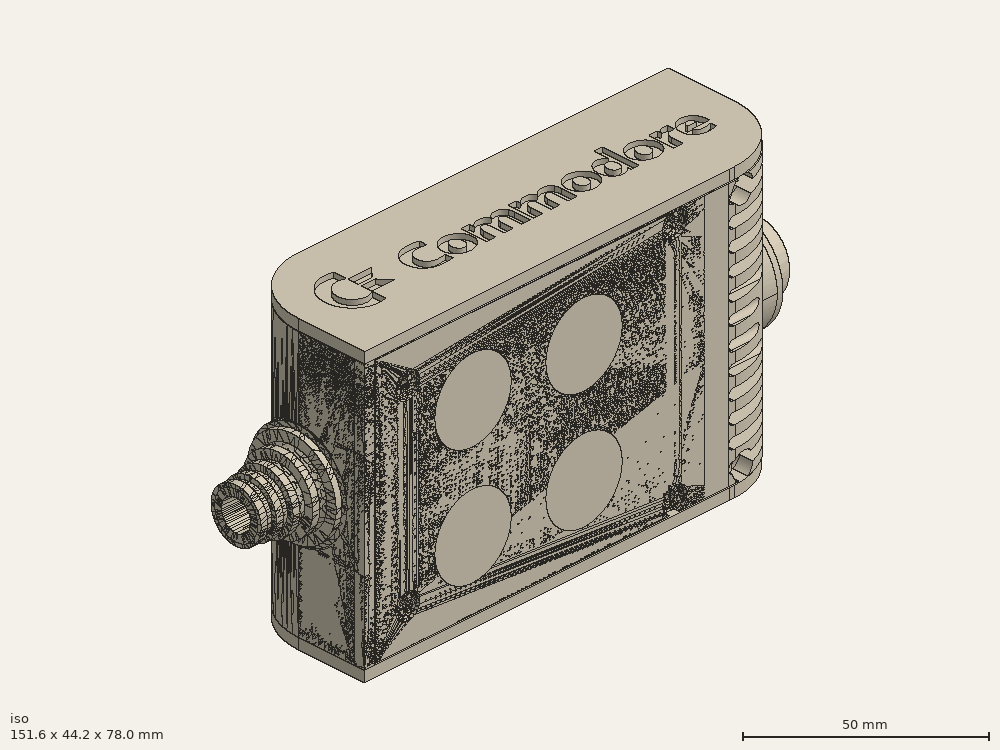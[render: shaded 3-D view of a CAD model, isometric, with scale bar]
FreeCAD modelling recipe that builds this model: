
FCSTD DOCUMENT  (FreeCAD 0.19R0.19.2)
Label: enclosure_210FCStd
License: All rights reserved
LicenseURL: http://en.wikipedia.org/wiki/All_rights_reserved
objects: Part::Revolution×152, Part::MultiFuse×146, Part::Feature×146, Sketcher::SketchObject×84, Part::Cut×72, Part::Cylinder×70, Part::Extrusion×69, Part::Fillet×58, Part::Box×36, App::MeasureDistance×4, Part::FeaturePython×2, Image::ImagePlane×1, PartDesign::Body×1, Part::Mirroring×1
note: 837 computed .brp shape members not serialized (recipe doc carries the construction recipe); baked Part::Feature solids carry a one-line shape summary decoded from their .brp

FEATURE [Sketcher::SketchObject] Sketch  label="topSketch"
  FullyConstrained = true
  sketch-geometry (20):
    g0: LineSegment StartX=5.21097e-06 StartY=3 StartZ=0 EndX=5.21097e-06 EndY=19 EndZ=0
    g1: ArcOfCircle CenterX=19 CenterY=19 CenterZ=0 NormalX=0 NormalY=0 NormalZ=1 AngleXU=0 Radius=19 StartAngle=1.5708 EndAngle=3.14159
    g2: ArcOfCircle CenterX=19 CenterY=19 CenterZ=0 NormalX=0 NormalY=0 NormalZ=1 AngleXU=0 Radius=16 StartAngle=1.5708 EndAngle=3.14159
    g3: LineSegment StartX=114 StartY=35 StartZ=0 EndX=19 EndY=35 EndZ=0
    g4: LineSegment StartX=5.21097e-06 StartY=3 StartZ=0 EndX=5.21097e-06 EndY=0 EndZ=0
    g5: LineSegment StartX=3 StartY=0 StartZ=0 EndX=5.21097e-06 EndY=0 EndZ=0
    g6: LineSegment StartX=3 StartY=19 StartZ=0 EndX=3 EndY=0 EndZ=0
    g7: LineSegment StartX=19 StartY=38 StartZ=0 EndX=124 EndY=38 EndZ=0
    g8: Circle CenterX=119 CenterY=35 CenterZ=0 NormalX=0 NormalY=0 NormalZ=1 AngleXU=0 Radius=1
    g9: Circle CenterX=121 CenterY=35 CenterZ=0 NormalX=0 NormalY=0 NormalZ=1 AngleXU=0 Radius=1
    g10: Circle CenterX=121 CenterY=33 CenterZ=0 NormalX=0 NormalY=0 NormalZ=1 AngleXU=0 Radius=1
    g11: BSplineCurve PolesCount=3 KnotsCount=2 Degree=2 IsPeriodic=0
    g12: GeomPoint X=119 Y=35 Z=0
    g13: GeomPoint X=121 Y=33 Z=0
    g14: LineSegment StartX=119 StartY=35 StartZ=0 EndX=114 EndY=35 EndZ=0
    g15: ArcOfCircle CenterX=105 CenterY=19 CenterZ=0 NormalX=0 NormalY=0 NormalZ=1 AngleXU=0 Radius=19 StartAngle=5.7297 EndAngle=6.28319
    g16: ArcOfCircle CenterX=105 CenterY=19 CenterZ=0 NormalX=0 NormalY=0 NormalZ=1 AngleXU=0 Radius=16 StartAngle=5.60905 EndAngle=6.28319
    g17: LineSegment StartX=121 StartY=33 StartZ=0 EndX=121 EndY=19 EndZ=0
    g18: LineSegment StartX=124 StartY=38 StartZ=0 EndX=124 EndY=19 EndZ=0
    g19: LineSegment StartX=117.5 StartY=9.01251 StartZ=0 EndX=121.163 EndY=9.0125 EndZ=0
  constraints (46):
    c: Vertical(g0)
    c: Block(g0)
    c: Coincident(g1,g0)
    c: Block(g1)
    c: Coincident(g2,g1)
    c: Block(g2)
    c: Coincident(g3,g2)
    c: Horizontal(g3)
    c: Tangent(g3,g2)
    c: Coincident(g4,g0)
    c: Distance(g4) = 3
    c: Vertical(g4)
    c: Coincident(g5,g4)
    c: Horizontal(g5)
    c: Coincident(g6,g2)
    c: Coincident(g6,g5)
    c: Vertical(g6)
    c: Horizontal(g7)
    c: Distance(g7) = 105
    c: Coincident(g7,g1)
    c: Block(g3)
    c: Weight(g8) = 1
    c: Equal(g8,g9)
    c: Equal(g8,g10)
    c: InternalAlignment(g8,g11)
    c: InternalAlignment(g9,g11)
    c: InternalAlignment(g10,g11)
    c: InternalAlignment(g12,g11)
    c: InternalAlignment(g13,g11)
    c: Block(g11)
    c: Coincident(g14,g11)
    c: Coincident(g14,g3)
    c: Horizontal(g14)
    c: Block(g15)
    c: Coincident(g16,g15)
    c: Block(g16)
    c: Coincident(g17,g11)
    c: Coincident(g17,g16)
    c: Vertical(g17)
    c: Distance(g17) = 14
    c: Coincident(g18,g7)
    c: Coincident(g18,g15)
    c: Vertical(g18)
    c: Distance(g18) = 19
    c: Coincident(g19,g16)
    c: Coincident(g19,g15)
FEATURE [Sketcher::SketchObject] Sketch001  label="bottomSketch"
  FullyConstrained = true
  sketch-geometry (32):
    g0: LineSegment StartX=3.3 StartY=-6.03275e-07 StartZ=0 EndX=98 EndY=-6.03275e-07 EndZ=0
    g1: ArcOfCircle CenterX=98 CenterY=19 CenterZ=0 NormalX=0 NormalY=0 NormalZ=1 AngleXU=0 Radius=19 StartAngle=4.71239 EndAngle=5.71103
    g2: LineSegment StartX=6.3 StartY=8 StartZ=0 EndX=3.3 EndY=8 EndZ=0
    g3: LineSegment StartX=3.3 StartY=8 StartZ=0 EndX=3.3 EndY=-6.03275e-07 EndZ=0
    g4: ArcOfCircle CenterX=8.3 CenterY=5 CenterZ=0 NormalX=0 NormalY=0 NormalZ=1 AngleXU=0 Radius=2 StartAngle=3.14159 EndAngle=4.71239
    g5: LineSegment StartX=6.3 StartY=8 StartZ=0 EndX=6.3 EndY=5 EndZ=0
    g6: ArcOfCircle CenterX=98 CenterY=19 CenterZ=0 NormalX=0 NormalY=0 NormalZ=1 AngleXU=0 Radius=12.7 StartAngle=4.71239 EndAngle=6.28319
    g7: LineSegment StartX=94.7 StartY=3 StartZ=0 EndX=8.3 EndY=3 EndZ=0
    g8-g12: Circle x5 (B-spline internal-alignment scaffolding for g13; pole/knot coordinates omitted)
    g13: BSplineCurve PolesCount=5 KnotsCount=3 Degree=3 IsPeriodic=0
    g14: GeomPoint X=98 Y=6.3 Z=0
    g15: GeomPoint X=96.3938 Y=4.71946 Z=0
    g16: GeomPoint X=94.7 Y=3 Z=0
    g17-g23: Circle x7 (B-spline internal-alignment scaffolding for g24; pole/knot coordinates omitted)
    g24: BSplineCurve PolesCount=7 KnotsCount=5 Degree=3 IsPeriodic=0
    g25-g29: GeomPoint x5 (B-spline internal-alignment scaffolding for g24; pole/knot coordinates omitted)
    g30: ArcOfCircle CenterX=98 CenterY=19 CenterZ=0 NormalX=0 NormalY=0 NormalZ=1 AngleXU=0 Radius=15.7 StartAngle=5.81226 EndAngle=6.28319
    g31: LineSegment StartX=110.7 StartY=19 StartZ=0 EndX=113.7 EndY=19 EndZ=0
  constraints (41):
    c: Horizontal(g0)
    c: Coincident(g1,g0)
    c: Block(g1)
    c: Horizontal(g2)
    c: Distance(g2) = 3
    c: Coincident(g3,g2)
    c: Vertical(g3)
    c: Coincident(g3,g0)
    c: Block(g4)
    c: Block(g2)
    c: Coincident(g5,g2)
    c: Coincident(g5,g4)
    c: Vertical(g5)
    c: Coincident(g6,g1)
    c: Block(g6)
    c: Coincident(g7,g4)
    c: Horizontal(g7)
    c: Block(g0)
    c: Block(g7)
    c: Block(g3)
    c: Coincident(g13,g6)
    c: Weight(g8) = 1
    c: Equal(g8, g9-g12) x4
    c: Coincident(g13,g7)
    c: InternalAlignment(g8-g12 -> g13) x5
    c: InternalAlignment(g14,g13)
    c: InternalAlignment(g15,g13)
    c: InternalAlignment(g16,g13)
    c: Block(g13)
    c: Weight(g17) = 1
    c: Equal(g17, g18-g23) x6
    c: Coincident(g24,g1)
    c: InternalAlignment(g17-g23 -> g24) x7
    c: InternalAlignment(g25-g29 -> g24) x5
    c: Block(g24)
    c: Coincident(g30,g24)
    c: Coincident(g31,g6)
    c: Coincident(g31,g30)
    c: Horizontal(g31)
    c: Block(g31)
    c: Block(g30)
FEATURE [Part::Extrusion] Extrude  label="top"
  Base = -> Sketch
  Dir = (0,0,1)
  DirMode = 2
  FaceMakerClass = Part::FaceMakerBullseye
  LengthFwd = 72
  LengthRev = 0
  Solid = true
  Symmetric = false
FEATURE [Part::Extrusion] Extrude001  label="bottom"
  Base = -> Sketch001
  Dir = (0,0,1)
  DirMode = 2
  FaceMakerClass = Part::FaceMakerBullseye
  LengthFwd = 71.4
  LengthRev = 0
  Placement = pos=(0,0,0.3) rot=(0,0,1;0rad)
  Solid = true
  Symmetric = false
FEATURE [Sketcher::SketchObject] Sketch002  label="topSketch001"
  FullyConstrained = true
  sketch-geometry (8):
    g0: ArcOfCircle CenterX=19 CenterY=19.0975 CenterZ=0 NormalX=0 NormalY=0 NormalZ=1 AngleXU=0 Radius=18.9025 StartAngle=1.5708 EndAngle=3.14674
    g1: LineSegment StartX=0.0977805 StartY=19.0003 StartZ=0 EndX=0.0977805 EndY=0.000251602 EndZ=0
    g2: LineSegment StartX=19 StartY=38 StartZ=0 EndX=124 EndY=38 EndZ=0
    g3: LineSegment StartX=0.0977805 StartY=0.000251602 StartZ=0 EndX=105.098 EndY=0.000251602 EndZ=0
    g4: LineSegment StartX=124 StartY=38 StartZ=0 EndX=125.616 EndY=38 EndZ=0
    g5: LineSegment StartX=105.098 StartY=0.000251602 StartZ=0 EndX=106.713 EndY=0.000251602 EndZ=0
    g6: ArcOfCircle CenterX=106.616 CenterY=19 CenterZ=0 NormalX=0 NormalY=0 NormalZ=1 AngleXU=0 Radius=19 StartAngle=4.71754 EndAngle=6.28319
    g7: LineSegment StartX=125.616 StartY=38 StartZ=0 EndX=125.616 EndY=19 EndZ=0
  constraints (21):
    c: Block(g0)
    c: Coincident(g1,g0)
    c: Vertical(g1)
    c: Horizontal(g2)
    c: Distance(g2) = 105
    c: Coincident(g2,g0)
    c: Distance(g1) = 19
    c: Coincident(g3,g1)
    c: Horizontal(g3)
    c: Distance(g3) = 105
    c: Coincident(g4,g2)
    c: Horizontal(g4)
    c: Distance(g4) = 1.61553
    c: Horizontal(g5)
    c: Equal(g4,g5) = 1.61553
    c: Coincident(g5,g3)
    c: Block(g6)
    c: Coincident(g6,g5)
    c: Coincident(g7,g4)
    c: Coincident(g7,g6)
    c: Vertical(g7)
FEATURE [Part::Extrusion] Extrude002  label="sideA"
  Base = -> Sketch002
  Dir = (0,0,1)
  DirMode = 2
  FaceMakerClass = Part::FaceMakerBullseye
  LengthFwd = 3
  LengthRev = 0
  Placement = pos=(0,0,-3) rot=(0,0,1;0rad)
  Solid = true
  Symmetric = false
FEATURE [Sketcher::SketchObject] Sketch003  label="topSketch002"
  FullyConstrained = true
  sketch-geometry (6):
    g0: LineSegment StartX=19 StartY=38 StartZ=0 EndX=117 EndY=38 EndZ=0
    g1: ArcOfCircle CenterX=19 CenterY=19 CenterZ=0 NormalX=0 NormalY=0 NormalZ=1 AngleXU=0 Radius=19 StartAngle=1.5708 EndAngle=3.14159
    g2: LineSegment StartX=117 StartY=38 StartZ=0 EndX=117 EndY=19 EndZ=0
    g3: LineSegment StartX=98 StartY=1.0161e-12 StartZ=0 EndX=5.22862e-06 EndY=1.0161e-12 EndZ=0
    g4: LineSegment StartX=5.22862e-06 StartY=19 StartZ=0 EndX=5.22862e-06 EndY=1.0161e-12 EndZ=0
    g5: ArcOfCircle CenterX=98 CenterY=19 CenterZ=0 NormalX=0 NormalY=0 NormalZ=1 AngleXU=0 Radius=19 StartAngle=4.71239 EndAngle=6.28319
  constraints (16):
    c: Horizontal(g0)
    c: Distance(g0) = 98
    c: Coincident(g1,g0)
    c: Block(g1)
    c: Coincident(g2,g0)
    c: Vertical(g2)
    c: Distance(g2) = 19
    c: Horizontal(g3)
    c: Coincident(g4,g1)
    c: Vertical(g4)
    c: Coincident(g3,g4)
    c: Block(g3)
    c: Coincident(g5,g2)
    c: Coincident(g5,g3)
    c: Block(g0)
    c: Block(g5)
FEATURE [Sketcher::SketchObject] Sketch004
  FullyConstrained = true
  MapMode = 3
  Placement = pos=(0,0,0) rot=(1,0,0;1.5708rad)
  Support = -> [Extrude]
  sketch-geometry (8):
    g0: Circle CenterX=80.351 CenterY=-67.6202 CenterZ=0 NormalX=0 NormalY=0 NormalZ=1 AngleXU=0 Radius=2
    g1: Circle CenterX=80.351 CenterY=-67.6202 CenterZ=0 NormalX=0 NormalY=0 NormalZ=1 AngleXU=0 Radius=3
    g2: Circle CenterX=80.351 CenterY=-4.92017 CenterZ=0 NormalX=0 NormalY=0 NormalZ=1 AngleXU=0 Radius=2
    g3: Circle CenterX=80.351 CenterY=-4.92017 CenterZ=0 NormalX=0 NormalY=0 NormalZ=1 AngleXU=0 Radius=3
    g4: Circle CenterX=23.851 CenterY=-4.92017 CenterZ=0 NormalX=0 NormalY=0 NormalZ=1 AngleXU=0 Radius=2
    g5: Circle CenterX=23.851 CenterY=-4.92017 CenterZ=0 NormalX=0 NormalY=0 NormalZ=1 AngleXU=0 Radius=3
    g6: Circle CenterX=23.851 CenterY=-67.6202 CenterZ=0 NormalX=0 NormalY=0 NormalZ=1 AngleXU=0 Radius=2
    g7: Circle CenterX=23.851 CenterY=-67.6202 CenterZ=0 NormalX=0 NormalY=0 NormalZ=1 AngleXU=0 Radius=3
  constraints (8):
    c: Block(g3)
    c: Block(g2)
    c: Block(g1)
    c: Block(g0)
    c: Block(g6)
    c: Block(g7)
    c: Block(g4)
    c: Block(g5)
FEATURE [Part::Extrusion] Extrude004
  Base = -> Sketch004
  Dir = (0,-1,2e-16)
  DirMode = 2
  FaceMakerClass = Part::FaceMakerBullseye
  LengthFwd = 6
  LengthRev = 0
  Placement = pos=(0,9,0) rot=(0,0,1;0rad)
  Solid = true
  Symmetric = false
FEATURE [Sketcher::SketchObject] Sketch005
  FullyConstrained = true
  MapMode = 3
  Placement = pos=(0,0,0) rot=(1,0,0;1.5708rad)
  Support = -> [Extrude]
  sketch-geometry (8):
    g0: Circle CenterX=80.351 CenterY=-67.6202 CenterZ=0 NormalX=0 NormalY=0 NormalZ=1 AngleXU=0 Radius=3
    g1: Circle CenterX=80.351 CenterY=-4.92017 CenterZ=0 NormalX=0 NormalY=0 NormalZ=1 AngleXU=0 Radius=3
    g2: Circle CenterX=23.851 CenterY=-4.92017 CenterZ=0 NormalX=0 NormalY=0 NormalZ=1 AngleXU=0 Radius=3
    g3: Circle CenterX=23.851 CenterY=-67.6202 CenterZ=0 NormalX=0 NormalY=0 NormalZ=1 AngleXU=0 Radius=3
    g4: Circle CenterX=23.851 CenterY=-67.6202 CenterZ=0 NormalX=0 NormalY=0 NormalZ=1 AngleXU=0 Radius=5
    g5: Circle CenterX=80.351 CenterY=-67.6202 CenterZ=0 NormalX=0 NormalY=0 NormalZ=1 AngleXU=0 Radius=5
    g6: Circle CenterX=23.851 CenterY=-4.92017 CenterZ=0 NormalX=0 NormalY=0 NormalZ=1 AngleXU=0 Radius=5
    g7: Circle CenterX=80.351 CenterY=-4.92017 CenterZ=0 NormalX=0 NormalY=0 NormalZ=1 AngleXU=0 Radius=5
  constraints (8):
    c: Block(g1)
    c: Block(g0)
    c: Block(g3)
    c: Block(g2)
    c: Block(g5)
    c: Block(g4)
    c: Block(g6)
    c: Block(g7)
FEATURE [Part::Extrusion] Extrude005
  Base = -> Sketch005
  Dir = (0,-1,2e-16)
  DirMode = 2
  FaceMakerClass = Part::FaceMakerBullseye
  LengthFwd = 2
  LengthRev = 0
  Solid = true
  Symmetric = false
FEATURE [Sketcher::SketchObject] Sketch006
  FullyConstrained = true
  MapMode = 3
  Placement = pos=(0,0,0) rot=(1,0,0;1.5708rad)
  sketch-geometry (8):
    g0: Circle CenterX=80.351 CenterY=-67.6202 CenterZ=0 NormalX=0 NormalY=0 NormalZ=1 AngleXU=0 Radius=3
    g1: Circle CenterX=80.351 CenterY=-4.92017 CenterZ=0 NormalX=0 NormalY=0 NormalZ=1 AngleXU=0 Radius=3
    g2: Circle CenterX=23.851 CenterY=-4.92017 CenterZ=0 NormalX=0 NormalY=0 NormalZ=1 AngleXU=0 Radius=3
    g3: Circle CenterX=23.851 CenterY=-67.6202 CenterZ=0 NormalX=0 NormalY=0 NormalZ=1 AngleXU=0 Radius=3
    g4: Circle CenterX=23.851 CenterY=-67.6202 CenterZ=0 NormalX=0 NormalY=0 NormalZ=1 AngleXU=0 Radius=5
    g5: Circle CenterX=80.351 CenterY=-67.6202 CenterZ=0 NormalX=0 NormalY=0 NormalZ=1 AngleXU=0 Radius=5
    g6: Circle CenterX=23.851 CenterY=-4.92017 CenterZ=0 NormalX=0 NormalY=0 NormalZ=1 AngleXU=0 Radius=5
    g7: Circle CenterX=80.351 CenterY=-4.92017 CenterZ=0 NormalX=0 NormalY=0 NormalZ=1 AngleXU=0 Radius=5
  constraints (8):
    c: Block(g1)
    c: Block(g0)
    c: Block(g3)
    c: Block(g2)
    c: Block(g5)
    c: Block(g4)
    c: Block(g6)
    c: Block(g7)
FEATURE [Part::Extrusion] Extrude007
  Base = -> Sketch006
  Dir = (0,-1,2e-16)
  DirMode = 2
  FaceMakerClass = Part::FaceMakerBullseye
  LengthFwd = 2
  LengthRev = 0
  Solid = true
  Symmetric = false
FEATURE [Part::Fillet] Fillet
  Base = -> Extrude007
  Edges = 4 edges r=1.99: [Edge6,Edge12,Edge18,Edge24]
FEATURE [Part::Cut] Cut
  Base = -> Extrude005
  Placement = pos=(0,5,0) rot=(0,0,1;0rad)
  Tool = -> Fillet
FEATURE [Part::MultiFuse] Fusion  label="pCBScrews"
  Placement = pos=(-2.5,0,72.3) rot=(0,0,1;0rad)
  Shapes = -> [Extrude004,Cut]
FEATURE [App::MeasureDistance] Distance  label="Distance: 0.69 mm"
  Distance = 0.685967
  P1 = (24.0138,2.9647,0.3)
  P2 = (23.8901,3,-0.373787)
FEATURE [App::MeasureDistance] Distance001  label="Distance: 0.53 mm"
  Distance = 0.533607
  P1 = (80.2939,3,72.2334)
  P2 = (80.281,2.99661,71.7)
FEATURE [Part::Fillet] Fillet001
  Base = -> Extrude001
  Edges = 1 edges r=2.4: [Edge17]
FEATURE [Part::Fillet] Fillet002  label="bottom001"
  Base = -> Fillet001
  Edges = 1 edges r=2.4: [Edge36]
FEATURE [Part::Fillet] Fillet003  label="top001"
  Base = -> Extrude
  Edges = 1 edges r=2: [Edge1]
FEATURE [Sketcher::SketchObject] Sketch007
  FullyConstrained = true
  sketch-geometry (16):
    g0: LineSegment StartX=4 StartY=0 StartZ=0 EndX=4 EndY=2.4 EndZ=0
    g1: LineSegment StartX=4 StartY=2.4 StartZ=0 EndX=7 EndY=2.4 EndZ=0
    g2: LineSegment StartX=4 StartY=0 StartZ=0 EndX=5.7 EndY=0 EndZ=0
    g3: LineSegment StartX=5.7 StartY=0 StartZ=0 EndX=5.7 EndY=-5.6 EndZ=0
    g4-g8: Circle x5 (B-spline internal-alignment scaffolding for g9; pole/knot coordinates omitted)
    g9: BSplineCurve PolesCount=5 KnotsCount=3 Degree=3 IsPeriodic=0
    g10: GeomPoint X=7 Y=2.4 Z=0
    g11: GeomPoint X=10.4582 Y=-1.55472 Z=0
    g12: GeomPoint X=14 Y=-5.6 Z=0
    g13: LineSegment StartX=14 StartY=-5.6 StartZ=0 EndX=14 EndY=-14.1 EndZ=0
    g14: LineSegment StartX=14 StartY=-14.1 StartZ=0 EndX=6.5 EndY=-14.1 EndZ=0
    g15: LineSegment StartX=5.7 StartY=-5.6 StartZ=0 EndX=6.5 EndY=-14.1 EndZ=0
  constraints (28):
    c: Distance(g0) = 2.4
    c: Vertical(g0)
    c: Block(g0)
    c: Coincident(g1,g0)
    c: Horizontal(g1)
    c: Distance(g1) = 3
    c: Coincident(g2,g0)
    c: Horizontal(g2)
    c: Distance(g2) = 1.7
    c: Coincident(g3,g2)
    c: Vertical(g3)
    c: Distance(g3) = 5.6
    c: Coincident(g9,g1)
    c: Weight(g4) = 1
    c: Equal(g4, g5-g8) x4
    c: InternalAlignment(g4-g8 -> g9) x5
    c: InternalAlignment(g10,g9)
    c: InternalAlignment(g11,g9)
    c: InternalAlignment(g12,g9)
    c: Block(g9)
    c: Coincident(g13,g9)
    c: Vertical(g13)
    c: Distance(g13) = 8.5
    c: Coincident(g14,g13)
    c: Horizontal(g14)
    c: Distance(g14) = 7.5
    c: Coincident(g15,g3)
    c: Coincident(g15,g14)
FEATURE [Part::Feature] Face
  shape: bbox 10 x 16.5 x 2e-07 mm, 1 faces, 0 solids (baked)
FEATURE [Part::Revolution] Revolve  label="plugHousing"
  Angle = 360
  Axis = (0,1,0)
  Base = (0,0,0)
  FaceMakerClass = Part::FaceMakerBullseye
  Placement = pos=(0,0,36.15) rot=(0,0,1;0rad)
  Solid = false
  Source = -> Face
  Symmetric = false
FEATURE [Part::Feature] Face001
  shape: bbox 10 x 16.5 x 2e-07 mm, 1 faces, 0 solids (baked)
FEATURE [Part::Revolution] Revolve001  label="plugHousing001"
  Angle = 360
  Axis = (0,1,0)
  Base = (0,0,0)
  FaceMakerClass = Part::FaceMakerBullseye
  Placement = pos=(0,0,36.15) rot=(0,0,1;0rad)
  Solid = false
  Source = -> Face001
  Symmetric = false
FEATURE [Part::MultiFuse] Fusion001  label="plugHousing002"
  Placement = pos=(0,0,0) rot=(0,0,1;1.5708rad)
  Shapes = -> [Revolve001,Revolve]
FEATURE [Part::Feature] Face002
  shape: bbox 10 x 16.5 x 2e-07 mm, 1 faces, 0 solids (baked)
FEATURE [Part::Revolution] Revolve003  label="plugHousing005"
  Angle = 360
  Axis = (0,1,0)
  Base = (0,0,0)
  FaceMakerClass = Part::FaceMakerBullseye
  Placement = pos=(0,0,36.15) rot=(0,0,1;0rad)
  Solid = false
  Source = -> Face002
  Symmetric = false
FEATURE [Part::Feature] Face003
  shape: bbox 10 x 16.5 x 2e-07 mm, 1 faces, 0 solids (baked)
FEATURE [Part::Revolution] Revolve002  label="plugHousing003"
  Angle = 360
  Axis = (0,1,0)
  Base = (0,0,0)
  FaceMakerClass = Part::FaceMakerBullseye
  Placement = pos=(0,0,36.15) rot=(0,0,1;0rad)
  Solid = false
  Source = -> Face003
  Symmetric = false
FEATURE [Part::MultiFuse] Fusion002  label="plugHousing004"
  Placement = pos=(0,0,0) rot=(0,0,1;1.5708rad)
  Shapes = -> [Revolve002,Revolve003]
FEATURE [Part::MultiFuse] Fusion003  label="plugHousing006"
  Placement = pos=(0,19,0) rot=(0,0,1;3.14159rad)
  Shapes = -> [Fusion002,Fusion001]
FEATURE [Part::Feature] Face004
  shape: bbox 10 x 16.5 x 2e-07 mm, 1 faces, 0 solids (baked)
FEATURE [Part::Revolution] Revolve006  label="plugHousing010"
  Angle = 360
  Axis = (0,1,0)
  Base = (0,0,0)
  FaceMakerClass = Part::FaceMakerBullseye
  Placement = pos=(0,0,36.15) rot=(0,0,1;0rad)
  Solid = false
  Source = -> Face004
  Symmetric = false
FEATURE [Part::Feature] Face005
  shape: bbox 10 x 16.5 x 2e-07 mm, 1 faces, 0 solids (baked)
FEATURE [Part::Revolution] Revolve007  label="plugHousing011"
  Angle = 360
  Axis = (0,1,0)
  Base = (0,0,0)
  FaceMakerClass = Part::FaceMakerBullseye
  Placement = pos=(0,0,36.15) rot=(0,0,1;0rad)
  Solid = false
  Source = -> Face005
  Symmetric = false
FEATURE [Part::Feature] Face006
  shape: bbox 10 x 16.5 x 2e-07 mm, 1 faces, 0 solids (baked)
FEATURE [Part::Revolution] Revolve004  label="plugHousing007"
  Angle = 360
  Axis = (0,1,0)
  Base = (0,0,0)
  FaceMakerClass = Part::FaceMakerBullseye
  Placement = pos=(0,0,36.15) rot=(0,0,1;0rad)
  Solid = false
  Source = -> Face006
  Symmetric = false
FEATURE [Part::MultiFuse] Fusion004  label="plugHousing009"
  Placement = pos=(0,0,0) rot=(0,0,1;1.5708rad)
  Shapes = -> [Revolve004,Revolve007]
FEATURE [Part::Feature] Face007
  shape: bbox 10 x 16.5 x 2e-07 mm, 1 faces, 0 solids (baked)
FEATURE [Part::Revolution] Revolve005  label="plugHousing008"
  Angle = 360
  Axis = (0,1,0)
  Base = (0,0,0)
  FaceMakerClass = Part::FaceMakerBullseye
  Placement = pos=(0,0,36.15) rot=(0,0,1;0rad)
  Solid = false
  Source = -> Face007
  Symmetric = false
FEATURE [Part::MultiFuse] Fusion005  label="plugHousing012"
  Placement = pos=(0,0,0) rot=(0,0,1;1.5708rad)
  Shapes = -> [Revolve006,Revolve005]
FEATURE [Part::MultiFuse] Fusion006  label="plugHousing013"
  Placement = pos=(0,19,0) rot=(0,0,1;3.14159rad)
  Shapes = -> [Fusion005,Fusion004]
FEATURE [Part::MultiFuse] Fusion007  label="plugHousing014"
  Placement = pos=(122.621,0,-0.15) rot=(0,0,1;0rad)
  Shapes = -> [Fusion003,Fusion006]
FEATURE [Part::Cylinder] Cylinder002
  Angle = 360
  AttacherType = Attacher::AttachEngine3D
  Height = 20
  Placement = pos=(0,0,36.15) rot=(0,0,1;0rad)
  Radius = 4
FEATURE [Part::Cylinder] Cylinder003
  Angle = 360
  AttacherType = Attacher::AttachEngine3D
  Height = 10
  Placement = pos=(0,0,36.15) rot=(0,0,1;0rad)
  Radius = 4
FEATURE [Part::MultiFuse] Fusion009  label="removeToCreateHoleForPlugHousing"
  Placement = pos=(70,19,36.15) rot=(0,1,0;1.5708rad)
  Shapes = -> [Cylinder002,Cylinder003]
FEATURE [Part::Cylinder] Cylinder004
  Angle = 360
  AttacherType = Attacher::AttachEngine3D
  Height = 20
  Placement = pos=(0,0,36.15) rot=(0,0,1;0rad)
  Radius = 4
FEATURE [Part::Cylinder] Cylinder005
  Angle = 360
  AttacherType = Attacher::AttachEngine3D
  Height = 10
  Placement = pos=(0,0,36.15) rot=(0,0,1;0rad)
  Radius = 4
FEATURE [Part::MultiFuse] Fusion010  label="removeToCreateHoleForPlugHousing001"
  Placement = pos=(70,19,36.15) rot=(0,1,0;1.5708rad)
  Shapes = -> [Cylinder004,Cylinder005]
FEATURE [Part::Cut] Cut001
  Base = -> Fillet003
  Tool = -> Fusion010
FEATURE [Part::Cut] Cut002  label="Bottom"
  Base = -> Fillet002
  Tool = -> Fusion009
FEATURE [Part::Feature] Face008
  shape: bbox 10 x 16.5 x 2e-07 mm, 1 faces, 0 solids (baked)
FEATURE [Part::Revolution] Revolve011  label="plugHousing021"
  Angle = 360
  Axis = (0,1,0)
  Base = (0,0,0)
  FaceMakerClass = Part::FaceMakerBullseye
  Placement = pos=(0,0,36.15) rot=(0,0,1;0rad)
  Solid = false
  Source = -> Face008
  Symmetric = false
FEATURE [Part::Feature] Face009
  shape: bbox 10 x 16.5 x 2e-07 mm, 1 faces, 0 solids (baked)
FEATURE [Part::Revolution] Revolve012  label="plugHousing022"
  Angle = 360
  Axis = (0,1,0)
  Base = (0,0,0)
  FaceMakerClass = Part::FaceMakerBullseye
  Placement = pos=(0,0,36.15) rot=(0,0,1;0rad)
  Solid = false
  Source = -> Face009
  Symmetric = false
FEATURE [Part::Feature] Face010 .. Face013  x4 (patterned run collapsed; names and placements below)
  shape: bbox 10 x 16.5 x 2e-07 mm, 1 faces, 0 solids (baked)
FEATURE [Part::Revolution] Revolve015  label="plugHousing027"
  Angle = 360
  Axis = (0,1,0)
  Base = (0,0,0)
  FaceMakerClass = Part::FaceMakerBullseye
  Placement = pos=(0,0,36.15) rot=(0,0,1;0rad)
  Solid = false
  Source = -> Face013
  Symmetric = false
FEATURE [Part::Feature] Face014
  shape: bbox 10 x 16.5 x 2e-07 mm, 1 faces, 0 solids (baked)
FEATURE [Part::Feature] Face015
  shape: bbox 10 x 16.5 x 2e-07 mm, 1 faces, 0 solids (baked)
FEATURE [Part::Feature] Face016
  shape: bbox 10 x 16.5 x 2e-07 mm, 1 faces, 0 solids (baked)
FEATURE [Part::Revolution] Revolve019  label="plugHousing033"
  Angle = 360
  Axis = (0,1,0)
  Base = (0,0,0)
  FaceMakerClass = Part::FaceMakerBullseye
  Placement = pos=(0,0,36.15) rot=(0,0,1;0rad)
  Solid = false
  Source = -> Face016
  Symmetric = false
FEATURE [Part::Feature] Face017
  shape: bbox 10 x 16.5 x 2e-07 mm, 1 faces, 0 solids (baked)
FEATURE [Part::Revolution] Revolve020  label="plugHousing034"
  Angle = 360
  Axis = (0,1,0)
  Base = (0,0,0)
  FaceMakerClass = Part::FaceMakerBullseye
  Placement = pos=(0,0,36.15) rot=(0,0,1;0rad)
  Solid = false
  Source = -> Face017
  Symmetric = false
FEATURE [Part::Feature] Face018
  shape: bbox 10 x 16.5 x 2e-07 mm, 1 faces, 0 solids (baked)
FEATURE [Part::Revolution] Revolve016  label="plugHousing030"
  Angle = 360
  Axis = (0,1,0)
  Base = (0,0,0)
  FaceMakerClass = Part::FaceMakerBullseye
  Placement = pos=(0,0,36.15) rot=(0,0,1;0rad)
  Solid = false
  Source = -> Face018
  Symmetric = false
FEATURE [Part::MultiFuse] Fusion020  label="plugHousing038"
  Placement = pos=(0,0,0) rot=(0,0,1;1.5708rad)
  Shapes = -> [Revolve016,Revolve020]
FEATURE [Part::Feature] Face019
  shape: bbox 10 x 16.5 x 2e-07 mm, 1 faces, 0 solids (baked)
FEATURE [Part::Feature] Face020
  shape: bbox 10 x 16.5 x 2e-07 mm, 1 faces, 0 solids (baked)
FEATURE [Part::Revolution] Revolve017  label="plugHousing031"
  Angle = 360
  Axis = (0,1,0)
  Base = (0,0,0)
  FaceMakerClass = Part::FaceMakerBullseye
  Placement = pos=(0,0,36.15) rot=(0,0,1;0rad)
  Solid = false
  Source = -> Face020
  Symmetric = false
FEATURE [Part::MultiFuse] Fusion021  label="plugHousing039"
  Placement = pos=(0,0,0) rot=(0,0,1;1.5708rad)
  Shapes = -> [Revolve019,Revolve017]
FEATURE [Part::MultiFuse] Fusion023  label="plugHousing041"
  Placement = pos=(0,19,0) rot=(0,0,1;3.14159rad)
  Shapes = -> [Fusion021,Fusion020]
FEATURE [Part::Revolution] Revolve022  label="plugHousing043"
  Angle = 360
  Axis = (0,1,0)
  Base = (0,0,0)
  FaceMakerClass = Part::FaceMakerBullseye
  Placement = pos=(0,0,36.15) rot=(0,0,1;0rad)
  Solid = false
  Source = -> Face019
  Symmetric = false
FEATURE [Part::Feature] Face021
  shape: bbox 10 x 16.5 x 2e-07 mm, 1 faces, 0 solids (baked)
FEATURE [Part::Revolution] Revolve023  label="plugHousing044"
  Angle = 360
  Axis = (0,1,0)
  Base = (0,0,0)
  FaceMakerClass = Part::FaceMakerBullseye
  Placement = pos=(0,0,36.15) rot=(0,0,1;0rad)
  Solid = false
  Source = -> Face021
  Symmetric = false
FEATURE [Part::Feature] Face022
  shape: bbox 10 x 16.5 x 2e-07 mm, 1 faces, 0 solids (baked)
FEATURE [Part::Revolution] Revolve018  label="plugHousing032"
  Angle = 360
  Axis = (0,1,0)
  Base = (0,0,0)
  FaceMakerClass = Part::FaceMakerBullseye
  Placement = pos=(0,0,36.15) rot=(0,0,1;0rad)
  Solid = false
  Source = -> Face022
  Symmetric = false
FEATURE [Part::MultiFuse] Fusion022  label="plugHousing040"
  Placement = pos=(0,0,0) rot=(0,0,1;1.5708rad)
  Shapes = -> [Revolve018,Revolve023]
FEATURE [Part::Feature] Face023
  shape: bbox 10 x 16.5 x 2e-07 mm, 1 faces, 0 solids (baked)
FEATURE [Part::Revolution] Revolve021  label="plugHousing035"
  Angle = 360
  Axis = (0,1,0)
  Base = (0,0,0)
  FaceMakerClass = Part::FaceMakerBullseye
  Placement = pos=(0,0,36.15) rot=(0,0,1;0rad)
  Solid = false
  Source = -> Face023
  Symmetric = false
FEATURE [Part::MultiFuse] Fusion018  label="plugHousing036"
  Placement = pos=(0,0,0) rot=(0,0,1;1.5708rad)
  Shapes = -> [Revolve022,Revolve021]
FEATURE [Part::MultiFuse] Fusion019  label="plugHousing037"
  Placement = pos=(0,19,0) rot=(0,0,1;3.14159rad)
  Shapes = -> [Fusion018,Fusion022]
FEATURE [Part::MultiFuse] Fusion024  label="plugHousing042"
  Placement = pos=(122.621,0,-0.15) rot=(0,0,1;0rad)
  Shapes = -> [Fusion023,Fusion019]
FEATURE [Part::Cylinder] Cylinder006
  Angle = 360
  AttacherType = Attacher::AttachEngine3D
  Height = 20
  Placement = pos=(0,0,36.15) rot=(0,0,1;0rad)
  Radius = 14.3
FEATURE [Part::Cylinder] Cylinder007
  Angle = 360
  AttacherType = Attacher::AttachEngine3D
  Height = 10
  Placement = pos=(0,0,36.15) rot=(0,0,1;0rad)
  Radius = 4
FEATURE [Part::MultiFuse] Fusion026  label="removeToCreteHoleForPlugHousing"
  Placement = pos=(70,19,36) rot=(0,1,0;1.5708rad)
  Shapes = -> [Cylinder006,Cylinder007]
FEATURE [Part::Box] Box001  label="Cube001"
  AttacherType = Attacher::AttachEngine3D
  Height = 28
  Length = 3
  Placement = pos=(110.7,19,22) rot=(0,0,1;0rad)
  Width = 15.7
FEATURE [Part::Cut] Cut003  label="top002"
  Base = -> Cut001
  Tool = -> Fusion007
FEATURE [Part::Revolution] Revolve008  label="plugHousing015"
  Angle = 360
  Axis = (0,1,0)
  Base = (0,0,0)
  FaceMakerClass = Part::FaceMakerBullseye
  Placement = pos=(0,0,36.15) rot=(0,0,1;0rad)
  Solid = false
  Source = -> Face010
  Symmetric = false
FEATURE [Part::MultiFuse] Fusion013  label="plugHousing020"
  Placement = pos=(0,0,0) rot=(0,0,1;1.5708rad)
  Shapes = -> [Revolve008,Revolve012]
FEATURE [Part::Cut] Cut004  label="top003"
  Base = -> Cut003
  Placement = pos=(1,0,0) rot=(0,0,1;0rad)
  Tool = -> Fusion026
FEATURE [Part::Cylinder] Cylinder008
  Angle = 360
  AttacherType = Attacher::AttachEngine3D
  Height = 20
  Placement = pos=(0,0,36.15) rot=(0,0,1;0rad)
  Radius = 10.3
FEATURE [Part::Cylinder] Cylinder009
  Angle = 360
  AttacherType = Attacher::AttachEngine3D
  Height = 10
  Placement = pos=(0,0,36.15) rot=(0,0,1;0rad)
  Radius = 4
FEATURE [Part::MultiFuse] Fusion027  label="removeToCreteHoleForPlugHousing001"
  Placement = pos=(70,19,36) rot=(0,1,0;1.5708rad)
  Shapes = -> [Cylinder008,Cylinder009]
FEATURE [Part::Cut] Cut005  label="plugHousingTab"
  Base = -> Box001
  Tool = -> Fusion027
FEATURE [Part::MultiFuse] Fusion028  label="plugHousing045"
  Shapes = -> [Fusion024,Cut005]
FEATURE [Part::Box] Box002  label="Cube002"
  AttacherType = Attacher::AttachEngine3D
  Height = 28.8
  Length = 3
  Placement = pos=(107.3,28,21.6) rot=(0,0,1;0rad)
  Width = 7
FEATURE [Part::Box] Box003  label="Cube003"
  AttacherType = Attacher::AttachEngine3D
  Height = 3
  Length = 6.4
  Placement = pos=(107.3,28,18.6) rot=(0,0,1;0rad)
  Width = 7
FEATURE [Part::Box] Box004  label="Cube004"
  AttacherType = Attacher::AttachEngine3D
  Height = 3
  Length = 6.4
  Placement = pos=(107.3,28,50.4) rot=(0,0,1;0rad)
  Width = 7
FEATURE [Part::MultiFuse] Fusion029  label="plugHousingBracketHolder"
  Shapes = -> [Box004,Box002,Box003]
FEATURE [Part::Cylinder] Cylinder010
  Angle = 360
  AttacherType = Attacher::AttachEngine3D
  Height = 20
  Placement = pos=(0,0,36.15) rot=(0,0,1;0rad)
  Radius = 14.3
FEATURE [Part::Cylinder] Cylinder011
  Angle = 360
  AttacherType = Attacher::AttachEngine3D
  Height = 10
  Placement = pos=(0,0,36.15) rot=(0,0,1;0rad)
  Radius = 4
FEATURE [Part::MultiFuse] Fusion030  label="removeToCreteHoleForPlugHousing002"
  Placement = pos=(70,19,36) rot=(0,1,0;1.5708rad)
  Shapes = -> [Cylinder010,Cylinder011]
FEATURE [Part::Cut] Cut006  label="plugHousingBracketHolder001"
  Base = -> Fusion029
  Tool = -> Fusion030
FEATURE [Part::Cylinder] Cylinder012
  Angle = 360
  AttacherType = Attacher::AttachEngine3D
  Height = 20
  Placement = pos=(0,0,36.15) rot=(0,0,1;0rad)
  Radius = 7
FEATURE [Part::Cylinder] Cylinder013
  Angle = 360
  AttacherType = Attacher::AttachEngine3D
  Height = 10
  Placement = pos=(0,0,36.15) rot=(0,0,1;0rad)
  Radius = 4
FEATURE [Part::MultiFuse] Fusion032  label="removeToCreteHoleForPlugHousing003"
  Placement = pos=(70,19,36) rot=(0,1,0;1.5708rad)
  Shapes = -> [Cylinder012,Cylinder013]
FEATURE [Part::Cut] Cut007  label="bottom002"
  Base = -> Cut002
  Tool = -> Fusion032
FEATURE [Sketcher::SketchObject] Sketch008
  FullyConstrained = true
  sketch-geometry (54):
    g0: LineSegment StartX=-4.2 StartY=0 StartZ=0 EndX=-6.2 EndY=0 EndZ=0
    g1: LineSegment StartX=-14 StartY=-18 StartZ=0 EndX=-14 EndY=-26.5 EndZ=0
    g2: LineSegment StartX=-4.2 StartY=0 StartZ=0 EndX=-4.2 EndY=-13.4877 EndZ=0
    g3: Circle CenterX=-4.2 CenterY=-13.4877 CenterZ=0 NormalX=0 NormalY=0 NormalZ=1 AngleXU=0 Radius=1
    g4: Circle CenterX=-4.2 CenterY=-26.5 CenterZ=0 NormalX=0 NormalY=0 NormalZ=1 AngleXU=0 Radius=1
    g5: Circle CenterX=-8.2 CenterY=-26.5 CenterZ=0 NormalX=0 NormalY=0 NormalZ=1 AngleXU=0 Radius=1
    g6: BSplineCurve PolesCount=3 KnotsCount=2 Degree=2 IsPeriodic=0
    g7: GeomPoint X=-4.2 Y=-13.4877 Z=0
    g8: GeomPoint X=-8.2 Y=-26.5 Z=0
    g9: LineSegment StartX=-14 StartY=-26.5 StartZ=0 EndX=-8.2 EndY=-26.5 EndZ=0
    g10: LineSegment StartX=-10.15 StartY=-12 StartZ=0 EndX=-10.15 EndY=-14 EndZ=0
    g11: LineSegment StartX=-12.8401 StartY=-16 StartZ=0 EndX=-10.1571 EndY=-16 EndZ=0
    g12: LineSegment StartX=-10.15 StartY=-14 StartZ=0 EndX=-8.70761 EndY=-14 EndZ=0
    g13: LineSegment StartX=-12.8401 StartY=-16 StartZ=0 EndX=-12.8401 EndY=-17.6958 EndZ=0
    g14: LineSegment StartX=-10.15 StartY=-12 StartZ=0 EndX=-7.79258 EndY=-12 EndZ=0
    g15: Circle CenterX=-6.2215 CenterY=-2 CenterZ=0 NormalX=0 NormalY=0 NormalZ=1 AngleXU=0 Radius=1
    g16: Circle CenterX=-6.22762 CenterY=-2.58724 CenterZ=0 NormalX=0 NormalY=0 NormalZ=1 AngleXU=0 Radius=1
    g17: Circle CenterX=-6.32538 CenterY=-4 CenterZ=0 NormalX=0 NormalY=0 NormalZ=1 AngleXU=0 Radius=1
    g18: BSplineCurve PolesCount=3 KnotsCount=2 Degree=2 IsPeriodic=0
    g19: GeomPoint X=-6.2215 Y=-2 Z=0
    g20: GeomPoint X=-6.32538 Y=-4 Z=0
    g21: Circle CenterX=-6.48644 CenterY=-5.99526 CenterZ=0 NormalX=0 NormalY=0 NormalZ=1 AngleXU=0 Radius=1
    g22: Circle CenterX=-6.58486 CenterY=-6.99526 CenterZ=0 NormalX=0 NormalY=0 NormalZ=1 AngleXU=0 Radius=1
    g23: Circle CenterX=-6.77343 CenterY=-8 CenterZ=0 NormalX=0 NormalY=0 NormalZ=1 AngleXU=0 Radius=1
    g24: BSplineCurve PolesCount=3 KnotsCount=2 Degree=2 IsPeriodic=0
    g25: GeomPoint X=-6.48644 Y=-5.99526 Z=0
    g26: GeomPoint X=-6.77343 Y=-8 Z=0
    g27: Circle CenterX=-7.19003 CenterY=-10 CenterZ=0 NormalX=0 NormalY=0 NormalZ=1 AngleXU=0 Radius=1
    g28: Circle CenterX=-7.44407 CenterY=-11.0915 CenterZ=0 NormalX=0 NormalY=0 NormalZ=1 AngleXU=0 Radius=1
    g29: Circle CenterX=-7.79258 CenterY=-12 CenterZ=0 NormalX=0 NormalY=0 NormalZ=1 AngleXU=0 Radius=1
    g30: BSplineCurve PolesCount=3 KnotsCount=2 Degree=2 IsPeriodic=0
    g31: GeomPoint X=-7.19003 Y=-10 Z=0
    g32: GeomPoint X=-7.79258 Y=-12 Z=0
    g33: Circle CenterX=-8.70761 CenterY=-14 CenterZ=0 NormalX=0 NormalY=0 NormalZ=1 AngleXU=0 Radius=1
    g34: Circle CenterX=-9.33087 CenterY=-15.1837 CenterZ=0 NormalX=0 NormalY=0 NormalZ=1 AngleXU=0 Radius=1
    g35: Circle CenterX=-10.1571 CenterY=-16 CenterZ=0 NormalX=0 NormalY=0 NormalZ=1 AngleXU=0 Radius=1
    g36: BSplineCurve PolesCount=3 KnotsCount=2 Degree=2 IsPeriodic=0
    g37: GeomPoint X=-8.70761 Y=-14 Z=0
    g38: GeomPoint X=-10.1571 Y=-16 Z=0
    g39: Circle CenterX=-12.8401 CenterY=-17.6958 CenterZ=0 NormalX=0 NormalY=0 NormalZ=1 AngleXU=0 Radius=1
    g40: Circle CenterX=-13.3521 CenterY=-17.9027 CenterZ=0 NormalX=0 NormalY=0 NormalZ=1 AngleXU=0 Radius=1
    g41: Circle CenterX=-14 CenterY=-18 CenterZ=0 NormalX=0 NormalY=0 NormalZ=1 AngleXU=0 Radius=1
    g42: BSplineCurve PolesCount=3 KnotsCount=2 Degree=2 IsPeriodic=0
    g43: GeomPoint X=-12.8401 Y=-17.6958 Z=0
    g44: GeomPoint X=-14 Y=-18 Z=0
    g45: LineSegment StartX=-6.2 StartY=0 StartZ=0 EndX=-7.2 EndY=0 EndZ=0
    g46: LineSegment StartX=-7.2 StartY=0 StartZ=0 EndX=-7.2 EndY=-2 EndZ=0
    g47: LineSegment StartX=-7.2 StartY=-2 StartZ=0 EndX=-6.2215 EndY=-2 EndZ=0
    g48: LineSegment StartX=-6.32538 StartY=-4 StartZ=0 EndX=-7.65538 EndY=-4 EndZ=0
    g49: LineSegment StartX=-7.65538 StartY=-4 StartZ=0 EndX=-7.65538 EndY=-5.99526 EndZ=0
    g50: LineSegment StartX=-7.65538 StartY=-5.99526 StartZ=0 EndX=-6.48644 EndY=-5.99526 EndZ=0
    g51: LineSegment StartX=-6.77343 StartY=-8 StartZ=0 EndX=-8.43343 EndY=-8 EndZ=0
    g52: LineSegment StartX=-8.43343 StartY=-8 StartZ=0 EndX=-8.43343 EndY=-10 EndZ=0
    g53: LineSegment StartX=-8.43343 StartY=-10 StartZ=0 EndX=-7.19003 EndY=-10 EndZ=0
  constraints (112):
    c: Horizontal(g0)
    c: Distance(g0) = 2
    c: Block(g0)
    c: Vertical(g1)
    c: Coincident(g2,g0)
    c: Vertical(g2)
    c: Block(g2)
    c: Coincident(g6,g2)
    c: Weight(g3) = 1
    c: Equal(g3,g4)
    c: Equal(g3,g5)
    c: InternalAlignment(g3,g6)
    c: InternalAlignment(g4,g6)
    c: InternalAlignment(g5,g6)
    c: InternalAlignment(g7,g6)
    c: InternalAlignment(g8,g6)
    c: Block(g6)
    c: Coincident(g9,g1)
    c: Coincident(g9,g6)
    c: Horizontal(g9)
    c: Vertical(g10)
    c: Block(g10)
    c: Horizontal(g11)
    c: Block(g11)
    c: Coincident(g12,g10)
    c: Horizontal(g12)
    c: Block(g12)
    c: Coincident(g13,g11)
    c: Vertical(g13)
    c: Block(g13)
    c: Coincident(g14,g10)
    c: Horizontal(g14)
    c: Block(g14)
    c: Block(g9)
    c: Block(g1)
    c: Weight(g15) = 1
    c: Equal(g15,g16)
    c: Equal(g15,g17)
    c: InternalAlignment(g15,g18)
    c: InternalAlignment(g16,g18)
    c: InternalAlignment(g17,g18)
    c: InternalAlignment(g19,g18)
    c: InternalAlignment(g20,g18)
    c: Weight(g21) = 1
    c: Equal(g21,g22)
    c: Equal(g21,g23)
    c: InternalAlignment(g21,g24)
    c: InternalAlignment(g22,g24)
    c: InternalAlignment(g23,g24)
    c: InternalAlignment(g25,g24)
    c: InternalAlignment(g26,g24)
    c: Weight(g27) = 1
    c: Equal(g27,g28)
    c: Equal(g27,g29)
    c: Coincident(g30,g14)
    c: InternalAlignment(g27,g30)
    c: InternalAlignment(g28,g30)
    c: InternalAlignment(g29,g30)
    c: InternalAlignment(g31,g30)
    c: InternalAlignment(g32,g30)
    c: Coincident(g36,g12)
    c: Weight(g33) = 1
    c: Equal(g33,g34)
    c: Equal(g33,g35)
    c: Coincident(g36,g11)
    c: InternalAlignment(g33,g36)
    c: InternalAlignment(g34,g36)
    c: InternalAlignment(g35,g36)
    c: InternalAlignment(g37,g36)
    c: InternalAlignment(g38,g36)
    c: Coincident(g42,g13)
    c: Weight(g39) = 1
    c: Equal(g39,g40)
    c: Equal(g39,g41)
    c: Coincident(g42,g1)
    c: InternalAlignment(g39,g42)
    c: InternalAlignment(g40,g42)
    c: InternalAlignment(g41,g42)
    c: InternalAlignment(g43,g42)
    c: InternalAlignment(g44,g42)
    c: Block(g18)
    c: Block(g24)
    c: Block(g30)
    c: Block(g36)
    c: Block(g42)
    c: Horizontal(g45)
    c: Coincident(g45,g0)
    c: Vertical(g46)
    c: Coincident(g46,g45)
    c: Coincident(g47,g46)
    c: Coincident(g47,g18)
    c: Horizontal(g47)
    c: Block(g46)
    c: Coincident(g48,g18)
    c: Horizontal(g48)
    c: Distance(g48) = 1.33
    c: Vertical(g49)
    c: Coincident(g49,g48)
    c: Coincident(g50,g49)
    c: Coincident(g50,g24)
    c: Horizontal(g50)
    c: Tangent(g50,g22)
    c: Horizontal(g51)
    c: Coincident(g51,g24)
    c: Block(g51)
    c: Vertical(g52)
    c: Block(g52)
    c: Coincident(g52,g51)
    c: Coincident(g53,g52)
    c: Coincident(g53,g30)
    c: Horizontal(g53)
    c: Distance(g1) = 8.5
FEATURE [Part::Feature] Face024
  shape: bbox 9.8 x 26.5 x 2e-07 mm, 1 faces, 0 solids (baked)
FEATURE [Part::Revolution] Revolve024
  Angle = 360
  Axis = (0,1,0)
  Base = (0,0,0)
  FaceMakerClass = Part::FaceMakerBullseye
  Placement = pos=(0,0,0) rot=(0,0,1;1.5708rad)
  Solid = false
  Source = -> Face024
  Symmetric = false
FEATURE [Part::Feature] Face025
  shape: bbox 9.8 x 26.5 x 2e-07 mm, 1 faces, 0 solids (baked)
FEATURE [Part::Revolution] Revolve025
  Angle = 360
  Axis = (0,1,0)
  Base = (0,0,0)
  FaceMakerClass = Part::FaceMakerBullseye
  Placement = pos=(0,0,0) rot=(0,0,1;1.5708rad)
  Solid = false
  Source = -> Face025
  Symmetric = false
FEATURE [Part::MultiFuse] Fusion033
  Placement = pos=(-18,19,36) rot=(0,0,1;0rad)
  Shapes = -> [Revolve025,Revolve024]
FEATURE [Part::Cylinder] Cylinder014
  Angle = 360
  AttacherType = Attacher::AttachEngine3D
  Height = 20
  Placement = pos=(0,0,36.15) rot=(0,0,1;0rad)
  Radius = 14.3
FEATURE [Part::Cylinder] Cylinder015
  Angle = 360
  AttacherType = Attacher::AttachEngine3D
  Height = 10
  Placement = pos=(0,0,36.15) rot=(0,0,1;0rad)
  Radius = 4
FEATURE [Part::MultiFuse] Fusion034  label="removeToCreteHoleForPlugHousing004"
  Placement = pos=(-42,19,36) rot=(0,1,0;1.5708rad)
  Shapes = -> [Cylinder014,Cylinder015]
FEATURE [Part::Cut] Cut008  label="top004"
  Base = -> Cut004
  Placement = pos=(-1,0,0) rot=(0,0,1;0rad)
  Tool = -> Fusion034
FEATURE [Part::Box] Box005  label="Cube005"
  AttacherType = Attacher::AttachEngine3D
  Height = 28
  Length = 3
  Placement = pos=(110.7,19,22) rot=(0,0,1;0rad)
  Width = 15.7
FEATURE [Part::Cylinder] Cylinder016
  Angle = 360
  AttacherType = Attacher::AttachEngine3D
  Height = 10
  Placement = pos=(0,0,36.15) rot=(0,0,1;0rad)
  Radius = 4
FEATURE [Part::Cylinder] Cylinder017
  Angle = 360
  AttacherType = Attacher::AttachEngine3D
  Height = 20
  Placement = pos=(0,0,36.15) rot=(0,0,1;0rad)
  Radius = 10.3
FEATURE [Part::MultiFuse] Fusion035  label="removeToCreteHoleForPlugHousing005"
  Placement = pos=(70,19,36) rot=(0,1,0;1.5708rad)
  Shapes = -> [Cylinder017,Cylinder016]
FEATURE [Part::Cut] Cut009  label="plugHousingTab001"
  Base = -> Box005
  Placement = pos=(-107.4,-14,0) rot=(0,0,1;0rad)
  Tool = -> Fusion035
FEATURE [Part::Box] Box006  label="Cube006"
  AttacherType = Attacher::AttachEngine3D
  Height = 28
  Length = 3
  Placement = pos=(110.7,19,22) rot=(0,0,1;0rad)
  Width = 15.7
FEATURE [Part::Cylinder] Cylinder018
  Angle = 360
  AttacherType = Attacher::AttachEngine3D
  Height = 10
  Placement = pos=(0,0,36.15) rot=(0,0,1;0rad)
  Radius = 4
FEATURE [Part::Cylinder] Cylinder019
  Angle = 360
  AttacherType = Attacher::AttachEngine3D
  Height = 20
  Placement = pos=(0,0,36.15) rot=(0,0,1;0rad)
  Radius = 10.3
FEATURE [Part::MultiFuse] Fusion036  label="removeToCreteHoleForPlugHousing006"
  Placement = pos=(70,19,36) rot=(0,1,0;1.5708rad)
  Shapes = -> [Cylinder019,Cylinder018]
FEATURE [Part::Cut] Cut010  label="plugHousingTab002"
  Base = -> Box006
  Placement = pos=(-107.4,-14,0) rot=(0,0,1;0rad)
  Tool = -> Fusion036
FEATURE [Part::MultiFuse] Fusion037
  Placement = pos=(9.6,23,0) rot=(0,0,1;3.14159rad)
  Shapes = -> [Cut009,Cut010]
FEATURE [Part::Box] Box  label="Cube"
  AttacherType = Attacher::AttachEngine3D
  Height = 10
  Length = 3
  Placement = pos=(3.3,4,12) rot=(0,0,1;0rad)
  Width = 10
FEATURE [Part::Fillet] Fillet004
  Base = -> Fusion028
  Edges = 1 edges r=2: [Edge25]
FEATURE [Part::Fillet] Fillet005  label="plugHousing046"
  Base = -> Fillet004
  Edges = 1 edges r=2: [Edge8]
FEATURE [Part::Fillet] Fillet006
  Base = -> Box
  Edges = 1 edges r=2: [Edge11]
FEATURE [Part::Box] Box007  label="Cube007"
  AttacherType = Attacher::AttachEngine3D
  Height = 10
  Length = 3
  Placement = pos=(3.3,4,50) rot=(0,0,1;0rad)
  Width = 10
FEATURE [Part::Fillet] Fillet007
  Base = -> Box007
  Edges = 1 edges r=2: [Edge12]
FEATURE [Part::Box] Box008  label="Cube008"
  AttacherType = Attacher::AttachEngine3D
  Height = 28
  Length = 4
  Placement = pos=(5,0,22) rot=(0,0,1;0rad)
  Width = 10
FEATURE [Part::Fillet] Fillet008
  Base = -> Box008
  Edges = 1 edges r=1: [Edge7]
FEATURE [Part::Fillet] Fillet009
  Base = -> Fillet008
  Edges = 1 edges r=2: [Edge5]
FEATURE [Part::Fillet] Fillet010
  Base = -> Fillet009
  Edges = 1 edges r=2: [Edge2]
FEATURE [Sketcher::SketchObject] Sketch009  label="topSketch003"
  FullyConstrained = true
  sketch-geometry (4):
    g0: LineSegment StartX=16.8446 StartY=31.512 StartZ=0 EndX=16.3251 EndY=34.4666 EndZ=0
    g1: ArcOfCircle CenterX=19 CenterY=19.2524 CenterZ=0 NormalX=0 NormalY=0 NormalZ=1 AngleXU=0 Radius=15.4476 StartAngle=1.74483 EndAngle=2.72717
    g2: ArcOfCircle CenterX=19 CenterY=19.2524 CenterZ=0 NormalX=0 NormalY=0 NormalZ=1 AngleXU=0 Radius=12.4476 StartAngle=1.74483 EndAngle=2.73189
    g3: LineSegment StartX=4.86004 StartY=25.4725 StartZ=0 EndX=7.58253 EndY=24.2107 EndZ=0
  constraints (7):
    c: Block(g0)
    c: Coincident(g1,g0)
    c: Coincident(g2,g0)
    c: Coincident(g3,g1)
    c: Coincident(g3,g2)
    c: Block(g1)
    c: Block(g2)
FEATURE [Part::Extrusion] Extrude008
  Base = -> Sketch009
  Dir = (0,0,1)
  DirMode = 2
  FaceMakerClass = Part::FaceMakerBullseye
  LengthFwd = 10
  LengthRev = 0
  Placement = pos=(0,0,31) rot=(0,0,1;0rad)
  Solid = true
  Symmetric = false
FEATURE [Part::Cylinder] Cylinder020
  Angle = 360
  AttacherType = Attacher::AttachEngine3D
  Height = 20
  Placement = pos=(0,0,36.15) rot=(0,0,1;0rad)
  Radius = 8.2
FEATURE [Part::Cylinder] Cylinder021
  Angle = 360
  AttacherType = Attacher::AttachEngine3D
  Height = 10
  Placement = pos=(0,0,36.15) rot=(0,0,1;0rad)
  Radius = 4
FEATURE [Part::MultiFuse] Fusion038  label="removeToCreteHoleForPlugHousing007"
  Placement = pos=(-42,19,36) rot=(0,1,0;1.5708rad)
  Shapes = -> [Cylinder020,Cylinder021]
FEATURE [Part::Cut] Cut011
  Base = -> Extrude008
  Tool = -> Fusion038
FEATURE [Part::Fillet] Fillet011
  Base = -> Cut011
  Edges = 1 edges r=2: [Edge1]
FEATURE [Part::Fillet] Fillet012
  Base = -> Fillet011
  Edges = 1 edges r=2.5: [Edge1]
FEATURE [Part::Fillet] Fillet013
  Base = -> Fillet012
  Edges = 1 edges r=2.5: [Edge2]
FEATURE [Part::Box] Box010  label="Cube010"
  AttacherType = Attacher::AttachEngine3D
  Height = 16
  Length = 8
  Placement = pos=(12.7,31.52,28) rot=(0,0,1;0rad)
  Width = 4
FEATURE [Sketcher::SketchObject] Sketch010  label="topSketch004"
  FullyConstrained = true
  sketch-geometry (4):
    g0: LineSegment StartX=16.8446 StartY=31.512 StartZ=0 EndX=16.3251 EndY=34.4666 EndZ=0
    g1: ArcOfCircle CenterX=19 CenterY=19.2524 CenterZ=0 NormalX=0 NormalY=0 NormalZ=1 AngleXU=0 Radius=15.4476 StartAngle=1.74483 EndAngle=2.72717
    g2: ArcOfCircle CenterX=19 CenterY=19.2524 CenterZ=0 NormalX=0 NormalY=0 NormalZ=1 AngleXU=0 Radius=12.4476 StartAngle=1.74483 EndAngle=2.73189
    g3: LineSegment StartX=4.86004 StartY=25.4725 StartZ=0 EndX=7.58253 EndY=24.2107 EndZ=0
  constraints (7):
    c: Block(g0)
    c: Coincident(g1,g0)
    c: Coincident(g2,g0)
    c: Coincident(g3,g1)
    c: Coincident(g3,g2)
    c: Block(g1)
    c: Block(g2)
FEATURE [Part::Cylinder] Cylinder022
  Angle = 360
  AttacherType = Attacher::AttachEngine3D
  Height = 10
  Placement = pos=(0,0,36.15) rot=(0,0,1;0rad)
  Radius = 4
FEATURE [Sketcher::SketchObject] Sketch011  label="topSketch005"
  FullyConstrained = true
  sketch-geometry (4):
    g0: LineSegment StartX=16.8446 StartY=31.512 StartZ=0 EndX=16.3251 EndY=34.4666 EndZ=0
    g1: ArcOfCircle CenterX=19 CenterY=19.2524 CenterZ=0 NormalX=0 NormalY=0 NormalZ=1 AngleXU=0 Radius=15.4476 StartAngle=1.74483 EndAngle=2.72717
    g2: ArcOfCircle CenterX=19 CenterY=19.2524 CenterZ=0 NormalX=0 NormalY=0 NormalZ=1 AngleXU=0 Radius=12.4476 StartAngle=1.74483 EndAngle=2.73189
    g3: LineSegment StartX=4.86004 StartY=25.4725 StartZ=0 EndX=7.58253 EndY=24.2107 EndZ=0
  constraints (7):
    c: Block(g0)
    c: Coincident(g1,g0)
    c: Coincident(g2,g0)
    c: Coincident(g3,g1)
    c: Coincident(g3,g2)
    c: Block(g1)
    c: Block(g2)
FEATURE [Part::Extrusion] Extrude010
  Base = -> Sketch011
  Dir = (0,0,1)
  DirMode = 2
  FaceMakerClass = Part::FaceMakerBullseye
  LengthFwd = 10.6
  LengthRev = 0
  Placement = pos=(0,0,31) rot=(0,0,1;0rad)
  Solid = true
  Symmetric = false
FEATURE [Part::Cylinder] Cylinder023
  Angle = 360
  AttacherType = Attacher::AttachEngine3D
  Height = 20
  Placement = pos=(0,0,36.15) rot=(0,0,1;0rad)
  Radius = 8.2
FEATURE [Part::MultiFuse] Fusion039  label="removeToCreteHoleForPlugHousing008"
  Placement = pos=(-42,19,36) rot=(0,1,0;1.5708rad)
  Shapes = -> [Cylinder023,Cylinder022]
FEATURE [Part::Cut] Cut012
  Base = -> Extrude010
  Placement = pos=(0,0,-0.3) rot=(0,0,1;0rad)
  Tool = -> Fusion039
FEATURE [Part::Cut] Cut013
  Base = -> Box010
  Tool = -> Cut012
FEATURE [Part::Fillet] Fillet014
  Base = -> Cut013
  Edges = 1 edges r=0.7: [Edge13]
FEATURE [Part::Fillet] Fillet015
  Base = -> Fillet014
  Edges = 1 edges r=0.7: [Edge13]
FEATURE [Part::Fillet] Fillet016
  Base = -> Fillet015
  Edges = 1 edges r=0.7: [Edge16]
FEATURE [Part::Fillet] Fillet017
  Base = -> Fillet016
  Edges = 1 edges r=0.7: [Edge11]
FEATURE [Part::Fillet] Fillet018
  Base = -> Fillet017
  Edges = 1 edges r=0.7: [Edge10]
FEATURE [Part::Fillet] Fillet019
  Base = -> Fillet018
  Edges = 1 edges r=1.2: [Edge5]
FEATURE [Part::Fillet] Fillet020
  Base = -> Fillet019
  Edges = 1 edges r=1.2: [Edge12]
FEATURE [Part::Fillet] Fillet021
  Base = -> Fillet020
  Edges = 1 edges r=2: [Edge1]
  Placement = pos=(0.3,0,0) rot=(0,0,1;0rad)
FEATURE [Part::MultiFuse] Fusion040  label="top005"
  Shapes = -> [Cut008,Fillet021]
FEATURE [Part::MultiFuse] Fusion041  label="wireHolder"
  Shapes = -> [Fusion033,Fillet013]
FEATURE [Part::MultiFuse] Fusion042
  Shapes = -> [Fillet007,Fusion041]
FEATURE [Part::MultiFuse] Fusion043  label="wireHolder001"
  Shapes = -> [Fusion042,Fillet010]
FEATURE [Part::MultiFuse] Fusion044  label="wireHolder002"
  Shapes = -> [Fillet006,Fusion037,Fusion043]
FEATURE [Part::Feature] Face026
  shape: bbox 11 x 6 x 2e-07 mm, 1 faces, 0 solids (baked)
FEATURE [Part::Revolution] Revolve026
  Angle = 360
  Axis = (0,1,0)
  Base = (0,0,0)
  FaceMakerClass = Part::FaceMakerBullseye
  Placement = pos=(30.3,-1,19.7) rot=(0,0,1;0rad)
  Solid = false
  Source = -> Face026
  Symmetric = false
FEATURE [Sketcher::SketchObject] Sketch013  label="topSketch006"
  FullyConstrained = true
  sketch-geometry (13):
    g0: LineSegment StartX=117 StartY=19 StartZ=0 EndX=117 EndY=38 EndZ=0
    g1: ArcOfCircle CenterX=98 CenterY=19 CenterZ=0 NormalX=0 NormalY=0 NormalZ=1 AngleXU=0 Radius=19 StartAngle=5.7297 EndAngle=6.28319
    g2: LineSegment StartX=0 StartY=3 StartZ=0 EndX=0 EndY=19 EndZ=0
    g3: LineSegment StartX=19 StartY=38 StartZ=0 EndX=117 EndY=38 EndZ=0
    g4: ArcOfCircle CenterX=19 CenterY=19 CenterZ=0 NormalX=0 NormalY=0 NormalZ=1 AngleXU=0 Radius=19 StartAngle=1.5708 EndAngle=3.14159
    g5: ArcOfCircle CenterX=19 CenterY=19 CenterZ=0 NormalX=0 NormalY=0 NormalZ=1 AngleXU=0 Radius=16 StartAngle=1.5708 EndAngle=3.14159
    g6: ArcOfCircle CenterX=98 CenterY=19 CenterZ=0 NormalX=0 NormalY=0 NormalZ=1 AngleXU=0 Radius=16 StartAngle=5.60905 EndAngle=6.28319
    g7: LineSegment StartX=114 StartY=19 StartZ=0 EndX=114 EndY=35 EndZ=0
    g8: LineSegment StartX=110.5 StartY=9.01251 StartZ=0 EndX=114.163 EndY=9.01251 EndZ=0
    g9: LineSegment StartX=114 StartY=35 StartZ=0 EndX=19 EndY=35 EndZ=0
    g10: LineSegment StartX=0 StartY=3 StartZ=0 EndX=0 EndY=0 EndZ=0
    g11: LineSegment StartX=3 StartY=0 StartZ=0 EndX=0 EndY=0 EndZ=0
    g12: LineSegment StartX=3 StartY=19 StartZ=0 EndX=3 EndY=0 EndZ=0
  constraints (33):
    c: Vertical(g0)
    c: Distance(g0) = 19
    c: Block(g0)
    c: Coincident(g1,g0)
    c: Block(g1)
    c: Vertical(g2)
    c: Block(g2)
    c: Coincident(g3,g0)
    c: Horizontal(g3)
    c: Distance(g3) = 98
    c: Coincident(g4,g3)
    c: Coincident(g4,g2)
    c: Block(g4)
    c: Coincident(g5,g4)
    c: Coincident(g6,g1)
    c: Block(g6)
    c: Block(g5)
    c: Coincident(g7,g6)
    c: Vertical(g7)
    c: Coincident(g8,g6)
    c: Coincident(g8,g1)
    c: Coincident(g9,g7)
    c: Coincident(g9,g5)
    c: Horizontal(g9)
    c: Tangent(g9,g5)
    c: Coincident(g10,g2)
    c: Distance(g10) = 3
    c: Vertical(g10)
    c: Coincident(g11,g10)
    c: Horizontal(g11)
    c: Coincident(g12,g5)
    c: Coincident(g12,g11)
    c: Vertical(g12)
FEATURE [Part::Extrusion] Extrude011  label="top006"
  Base = -> Sketch013
  Dir = (0,0,1)
  DirMode = 2
  FaceMakerClass = Part::FaceMakerBullseye
  LengthFwd = 72
  LengthRev = 0
  Solid = true
  Symmetric = false
FEATURE [Sketcher::SketchObject] Sketch014
  FullyConstrained = true
  MapMode = 3
  Placement = pos=(0,0,0) rot=(1,0,0;1.5708rad)
  Support = -> [Extrude011]
  sketch-geometry (8):
    g0: Circle CenterX=80.351 CenterY=-67.6202 CenterZ=0 NormalX=0 NormalY=0 NormalZ=1 AngleXU=0 Radius=2
    g1: Circle CenterX=80.351 CenterY=-67.6202 CenterZ=0 NormalX=0 NormalY=0 NormalZ=1 AngleXU=0 Radius=3
    g2: Circle CenterX=80.351 CenterY=-4.92017 CenterZ=0 NormalX=0 NormalY=0 NormalZ=1 AngleXU=0 Radius=2
    g3: Circle CenterX=80.351 CenterY=-4.92017 CenterZ=0 NormalX=0 NormalY=0 NormalZ=1 AngleXU=0 Radius=3
    g4: Circle CenterX=23.851 CenterY=-4.92017 CenterZ=0 NormalX=0 NormalY=0 NormalZ=1 AngleXU=0 Radius=2
    g5: Circle CenterX=23.851 CenterY=-4.92017 CenterZ=0 NormalX=0 NormalY=0 NormalZ=1 AngleXU=0 Radius=3
    g6: Circle CenterX=23.851 CenterY=-67.6202 CenterZ=0 NormalX=0 NormalY=0 NormalZ=1 AngleXU=0 Radius=2
    g7: Circle CenterX=23.851 CenterY=-67.6202 CenterZ=0 NormalX=0 NormalY=0 NormalZ=1 AngleXU=0 Radius=3
  constraints (8):
    c: Block(g3)
    c: Block(g2)
    c: Block(g1)
    c: Block(g0)
    c: Block(g6)
    c: Block(g7)
    c: Block(g4)
    c: Block(g5)
FEATURE [Part::Feature] Face027
  shape: bbox 11 x 6 x 2e-07 mm, 1 faces, 0 solids (baked)
FEATURE [Part::Revolution] Revolve027
  Angle = 360
  Axis = (0,1,0)
  Base = (0,0,0)
  FaceMakerClass = Part::FaceMakerBullseye
  Placement = pos=(30.3,-1,51.7) rot=(0,0,1;0rad)
  Solid = false
  Source = -> Face027
  Symmetric = false
FEATURE [Part::Feature] Face028
  shape: bbox 11 x 6 x 2e-07 mm, 1 faces, 0 solids (baked)
FEATURE [Part::Revolution] Revolve028
  Angle = 360
  Axis = (0,1,0)
  Base = (0,0,0)
  FaceMakerClass = Part::FaceMakerBullseye
  Placement = pos=(62.3,-1,19.7) rot=(0,0,1;0rad)
  Solid = false
  Source = -> Face028
  Symmetric = false
FEATURE [Part::Feature] Face029
  shape: bbox 11 x 6 x 2e-07 mm, 1 faces, 0 solids (baked)
FEATURE [Part::Revolution] Revolve029
  Angle = 360
  Axis = (0,1,0)
  Base = (0,0,0)
  FaceMakerClass = Part::FaceMakerBullseye
  Placement = pos=(62.3,-1,51.7) rot=(0,0,1;0rad)
  Solid = false
  Source = -> Face029
  Symmetric = false
FEATURE [Part::Feature] Wire
  shape: bbox 11 x 5.2 x 2e-07 mm, 0 faces, 0 solids (baked)
FEATURE [Part::Revolution] Revolve030
  Angle = 360
  Axis = (0,1,0)
  Base = (0,0,0)
  FaceMakerClass = Part::FaceMakerBullseye
  Placement = pos=(30.3,38,19.7) rot=(0,0,1;0rad)
  Solid = true
  Source = -> Wire
  Symmetric = false
FEATURE [Part::Feature] Wire001
  shape: bbox 11 x 5.2 x 2e-07 mm, 0 faces, 0 solids (baked)
FEATURE [Part::Revolution] Revolve031
  Angle = 360
  Axis = (0,1,0)
  Base = (0,0,0)
  FaceMakerClass = Part::FaceMakerBullseye
  Placement = pos=(30.3,38,51.7) rot=(0,0,1;0rad)
  Solid = true
  Source = -> Wire001
  Symmetric = false
FEATURE [Part::Feature] Wire002
  shape: bbox 11 x 5.2 x 2e-07 mm, 0 faces, 0 solids (baked)
FEATURE [Part::Revolution] Revolve032
  Angle = 360
  Axis = (0,1,0)
  Base = (0,0,0)
  FaceMakerClass = Part::FaceMakerBullseye
  Placement = pos=(62.3,38,51.7) rot=(0,0,1;0rad)
  Solid = true
  Source = -> Wire002
  Symmetric = false
FEATURE [Part::Feature] Wire003
  shape: bbox 11 x 5.2 x 2e-07 mm, 0 faces, 0 solids (baked)
FEATURE [Part::Revolution] Revolve033
  Angle = 360
  Axis = (0,1,0)
  Base = (0,0,0)
  FaceMakerClass = Part::FaceMakerBullseye
  Placement = pos=(62.3,38,19.7) rot=(0,0,1;0rad)
  Solid = true
  Source = -> Wire003
  Symmetric = false
FEATURE [Part::MultiFuse] Fusion045  label="altRandScrewHousing"
  Shapes = -> [Revolve029,Revolve027,Revolve028,Revolve026]
FEATURE [Part::MultiFuse] Fusion046  label="fanScrewHousing"
  Shapes = -> [Revolve033,Revolve032,Revolve031,Revolve030]
FEATURE [Sketcher::SketchObject] Sketch015
  FullyConstrained = true
  sketch-geometry (17):
    g0: Circle CenterX=-3.5 CenterY=23.5 CenterZ=0 NormalX=0 NormalY=0 NormalZ=1 AngleXU=0 Radius=1
    g1: Circle CenterX=-1 CenterY=15.25 CenterZ=0 NormalX=0 NormalY=0 NormalZ=1 AngleXU=0 Radius=1
    g2: Circle CenterX=-3.5 CenterY=7 CenterZ=0 NormalX=0 NormalY=0 NormalZ=1 AngleXU=0 Radius=1
    g3: BSplineCurve PolesCount=3 KnotsCount=2 Degree=2 IsPeriodic=0
    g4: GeomPoint X=-3.5 Y=23.5 Z=0
    g5: GeomPoint X=-3.5 Y=7 Z=0
    g6: Circle CenterX=-4.8 CenterY=30.5 CenterZ=0 NormalX=0 NormalY=0 NormalZ=1 AngleXU=0 Radius=1
    g7: Circle CenterX=-3.5 CenterY=30.5 CenterZ=0 NormalX=0 NormalY=0 NormalZ=1 AngleXU=0 Radius=1
    g8: Circle CenterX=-3.5 CenterY=29.2 CenterZ=0 NormalX=0 NormalY=0 NormalZ=1 AngleXU=0 Radius=1
    g9: BSplineCurve PolesCount=3 KnotsCount=2 Degree=2 IsPeriodic=0
    g10: GeomPoint X=-4.8 Y=30.5 Z=0
    g11: GeomPoint X=-3.5 Y=29.2 Z=0
    g12: LineSegment StartX=-3.5 StartY=29.2 StartZ=0 EndX=-3.5 EndY=23.5 EndZ=0
    g13: LineSegment StartX=-4.8 StartY=30.5 StartZ=0 EndX=0 EndY=30.5 EndZ=0
    g14: LineSegment StartX=-3.5 StartY=0.3 StartZ=0 EndX=0 EndY=0.3 EndZ=0
    g15: LineSegment StartX=-3.5 StartY=0.3 StartZ=0 EndX=-3.5 EndY=7 EndZ=0
    g16: LineSegment StartX=0 StartY=0.3 StartZ=0 EndX=0 EndY=30.5 EndZ=0
  constraints (33):
    c: Weight(g0) = 1
    c: Equal(g0,g1)
    c: Equal(g0,g2)
    c: InternalAlignment(g0,g3)
    c: InternalAlignment(g1,g3)
    c: InternalAlignment(g2,g3)
    c: InternalAlignment(g4,g3)
    c: InternalAlignment(g5,g3)
    c: Block(g3)
    c: Weight(g6) = 1
    c: Equal(g6,g7)
    c: Equal(g6,g8)
    c: InternalAlignment(g6,g9)
    c: InternalAlignment(g7,g9)
    c: InternalAlignment(g8,g9)
    c: InternalAlignment(g10,g9)
    c: InternalAlignment(g11,g9)
    c: Block(g9)
    c: Coincident(g12,g9)
    c: Coincident(g12,g3)
    c: Vertical(g12)
    c: Coincident(g13,g9)
    c: Horizontal(g13)
    c: Distance(g13) = 4.8
    c: Horizontal(g14)
    c: Block(g14)
    c: Coincident(g15,g14)
    c: Coincident(g15,g3)
    c: Vertical(g15)
    c: Coincident(g16,g14)
    c: Coincident(g16,g13)
    c: Vertical(g16)
    c: Tangent(g16,g1)
FEATURE [Sketcher::SketchObject] Sketch016
  FullyConstrained = true
  sketch-geometry (16):
    g0: Circle CenterX=-3.5 CenterY=23.5 CenterZ=0 NormalX=0 NormalY=0 NormalZ=1 AngleXU=0 Radius=1
    g1: Circle CenterX=-1 CenterY=15.25 CenterZ=0 NormalX=0 NormalY=0 NormalZ=1 AngleXU=0 Radius=1
    g2: Circle CenterX=-3.5 CenterY=7 CenterZ=0 NormalX=0 NormalY=0 NormalZ=1 AngleXU=0 Radius=1
    g3: BSplineCurve PolesCount=3 KnotsCount=2 Degree=2 IsPeriodic=0
    g4: GeomPoint X=-3.5 Y=23.5 Z=0
    g5: GeomPoint X=-3.5 Y=7 Z=0
    g6: LineSegment StartX=-3.5 StartY=28.2 StartZ=0 EndX=-3.5 EndY=23.5 EndZ=0
    g7: LineSegment StartX=0 StartY=29.5 StartZ=0 EndX=0 EndY=30 EndZ=0
    g8: LineSegment StartX=-3.5 StartY=28.2 StartZ=0 EndX=-3.5 EndY=30 EndZ=0
    g9: LineSegment StartX=0 StartY=30 StartZ=0 EndX=0 EndY=30.5 EndZ=0
    g10: LineSegment StartX=0 StartY=30.5 StartZ=0 EndX=-3.5 EndY=30.5 EndZ=0
    g11: LineSegment StartX=-3.5 StartY=30.5 StartZ=0 EndX=-3.5 EndY=30 EndZ=0
    g12: LineSegment StartX=0 StartY=29.5 StartZ=0 EndX=0 EndY=5 EndZ=0
    g13: LineSegment StartX=-3.5 StartY=0.3 StartZ=0 EndX=-3.5 EndY=7 EndZ=0
    g14: LineSegment StartX=-3.5 StartY=0.3 StartZ=0 EndX=0 EndY=0.3 EndZ=0
    g15: LineSegment StartX=0 StartY=5 StartZ=0 EndX=0 EndY=0.3 EndZ=0
  constraints (39):
    c: Weight(g0) = 1
    c: Equal(g0,g1)
    c: Equal(g0,g2)
    c: InternalAlignment(g0,g3)
    c: InternalAlignment(g1,g3)
    c: InternalAlignment(g2,g3)
    c: InternalAlignment(g4,g3)
    c: InternalAlignment(g5,g3)
    c: Block(g3)
    c: Coincident(g6,g3)
    c: Vertical(g6)
    c: Vertical(g7)
    c: Distance(g7) = 0.5
    c: Coincident(g8,g6)
    c: Vertical(g8)
    c: Block(g6)
    c: Block(g7)
    c: Vertical(g9)
    c: Equal(g7,g9) = 0.5
    c: Block(g9)
    c: Coincident(g9,g7)
    c: Horizontal(g10)
    c: Coincident(g10,g9)
    c: Coincident(g11,g10)
    c: Coincident(g11,g8)
    c: Vertical(g11)
    c: Block(g11)
    c: Coincident(g12,g7)
    c: Vertical(g12)
    c: Coincident(g13,g3)
    c: Vertical(g13)
    c: Distance(g13) = 6.7
    c: Coincident(g14,g13)
    c: Horizontal(g14)
    c: Block(g14)
    c: Coincident(g15,g12)
    c: Coincident(g15,g14)
    c: Vertical(g15)
    c: Block(g15)
FEATURE [Sketcher::SketchObject] Sketch017
  FullyConstrained = true
  sketch-geometry (11):
    g0: LineSegment StartX=-3.5 StartY=1e-16 StartZ=0 EndX=-1.6 EndY=1e-16 EndZ=0
    g1: LineSegment StartX=-1.6 StartY=1e-16 StartZ=0 EndX=-1.6 EndY=1.5 EndZ=0
    g2: LineSegment StartX=-3.5 StartY=1.5 StartZ=0 EndX=-1.6 EndY=1.5 EndZ=0
    g3: LineSegment StartX=-3.5 StartY=1e-16 StartZ=0 EndX=-4.8 EndY=1e-16 EndZ=0
    g4: Circle CenterX=-3.5 CenterY=1.3 CenterZ=0 NormalX=0 NormalY=0 NormalZ=1 AngleXU=0 Radius=1
    g5: Circle CenterX=-3.5 CenterY=1e-16 CenterZ=0 NormalX=0 NormalY=0 NormalZ=1 AngleXU=0 Radius=1
    g6: Circle CenterX=-4.8 CenterY=1e-16 CenterZ=0 NormalX=0 NormalY=0 NormalZ=1 AngleXU=0 Radius=1
    g7: BSplineCurve PolesCount=3 KnotsCount=2 Degree=2 IsPeriodic=0
    g8: GeomPoint X=-3.5 Y=1.3 Z=0
    g9: GeomPoint X=-4.8 Y=1e-16 Z=0
    g10: LineSegment StartX=-3.5 StartY=1.3 StartZ=0 EndX=-3.5 EndY=1.5 EndZ=0
  constraints (24):
    c: Horizontal(g0)
    c: Distance(g0) = 1.9
    c: Block(g0)
    c: Coincident(g1,g0)
    c: Vertical(g1)
    c: Coincident(g2,g1)
    c: Horizontal(g2)
    c: Coincident(g3,g0)
    c: Horizontal(g3)
    c: Distance(g3) = 1.3
    c: Weight(g4) = 1
    c: Equal(g4,g5)
    c: Coincident(g5,g0)
    c: Equal(g4,g6)
    c: Coincident(g7,g3)
    c: InternalAlignment(g4,g7)
    c: InternalAlignment(g5,g7)
    c: InternalAlignment(g6,g7)
    c: InternalAlignment(g8,g7)
    c: InternalAlignment(g9,g7)
    c: Coincident(g10,g7)
    c: Coincident(g10,g2)
    c: Vertical(g10)
    c: Block(g10)
FEATURE [Part::Feature] Face035
  shape: bbox 3.2 x 1.5 x 2e-07 mm, 1 faces, 0 solids (baked)
FEATURE [Part::Revolution] Revolve039  label="backCaseScrewRetainer"
  Angle = 360
  Axis = (0,1,0)
  Base = (0,0,0)
  FaceMakerClass = Part::FaceMakerBullseye
  Placement = pos=(12.5,3,62) rot=(0,0,1;0rad)
  Solid = false
  Source = -> Face035
  Symmetric = false
FEATURE [Part::Feature] Face036
  shape: bbox 3.2 x 1.5 x 2e-07 mm, 1 faces, 0 solids (baked)
FEATURE [Part::Feature] Face039
  shape: bbox 4.8 x 30.2 x 2e-07 mm, 1 faces, 0 solids (baked)
FEATURE [Part::Revolution] Revolve043  label="frontCaseScrewPost002"
  Angle = 360
  Axis = (0,1,0)
  Base = (0,0,0)
  FaceMakerClass = Part::FaceMakerBullseye
  Placement = pos=(89.5,4.5,3.5) rot=(0,0,1;0rad)
  Solid = false
  Source = -> Face039
  Symmetric = false
FEATURE [Part::Feature] Face042
  shape: bbox 4.8 x 30.2 x 2e-07 mm, 1 faces, 0 solids (baked)
FEATURE [Part::Revolution] Revolve046  label="frontCaseScrewPost003"
  Angle = 360
  Axis = (0,1,0)
  Base = (0,0,0)
  FaceMakerClass = Part::FaceMakerBullseye
  Placement = pos=(89.5,4.5,68.5) rot=(0,0,1;0rad)
  Solid = false
  Source = -> Face042
  Symmetric = false
FEATURE [Part::Feature] Face043
  shape: bbox 3.2 x 1.5 x 2e-07 mm, 1 faces, 0 solids (baked)
FEATURE [Part::Revolution] Revolve047  label="frontCaseScrewRetainer002"
  Angle = 360
  Axis = (0,1,0)
  Base = (0,0,0)
  FaceMakerClass = Part::FaceMakerBullseye
  Placement = pos=(89.5,3,68.5) rot=(0,0,1;0rad)
  Solid = false
  Source = -> Face043
  Symmetric = false
FEATURE [Part::Feature] Face044
  shape: bbox 3.2 x 1.5 x 2e-07 mm, 1 faces, 0 solids (baked)
FEATURE [Part::Revolution] Revolve048  label="frontCaseScrewRetainer003"
  Angle = 360
  Axis = (0,1,0)
  Base = (0,0,0)
  FaceMakerClass = Part::FaceMakerBullseye
  Placement = pos=(89.5,3,3.5) rot=(0,0,1;0rad)
  Solid = false
  Source = -> Face044
  Symmetric = false
FEATURE [App::MeasureDistance] Distance002  label="Distance: 1.67 mm"
  Distance = 1.66921
  P1 = (99.2361,4.7524,71.7)
  P2 = (99.2347,6.42161,71.7)
FEATURE [Sketcher::SketchObject] Sketch018
  FullyConstrained = true
  sketch-geometry (7):
    g0: LineSegment StartX=0 StartY=0 StartZ=0 EndX=0 EndY=6 EndZ=0
    g1: Circle CenterX=0 CenterY=0 CenterZ=0 NormalX=0 NormalY=0 NormalZ=1 AngleXU=0 Radius=1
    g2: Circle CenterX=8 CenterY=6 CenterZ=0 NormalX=0 NormalY=0 NormalZ=1 AngleXU=0 Radius=1
    g3: BSplineCurve PolesCount=3 KnotsCount=2 Degree=2 IsPeriodic=0
    g4: GeomPoint X=0 Y=0 Z=0
    g5: GeomPoint X=8 Y=6 Z=0
    g6: LineSegment StartX=0 StartY=6 StartZ=0 EndX=8 EndY=6 EndZ=0
  constraints (14):
    c: Coincident(g0,g-1)
    c: Distance(g0) = 6
    c: Vertical(g0)
    c: Coincident(g3,g0)
    c: Weight(g1) = 1
    c: Equal(g1,g2)
    c: InternalAlignment(g1,g3)
    c: InternalAlignment(g2,g3)
    c: InternalAlignment(g4,g3)
    c: InternalAlignment(g5,g3)
    c: Block(g3)
    c: Coincident(g6,g0)
    c: Coincident(g6,g3)
    c: Horizontal(g6)
FEATURE [Part::Extrusion] Extrude012  label="caseScrewPillarBracket"
  Base = -> Sketch018
  Dir = (0,0,1)
  DirMode = 2
  FaceMakerClass = Part::FaceMakerBullseye
  LengthFwd = 2.4
  LengthRev = 0
  Placement = pos=(15.76,29,8.8) rot=(0,1,0;0rad)
  Solid = true
  Symmetric = false
FEATURE [Sketcher::SketchObject] Sketch019
  FullyConstrained = true
  sketch-geometry (7):
    g0: LineSegment StartX=0 StartY=0 StartZ=0 EndX=0 EndY=6 EndZ=0
    g1: Circle CenterX=0 CenterY=0 CenterZ=0 NormalX=0 NormalY=0 NormalZ=1 AngleXU=0 Radius=1
    g2: Circle CenterX=8 CenterY=6 CenterZ=0 NormalX=0 NormalY=0 NormalZ=1 AngleXU=0 Radius=1
    g3: BSplineCurve PolesCount=3 KnotsCount=2 Degree=2 IsPeriodic=0
    g4: GeomPoint X=0 Y=0 Z=0
    g5: GeomPoint X=8 Y=6 Z=0
    g6: LineSegment StartX=0 StartY=6 StartZ=0 EndX=8 EndY=6 EndZ=0
  constraints (14):
    c: Coincident(g0,g-1)
    c: Distance(g0) = 6
    c: Vertical(g0)
    c: Coincident(g3,g0)
    c: Weight(g1) = 1
    c: Equal(g1,g2)
    c: InternalAlignment(g1,g3)
    c: InternalAlignment(g2,g3)
    c: InternalAlignment(g4,g3)
    c: InternalAlignment(g5,g3)
    c: Block(g3)
    c: Coincident(g6,g0)
    c: Coincident(g6,g3)
    c: Horizontal(g6)
FEATURE [Part::Extrusion] Extrude013  label="caseScrewPillarBracket001"
  Base = -> Sketch019
  Dir = (0,0,1)
  DirMode = 2
  FaceMakerClass = Part::FaceMakerBullseye
  LengthFwd = 2.4
  LengthRev = 0
  Placement = pos=(15.76,29,60.8) rot=(0,0,1;0rad)
  Solid = true
  Symmetric = false
FEATURE [Sketcher::SketchObject] Sketch020
  FullyConstrained = true
  sketch-geometry (7):
    g0: LineSegment StartX=0 StartY=0 StartZ=0 EndX=0 EndY=6 EndZ=0
    g1: Circle CenterX=0 CenterY=0 CenterZ=0 NormalX=0 NormalY=0 NormalZ=1 AngleXU=0 Radius=1
    g2: Circle CenterX=8 CenterY=6 CenterZ=0 NormalX=0 NormalY=0 NormalZ=1 AngleXU=0 Radius=1
    g3: BSplineCurve PolesCount=3 KnotsCount=2 Degree=2 IsPeriodic=0
    g4: GeomPoint X=0 Y=0 Z=0
    g5: GeomPoint X=8 Y=6 Z=0
    g6: LineSegment StartX=0 StartY=6 StartZ=0 EndX=8 EndY=6 EndZ=0
  constraints (14):
    c: Coincident(g0,g-1)
    c: Distance(g0) = 6
    c: Vertical(g0)
    c: Coincident(g3,g0)
    c: Weight(g1) = 1
    c: Equal(g1,g2)
    c: InternalAlignment(g1,g3)
    c: InternalAlignment(g2,g3)
    c: InternalAlignment(g4,g3)
    c: InternalAlignment(g5,g3)
    c: Block(g3)
    c: Coincident(g6,g0)
    c: Coincident(g6,g3)
    c: Horizontal(g6)
FEATURE [Part::Extrusion] Extrude014  label="caseScrewPillarBracket002"
  Base = -> Sketch020
  Dir = (0,0,1)
  DirMode = 2
  FaceMakerClass = Part::FaceMakerBullseye
  LengthFwd = 2.4
  LengthRev = 0
  Placement = pos=(13.7,29,13.26) rot=(0,-1,0;1.5708rad)
  Solid = true
  Symmetric = false
FEATURE [Sketcher::SketchObject] Sketch021
  FullyConstrained = true
  sketch-geometry (7):
    g0: LineSegment StartX=0 StartY=0 StartZ=0 EndX=0 EndY=6 EndZ=0
    g1: Circle CenterX=0 CenterY=0 CenterZ=0 NormalX=0 NormalY=0 NormalZ=1 AngleXU=0 Radius=1
    g2: Circle CenterX=8 CenterY=6 CenterZ=0 NormalX=0 NormalY=0 NormalZ=1 AngleXU=0 Radius=1
    g3: BSplineCurve PolesCount=3 KnotsCount=2 Degree=2 IsPeriodic=0
    g4: GeomPoint X=0 Y=0 Z=0
    g5: GeomPoint X=8 Y=6 Z=0
    g6: LineSegment StartX=0 StartY=6 StartZ=0 EndX=8 EndY=6 EndZ=0
  constraints (14):
    c: Coincident(g0,g-1)
    c: Distance(g0) = 6
    c: Vertical(g0)
    c: Coincident(g3,g0)
    c: Weight(g1) = 1
    c: Equal(g1,g2)
    c: InternalAlignment(g1,g3)
    c: InternalAlignment(g2,g3)
    c: InternalAlignment(g4,g3)
    c: InternalAlignment(g5,g3)
    c: Block(g3)
    c: Coincident(g6,g0)
    c: Coincident(g6,g3)
    c: Horizontal(g6)
FEATURE [Part::Extrusion] Extrude015  label="caseScrewPillarBracket003"
  Base = -> Sketch021
  Dir = (0,0,1)
  DirMode = 2
  FaceMakerClass = Part::FaceMakerBullseye
  LengthFwd = 2.4
  LengthRev = 0
  Placement = pos=(11.3,29,58.74) rot=(0,1,0;1.5708rad)
  Solid = true
  Symmetric = false
FEATURE [Sketcher::SketchObject] Sketch022
  FullyConstrained = true
  sketch-geometry (7):
    g0: LineSegment StartX=0 StartY=0 StartZ=0 EndX=0 EndY=6 EndZ=0
    g1: Circle CenterX=0 CenterY=0 CenterZ=0 NormalX=0 NormalY=0 NormalZ=1 AngleXU=0 Radius=1
    g2: Circle CenterX=8 CenterY=6 CenterZ=0 NormalX=0 NormalY=0 NormalZ=1 AngleXU=0 Radius=1
    g3: BSplineCurve PolesCount=3 KnotsCount=2 Degree=2 IsPeriodic=0
    g4: GeomPoint X=0 Y=0 Z=0
    g5: GeomPoint X=8 Y=6 Z=0
    g6: LineSegment StartX=0 StartY=6 StartZ=0 EndX=8 EndY=6 EndZ=0
  constraints (14):
    c: Coincident(g0,g-1)
    c: Distance(g0) = 6
    c: Vertical(g0)
    c: Coincident(g3,g0)
    c: Weight(g1) = 1
    c: Equal(g1,g2)
    c: InternalAlignment(g1,g3)
    c: InternalAlignment(g2,g3)
    c: InternalAlignment(g4,g3)
    c: InternalAlignment(g5,g3)
    c: Block(g3)
    c: Coincident(g6,g0)
    c: Coincident(g6,g3)
    c: Horizontal(g6)
FEATURE [Part::Extrusion] Extrude016  label="caseScrewPillarBracket004"
  Base = -> Sketch022
  Dir = (0,0,1)
  DirMode = 2
  FaceMakerClass = Part::FaceMakerBullseye
  LengthFwd = 2.4
  LengthRev = 0
  Placement = pos=(88.3,29,65.23) rot=(0,1,0;1.5708rad)
  Solid = true
  Symmetric = false
FEATURE [Sketcher::SketchObject] Sketch023
  FullyConstrained = true
  sketch-geometry (7):
    g0: LineSegment StartX=0 StartY=0 StartZ=0 EndX=0 EndY=6 EndZ=0
    g1: Circle CenterX=0 CenterY=0 CenterZ=0 NormalX=0 NormalY=0 NormalZ=1 AngleXU=0 Radius=1
    g2: Circle CenterX=8 CenterY=6 CenterZ=0 NormalX=0 NormalY=0 NormalZ=1 AngleXU=0 Radius=1
    g3: BSplineCurve PolesCount=3 KnotsCount=2 Degree=2 IsPeriodic=0
    g4: GeomPoint X=0 Y=0 Z=0
    g5: GeomPoint X=8 Y=6 Z=0
    g6: LineSegment StartX=0 StartY=6 StartZ=0 EndX=8 EndY=6 EndZ=0
  constraints (14):
    c: Coincident(g0,g-1)
    c: Distance(g0) = 6
    c: Vertical(g0)
    c: Coincident(g3,g0)
    c: Weight(g1) = 1
    c: Equal(g1,g2)
    c: InternalAlignment(g1,g3)
    c: InternalAlignment(g2,g3)
    c: InternalAlignment(g4,g3)
    c: InternalAlignment(g5,g3)
    c: Block(g3)
    c: Coincident(g6,g0)
    c: Coincident(g6,g3)
    c: Horizontal(g6)
FEATURE [Part::Extrusion] Extrude017  label="caseScrewPillarBracket005"
  Base = -> Sketch023
  Dir = (0,0,1)
  DirMode = 2
  FaceMakerClass = Part::FaceMakerBullseye
  LengthFwd = 2.4
  LengthRev = 0
  Placement = pos=(90.7,29,6.77) rot=(0,-1,0;1.5708rad)
  Solid = true
  Symmetric = false
FEATURE [Sketcher::SketchObject] Sketch024
  FullyConstrained = true
  sketch-geometry (7):
    g0: LineSegment StartX=0 StartY=0 StartZ=0 EndX=0 EndY=6 EndZ=0
    g1: Circle CenterX=0 CenterY=0 CenterZ=0 NormalX=0 NormalY=0 NormalZ=1 AngleXU=0 Radius=1
    g2: Circle CenterX=8 CenterY=6 CenterZ=0 NormalX=0 NormalY=0 NormalZ=1 AngleXU=0 Radius=1
    g3: BSplineCurve PolesCount=3 KnotsCount=2 Degree=2 IsPeriodic=0
    g4: GeomPoint X=0 Y=0 Z=0
    g5: GeomPoint X=8 Y=6 Z=0
    g6: LineSegment StartX=0 StartY=6 StartZ=0 EndX=8 EndY=6 EndZ=0
  constraints (14):
    c: Coincident(g0,g-1)
    c: Distance(g0) = 6
    c: Vertical(g0)
    c: Coincident(g3,g0)
    c: Weight(g1) = 1
    c: Equal(g1,g2)
    c: InternalAlignment(g1,g3)
    c: InternalAlignment(g2,g3)
    c: InternalAlignment(g4,g3)
    c: InternalAlignment(g5,g3)
    c: Block(g3)
    c: Coincident(g6,g0)
    c: Coincident(g6,g3)
    c: Horizontal(g6)
FEATURE [Part::Extrusion] Extrude018  label="caseScrewPillarBracket006"
  Base = -> Sketch024
  Dir = (0,0,1)
  DirMode = 2
  FaceMakerClass = Part::FaceMakerBullseye
  LengthFwd = 2.4
  LengthRev = 0
  Placement = pos=(103.7,29,6.77) rot=(0,-1,0;1.5708rad)
  Solid = true
  Symmetric = false
FEATURE [Sketcher::SketchObject] Sketch025
  FullyConstrained = true
  sketch-geometry (7):
    g0: LineSegment StartX=0 StartY=0 StartZ=0 EndX=0 EndY=6 EndZ=0
    g1: Circle CenterX=0 CenterY=0 CenterZ=0 NormalX=0 NormalY=0 NormalZ=1 AngleXU=0 Radius=1
    g2: Circle CenterX=8 CenterY=6 CenterZ=0 NormalX=0 NormalY=0 NormalZ=1 AngleXU=0 Radius=1
    g3: BSplineCurve PolesCount=3 KnotsCount=2 Degree=2 IsPeriodic=0
    g4: GeomPoint X=0 Y=0 Z=0
    g5: GeomPoint X=8 Y=6 Z=0
    g6: LineSegment StartX=0 StartY=6 StartZ=0 EndX=8 EndY=6 EndZ=0
  constraints (14):
    c: Coincident(g0,g-1)
    c: Distance(g0) = 6
    c: Vertical(g0)
    c: Coincident(g3,g0)
    c: Weight(g1) = 1
    c: Equal(g1,g2)
    c: InternalAlignment(g1,g3)
    c: InternalAlignment(g2,g3)
    c: InternalAlignment(g4,g3)
    c: InternalAlignment(g5,g3)
    c: Block(g3)
    c: Coincident(g6,g0)
    c: Coincident(g6,g3)
    c: Horizontal(g6)
FEATURE [Part::Extrusion] Extrude019  label="caseScrewPillarBracket007"
  Base = -> Sketch025
  Dir = (0,0,1)
  DirMode = 2
  FaceMakerClass = Part::FaceMakerBullseye
  LengthFwd = 2.4
  LengthRev = 0
  Placement = pos=(101.3,29,65.23) rot=(0,1,0;1.5708rad)
  Solid = true
  Symmetric = false
FEATURE [Part::Box] Box011  label="frontCaseScrewPillarBracket"
  AttacherType = Attacher::AttachEngine3D
  Height = 2.4
  Length = 16
  Placement = pos=(87,28,2.3) rot=(0,0,1;0rad)
  Width = 7
FEATURE [Part::Box] Box012  label="frontCaseScrewPillarBracket001"
  AttacherType = Attacher::AttachEngine3D
  Height = 2.4
  Length = 16
  Placement = pos=(87,28,67.3) rot=(0,0,1;0rad)
  Width = 7
FEATURE [Sketcher::SketchObject] Sketch026
  FullyConstrained = true
  sketch-geometry (17):
    g0: Circle CenterX=-3.5 CenterY=23.5 CenterZ=0 NormalX=0 NormalY=0 NormalZ=1 AngleXU=0 Radius=1
    g1: Circle CenterX=-1 CenterY=15.25 CenterZ=0 NormalX=0 NormalY=0 NormalZ=1 AngleXU=0 Radius=1
    g2: Circle CenterX=-3.5 CenterY=7 CenterZ=0 NormalX=0 NormalY=0 NormalZ=1 AngleXU=0 Radius=1
    g3: BSplineCurve PolesCount=3 KnotsCount=2 Degree=2 IsPeriodic=0
    g4: GeomPoint X=-3.5 Y=23.5 Z=0
    g5: GeomPoint X=-3.5 Y=7 Z=0
    g6: Circle CenterX=-4.8 CenterY=30.5 CenterZ=0 NormalX=0 NormalY=0 NormalZ=1 AngleXU=0 Radius=1
    g7: Circle CenterX=-3.5 CenterY=30.5 CenterZ=0 NormalX=0 NormalY=0 NormalZ=1 AngleXU=0 Radius=1
    g8: Circle CenterX=-3.5 CenterY=29.2 CenterZ=0 NormalX=0 NormalY=0 NormalZ=1 AngleXU=0 Radius=1
    g9: BSplineCurve PolesCount=3 KnotsCount=2 Degree=2 IsPeriodic=0
    g10: GeomPoint X=-4.8 Y=30.5 Z=0
    g11: GeomPoint X=-3.5 Y=29.2 Z=0
    g12: LineSegment StartX=-3.5 StartY=29.2 StartZ=0 EndX=-3.5 EndY=23.5 EndZ=0
    g13: LineSegment StartX=-4.8 StartY=30.5 StartZ=0 EndX=0 EndY=30.5 EndZ=0
    g14: LineSegment StartX=-3.5 StartY=5 StartZ=0 EndX=-3.5 EndY=7 EndZ=0
    g15: LineSegment StartX=0 StartY=5 StartZ=0 EndX=0 EndY=30.5 EndZ=0
    g16: LineSegment StartX=-3.5 StartY=5 StartZ=0 EndX=0 EndY=5 EndZ=0
  constraints (33):
    c: Weight(g0) = 1
    c: Equal(g0,g1)
    c: Equal(g0,g2)
    c: InternalAlignment(g0,g3)
    c: InternalAlignment(g1,g3)
    c: InternalAlignment(g2,g3)
    c: InternalAlignment(g4,g3)
    c: InternalAlignment(g5,g3)
    c: Block(g3)
    c: Weight(g6) = 1
    c: Equal(g6,g7)
    c: Equal(g6,g8)
    c: InternalAlignment(g6,g9)
    c: InternalAlignment(g7,g9)
    c: InternalAlignment(g8,g9)
    c: InternalAlignment(g10,g9)
    c: InternalAlignment(g11,g9)
    c: Block(g9)
    c: Coincident(g12,g9)
    c: Coincident(g12,g3)
    c: Vertical(g12)
    c: Coincident(g13,g9)
    c: Horizontal(g13)
    c: Distance(g13) = 4.8
    c: Coincident(g14,g3)
    c: Vertical(g14)
    c: Coincident(g15,g13)
    c: Vertical(g15)
    c: Tangent(g15,g1)
    c: Distance(g14) = 2
    c: Coincident(g16,g14)
    c: Horizontal(g16)
    c: Coincident(g15,g16)
FEATURE [Part::Feature] Face050
  shape: bbox 4.8 x 25.5 x 2e-07 mm, 1 faces, 0 solids (baked)
FEATURE [Part::Revolution] Revolve054  label="moreFrontCaseScrewPost001"
  Angle = 360
  Axis = (0,1,0)
  Base = (0,0,0)
  FaceMakerClass = Part::FaceMakerBullseye
  Placement = pos=(102.5,4.5,3.5) rot=(0,0,1;0rad)
  Solid = false
  Source = -> Face050
  Symmetric = false
FEATURE [Part::Feature] Face051
  shape: bbox 4.8 x 25.5 x 2e-07 mm, 1 faces, 0 solids (baked)
FEATURE [Part::Revolution] Revolve055  label="moreFrontCaseScrewPost002"
  Angle = 360
  Axis = (0,1,0)
  Base = (0,0,0)
  FaceMakerClass = Part::FaceMakerBullseye
  Placement = pos=(102.5,4.5,68.5) rot=(0,0,1;0rad)
  Solid = false
  Source = -> Face051
  Symmetric = false
FEATURE [Sketcher::SketchObject] Sketch027
  FullyConstrained = true
  sketch-geometry (10):
    g0: LineSegment StartX=-1.6 StartY=4.7 StartZ=0 EndX=-1.6 EndY=1.7 EndZ=0
    g1: LineSegment StartX=-3.5 StartY=4.7 StartZ=0 EndX=-1.6 EndY=4.7 EndZ=0
    g2: LineSegment StartX=-1.6 StartY=1.7 StartZ=0 EndX=-1.6 EndY=1.5 EndZ=0
    g3: LineSegment StartX=-1.6 StartY=1.5 StartZ=0 EndX=-5.2 EndY=1.5 EndZ=0
    g4: Circle CenterX=-3.5 CenterY=4.7 CenterZ=0 NormalX=0 NormalY=0 NormalZ=1 AngleXU=0 Radius=1
    g5: Circle CenterX=-3.59627 CenterY=2.99743 CenterZ=0 NormalX=0 NormalY=0 NormalZ=1 AngleXU=0 Radius=1
    g6: Circle CenterX=-5.2 CenterY=1.5 CenterZ=0 NormalX=0 NormalY=0 NormalZ=1 AngleXU=0 Radius=1
    g7: BSplineCurve PolesCount=3 KnotsCount=2 Degree=2 IsPeriodic=0
    g8: GeomPoint X=-3.5 Y=4.7 Z=0
    g9: GeomPoint X=-5.2 Y=1.5 Z=0
  constraints (23):
    c: Vertical(g0)
    c: Distance(g0) = 3
    c: Coincident(g1,g0)
    c: Horizontal(g1)
    c: Block(g0)
    c: Block(g1)
    c: Coincident(g2,g0)
    c: Vertical(g2)
    c: Distance(g2) = 0.2
    c: Coincident(g3,g2)
    c: Horizontal(g3)
    c: Block(g3)
    c: Coincident(g7,g1)
    c: Weight(g4) = 1
    c: Equal(g4,g5)
    c: Equal(g4,g6)
    c: Coincident(g7,g3)
    c: InternalAlignment(g4,g7)
    c: InternalAlignment(g5,g7)
    c: InternalAlignment(g6,g7)
    c: InternalAlignment(g8,g7)
    c: InternalAlignment(g9,g7)
    c: Block(g7)
FEATURE [Sketcher::SketchObject] Sketch028
  FullyConstrained = true
  sketch-geometry (18):
    g0: LineSegment StartX=0 StartY=3e-16 StartZ=0 EndX=0 EndY=1.7 EndZ=0
    g1: LineSegment StartX=-3.5 StartY=0 StartZ=0 EndX=-3.5 EndY=0.9 EndZ=0
    g2: Circle CenterX=-2.7 CenterY=1.7 CenterZ=0 NormalX=0 NormalY=0 NormalZ=1 AngleXU=0 Radius=1
    g3: Circle CenterX=-3.5 CenterY=1.7 CenterZ=0 NormalX=0 NormalY=0 NormalZ=1 AngleXU=0 Radius=1
    g4: Circle CenterX=-3.5 CenterY=0.9 CenterZ=0 NormalX=0 NormalY=0 NormalZ=1 AngleXU=0 Radius=1
    g5: BSplineCurve PolesCount=3 KnotsCount=2 Degree=2 IsPeriodic=0
    g6: GeomPoint X=-2.7 Y=1.7 Z=0
    g7: GeomPoint X=-3.5 Y=0.9 Z=0
    g8: LineSegment StartX=-3.5 StartY=0 StartZ=0 EndX=-3.5 EndY=-7 EndZ=0
    g9: LineSegment StartX=0 StartY=3e-16 StartZ=0 EndX=0 EndY=-7 EndZ=0
    g10: LineSegment StartX=-3.5 StartY=-7 StartZ=0 EndX=0 EndY=-7 EndZ=0
    g11: LineSegment StartX=-2.7 StartY=1.7 StartZ=0 EndX=-1.6 EndY=1.7 EndZ=0
    g12: LineSegment StartX=0 StartY=1.7 StartZ=0 EndX=0 EndY=4.5 EndZ=0
    g13: LineSegment StartX=0 StartY=4.5 StartZ=0 EndX=0 EndY=10.8 EndZ=0
    g14: LineSegment StartX=0 StartY=10.8 StartZ=0 EndX=-2 EndY=10.8 EndZ=0
    g15: LineSegment StartX=-1.6 StartY=4.7 StartZ=0 EndX=-1.6 EndY=1.7 EndZ=0
    g16: LineSegment StartX=-1.6 StartY=4.7 StartZ=0 EndX=-2 EndY=4.7 EndZ=0
    g17: LineSegment StartX=-2 StartY=4.7 StartZ=0 EndX=-2 EndY=10.8 EndZ=0
  constraints (44):
    c: Vertical(g0)
    c: Vertical(g1)
    c: Distance(g1) = 0.9
    c: Block(g0)
    c: Distance(g0) = 1.7
    c: Weight(g2) = 1
    c: Equal(g2,g3)
    c: Equal(g2,g4)
    c: Coincident(g5,g1)
    c: InternalAlignment(g2,g5)
    c: InternalAlignment(g3,g5)
    c: InternalAlignment(g4,g5)
    c: InternalAlignment(g6,g5)
    c: InternalAlignment(g7,g5)
    c: Block(g5)
    c: Coincident(g8,g1)
    c: Vertical(g8)
    c: Distance(g8) = 7
    c: Vertical(g9)
    c: Equal(g8,g9) = 7
    c: Coincident(g9,g0)
    c: Coincident(g10,g8)
    c: Coincident(g10,g9)
    c: Horizontal(g10)
    c: Coincident(g11,g5)
    c: Horizontal(g11)
    c: Coincident(g12,g0)
    c: Vertical(g12)
    c: Distance(g12) = 2.8
    c: Coincident(g13,g12)
    c: Vertical(g13)
    c: Distance(g13) = 6.3
    c: Coincident(g14,g13)
    c: Horizontal(g14)
    c: Distance(g14) = 2
    c: Vertical(g15)
    c: Distance(g15) = 3
    c: Block(g11)
    c: Coincident(g15,g11)
    c: Coincident(g16,g15)
    c: Horizontal(g16)
    c: Coincident(g17,g16)
    c: Coincident(g17,g14)
    c: Vertical(g17)
FEATURE [Part::Revolution] Revolve040  label="backCaseScrewRetainer001"
  Angle = 360
  Axis = (0,1,0)
  Base = (0,0,0)
  FaceMakerClass = Part::FaceMakerBullseye
  Placement = pos=(12.5,3,10) rot=(0,0,1;0rad)
  Solid = false
  Source = -> Face036
  Symmetric = false
FEATURE [Part::Feature] Face055
  shape: bbox 3.5 x 30.2 x 2e-07 mm, 1 faces, 0 solids (baked)
FEATURE [Part::Revolution] Revolve059  label="backCaseScrewPost"
  Angle = 360
  Axis = (0,1,0)
  Base = (0,0,0)
  FaceMakerClass = Part::FaceMakerBullseye
  Placement = pos=(12.5,4.5,10) rot=(0,0,1;0rad)
  Solid = false
  Source = -> Face055
  Symmetric = false
FEATURE [Part::Feature] Face056
  shape: bbox 3.5 x 30.2 x 2e-07 mm, 1 faces, 0 solids (baked)
FEATURE [Part::Revolution] Revolve060  label="backCaseScrewPost001"
  Angle = 360
  Axis = (0,1,0)
  Base = (0,0,0)
  FaceMakerClass = Part::FaceMakerBullseye
  Placement = pos=(12.5,4.5,62) rot=(0,0,1;0rad)
  Solid = false
  Source = -> Face056
  Symmetric = false
FEATURE [Part::Feature] Face057
  shape: bbox 3.5 x 17.8 x 2e-07 mm, 1 faces, 0 solids (baked)
FEATURE [Part::Revolution] Revolve061  label="removeToCreateScrewAndThreadedInsertHole"
  Angle = 360
  Axis = (0,1,0)
  Base = (0,0,0)
  FaceMakerClass = Part::FaceMakerBullseye
  Placement = pos=(12.5,0,10) rot=(0,0,1;0rad)
  Solid = false
  Source = -> Face057
  Symmetric = false
FEATURE [Part::Feature] Face058
  shape: bbox 3.5 x 17.8 x 2e-07 mm, 1 faces, 0 solids (baked)
FEATURE [Part::Revolution] Revolve062  label="removeToCreateScrewAndThreadedInsertHole001"
  Angle = 360
  Axis = (0,1,0)
  Base = (0,0,0)
  FaceMakerClass = Part::FaceMakerBullseye
  Placement = pos=(12.5,0,62) rot=(0,0,1;0rad)
  Solid = false
  Source = -> Face058
  Symmetric = false
FEATURE [Part::Feature] Face059
  shape: bbox 3.5 x 17.8 x 2e-07 mm, 1 faces, 0 solids (baked)
FEATURE [Part::Revolution] Revolve063  label="removeToCreateScrewAndThreadedInsertHole002"
  Angle = 360
  Axis = (0,1,0)
  Base = (0,0,0)
  FaceMakerClass = Part::FaceMakerBullseye
  Placement = pos=(89.5,0,68.5) rot=(0,0,1;0rad)
  Solid = false
  Source = -> Face059
  Symmetric = false
FEATURE [Part::Feature] Face060
  shape: bbox 3.5 x 17.8 x 2e-07 mm, 1 faces, 0 solids (baked)
FEATURE [Part::Revolution] Revolve064  label="removeToCreateScrewAndThreadedInsertHole003"
  Angle = 360
  Axis = (0,1,0)
  Base = (0,0,0)
  FaceMakerClass = Part::FaceMakerBullseye
  Placement = pos=(89.5,0,3.5) rot=(0,0,1;0rad)
  Solid = false
  Source = -> Face060
  Symmetric = false
FEATURE [Part::Feature] Face061
  shape: bbox 3.5 x 17.8 x 2e-07 mm, 1 faces, 0 solids (baked)
FEATURE [Part::Revolution] Revolve065  label="removeToCreateScrewAndThreadedInsertHole004"
  Angle = 360
  Axis = (0,1,0)
  Base = (0,0,0)
  FaceMakerClass = Part::FaceMakerBullseye
  Placement = pos=(102.5,4.7,3.5) rot=(0,0,1;0rad)
  Solid = false
  Source = -> Face061
  Symmetric = false
FEATURE [Part::Feature] Face062
  shape: bbox 3.5 x 17.8 x 2e-07 mm, 1 faces, 0 solids (baked)
FEATURE [Part::Revolution] Revolve066  label="removeToCreateScrewAndThreadedInsertHole005"
  Angle = 360
  Axis = (0,1,0)
  Base = (0,0,0)
  FaceMakerClass = Part::FaceMakerBullseye
  Placement = pos=(102.5,4.7,68.5) rot=(0,0,1;0rad)
  Solid = false
  Source = -> Face062
  Symmetric = false
FEATURE [Part::MultiFuse] Fusion047  label="makeHoles"
  Shapes = -> [Revolve066,Revolve065,Revolve064,Revolve063,Revolve062,Revolve061]
FEATURE [Part::Feature] Face063
  shape: bbox 3.6 x 3.2 x 2e-07 mm, 1 faces, 0 solids (baked)
FEATURE [Part::Revolution] Revolve067  label="moreFrontCaseScrewRetainer002"
  Angle = 360
  Axis = (0,1,0)
  Base = (0,0,0)
  FaceMakerClass = Part::FaceMakerBullseye
  Placement = pos=(102.5,4.5,68.5) rot=(0,0,1;0rad)
  Solid = false
  Source = -> Face063
  Symmetric = false
FEATURE [Part::Feature] Face064
  shape: bbox 3.6 x 3.2 x 2e-07 mm, 1 faces, 0 solids (baked)
FEATURE [Part::Revolution] Revolve068  label="moreFrontCaseScrewRetainer003"
  Angle = 360
  Axis = (0,1,0)
  Base = (0,0,0)
  FaceMakerClass = Part::FaceMakerBullseye
  Placement = pos=(102.5,4.5,3.5) rot=(0,0,1;0rad)
  Solid = false
  Source = -> Face064
  Symmetric = false
FEATURE [Part::Feature] Face065
  shape: bbox 3.5 x 17.8 x 2e-07 mm, 1 faces, 0 solids (baked)
FEATURE [Part::Revolution] Revolve069  label="removeToCreateScrewAndThreadedInsertHole006"
  Angle = 360
  Axis = (0,1,0)
  Base = (0,0,0)
  FaceMakerClass = Part::FaceMakerBullseye
  Placement = pos=(12.5,0,10) rot=(0,0,1;0rad)
  Solid = false
  Source = -> Face065
  Symmetric = false
FEATURE [Part::Feature] Face066
  shape: bbox 3.5 x 17.8 x 2e-07 mm, 1 faces, 0 solids (baked)
FEATURE [Part::Revolution] Revolve070  label="removeToCreateScrewAndThreadedInsertHole007"
  Angle = 360
  Axis = (0,1,0)
  Base = (0,0,0)
  FaceMakerClass = Part::FaceMakerBullseye
  Placement = pos=(12.5,0,62) rot=(0,0,1;0rad)
  Solid = false
  Source = -> Face066
  Symmetric = false
FEATURE [Part::Feature] Face067
  shape: bbox 3.5 x 17.8 x 2e-07 mm, 1 faces, 0 solids (baked)
FEATURE [Part::Revolution] Revolve071  label="removeToCreateScrewAndThreadedInsertHole008"
  Angle = 360
  Axis = (0,1,0)
  Base = (0,0,0)
  FaceMakerClass = Part::FaceMakerBullseye
  Placement = pos=(89.5,0,68.5) rot=(0,0,1;0rad)
  Solid = false
  Source = -> Face067
  Symmetric = false
FEATURE [Part::Feature] Face068
  shape: bbox 3.5 x 17.8 x 2e-07 mm, 1 faces, 0 solids (baked)
FEATURE [Part::Revolution] Revolve072  label="removeToCreateScrewAndThreadedInsertHole009"
  Angle = 360
  Axis = (0,1,0)
  Base = (0,0,0)
  FaceMakerClass = Part::FaceMakerBullseye
  Placement = pos=(89.5,0,3.5) rot=(0,0,1;0rad)
  Solid = false
  Source = -> Face068
  Symmetric = false
FEATURE [Part::Feature] Face069
  shape: bbox 3.5 x 17.8 x 2e-07 mm, 1 faces, 0 solids (baked)
FEATURE [Part::Feature] Face070
  shape: bbox 3.5 x 17.8 x 2e-07 mm, 1 faces, 0 solids (baked)
FEATURE [Part::Revolution] Revolve073  label="removeToCreateScrewAndThreadedInsertHole010"
  Angle = 360
  Axis = (0,1,0)
  Base = (0,0,0)
  FaceMakerClass = Part::FaceMakerBullseye
  Placement = pos=(102.5,4.7,3.5) rot=(0,0,1;0rad)
  Solid = false
  Source = -> Face069
  Symmetric = false
FEATURE [Part::Revolution] Revolve074  label="removeToCreateScrewAndThreadedInsertHole011"
  Angle = 360
  Axis = (0,1,0)
  Base = (0,0,0)
  FaceMakerClass = Part::FaceMakerBullseye
  Placement = pos=(102.5,4.7,68.5) rot=(0,0,1;0rad)
  Solid = false
  Source = -> Face070
  Symmetric = false
FEATURE [Part::MultiFuse] Fusion048  label="makeHoles001"
  Shapes = -> [Revolve074,Revolve073,Revolve072,Revolve071,Revolve070,Revolve069]
FEATURE [Part::MultiFuse] Fusion049  label="caseScrewRetainers"
  Shapes = -> [Revolve067,Revolve068,Revolve048,Revolve047,Revolve039,Revolve040]
FEATURE [Part::Cut] Cut015  label="caseScrewRetainers001"
  Base = -> Fusion049
  Tool = -> Fusion048
FEATURE [Part::MultiFuse] Fusion050  label="casePillars"
  Shapes = -> [Revolve055,Revolve054,Revolve043,Revolve046,Revolve059,Revolve060]
FEATURE [Part::Feature] Face071 .. Face076  x6 (patterned run collapsed; names and placements below)
  shape: bbox 3.5 x 17.8 x 2e-07 mm, 1 faces, 0 solids (baked)
FEATURE [Part::Revolution] Revolve075  label="removeToCreateScrewAndThreadedInsertHole012"
  Angle = 360
  Axis = (0,1,0)
  Base = (0,0,0)
  FaceMakerClass = Part::FaceMakerBullseye
  Placement = pos=(12.5,0,10) rot=(0,0,1;0rad)
  Solid = false
  Source = -> Face071
  Symmetric = false
FEATURE [Part::Revolution] Revolve076  label="removeToCreateScrewAndThreadedInsertHole013"
  Angle = 360
  Axis = (0,1,0)
  Base = (0,0,0)
  FaceMakerClass = Part::FaceMakerBullseye
  Placement = pos=(12.5,0,62) rot=(0,0,1;0rad)
  Solid = false
  Source = -> Face072
  Symmetric = false
FEATURE [Part::Revolution] Revolve077  label="removeToCreateScrewAndThreadedInsertHole014"
  Angle = 360
  Axis = (0,1,0)
  Base = (0,0,0)
  FaceMakerClass = Part::FaceMakerBullseye
  Placement = pos=(89.5,0,68.5) rot=(0,0,1;0rad)
  Solid = false
  Source = -> Face073
  Symmetric = false
FEATURE [Part::Revolution] Revolve078  label="removeToCreateScrewAndThreadedInsertHole015"
  Angle = 360
  Axis = (0,1,0)
  Base = (0,0,0)
  FaceMakerClass = Part::FaceMakerBullseye
  Placement = pos=(89.5,0,3.5) rot=(0,0,1;0rad)
  Solid = false
  Source = -> Face074
  Symmetric = false
FEATURE [Part::Revolution] Revolve079  label="removeToCreateScrewAndThreadedInsertHole016"
  Angle = 360
  Axis = (0,1,0)
  Base = (0,0,0)
  FaceMakerClass = Part::FaceMakerBullseye
  Placement = pos=(102.5,4.7,3.5) rot=(0,0,1;0rad)
  Solid = false
  Source = -> Face075
  Symmetric = false
FEATURE [Part::Revolution] Revolve080  label="removeToCreateScrewAndThreadedInsertHole017"
  Angle = 360
  Axis = (0,1,0)
  Base = (0,0,0)
  FaceMakerClass = Part::FaceMakerBullseye
  Placement = pos=(102.5,4.7,68.5) rot=(0,0,1;0rad)
  Solid = false
  Source = -> Face076
  Symmetric = false
FEATURE [Part::MultiFuse] Fusion051  label="makeHoles002"
  Shapes = -> [Revolve080,Revolve079,Revolve078,Revolve077,Revolve076,Revolve075]
FEATURE [Part::Cut] Cut016  label="caesPillars"
  Base = -> Fusion050
  Tool = -> Fusion051
FEATURE [Part::Revolution] Revolve009  label="plugHousing016"
  Angle = 360
  Axis = (0,1,0)
  Base = (0,0,0)
  FaceMakerClass = Part::FaceMakerBullseye
  Placement = pos=(0,0,36.15) rot=(0,0,1;0rad)
  Solid = false
  Source = -> Face012
  Symmetric = false
FEATURE [Part::MultiFuse] Fusion014  label="plugHousing023"
  Placement = pos=(0,0,0) rot=(0,0,1;1.5708rad)
  Shapes = -> [Revolve011,Revolve009]
FEATURE [Part::Revolution] Revolve010  label="plugHousing017"
  Angle = 360
  Axis = (0,1,0)
  Base = (0,0,0)
  FaceMakerClass = Part::FaceMakerBullseye
  Placement = pos=(0,0,36.15) rot=(0,0,1;0rad)
  Solid = false
  Source = -> Face014
  Symmetric = false
FEATURE [Part::MultiFuse] Fusion015  label="plugHousing024"
  Placement = pos=(0,0,0) rot=(0,0,1;1.5708rad)
  Shapes = -> [Revolve010,Revolve015]
FEATURE [Part::Revolution] Revolve014  label="plugHousing026"
  Angle = 360
  Axis = (0,1,0)
  Base = (0,0,0)
  FaceMakerClass = Part::FaceMakerBullseye
  Placement = pos=(0,0,36.15) rot=(0,0,1;0rad)
  Solid = false
  Source = -> Face011
  Symmetric = false
FEATURE [Part::Revolution] Revolve013  label="plugHousing025"
  Angle = 360
  Axis = (0,1,0)
  Base = (0,0,0)
  FaceMakerClass = Part::FaceMakerBullseye
  Placement = pos=(0,0,36.15) rot=(0,0,1;0rad)
  Solid = false
  Source = -> Face015
  Symmetric = false
FEATURE [Part::MultiFuse] Fusion016  label="plugHousing028"
  Placement = pos=(0,19,0) rot=(0,0,1;3.14159rad)
  Shapes = -> [Fusion014,Fusion013]
FEATURE [Part::MultiFuse] Fusion011  label="plugHousing018"
  Placement = pos=(0,0,0) rot=(0,0,1;1.5708rad)
  Shapes = -> [Revolve014,Revolve013]
FEATURE [Part::MultiFuse] Fusion012  label="plugHousing019"
  Placement = pos=(0,19,0) rot=(0,0,1;3.14159rad)
  Shapes = -> [Fusion011,Fusion015]
FEATURE [Part::MultiFuse] Fusion017  label="plugHousing029"
  Placement = pos=(122.621,0,-0.15) rot=(0,0,1;0rad)
  Shapes = -> [Fusion016,Fusion012]
FEATURE [Part::MultiFuse] Fusion052  label="casePillarRetainers"
  Shapes = -> [Extrude012,Extrude013,Extrude014,Extrude015,Extrude016,Extrude017,Extrude018,Extrude019,Box011,Box012]
FEATURE [Part::Feature] Face077
  shape: bbox 3.5 x 17.8 x 2e-07 mm, 1 faces, 0 solids (baked)
FEATURE [Part::Revolution] Revolve081  label="removeToCreateScrewAndThreadedInsertHole018"
  Angle = 360
  Axis = (0,1,0)
  Base = (0,0,0)
  FaceMakerClass = Part::FaceMakerBullseye
  Placement = pos=(62.3,30.3,19.7) rot=(0,0,1;0rad)
  Solid = false
  Source = -> Face077
  Symmetric = false
FEATURE [Part::Feature] Face078
  shape: bbox 3.5 x 17.8 x 2e-07 mm, 1 faces, 0 solids (baked)
FEATURE [Part::Revolution] Revolve082  label="removeToCreateScrewAndThreadedInsertHole019"
  Angle = 360
  Axis = (0,1,0)
  Base = (0,0,0)
  FaceMakerClass = Part::FaceMakerBullseye
  Placement = pos=(62.3,30.3,51.7) rot=(0,0,1;0rad)
  Solid = false
  Source = -> Face078
  Symmetric = false
FEATURE [Part::Feature] Face079
  shape: bbox 3.5 x 17.8 x 2e-07 mm, 1 faces, 0 solids (baked)
FEATURE [Part::Revolution] Revolve083  label="removeToCreateScrewAndThreadedInsertHole020"
  Angle = 360
  Axis = (0,1,0)
  Base = (0,0,0)
  FaceMakerClass = Part::FaceMakerBullseye
  Placement = pos=(30.3,30.3,19.7) rot=(0,0,1;0rad)
  Solid = false
  Source = -> Face079
  Symmetric = false
FEATURE [Part::Feature] Face080
  shape: bbox 3.5 x 17.8 x 2e-07 mm, 1 faces, 0 solids (baked)
FEATURE [Part::Revolution] Revolve084  label="removeToCreateScrewAndThreadedInsertHole021"
  Angle = 360
  Axis = (0,1,0)
  Base = (0,0,0)
  FaceMakerClass = Part::FaceMakerBullseye
  Placement = pos=(30.3,30.3,51.7) rot=(0,0,1;0rad)
  Solid = false
  Source = -> Face080
  Symmetric = false
FEATURE [Part::MultiFuse] Fusion053  label="createThreadedInsertHolesForFan"
  Shapes = -> [Revolve081,Revolve082,Revolve083,Revolve084]
FEATURE [Part::Cut] Cut017  label="fanScrewHousing001"
  Base = -> Fusion046
  Tool = -> Fusion053
FEATURE [Part::Feature] Face081
  shape: bbox 3.5 x 17.8 x 2e-07 mm, 1 faces, 0 solids (baked)
FEATURE [Part::Revolution] Revolve085  label="removeToCreateScrewAndThreadedInsertHole022"
  Angle = 360
  Axis = (0,1,0)
  Base = (0,0,0)
  FaceMakerClass = Part::FaceMakerBullseye
  Placement = pos=(62.3,30.3,19.7) rot=(0,0,1;0rad)
  Solid = false
  Source = -> Face081
  Symmetric = false
FEATURE [Part::Feature] Face082
  shape: bbox 3.5 x 17.8 x 2e-07 mm, 1 faces, 0 solids (baked)
FEATURE [Part::Revolution] Revolve086  label="removeToCreateScrewAndThreadedInsertHole023"
  Angle = 360
  Axis = (0,1,0)
  Base = (0,0,0)
  FaceMakerClass = Part::FaceMakerBullseye
  Placement = pos=(62.3,30.3,51.7) rot=(0,0,1;0rad)
  Solid = false
  Source = -> Face082
  Symmetric = false
FEATURE [Part::Feature] Face083
  shape: bbox 3.5 x 17.8 x 2e-07 mm, 1 faces, 0 solids (baked)
FEATURE [Part::Revolution] Revolve087  label="removeToCreateScrewAndThreadedInsertHole024"
  Angle = 360
  Axis = (0,1,0)
  Base = (0,0,0)
  FaceMakerClass = Part::FaceMakerBullseye
  Placement = pos=(30.3,30.3,19.7) rot=(0,0,1;0rad)
  Solid = false
  Source = -> Face083
  Symmetric = false
FEATURE [Part::Feature] Face084
  shape: bbox 3.5 x 17.8 x 2e-07 mm, 1 faces, 0 solids (baked)
FEATURE [Part::Revolution] Revolve088  label="removeToCreateScrewAndThreadedInsertHole025"
  Angle = 360
  Axis = (0,1,0)
  Base = (0,0,0)
  FaceMakerClass = Part::FaceMakerBullseye
  Placement = pos=(30.3,30.3,51.7) rot=(0,0,1;0rad)
  Solid = false
  Source = -> Face084
  Symmetric = false
FEATURE [Part::MultiFuse] Fusion054  label="createThreadedInsertHolesForFan001"
  Shapes = -> [Revolve085,Revolve086,Revolve087,Revolve088]
FEATURE [Part::Cut] Cut018  label="top007"
  Base = -> Fusion040
  Tool = -> Fusion054
FEATURE [Sketcher::SketchObject] Sketch029
  FullyConstrained = false
  Placement = pos=(0,0,0) rot=(1,0,0;1.5708rad)
  sketch-geometry (24):
    g0: ArcOfCircle CenterX=-4 CenterY=-10.5 CenterZ=0 NormalX=0 NormalY=0 NormalZ=1 AngleXU=0 Radius=1.5 StartAngle=6e-16 EndAngle=3.14159
    g1: ArcOfCircle CenterX=-34.2 CenterY=-10.5 CenterZ=0 NormalX=0 NormalY=0 NormalZ=1 AngleXU=0 Radius=1.5 StartAngle=0 EndAngle=3.14159
    g2: ArcOfCircle CenterX=-34.2 CenterY=-27.7 CenterZ=0 NormalX=0 NormalY=0 NormalZ=1 AngleXU=0 Radius=1.5 StartAngle=3.14159 EndAngle=6.28319
    g3: ArcOfCircle CenterX=-4 CenterY=-27.7 CenterZ=0 NormalX=0 NormalY=0 NormalZ=1 AngleXU=0 Radius=1.5 StartAngle=3.1416 EndAngle=6.28319
    g4: ArcOfCircle CenterX=-10 CenterY=-4.3 CenterZ=0 NormalX=0 NormalY=0 NormalZ=1 AngleXU=0 Radius=1.5 StartAngle=2e-16 EndAngle=3.14159
    g5: ArcOfCircle CenterX=-16.1 CenterY=-1.8 CenterZ=0 NormalX=0 NormalY=0 NormalZ=1 AngleXU=0 Radius=1.5 StartAngle=5e-16 EndAngle=3.14159
    g6: ArcOfCircle CenterX=-22.1 CenterY=-1.8 CenterZ=0 NormalX=0 NormalY=0 NormalZ=1 AngleXU=0 Radius=1.5 StartAngle=5e-16 EndAngle=3.14159
    g7: ArcOfCircle CenterX=-28.2 CenterY=-4.3 CenterZ=0 NormalX=0 NormalY=0 NormalZ=1 AngleXU=0 Radius=1.5 StartAngle=2e-16 EndAngle=3.14159
    g8: ArcOfCircle CenterX=-10 CenterY=-33.9 CenterZ=0 NormalX=0 NormalY=0 NormalZ=1 AngleXU=0 Radius=1.5 StartAngle=3.14159 EndAngle=6.28319
    g9: ArcOfCircle CenterX=-16.1 CenterY=-36.4 CenterZ=0 NormalX=0 NormalY=0 NormalZ=1 AngleXU=0 Radius=1.5 StartAngle=3.14159 EndAngle=6.28319
    g10: ArcOfCircle CenterX=-22.1 CenterY=-36.4 CenterZ=0 NormalX=0 NormalY=0 NormalZ=1 AngleXU=0 Radius=1.5 StartAngle=3.14159 EndAngle=6.28319
    g11: ArcOfCircle CenterX=-28.2 CenterY=-33.9 CenterZ=0 NormalX=0 NormalY=0 NormalZ=1 AngleXU=0 Radius=1.5 StartAngle=3.14159 EndAngle=6.28319
    g12: LineSegment StartX=-35.7 StartY=-10.5 StartZ=0 EndX=-35.7 EndY=-27.7 EndZ=0
    g13: LineSegment StartX=-32.7 StartY=-10.5 StartZ=0 EndX=-32.7 EndY=-27.7 EndZ=0
    g14: LineSegment StartX=-29.7 StartY=-33.9 StartZ=0 EndX=-29.7 EndY=-4.3 EndZ=0
    g15: LineSegment StartX=-26.7 StartY=-33.9 StartZ=0 EndX=-26.7 EndY=-4.3 EndZ=0
    g16: LineSegment StartX=-2.5 StartY=-10.5 StartZ=0 EndX=-2.5 EndY=-27.7 EndZ=0
    g17: LineSegment StartX=-8.5 StartY=-4.3 StartZ=0 EndX=-8.5 EndY=-33.9 EndZ=0
    g18: LineSegment StartX=-5.5 StartY=-10.5 StartZ=0 EndX=-5.5 EndY=-27.7 EndZ=0
    g19: LineSegment StartX=-11.5 StartY=-4.3 StartZ=0 EndX=-11.5 EndY=-33.9 EndZ=0
    g20: LineSegment StartX=-14.6 StartY=-1.8 StartZ=0 EndX=-14.6 EndY=-36.4 EndZ=0
    g21: LineSegment StartX=-17.6 StartY=-1.8 StartZ=0 EndX=-17.6 EndY=-36.4 EndZ=0
    g22: LineSegment StartX=-20.6 StartY=-36.4 StartZ=0 EndX=-20.6 EndY=-1.8 EndZ=0
    g23: LineSegment StartX=-23.6 StartY=-1.8 StartZ=0 EndX=-23.6 EndY=-36.4 EndZ=0
  constraints (48):
    c: Block(g0)
    c: Block(g1)
    c: Block(g2)
    c: Block(g3)
    c: Block(g4)
    c: Block(g5)
    c: Block(g6)
    c: Block(g7)
    c: Block(g8)
    c: Block(g9)
    c: Block(g10)
    c: Block(g11)
    c: Coincident(g12,g1)
    c: Coincident(g12,g2)
    c: Vertical(g12)
    c: Coincident(g13,g1)
    c: Coincident(g13,g2)
    c: Vertical(g13)
    c: Coincident(g14,g11)
    c: Coincident(g14,g7)
    c: Vertical(g14)
    c: Coincident(g15,g11)
    c: Coincident(g15,g7)
    c: Vertical(g15)
    c: Coincident(g16,g0)
    c: Coincident(g16,g3)
    c: Vertical(g16)
    c: Coincident(g17,g4)
    c: Coincident(g17,g8)
    c: Vertical(g17)
    c: Coincident(g18,g0)
    c: Coincident(g18,g3)
    c: Vertical(g18)
    c: Coincident(g19,g4)
    c: Coincident(g19,g8)
    c: Vertical(g19)
    c: Coincident(g20,g5)
    c: Coincident(g20,g9)
    c: Vertical(g20)
    c: Coincident(g21,g5)
    c: Coincident(g21,g9)
    c: Vertical(g21)
    c: Coincident(g22,g10)
    c: Coincident(g22,g6)
    c: Vertical(g22)
    c: Coincident(g23,g6)
    c: Coincident(g23,g10)
    c: Vertical(g23)
FEATURE [Part::Extrusion] Extrude020  label="removeToCreateFanGrillHoles"
  Base = -> Sketch029
  Dir = (0,-1,6e-16)
  DirMode = 2
  FaceMakerClass = Part::FaceMakerBullseye
  LengthFwd = 10
  LengthRev = 0
  Placement = pos=(65.4,44,54.82) rot=(0,0,1;0rad)
  Solid = true
  Symmetric = false
FEATURE [Part::MultiFuse] Fusion055  label="top008"
  Shapes = -> [Cut017,Cut018]
FEATURE [Part::Cut] Cut019  label="top009"
  Base = -> Fusion055
  Tool = -> Extrude020
FEATURE [App::MeasureDistance] Distance003  label="Distance: 71.95 mm"
  Distance = 71.9513
  P1 = (117,38,72)
  P2 = (117,38,0.0487319)
FEATURE [Sketcher::SketchObject] Sketch030
  FullyConstrained = true
  Placement = pos=(117,19,0) rot=(0.57735,0.57735,0.57735;2.0944rad)
  sketch-geometry (48):
    g0: LineSegment StartX=-49.19 StartY=69.25 StartZ=0 EndX=-49.19 EndY=66.25 EndZ=0
    g1: LineSegment StartX=-49.19 StartY=63.5 StartZ=0 EndX=-49.19 EndY=60.5 EndZ=0
    g2: LineSegment StartX=-49.19 StartY=57.75 StartZ=0 EndX=-49.19 EndY=54.75 EndZ=0
    g3: LineSegment StartX=-49.19 StartY=52 StartZ=0 EndX=-49.19 EndY=49 EndZ=0
    g4: LineSegment StartX=-49.19 StartY=46.25 StartZ=0 EndX=-49.19 EndY=43.25 EndZ=0
    g5: LineSegment StartX=-49.19 StartY=40.5 StartZ=0 EndX=-49.19 EndY=37.5 EndZ=0
    g6: LineSegment StartX=-49.19 StartY=34.5 StartZ=0 EndX=-49.19 EndY=31.5 EndZ=0
    g7: LineSegment StartX=-49.19 StartY=28.75 StartZ=0 EndX=-49.19 EndY=25.75 EndZ=0
    g8: LineSegment StartX=-49.19 StartY=23 StartZ=0 EndX=-49.19 EndY=20 EndZ=0
    g9: LineSegment StartX=-49.19 StartY=17.25 StartZ=0 EndX=-49.19 EndY=14.25 EndZ=0
    g10: LineSegment StartX=-49.19 StartY=11.5 StartZ=0 EndX=-49.19 EndY=8.5 EndZ=0
    g11: LineSegment StartX=-49.19 StartY=5.75 StartZ=0 EndX=-49.19 EndY=2.75 EndZ=0
    g12: ArcOfCircle CenterX=-1.5 CenterY=67.75 CenterZ=0 NormalX=0 NormalY=0 NormalZ=1 AngleXU=0 Radius=1.5 StartAngle=4.71239 EndAngle=7.85398
    g13: ArcOfCircle CenterX=-1.5 CenterY=62 CenterZ=0 NormalX=0 NormalY=0 NormalZ=1 AngleXU=0 Radius=1.5 StartAngle=4.71239 EndAngle=7.85398
    g14: ArcOfCircle CenterX=-1.5 CenterY=56.25 CenterZ=0 NormalX=0 NormalY=0 NormalZ=1 AngleXU=0 Radius=1.5 StartAngle=4.71239 EndAngle=7.85398
    g15: ArcOfCircle CenterX=-11.49 CenterY=50.5 CenterZ=0 NormalX=0 NormalY=0 NormalZ=1 AngleXU=0 Radius=1.5 StartAngle=4.71239 EndAngle=7.85398
    g16: ArcOfCircle CenterX=-16.28 CenterY=44.75 CenterZ=0 NormalX=0 NormalY=0 NormalZ=1 AngleXU=0 Radius=1.5 StartAngle=4.71239 EndAngle=7.85398
    g17: ArcOfCircle CenterX=-18.2337 CenterY=39 CenterZ=0 NormalX=0 NormalY=0 NormalZ=1 AngleXU=0 Radius=1.5 StartAngle=4.71485 EndAngle=7.85398
    g18: ArcOfCircle CenterX=-16.2837 CenterY=27.25 CenterZ=0 NormalX=0 NormalY=0 NormalZ=1 AngleXU=0 Radius=1.5 StartAngle=4.71485 EndAngle=7.85398
    g19: ArcOfCircle CenterX=-18.2337 CenterY=33 CenterZ=0 NormalX=0 NormalY=0 NormalZ=1 AngleXU=0 Radius=1.5 StartAngle=4.71485 EndAngle=7.85398
    g20: ArcOfCircle CenterX=-11.49 CenterY=21.5 CenterZ=0 NormalX=0 NormalY=0 NormalZ=1 AngleXU=0 Radius=1.5 StartAngle=4.71239 EndAngle=7.85398
    g21: ArcOfCircle CenterX=-1.5 CenterY=4.25 CenterZ=0 NormalX=0 NormalY=0 NormalZ=1 AngleXU=0 Radius=1.5 StartAngle=4.71239 EndAngle=7.85398
    g22: ArcOfCircle CenterX=-1.5 CenterY=10 CenterZ=0 NormalX=0 NormalY=0 NormalZ=1 AngleXU=0 Radius=1.5 StartAngle=4.71239 EndAngle=7.85398
    g23: ArcOfCircle CenterX=-1.5 CenterY=15.75 CenterZ=0 NormalX=0 NormalY=0 NormalZ=1 AngleXU=0 Radius=1.5 StartAngle=4.71239 EndAngle=7.85398
    g24: LineSegment StartX=-49.19 StartY=69.25 StartZ=0 EndX=-1.5 EndY=69.25 EndZ=0
    g25: LineSegment StartX=-49.19 StartY=66.25 StartZ=0 EndX=-1.5 EndY=66.25 EndZ=0
    g26: LineSegment StartX=-49.19 StartY=63.5 StartZ=0 EndX=-1.5 EndY=63.5 EndZ=0
    g27: LineSegment StartX=-49.19 StartY=60.5 StartZ=0 EndX=-1.5 EndY=60.5 EndZ=0
    g28: LineSegment StartX=-49.19 StartY=57.75 StartZ=0 EndX=-1.5 EndY=57.75 EndZ=0
    g29: LineSegment StartX=-49.19 StartY=54.75 StartZ=0 EndX=-1.5 EndY=54.75 EndZ=0
    g30: LineSegment StartX=-49.19 StartY=52 StartZ=0 EndX=-11.49 EndY=52 EndZ=0
    g31: LineSegment StartX=-49.19 StartY=49 StartZ=0 EndX=-11.49 EndY=49 EndZ=0
    g32: LineSegment StartX=-49.19 StartY=46.25 StartZ=0 EndX=-16.28 EndY=46.25 EndZ=0
    g33: LineSegment StartX=-49.19 StartY=43.25 StartZ=0 EndX=-16.28 EndY=43.25 EndZ=0
    g34: LineSegment StartX=-49.19 StartY=40.5 StartZ=0 EndX=-18.2337 EndY=40.5 EndZ=0
    g35: LineSegment StartX=-49.19 StartY=37.5 StartZ=0 EndX=-18.23 EndY=37.5 EndZ=0
    g36: LineSegment StartX=-49.19 StartY=34.5 StartZ=0 EndX=-18.2337 EndY=34.5 EndZ=0
    g37: LineSegment StartX=-49.19 StartY=31.5 StartZ=0 EndX=-18.23 EndY=31.5 EndZ=0
    g38: LineSegment StartX=-49.19 StartY=28.75 StartZ=0 EndX=-16.2837 EndY=28.75 EndZ=0
    g39: LineSegment StartX=-49.19 StartY=25.75 StartZ=0 EndX=-16.28 EndY=25.75 EndZ=0
    g40: LineSegment StartX=-49.19 StartY=23 StartZ=0 EndX=-11.49 EndY=23 EndZ=0
    g41: LineSegment StartX=-49.19 StartY=20 StartZ=0 EndX=-11.49 EndY=20 EndZ=0
    g42: LineSegment StartX=-49.19 StartY=17.25 StartZ=0 EndX=-1.5 EndY=17.25 EndZ=0
    g43: LineSegment StartX=-49.19 StartY=14.25 StartZ=0 EndX=-1.5 EndY=14.25 EndZ=0
    g44: LineSegment StartX=-49.19 StartY=11.5 StartZ=0 EndX=-1.5 EndY=11.5 EndZ=0
    g45: LineSegment StartX=-49.19 StartY=8.5 StartZ=0 EndX=-1.5 EndY=8.5 EndZ=0
    g46: LineSegment StartX=-49.19 StartY=5.75 StartZ=0 EndX=-1.5 EndY=5.75 EndZ=0
    g47: LineSegment StartX=-49.19 StartY=2.75 StartZ=0 EndX=-1.5 EndY=2.75 EndZ=0
  constraints (120):
    c: Vertical(g0)
    c: Distance(g0) = 3
    c: Block(g0)
    c: Vertical(g1)
    c: Distance(g1) = 3
    c: Vertical(g2)
    c: Equal(g0,g2) = 3
    c: Block(g2)
    c: Vertical(g3)
    c: Equal(g1,g3) = 3
    c: Vertical(g4)
    c: Equal(g0,g4) = 3
    c: Block(g4)
    c: Vertical(g5)
    c: Equal(g1,g5) = 3
    c: Vertical(g6)
    c: Equal(g0,g6) = 3
    c: Block(g6)
    c: Vertical(g7)
    c: Equal(g1,g7) = 3
    c: Vertical(g8)
    c: Equal(g0,g8) = 3
    c: Block(g8)
    c: Vertical(g9)
    c: Equal(g1,g9) = 3
    c: Vertical(g10)
    c: Equal(g0,g10) = 3
    c: Block(g10)
    c: Vertical(g11)
    c: Equal(g1,g11) = 3
    c: Block(g12)
    c: Block(g13)
    c: Block(g14)
    c: Block(g15)
    c: Block(g16)
    c: Block(g17)
    c: Block(g18)
    c: Block(g19)
    c: Block(g20)
    c: Block(g21)
    c: Block(g22)
    c: Block(g23)
    c: Block(g11)
    c: Block(g9)
    c: Block(g7)
    c: Block(g5)
    c: Block(g3)
    c: Block(g1)
    c: Coincident(g24,g0)
    c: Coincident(g24,g12)
    c: Horizontal(g24)
    c: Coincident(g25,g0)
    c: Coincident(g25,g12)
    c: Horizontal(g25)
    c: Coincident(g26,g1)
    c: Coincident(g26,g13)
    c: Horizontal(g26)
    c: Coincident(g27,g1)
    c: Coincident(g27,g13)
    c: Horizontal(g27)
    c: Coincident(g28,g2)
    c: Coincident(g28,g14)
    c: Horizontal(g28)
    c: Coincident(g29,g2)
    c: Coincident(g29,g14)
    c: Horizontal(g29)
    c: Coincident(g30,g3)
    c: Coincident(g30,g15)
    c: Horizontal(g30)
    c: Coincident(g31,g3)
    c: Coincident(g31,g15)
    c: Horizontal(g31)
    c: Coincident(g32,g4)
    c: Coincident(g32,g16)
    c: Horizontal(g32)
    c: Coincident(g33,g4)
    c: Coincident(g33,g16)
    c: Horizontal(g33)
    c: Coincident(g34,g5)
    c: Coincident(g34,g17)
    c: Horizontal(g34)
    c: Coincident(g35,g5)
    c: Coincident(g35,g17)
    c: Horizontal(g35)
    c: Coincident(g36,g6)
    c: Coincident(g36,g19)
    c: Horizontal(g36)
    c: Coincident(g37,g6)
    c: Coincident(g37,g19)
    c: Horizontal(g37)
    c: Coincident(g38,g7)
    c: Coincident(g38,g18)
    c: Horizontal(g38)
    c: Coincident(g39,g7)
    c: Coincident(g39,g18)
    c: Horizontal(g39)
    c: Coincident(g40,g8)
    c: Coincident(g40,g20)
    c: Horizontal(g40)
    c: Coincident(g41,g8)
    c: Coincident(g41,g20)
    c: Horizontal(g41)
    c: Coincident(g42,g9)
    c: Coincident(g42,g23)
    c: Horizontal(g42)
    c: Coincident(g43,g9)
    c: Coincident(g43,g23)
    c: Horizontal(g43)
    c: Coincident(g44,g10)
    c: Coincident(g44,g22)
    c: Horizontal(g44)
    c: Coincident(g45,g10)
    c: Coincident(g45,g22)
    c: Horizontal(g45)
    c: Coincident(g46,g11)
    c: Coincident(g46,g21)
    c: Horizontal(g46)
    c: Coincident(g47,g11)
    c: Coincident(g47,g21)
    c: Horizontal(g47)
FEATURE [Sketcher::SketchObject] Sketch031
  FullyConstrained = true
  Placement = pos=(117,19,0) rot=(0.57735,0.57735,0.57735;2.0944rad)
  sketch-geometry (24):
    g0: ArcOfCircle CenterX=-49.19 CenterY=67.75 CenterZ=0 NormalX=0 NormalY=0 NormalZ=1 AngleXU=0 Radius=1.5 StartAngle=1.5708 EndAngle=4.71239
    g1: ArcOfCircle CenterX=-49.19 CenterY=62 CenterZ=0 NormalX=0 NormalY=0 NormalZ=1 AngleXU=0 Radius=1.5 StartAngle=1.5708 EndAngle=4.71239
    g2: ArcOfCircle CenterX=-49.19 CenterY=56.25 CenterZ=0 NormalX=0 NormalY=0 NormalZ=1 AngleXU=0 Radius=1.5 StartAngle=1.5708 EndAngle=4.71239
    g3: ArcOfCircle CenterX=-49.19 CenterY=50.5 CenterZ=0 NormalX=0 NormalY=0 NormalZ=1 AngleXU=0 Radius=1.5 StartAngle=1.5708 EndAngle=4.71239
    g4: ArcOfCircle CenterX=-49.19 CenterY=44.75 CenterZ=0 NormalX=0 NormalY=0 NormalZ=1 AngleXU=0 Radius=1.5 StartAngle=1.5708 EndAngle=4.71239
    g5: ArcOfCircle CenterX=-49.19 CenterY=39 CenterZ=0 NormalX=0 NormalY=0 NormalZ=1 AngleXU=0 Radius=1.5 StartAngle=1.5708 EndAngle=4.71239
    g6: ArcOfCircle CenterX=-49.19 CenterY=33 CenterZ=0 NormalX=0 NormalY=0 NormalZ=1 AngleXU=0 Radius=1.5 StartAngle=1.5708 EndAngle=4.71239
    g7: ArcOfCircle CenterX=-49.19 CenterY=27.25 CenterZ=0 NormalX=0 NormalY=0 NormalZ=1 AngleXU=0 Radius=1.5 StartAngle=1.5708 EndAngle=4.71239
    g8: ArcOfCircle CenterX=-49.19 CenterY=21.5 CenterZ=0 NormalX=0 NormalY=0 NormalZ=1 AngleXU=0 Radius=1.5 StartAngle=1.5708 EndAngle=4.71239
    g9: ArcOfCircle CenterX=-49.19 CenterY=15.75 CenterZ=0 NormalX=0 NormalY=0 NormalZ=1 AngleXU=0 Radius=1.5 StartAngle=1.5708 EndAngle=4.71239
    g10: ArcOfCircle CenterX=-49.19 CenterY=10 CenterZ=0 NormalX=0 NormalY=0 NormalZ=1 AngleXU=0 Radius=1.5 StartAngle=1.5708 EndAngle=4.71239
    g11: ArcOfCircle CenterX=-49.19 CenterY=4.25 CenterZ=0 NormalX=0 NormalY=0 NormalZ=1 AngleXU=0 Radius=1.5 StartAngle=1.5708 EndAngle=4.71239
    g12: LineSegment StartX=-49.19 StartY=69.25 StartZ=0 EndX=-49.19 EndY=66.25 EndZ=0
    g13: LineSegment StartX=-49.19 StartY=63.5 StartZ=0 EndX=-49.19 EndY=60.5 EndZ=0
    g14: LineSegment StartX=-49.19 StartY=57.75 StartZ=0 EndX=-49.19 EndY=54.75 EndZ=0
    g15: LineSegment StartX=-49.19 StartY=52 StartZ=0 EndX=-49.19 EndY=49 EndZ=0
    g16: LineSegment StartX=-49.19 StartY=46.25 StartZ=0 EndX=-49.19 EndY=43.25 EndZ=0
    g17: LineSegment StartX=-49.19 StartY=40.5 StartZ=0 EndX=-49.19 EndY=37.5 EndZ=0
    g18: LineSegment StartX=-49.19 StartY=34.5 StartZ=0 EndX=-49.19 EndY=31.5 EndZ=0
    g19: LineSegment StartX=-49.19 StartY=28.75 StartZ=0 EndX=-49.19 EndY=25.75 EndZ=0
    g20: LineSegment StartX=-49.19 StartY=23 StartZ=0 EndX=-49.19 EndY=20 EndZ=0
    g21: LineSegment StartX=-49.19 StartY=17.25 StartZ=0 EndX=-49.19 EndY=14.25 EndZ=0
    g22: LineSegment StartX=-49.19 StartY=11.5 StartZ=0 EndX=-49.19 EndY=8.5 EndZ=0
    g23: LineSegment StartX=-49.19 StartY=5.75 StartZ=0 EndX=-49.19 EndY=2.75 EndZ=0
  constraints (48):
    c: Block(g0)
    c: Block(g1)
    c: Block(g2)
    c: Block(g3)
    c: Block(g4)
    c: Block(g5)
    c: Block(g6)
    c: Block(g7)
    c: Block(g8)
    c: Block(g9)
    c: Block(g10)
    c: Block(g11)
    c: Coincident(g12,g0)
    c: Coincident(g12,g0)
    c: Vertical(g12)
    c: Vertical(g13)
    c: Coincident(g13,g1)
    c: Vertical(g14)
    c: Coincident(g14,g2)
    c: Vertical(g15)
    c: Coincident(g15,g3)
    c: Vertical(g16)
    c: Coincident(g16,g4)
    c: Vertical(g17)
    c: Coincident(g17,g5)
    c: Vertical(g18)
    c: Coincident(g18,g6)
    c: Vertical(g19)
    c: Coincident(g19,g7)
    c: Vertical(g20)
    c: Coincident(g20,g8)
    c: Vertical(g21)
    c: Coincident(g21,g9)
    c: Vertical(g22)
    c: Coincident(g22,g10)
    c: Vertical(g23)
    c: Coincident(g23,g11)
    c: Block(g23)
    c: Block(g22)
    c: Block(g21)
    c: Block(g20)
    c: Block(g13)
    c: Block(g14)
    c: Block(g15)
    c: Block(g16)
    c: Block(g17)
    c: Block(g18)
    c: Block(g19)
FEATURE [Part::Extrusion] Extrude022
  Base = -> Sketch030
  Dir = (1,-2e-16,2e-16)
  DirMode = 2
  FaceMakerClass = Part::FaceMakerBullseye
  LengthFwd = 19
  LengthRev = 0
  Placement = pos=(-19,0,0) rot=(0,0,1;0rad)
  Solid = true
  Symmetric = false
FEATURE [Part::Fillet] Fillet022
  Base = -> Extrude022
  Edges = 24 edges r=1.49: [Edge6,Edge11,Edge18,Edge23,Edge30,Edge35,Edge42,Edge47,Edge54,Edge59,Edge66,Edge71,Edge78,Edge83,Edge90,Edge95,Edge102,Edge107,Edge114,Edge119,Edge126,Edge131,Edge138,Edge143]
FEATURE [Part::Cut] Cut020  label="top010"
  Base = -> Cut019
  Tool = -> Fillet022
FEATURE [Sketcher::SketchObject] Sketch032
  FullyConstrained = true
  Placement = pos=(117,19,0) rot=(0.57735,0.57735,0.57735;2.0944rad)
  sketch-geometry (48):
    g0: LineSegment StartX=-49.19 StartY=69.25 StartZ=0 EndX=-49.19 EndY=66.25 EndZ=0
    g1: LineSegment StartX=-49.19 StartY=63.5 StartZ=0 EndX=-49.19 EndY=60.5 EndZ=0
    g2: LineSegment StartX=-49.19 StartY=57.75 StartZ=0 EndX=-49.19 EndY=54.75 EndZ=0
    g3: LineSegment StartX=-49.19 StartY=52 StartZ=0 EndX=-49.19 EndY=49 EndZ=0
    g4: LineSegment StartX=-49.19 StartY=46.25 StartZ=0 EndX=-49.19 EndY=43.25 EndZ=0
    g5: LineSegment StartX=-49.19 StartY=40.5 StartZ=0 EndX=-49.19 EndY=37.5 EndZ=0
    g6: LineSegment StartX=-49.19 StartY=34.5 StartZ=0 EndX=-49.19 EndY=31.5 EndZ=0
    g7: LineSegment StartX=-49.19 StartY=28.75 StartZ=0 EndX=-49.19 EndY=25.75 EndZ=0
    g8: LineSegment StartX=-49.19 StartY=23 StartZ=0 EndX=-49.19 EndY=20 EndZ=0
    g9: LineSegment StartX=-49.19 StartY=17.25 StartZ=0 EndX=-49.19 EndY=14.25 EndZ=0
    g10: LineSegment StartX=-49.19 StartY=11.5 StartZ=0 EndX=-49.19 EndY=8.5 EndZ=0
    g11: LineSegment StartX=-49.19 StartY=5.75 StartZ=0 EndX=-49.19 EndY=2.75 EndZ=0
    g12: ArcOfCircle CenterX=-1.5 CenterY=67.75 CenterZ=0 NormalX=0 NormalY=0 NormalZ=1 AngleXU=0 Radius=1.5 StartAngle=4.71239 EndAngle=7.85398
    g13: ArcOfCircle CenterX=-1.5 CenterY=62 CenterZ=0 NormalX=0 NormalY=0 NormalZ=1 AngleXU=0 Radius=1.5 StartAngle=4.71239 EndAngle=7.85398
    g14: ArcOfCircle CenterX=-1.5 CenterY=56.25 CenterZ=0 NormalX=0 NormalY=0 NormalZ=1 AngleXU=0 Radius=1.5 StartAngle=4.71239 EndAngle=7.85398
    g15: ArcOfCircle CenterX=-11.49 CenterY=50.5 CenterZ=0 NormalX=0 NormalY=0 NormalZ=1 AngleXU=0 Radius=1.5 StartAngle=4.71239 EndAngle=7.85398
    g16: ArcOfCircle CenterX=-16.28 CenterY=44.75 CenterZ=0 NormalX=0 NormalY=0 NormalZ=1 AngleXU=0 Radius=1.5 StartAngle=4.71239 EndAngle=7.85398
    g17: ArcOfCircle CenterX=-18.2337 CenterY=39 CenterZ=0 NormalX=0 NormalY=0 NormalZ=1 AngleXU=0 Radius=1.5 StartAngle=4.71485 EndAngle=7.85398
    g18: ArcOfCircle CenterX=-16.2837 CenterY=27.25 CenterZ=0 NormalX=0 NormalY=0 NormalZ=1 AngleXU=0 Radius=1.5 StartAngle=4.71485 EndAngle=7.85398
    g19: ArcOfCircle CenterX=-18.2337 CenterY=33 CenterZ=0 NormalX=0 NormalY=0 NormalZ=1 AngleXU=0 Radius=1.5 StartAngle=4.71485 EndAngle=7.85398
    g20: ArcOfCircle CenterX=-11.49 CenterY=21.5 CenterZ=0 NormalX=0 NormalY=0 NormalZ=1 AngleXU=0 Radius=1.5 StartAngle=4.71239 EndAngle=7.85398
    g21: ArcOfCircle CenterX=-1.5 CenterY=4.25 CenterZ=0 NormalX=0 NormalY=0 NormalZ=1 AngleXU=0 Radius=1.5 StartAngle=4.71239 EndAngle=7.85398
    g22: ArcOfCircle CenterX=-1.5 CenterY=10 CenterZ=0 NormalX=0 NormalY=0 NormalZ=1 AngleXU=0 Radius=1.5 StartAngle=4.71239 EndAngle=7.85398
    g23: ArcOfCircle CenterX=-1.5 CenterY=15.75 CenterZ=0 NormalX=0 NormalY=0 NormalZ=1 AngleXU=0 Radius=1.5 StartAngle=4.71239 EndAngle=7.85398
    g24: LineSegment StartX=-49.19 StartY=69.25 StartZ=0 EndX=-1.5 EndY=69.25 EndZ=0
    g25: LineSegment StartX=-49.19 StartY=66.25 StartZ=0 EndX=-1.5 EndY=66.25 EndZ=0
    g26: LineSegment StartX=-49.19 StartY=63.5 StartZ=0 EndX=-1.5 EndY=63.5 EndZ=0
    g27: LineSegment StartX=-49.19 StartY=60.5 StartZ=0 EndX=-1.5 EndY=60.5 EndZ=0
    g28: LineSegment StartX=-49.19 StartY=57.75 StartZ=0 EndX=-1.5 EndY=57.75 EndZ=0
    g29: LineSegment StartX=-49.19 StartY=54.75 StartZ=0 EndX=-1.5 EndY=54.75 EndZ=0
    g30: LineSegment StartX=-49.19 StartY=52 StartZ=0 EndX=-11.49 EndY=52 EndZ=0
    g31: LineSegment StartX=-49.19 StartY=49 StartZ=0 EndX=-11.49 EndY=49 EndZ=0
    g32: LineSegment StartX=-49.19 StartY=46.25 StartZ=0 EndX=-16.28 EndY=46.25 EndZ=0
    g33: LineSegment StartX=-49.19 StartY=43.25 StartZ=0 EndX=-16.28 EndY=43.25 EndZ=0
    g34: LineSegment StartX=-49.19 StartY=40.5 StartZ=0 EndX=-18.2337 EndY=40.5 EndZ=0
    g35: LineSegment StartX=-49.19 StartY=37.5 StartZ=0 EndX=-18.23 EndY=37.5 EndZ=0
    g36: LineSegment StartX=-49.19 StartY=34.5 StartZ=0 EndX=-18.2337 EndY=34.5 EndZ=0
    g37: LineSegment StartX=-49.19 StartY=31.5 StartZ=0 EndX=-18.23 EndY=31.5 EndZ=0
    g38: LineSegment StartX=-49.19 StartY=28.75 StartZ=0 EndX=-16.2837 EndY=28.75 EndZ=0
    g39: LineSegment StartX=-49.19 StartY=25.75 StartZ=0 EndX=-16.28 EndY=25.75 EndZ=0
    g40: LineSegment StartX=-49.19 StartY=23 StartZ=0 EndX=-11.49 EndY=23 EndZ=0
    g41: LineSegment StartX=-49.19 StartY=20 StartZ=0 EndX=-11.49 EndY=20 EndZ=0
    g42: LineSegment StartX=-49.19 StartY=17.25 StartZ=0 EndX=-1.5 EndY=17.25 EndZ=0
    g43: LineSegment StartX=-49.19 StartY=14.25 StartZ=0 EndX=-1.5 EndY=14.25 EndZ=0
    g44: LineSegment StartX=-49.19 StartY=11.5 StartZ=0 EndX=-1.5 EndY=11.5 EndZ=0
    g45: LineSegment StartX=-49.19 StartY=8.5 StartZ=0 EndX=-1.5 EndY=8.5 EndZ=0
    g46: LineSegment StartX=-49.19 StartY=5.75 StartZ=0 EndX=-1.5 EndY=5.75 EndZ=0
    g47: LineSegment StartX=-49.19 StartY=2.75 StartZ=0 EndX=-1.5 EndY=2.75 EndZ=0
  constraints (120):
    c: Vertical(g0)
    c: Distance(g0) = 3
    c: Block(g0)
    c: Vertical(g1)
    c: Distance(g1) = 3
    c: Vertical(g2)
    c: Equal(g0,g2) = 3
    c: Block(g2)
    c: Vertical(g3)
    c: Equal(g1,g3) = 3
    c: Vertical(g4)
    c: Equal(g0,g4) = 3
    c: Block(g4)
    c: Vertical(g5)
    c: Equal(g1,g5) = 3
    c: Vertical(g6)
    c: Equal(g0,g6) = 3
    c: Block(g6)
    c: Vertical(g7)
    c: Equal(g1,g7) = 3
    c: Vertical(g8)
    c: Equal(g0,g8) = 3
    c: Block(g8)
    c: Vertical(g9)
    c: Equal(g1,g9) = 3
    c: Vertical(g10)
    c: Equal(g0,g10) = 3
    c: Block(g10)
    c: Vertical(g11)
    c: Equal(g1,g11) = 3
    c: Block(g12)
    c: Block(g13)
    c: Block(g14)
    c: Block(g15)
    c: Block(g16)
    c: Block(g17)
    c: Block(g18)
    c: Block(g19)
    c: Block(g20)
    c: Block(g21)
    c: Block(g22)
    c: Block(g23)
    c: Block(g11)
    c: Block(g9)
    c: Block(g7)
    c: Block(g5)
    c: Block(g3)
    c: Block(g1)
    c: Coincident(g24,g0)
    c: Coincident(g24,g12)
    c: Horizontal(g24)
    c: Coincident(g25,g0)
    c: Coincident(g25,g12)
    c: Horizontal(g25)
    c: Coincident(g26,g1)
    c: Coincident(g26,g13)
    c: Horizontal(g26)
    c: Coincident(g27,g1)
    c: Coincident(g27,g13)
    c: Horizontal(g27)
    c: Coincident(g28,g2)
    c: Coincident(g28,g14)
    c: Horizontal(g28)
    c: Coincident(g29,g2)
    c: Coincident(g29,g14)
    c: Horizontal(g29)
    c: Coincident(g30,g3)
    c: Coincident(g30,g15)
    c: Horizontal(g30)
    c: Coincident(g31,g3)
    c: Coincident(g31,g15)
    c: Horizontal(g31)
    c: Coincident(g32,g4)
    c: Coincident(g32,g16)
    c: Horizontal(g32)
    c: Coincident(g33,g4)
    c: Coincident(g33,g16)
    c: Horizontal(g33)
    c: Coincident(g34,g5)
    c: Coincident(g34,g17)
    c: Horizontal(g34)
    c: Coincident(g35,g5)
    c: Coincident(g35,g17)
    c: Horizontal(g35)
    c: Coincident(g36,g6)
    c: Coincident(g36,g19)
    c: Horizontal(g36)
    c: Coincident(g37,g6)
    c: Coincident(g37,g19)
    c: Horizontal(g37)
    c: Coincident(g38,g7)
    c: Coincident(g38,g18)
    c: Horizontal(g38)
    c: Coincident(g39,g7)
    c: Coincident(g39,g18)
    c: Horizontal(g39)
    c: Coincident(g40,g8)
    c: Coincident(g40,g20)
    c: Horizontal(g40)
    c: Coincident(g41,g8)
    c: Coincident(g41,g20)
    c: Horizontal(g41)
    c: Coincident(g42,g9)
    c: Coincident(g42,g23)
    c: Horizontal(g42)
    c: Coincident(g43,g9)
    c: Coincident(g43,g23)
    c: Horizontal(g43)
    c: Coincident(g44,g10)
    c: Coincident(g44,g22)
    c: Horizontal(g44)
    c: Coincident(g45,g10)
    c: Coincident(g45,g22)
    c: Horizontal(g45)
    c: Coincident(g46,g11)
    c: Coincident(g46,g21)
    c: Horizontal(g46)
    c: Coincident(g47,g11)
    c: Coincident(g47,g21)
    c: Horizontal(g47)
FEATURE [Part::Extrusion] Extrude023
  Base = -> Sketch032
  Dir = (1,-2e-16,2e-16)
  DirMode = 2
  FaceMakerClass = Part::FaceMakerBullseye
  LengthFwd = 19
  LengthRev = 0
  Placement = pos=(-19,0,0) rot=(0,0,1;0rad)
  Solid = true
  Symmetric = false
FEATURE [Part::Fillet] Fillet023
  Base = -> Extrude023
  Edges = <same value as first occurrence — deduplicated (x6 in doc)>
  Placement = pos=(0,0.05,0) rot=(0,0,1;0rad)
FEATURE [Part::Cut] Cut014  label="bottom003"
  Base = -> Cut007
  Tool = -> Fusion047
FEATURE [Part::Cut] Cut021  label="bottom004"
  Base = -> Cut014
  Tool = -> Fillet023
FEATURE [Sketcher::SketchObject] Sketch033
  FullyConstrained = true
  Placement = pos=(117,19,0) rot=(0.57735,0.57735,0.57735;2.0944rad)
  sketch-geometry (8):
    g0: LineSegment StartX=-49.19 StartY=69.25 StartZ=0 EndX=-49.19 EndY=66.25 EndZ=0
    g1: LineSegment StartX=-49.19 StartY=5.75 StartZ=0 EndX=-49.19 EndY=2.75 EndZ=0
    g2: ArcOfCircle CenterX=-1.5 CenterY=67.75 CenterZ=0 NormalX=0 NormalY=0 NormalZ=1 AngleXU=0 Radius=1.5 StartAngle=4.71239 EndAngle=7.85398
    g3: ArcOfCircle CenterX=-1.5 CenterY=4.25 CenterZ=0 NormalX=0 NormalY=0 NormalZ=1 AngleXU=0 Radius=1.5 StartAngle=4.71239 EndAngle=7.85398
    g4: LineSegment StartX=-49.19 StartY=69.25 StartZ=0 EndX=-1.5 EndY=69.25 EndZ=0
    g5: LineSegment StartX=-49.19 StartY=66.25 StartZ=0 EndX=-1.5 EndY=66.25 EndZ=0
    g6: LineSegment StartX=-49.19 StartY=5.75 StartZ=0 EndX=-1.5 EndY=5.75 EndZ=0
    g7: LineSegment StartX=-49.19 StartY=2.75 StartZ=0 EndX=-1.5 EndY=2.75 EndZ=0
  constraints (19):
    c: Vertical(g0)
    c: Distance(g0) = 3
    c: Block(g0)
    c: Vertical(g1)
    c: Block(g2)
    c: Block(g3)
    c: Block(g1)
    c: Coincident(g4,g0)
    c: Coincident(g4,g2)
    c: Horizontal(g4)
    c: Coincident(g5,g0)
    c: Coincident(g5,g2)
    c: Horizontal(g5)
    c: Coincident(g6,g1)
    c: Coincident(g6,g3)
    c: Horizontal(g6)
    c: Coincident(g7,g1)
    c: Coincident(g7,g3)
    c: Horizontal(g7)
FEATURE [Sketcher::SketchObject] Sketch034
  FullyConstrained = true
  Placement = pos=(117,19,0) rot=(0.57735,0.57735,0.57735;2.0944rad)
  sketch-geometry (8):
    g0: LineSegment StartX=-49.19 StartY=63.5 StartZ=0 EndX=-49.19 EndY=60.5 EndZ=0
    g1: LineSegment StartX=-49.19 StartY=11.5 StartZ=0 EndX=-49.19 EndY=8.5 EndZ=0
    g2: ArcOfCircle CenterX=-1.5 CenterY=62 CenterZ=0 NormalX=0 NormalY=0 NormalZ=1 AngleXU=0 Radius=1.5 StartAngle=4.71239 EndAngle=7.85398
    g3: ArcOfCircle CenterX=-1.5 CenterY=10 CenterZ=0 NormalX=0 NormalY=0 NormalZ=1 AngleXU=0 Radius=1.5 StartAngle=4.71239 EndAngle=7.85398
    g4: LineSegment StartX=-49.19 StartY=63.5 StartZ=0 EndX=-1.5 EndY=63.5 EndZ=0
    g5: LineSegment StartX=-49.19 StartY=60.5 StartZ=0 EndX=-1.5 EndY=60.5 EndZ=0
    g6: LineSegment StartX=-49.19 StartY=11.5 StartZ=0 EndX=-1.5 EndY=11.5 EndZ=0
    g7: LineSegment StartX=-49.19 StartY=8.5 StartZ=0 EndX=-1.5 EndY=8.5 EndZ=0
  constraints (19):
    c: Vertical(g0)
    c: Distance(g0) = 3
    c: Vertical(g1)
    c: Block(g1)
    c: Block(g2)
    c: Block(g3)
    c: Block(g0)
    c: Coincident(g4,g0)
    c: Coincident(g4,g2)
    c: Horizontal(g4)
    c: Coincident(g5,g0)
    c: Coincident(g5,g2)
    c: Horizontal(g5)
    c: Coincident(g6,g1)
    c: Coincident(g6,g3)
    c: Horizontal(g6)
    c: Coincident(g7,g1)
    c: Coincident(g7,g3)
    c: Horizontal(g7)
FEATURE [Part::Extrusion] Extrude024
  Base = -> Sketch033
  Dir = (1,0,0)
  DirMode = 2
  FaceMakerClass = Part::FaceMakerBullseye
  LengthFwd = 10
  LengthRev = 0
  Solid = true
  Symmetric = false
FEATURE [Part::Extrusion] Extrude025
  Base = -> Sketch034
  Dir = (1,0,0)
  DirMode = 2
  FaceMakerClass = Part::FaceMakerBullseye
  LengthFwd = 10
  LengthRev = 0
  Solid = true
  Symmetric = false
FEATURE [Part::Fillet] Fillet024  label="removeFromtMoreFrontCaseScrewRetainers"
  Base = -> Extrude024
  Edges = 4 edges r=1.49: [Edge6,Edge11,Edge18,Edge23]
  Placement = pos=(-11,0,0) rot=(0,0,1;0rad)
FEATURE [Part::Fillet] Fillet025  label="removeFromtMoreFrontCaseScrewRetainers001"
  Base = -> Extrude025
  Edges = 4 edges r=1.49: [Edge6,Edge11,Edge18,Edge23]
  Placement = pos=(-19,0,0) rot=(0,0,1;0rad)
FEATURE [Part::Cut] Cut022
  Base = -> Cut015
  Tool = -> Fillet025
FEATURE [Part::Cut] Cut023  label="screwRetainers"
  Base = -> Cut022
  Tool = -> Fillet024
FEATURE [Part::MultiFuse] Fusion056  label="bottom005"
  Shapes = -> [Fusion044,Cut021]
FEATURE [Part::MultiFuse] Fusion057  label="casePillars001"
  Shapes = -> [Cut016,Fusion052]
FEATURE [Part::MultiFuse] Fusion058  label="bottom006"
  Shapes = -> [Fusion056,Cut023]
FEATURE [Part::MultiFuse] Fusion059  label="bottom007"
  Shapes = -> [Fusion058,Fillet005]
FEATURE [Part::MultiFuse] Fusion060  label="bottom008"
  Shapes = -> [Fusion059,Fusion]
FEATURE [Part::MultiFuse] Fusion061  label="top011"
  Shapes = -> [Cut006,Cut020]
FEATURE [Part::MultiFuse] Fusion062  label="top012"
  Shapes = -> [Fusion057,Fusion061]
FEATURE [Sketcher::SketchObject] Sketch035  label="topSketch007"
  FullyConstrained = true
  sketch-geometry (6):
    g0: LineSegment StartX=19 StartY=38 StartZ=0 EndX=117 EndY=38 EndZ=0
    g1: ArcOfCircle CenterX=19 CenterY=19 CenterZ=0 NormalX=0 NormalY=0 NormalZ=1 AngleXU=0 Radius=19 StartAngle=1.5708 EndAngle=3.14159
    g2: LineSegment StartX=117 StartY=38 StartZ=0 EndX=117 EndY=19 EndZ=0
    g3: LineSegment StartX=98 StartY=1.0161e-12 StartZ=0 EndX=5.22862e-06 EndY=1.0161e-12 EndZ=0
    g4: LineSegment StartX=5.22862e-06 StartY=19 StartZ=0 EndX=5.22862e-06 EndY=1.0161e-12 EndZ=0
    g5: ArcOfCircle CenterX=98 CenterY=19 CenterZ=0 NormalX=0 NormalY=0 NormalZ=1 AngleXU=0 Radius=19 StartAngle=4.71239 EndAngle=6.28319
  constraints (16):
    c: Horizontal(g0)
    c: Distance(g0) = 98
    c: Coincident(g1,g0)
    c: Block(g1)
    c: Coincident(g2,g0)
    c: Vertical(g2)
    c: Distance(g2) = 19
    c: Horizontal(g3)
    c: Coincident(g4,g1)
    c: Vertical(g4)
    c: Coincident(g3,g4)
    c: Block(g3)
    c: Coincident(g5,g2)
    c: Coincident(g5,g3)
    c: Block(g0)
    c: Block(g5)
FEATURE [Part::Extrusion] Extrude026  label="sideA001"
  Base = -> Sketch035
  Dir = (0,0,1)
  DirMode = 2
  FaceMakerClass = Part::FaceMakerBullseye
  LengthFwd = 3
  LengthRev = 0
  Placement = pos=(0,0,-2.7) rot=(0,0,1;0rad)
  Solid = true
  Symmetric = false
FEATURE [Sketcher::SketchObject] Sketch036  label="topSketch008"
  FullyConstrained = true
  sketch-geometry (6):
    g0: LineSegment StartX=19 StartY=38 StartZ=0 EndX=117 EndY=38 EndZ=0
    g1: ArcOfCircle CenterX=19 CenterY=19 CenterZ=0 NormalX=0 NormalY=0 NormalZ=1 AngleXU=0 Radius=19 StartAngle=1.5708 EndAngle=3.14159
    g2: LineSegment StartX=117 StartY=38 StartZ=0 EndX=117 EndY=19 EndZ=0
    g3: LineSegment StartX=98 StartY=1.0161e-12 StartZ=0 EndX=5.22862e-06 EndY=1.0161e-12 EndZ=0
    g4: LineSegment StartX=5.22862e-06 StartY=19 StartZ=0 EndX=5.22862e-06 EndY=1.0161e-12 EndZ=0
    g5: ArcOfCircle CenterX=98 CenterY=19 CenterZ=0 NormalX=0 NormalY=0 NormalZ=1 AngleXU=0 Radius=19 StartAngle=4.71239 EndAngle=6.28319
  constraints (16):
    c: Horizontal(g0)
    c: Distance(g0) = 98
    c: Coincident(g1,g0)
    c: Block(g1)
    c: Coincident(g2,g0)
    c: Vertical(g2)
    c: Distance(g2) = 19
    c: Horizontal(g3)
    c: Coincident(g4,g1)
    c: Vertical(g4)
    c: Coincident(g3,g4)
    c: Block(g3)
    c: Coincident(g5,g2)
    c: Coincident(g5,g3)
    c: Block(g0)
    c: Block(g5)
FEATURE [Part::Extrusion] Extrude027  label="sideB001"
  Base = -> Sketch036
  Dir = (0,0,1)
  DirMode = 2
  FaceMakerClass = Part::FaceMakerBullseye
  LengthFwd = 3
  LengthRev = 0
  Placement = pos=(0,0,71.7) rot=(0,0,1;0rad)
  Solid = true
  Symmetric = false
FEATURE [Part::MultiFuse] Fusion064  label="removeFromBottom"
  Shapes = -> [Extrude026,Extrude027]
FEATURE [Part::Cut] Cut024  label="bottom009"
  Base = -> Fusion060
  Tool = -> Fusion064
FEATURE [Sketcher::SketchObject] Sketch037  label="topSketch009"
  FullyConstrained = true
  sketch-geometry (8):
    g0: ArcOfCircle CenterX=19 CenterY=19.1201 CenterZ=0 NormalX=0 NormalY=0 NormalZ=1 AngleXU=0 Radius=18.8799 StartAngle=1.5708 EndAngle=3.14793
    g1: LineSegment StartX=0.120501 StartY=19.0004 StartZ=0 EndX=0.120501 EndY=0.000382114 EndZ=0
    g2: LineSegment StartX=19 StartY=38 StartZ=0 EndX=124 EndY=38 EndZ=0
    g3: LineSegment StartX=0.120501 StartY=0.000382114 StartZ=0 EndX=105.121 EndY=0.000382114 EndZ=0
    g4: LineSegment StartX=124 StartY=38 StartZ=0 EndX=125.616 EndY=38 EndZ=0
    g5: LineSegment StartX=105.121 StartY=0.000382114 StartZ=0 EndX=106.736 EndY=0.000382114 EndZ=0
    g6: ArcOfCircle CenterX=106.616 CenterY=19 CenterZ=0 NormalX=0 NormalY=0 NormalZ=1 AngleXU=0 Radius=19 StartAngle=4.71873 EndAngle=6.28319
    g7: LineSegment StartX=125.616 StartY=38 StartZ=0 EndX=125.616 EndY=19 EndZ=0
  constraints (21):
    c: Block(g0)
    c: Coincident(g1,g0)
    c: Vertical(g1)
    c: Horizontal(g2)
    c: Distance(g2) = 105
    c: Coincident(g2,g0)
    c: Distance(g1) = 19
    c: Coincident(g3,g1)
    c: Horizontal(g3)
    c: Distance(g3) = 105
    c: Coincident(g4,g2)
    c: Horizontal(g4)
    c: Distance(g4) = 1.61553
    c: Horizontal(g5)
    c: Equal(g4,g5) = 1.61553
    c: Coincident(g5,g3)
    c: Block(g6)
    c: Coincident(g6,g5)
    c: Coincident(g7,g4)
    c: Coincident(g7,g6)
    c: Vertical(g7)
FEATURE [Part::Extrusion] Extrude028  label="sideB"
  Base = -> Sketch037
  Dir = (0,0,1)
  DirMode = 2
  FaceMakerClass = Part::FaceMakerBullseye
  LengthFwd = 3
  LengthRev = 0
  Placement = pos=(0,0,72) rot=(0,0,1;0rad)
  Solid = true
  Symmetric = false
FEATURE [Sketcher::SketchObject] Sketch038  label="topSketch010"
  FullyConstrained = true
  sketch-geometry (22):
    g0: LineSegment StartX=5.21097e-06 StartY=3 StartZ=0 EndX=5.21097e-06 EndY=19 EndZ=0
    g1: ArcOfCircle CenterX=19 CenterY=19 CenterZ=0 NormalX=0 NormalY=0 NormalZ=1 AngleXU=0 Radius=19 StartAngle=1.5708 EndAngle=3.14159
    g2: ArcOfCircle CenterX=19 CenterY=19 CenterZ=0 NormalX=0 NormalY=0 NormalZ=1 AngleXU=0 Radius=16 StartAngle=1.5708 EndAngle=3.14159
    g3: LineSegment StartX=114 StartY=35 StartZ=0 EndX=19 EndY=35 EndZ=0
    g4: LineSegment StartX=5.21097e-06 StartY=3 StartZ=0 EndX=5.21097e-06 EndY=0 EndZ=0
    g5: LineSegment StartX=3 StartY=0 StartZ=0 EndX=5.21097e-06 EndY=0 EndZ=0
    g6: LineSegment StartX=3 StartY=19 StartZ=0 EndX=3 EndY=0 EndZ=0
    g7: LineSegment StartX=19 StartY=38 StartZ=0 EndX=124 EndY=38 EndZ=0
    g8: Circle CenterX=119 CenterY=35 CenterZ=0 NormalX=0 NormalY=0 NormalZ=1 AngleXU=0 Radius=1
    g9: Circle CenterX=121 CenterY=35 CenterZ=0 NormalX=0 NormalY=0 NormalZ=1 AngleXU=0 Radius=1
    g10: Circle CenterX=121 CenterY=33 CenterZ=0 NormalX=0 NormalY=0 NormalZ=1 AngleXU=0 Radius=1
    g11: BSplineCurve PolesCount=3 KnotsCount=2 Degree=2 IsPeriodic=0
    g12: GeomPoint X=119 Y=35 Z=0
    g13: GeomPoint X=121 Y=33 Z=0
    g14: LineSegment StartX=119 StartY=35 StartZ=0 EndX=114 EndY=35 EndZ=0
    g15: ArcOfCircle CenterX=105 CenterY=19 CenterZ=0 NormalX=0 NormalY=0 NormalZ=1 AngleXU=0 Radius=16 StartAngle=5.60905 EndAngle=6.28319
    g16: LineSegment StartX=121 StartY=33 StartZ=0 EndX=121 EndY=19 EndZ=0
    g17: LineSegment StartX=117.5 StartY=9.01251 StartZ=0 EndX=121.163 EndY=9.0125 EndZ=0
    g18: ArcOfCircle CenterX=105 CenterY=19 CenterZ=0 NormalX=0 NormalY=0 NormalZ=1 AngleXU=0 Radius=20.6155 StartAngle=5.7297 EndAngle=6.28319
    g19: LineSegment StartX=121.163 StartY=9.0125 StartZ=0 EndX=122.538 EndY=8.16329 EndZ=0
    g20: LineSegment StartX=124 StartY=38 StartZ=0 EndX=125.616 EndY=38 EndZ=0
    g21: LineSegment StartX=125.616 StartY=19 StartZ=0 EndX=125.616 EndY=38 EndZ=0
  constraints (49):
    c: Vertical(g0)
    c: Block(g0)
    c: Coincident(g1,g0)
    c: Block(g1)
    c: Coincident(g2,g1)
    c: Block(g2)
    c: Coincident(g3,g2)
    c: Horizontal(g3)
    c: Tangent(g3,g2)
    c: Coincident(g4,g0)
    c: Distance(g4) = 3
    c: Vertical(g4)
    c: Coincident(g5,g4)
    c: Horizontal(g5)
    c: Coincident(g6,g2)
    c: Coincident(g6,g5)
    c: Vertical(g6)
    c: Horizontal(g7)
    c: Distance(g7) = 105
    c: Coincident(g7,g1)
    c: Block(g3)
    c: Weight(g8) = 1
    c: Equal(g8,g9)
    c: Equal(g8,g10)
    c: InternalAlignment(g8,g11)
    c: InternalAlignment(g9,g11)
    c: InternalAlignment(g10,g11)
    c: InternalAlignment(g12,g11)
    c: InternalAlignment(g13,g11)
    c: Block(g11)
    c: Coincident(g14,g11)
    c: Coincident(g14,g3)
    c: Horizontal(g14)
    c: Block(g15)
    c: Coincident(g16,g11)
    c: Coincident(g16,g15)
    c: Vertical(g16)
    c: Distance(g16) = 14
    c: Coincident(g17,g15)
    c: Block(g18)
    c: Coincident(g19,g18)
    c: Coincident(g20,g7)
    c: Horizontal(g20)
    c: Vertical(g21)
    c: Coincident(g20,g21)
    c: Block(g20)
    c: Block(g21)
    c: Block(g19)
    c: Block(g17)
FEATURE [Part::Extrusion] Extrude029
  Base = -> Sketch038
  Dir = (0,0,1)
  DirMode = 2
  FaceMakerClass = Part::FaceMakerBullseye
  LengthFwd = 72
  LengthRev = 0
  Solid = true
  Symmetric = false
FEATURE [Part::Feature] Face085
  shape: bbox 4.8 x 25.5 x 2e-07 mm, 1 faces, 0 solids (baked)
FEATURE [Part::Revolution] Revolve089  label="moreFrontCaseScrewPost003"
  Angle = 360
  Axis = (0,1,0)
  Base = (0,0,0)
  FaceMakerClass = Part::FaceMakerBullseye
  Placement = pos=(109.5,4.5,3.5) rot=(0,0,1;0rad)
  Solid = false
  Source = -> Face085
  Symmetric = false
FEATURE [Part::Feature] Face086
  shape: bbox 4.8 x 25.5 x 2e-07 mm, 1 faces, 0 solids (baked)
FEATURE [Part::Revolution] Revolve090  label="moreFrontCaseScrewPost004"
  Angle = 360
  Axis = (0,1,0)
  Base = (0,0,0)
  FaceMakerClass = Part::FaceMakerBullseye
  Placement = pos=(109.5,4.5,68.5) rot=(0,0,1;0rad)
  Solid = false
  Source = -> Face086
  Symmetric = false
FEATURE [Part::Fillet] Fillet026  label="top013"
  Base = -> Extrude029
  Edges = 1 edges r=2: [Edge35]
FEATURE [Sketcher::SketchObject] Sketch039
  FullyConstrained = true
  sketch-geometry (7):
    g0: LineSegment StartX=0 StartY=0 StartZ=0 EndX=0 EndY=6 EndZ=0
    g1: Circle CenterX=0 CenterY=0 CenterZ=0 NormalX=0 NormalY=0 NormalZ=1 AngleXU=0 Radius=1
    g2: Circle CenterX=8 CenterY=6 CenterZ=0 NormalX=0 NormalY=0 NormalZ=1 AngleXU=0 Radius=1
    g3: BSplineCurve PolesCount=3 KnotsCount=2 Degree=2 IsPeriodic=0
    g4: GeomPoint X=0 Y=0 Z=0
    g5: GeomPoint X=8 Y=6 Z=0
    g6: LineSegment StartX=0 StartY=6 StartZ=0 EndX=8 EndY=6 EndZ=0
  constraints (14):
    c: Coincident(g0,g-1)
    c: Distance(g0) = 6
    c: Vertical(g0)
    c: Coincident(g3,g0)
    c: Weight(g1) = 1
    c: Equal(g1,g2)
    c: InternalAlignment(g1,g3)
    c: InternalAlignment(g2,g3)
    c: InternalAlignment(g4,g3)
    c: InternalAlignment(g5,g3)
    c: Block(g3)
    c: Coincident(g6,g0)
    c: Coincident(g6,g3)
    c: Horizontal(g6)
FEATURE [Sketcher::SketchObject] Sketch040
  FullyConstrained = true
  sketch-geometry (7):
    g0: LineSegment StartX=0 StartY=0 StartZ=0 EndX=0 EndY=6 EndZ=0
    g1: Circle CenterX=0 CenterY=0 CenterZ=0 NormalX=0 NormalY=0 NormalZ=1 AngleXU=0 Radius=1
    g2: Circle CenterX=8 CenterY=6 CenterZ=0 NormalX=0 NormalY=0 NormalZ=1 AngleXU=0 Radius=1
    g3: BSplineCurve PolesCount=3 KnotsCount=2 Degree=2 IsPeriodic=0
    g4: GeomPoint X=0 Y=0 Z=0
    g5: GeomPoint X=8 Y=6 Z=0
    g6: LineSegment StartX=0 StartY=6 StartZ=0 EndX=8 EndY=6 EndZ=0
  constraints (14):
    c: Coincident(g0,g-1)
    c: Distance(g0) = 6
    c: Vertical(g0)
    c: Coincident(g3,g0)
    c: Weight(g1) = 1
    c: Equal(g1,g2)
    c: InternalAlignment(g1,g3)
    c: InternalAlignment(g2,g3)
    c: InternalAlignment(g4,g3)
    c: InternalAlignment(g5,g3)
    c: Block(g3)
    c: Coincident(g6,g0)
    c: Coincident(g6,g3)
    c: Horizontal(g6)
FEATURE [Sketcher::SketchObject] Sketch041
  FullyConstrained = true
  sketch-geometry (7):
    g0: LineSegment StartX=0 StartY=0 StartZ=0 EndX=0 EndY=6 EndZ=0
    g1: Circle CenterX=0 CenterY=0 CenterZ=0 NormalX=0 NormalY=0 NormalZ=1 AngleXU=0 Radius=1
    g2: Circle CenterX=8 CenterY=6 CenterZ=0 NormalX=0 NormalY=0 NormalZ=1 AngleXU=0 Radius=1
    g3: BSplineCurve PolesCount=3 KnotsCount=2 Degree=2 IsPeriodic=0
    g4: GeomPoint X=0 Y=0 Z=0
    g5: GeomPoint X=8 Y=6 Z=0
    g6: LineSegment StartX=0 StartY=6 StartZ=0 EndX=8 EndY=6 EndZ=0
  constraints (14):
    c: Coincident(g0,g-1)
    c: Distance(g0) = 6
    c: Vertical(g0)
    c: Coincident(g3,g0)
    c: Weight(g1) = 1
    c: Equal(g1,g2)
    c: InternalAlignment(g1,g3)
    c: InternalAlignment(g2,g3)
    c: InternalAlignment(g4,g3)
    c: InternalAlignment(g5,g3)
    c: Block(g3)
    c: Coincident(g6,g0)
    c: Coincident(g6,g3)
    c: Horizontal(g6)
FEATURE [Sketcher::SketchObject] Sketch042
  FullyConstrained = true
  sketch-geometry (7):
    g0: LineSegment StartX=0 StartY=0 StartZ=0 EndX=0 EndY=6 EndZ=0
    g1: Circle CenterX=0 CenterY=0 CenterZ=0 NormalX=0 NormalY=0 NormalZ=1 AngleXU=0 Radius=1
    g2: Circle CenterX=8 CenterY=6 CenterZ=0 NormalX=0 NormalY=0 NormalZ=1 AngleXU=0 Radius=1
    g3: BSplineCurve PolesCount=3 KnotsCount=2 Degree=2 IsPeriodic=0
    g4: GeomPoint X=0 Y=0 Z=0
    g5: GeomPoint X=8 Y=6 Z=0
    g6: LineSegment StartX=0 StartY=6 StartZ=0 EndX=8 EndY=6 EndZ=0
  constraints (14):
    c: Coincident(g0,g-1)
    c: Distance(g0) = 6
    c: Vertical(g0)
    c: Coincident(g3,g0)
    c: Weight(g1) = 1
    c: Equal(g1,g2)
    c: InternalAlignment(g1,g3)
    c: InternalAlignment(g2,g3)
    c: InternalAlignment(g4,g3)
    c: InternalAlignment(g5,g3)
    c: Block(g3)
    c: Coincident(g6,g0)
    c: Coincident(g6,g3)
    c: Horizontal(g6)
FEATURE [Part::Extrusion] Extrude030  label="caseScrewPillarBracket008"
  Base = -> Sketch039
  Dir = (0,0,1)
  DirMode = 2
  FaceMakerClass = Part::FaceMakerBullseye
  LengthFwd = 2.4
  LengthRev = 0
  Placement = pos=(15.76,29,8.8) rot=(0,1,0;0rad)
  Solid = true
  Symmetric = false
FEATURE [Part::Extrusion] Extrude031  label="caseScrewPillarBracket009"
  Base = -> Sketch040
  Dir = (0,0,1)
  DirMode = 2
  FaceMakerClass = Part::FaceMakerBullseye
  LengthFwd = 2.4
  LengthRev = 0
  Placement = pos=(15.76,29,60.8) rot=(0,0,1;0rad)
  Solid = true
  Symmetric = false
FEATURE [Part::Extrusion] Extrude032  label="caseScrewPillarBracket010"
  Base = -> Sketch041
  Dir = (0,0,1)
  DirMode = 2
  FaceMakerClass = Part::FaceMakerBullseye
  LengthFwd = 2.4
  LengthRev = 0
  Placement = pos=(13.7,29,13.26) rot=(0,-1,0;1.5708rad)
  Solid = true
  Symmetric = false
FEATURE [Part::Extrusion] Extrude033  label="caseScrewPillarBracket011"
  Base = -> Sketch042
  Dir = (0,0,1)
  DirMode = 2
  FaceMakerClass = Part::FaceMakerBullseye
  LengthFwd = 2.4
  LengthRev = 0
  Placement = pos=(11.3,29,58.74) rot=(0,1,0;1.5708rad)
  Solid = true
  Symmetric = false
FEATURE [Sketcher::SketchObject] Sketch043
  FullyConstrained = true
  sketch-geometry (7):
    g0: LineSegment StartX=0 StartY=0 StartZ=0 EndX=0 EndY=6 EndZ=0
    g1: Circle CenterX=0 CenterY=0 CenterZ=0 NormalX=0 NormalY=0 NormalZ=1 AngleXU=0 Radius=1
    g2: Circle CenterX=8 CenterY=6 CenterZ=0 NormalX=0 NormalY=0 NormalZ=1 AngleXU=0 Radius=1
    g3: BSplineCurve PolesCount=3 KnotsCount=2 Degree=2 IsPeriodic=0
    g4: GeomPoint X=0 Y=0 Z=0
    g5: GeomPoint X=8 Y=6 Z=0
    g6: LineSegment StartX=0 StartY=6 StartZ=0 EndX=8 EndY=6 EndZ=0
  constraints (14):
    c: Coincident(g0,g-1)
    c: Distance(g0) = 6
    c: Vertical(g0)
    c: Coincident(g3,g0)
    c: Weight(g1) = 1
    c: Equal(g1,g2)
    c: InternalAlignment(g1,g3)
    c: InternalAlignment(g2,g3)
    c: InternalAlignment(g4,g3)
    c: InternalAlignment(g5,g3)
    c: Block(g3)
    c: Coincident(g6,g0)
    c: Coincident(g6,g3)
    c: Horizontal(g6)
FEATURE [Part::Extrusion] Extrude034  label="caseScrewPillarBracket012"
  Base = -> Sketch043
  Dir = (0,0,1)
  DirMode = 2
  FaceMakerClass = Part::FaceMakerBullseye
  LengthFwd = 2.4
  LengthRev = 0
  Placement = pos=(88.3,29,65.23) rot=(0,1,0;1.5708rad)
  Solid = true
  Symmetric = false
FEATURE [Sketcher::SketchObject] Sketch044
  FullyConstrained = true
  sketch-geometry (7):
    g0: LineSegment StartX=0 StartY=0 StartZ=0 EndX=0 EndY=6 EndZ=0
    g1: Circle CenterX=0 CenterY=0 CenterZ=0 NormalX=0 NormalY=0 NormalZ=1 AngleXU=0 Radius=1
    g2: Circle CenterX=8 CenterY=6 CenterZ=0 NormalX=0 NormalY=0 NormalZ=1 AngleXU=0 Radius=1
    g3: BSplineCurve PolesCount=3 KnotsCount=2 Degree=2 IsPeriodic=0
    g4: GeomPoint X=0 Y=0 Z=0
    g5: GeomPoint X=8 Y=6 Z=0
    g6: LineSegment StartX=0 StartY=6 StartZ=0 EndX=8 EndY=6 EndZ=0
  constraints (14):
    c: Coincident(g0,g-1)
    c: Distance(g0) = 6
    c: Vertical(g0)
    c: Coincident(g3,g0)
    c: Weight(g1) = 1
    c: Equal(g1,g2)
    c: InternalAlignment(g1,g3)
    c: InternalAlignment(g2,g3)
    c: InternalAlignment(g4,g3)
    c: InternalAlignment(g5,g3)
    c: Block(g3)
    c: Coincident(g6,g0)
    c: Coincident(g6,g3)
    c: Horizontal(g6)
FEATURE [Part::Extrusion] Extrude035  label="caseScrewPillarBracket013"
  Base = -> Sketch044
  Dir = (0,0,1)
  DirMode = 2
  FaceMakerClass = Part::FaceMakerBullseye
  LengthFwd = 2.4
  LengthRev = 0
  Placement = pos=(90.7,29,6.77) rot=(0,-1,0;1.5708rad)
  Solid = true
  Symmetric = false
FEATURE [Sketcher::SketchObject] Sketch045
  FullyConstrained = true
  sketch-geometry (7):
    g0: LineSegment StartX=0 StartY=0 StartZ=0 EndX=0 EndY=6 EndZ=0
    g1: Circle CenterX=0 CenterY=0 CenterZ=0 NormalX=0 NormalY=0 NormalZ=1 AngleXU=0 Radius=1
    g2: Circle CenterX=8 CenterY=6 CenterZ=0 NormalX=0 NormalY=0 NormalZ=1 AngleXU=0 Radius=1
    g3: BSplineCurve PolesCount=3 KnotsCount=2 Degree=2 IsPeriodic=0
    g4: GeomPoint X=0 Y=0 Z=0
    g5: GeomPoint X=8 Y=6 Z=0
    g6: LineSegment StartX=0 StartY=6 StartZ=0 EndX=8 EndY=6 EndZ=0
  constraints (14):
    c: Coincident(g0,g-1)
    c: Distance(g0) = 6
    c: Vertical(g0)
    c: Coincident(g3,g0)
    c: Weight(g1) = 1
    c: Equal(g1,g2)
    c: InternalAlignment(g1,g3)
    c: InternalAlignment(g2,g3)
    c: InternalAlignment(g4,g3)
    c: InternalAlignment(g5,g3)
    c: Block(g3)
    c: Coincident(g6,g0)
    c: Coincident(g6,g3)
    c: Horizontal(g6)
FEATURE [Sketcher::SketchObject] Sketch046
  FullyConstrained = true
  sketch-geometry (7):
    g0: LineSegment StartX=0 StartY=0 StartZ=0 EndX=0 EndY=6 EndZ=0
    g1: Circle CenterX=0 CenterY=0 CenterZ=0 NormalX=0 NormalY=0 NormalZ=1 AngleXU=0 Radius=1
    g2: Circle CenterX=8 CenterY=6 CenterZ=0 NormalX=0 NormalY=0 NormalZ=1 AngleXU=0 Radius=1
    g3: BSplineCurve PolesCount=3 KnotsCount=2 Degree=2 IsPeriodic=0
    g4: GeomPoint X=0 Y=0 Z=0
    g5: GeomPoint X=8 Y=6 Z=0
    g6: LineSegment StartX=0 StartY=6 StartZ=0 EndX=8 EndY=6 EndZ=0
  constraints (14):
    c: Coincident(g0,g-1)
    c: Distance(g0) = 6
    c: Vertical(g0)
    c: Coincident(g3,g0)
    c: Weight(g1) = 1
    c: Equal(g1,g2)
    c: InternalAlignment(g1,g3)
    c: InternalAlignment(g2,g3)
    c: InternalAlignment(g4,g3)
    c: InternalAlignment(g5,g3)
    c: Block(g3)
    c: Coincident(g6,g0)
    c: Coincident(g6,g3)
    c: Horizontal(g6)
FEATURE [Part::Extrusion] Extrude036  label="caseScrewPillarBracket014"
  Base = -> Sketch045
  Dir = (0,0,1)
  DirMode = 2
  FaceMakerClass = Part::FaceMakerBullseye
  LengthFwd = 2.4
  LengthRev = 0
  Placement = pos=(110.7,29,6.77) rot=(0,-1,0;1.5708rad)
  Solid = true
  Symmetric = false
FEATURE [Part::Extrusion] Extrude037  label="caseScrewPillarBracket015"
  Base = -> Sketch046
  Dir = (0,0,1)
  DirMode = 2
  FaceMakerClass = Part::FaceMakerBullseye
  LengthFwd = 2.4
  LengthRev = 0
  Placement = pos=(108.3,29,65.23) rot=(0,1,0;1.5708rad)
  Solid = true
  Symmetric = false
FEATURE [Part::Box] Box013  label="frontCaseScrewPillarBracket002"
  AttacherType = Attacher::AttachEngine3D
  Height = 2.4
  Length = 22
  Placement = pos=(87,28,2.3) rot=(0,0,1;0rad)
  Width = 7
FEATURE [Part::Box] Box014  label="frontCaseScrewPillarBracket003"
  AttacherType = Attacher::AttachEngine3D
  Height = 2.4
  Length = 22
  Placement = pos=(87,28,67.3) rot=(0,0,1;0rad)
  Width = 7
FEATURE [Part::Feature] Face087
  shape: bbox 4.8 x 30.2 x 2e-07 mm, 1 faces, 0 solids (baked)
FEATURE [Part::Revolution] Revolve091  label="frontCaseScrewPost004"
  Angle = 360
  Axis = (0,1,0)
  Base = (0,0,0)
  FaceMakerClass = Part::FaceMakerBullseye
  Placement = pos=(89.5,4.5,3.5) rot=(0,0,1;0rad)
  Solid = false
  Source = -> Face087
  Symmetric = false
FEATURE [Part::Feature] Face088
  shape: bbox 4.8 x 30.2 x 2e-07 mm, 1 faces, 0 solids (baked)
FEATURE [Part::Revolution] Revolve092  label="frontCaseScrewPost005"
  Angle = 360
  Axis = (0,1,0)
  Base = (0,0,0)
  FaceMakerClass = Part::FaceMakerBullseye
  Placement = pos=(89.5,4.5,68.5) rot=(0,0,1;0rad)
  Solid = false
  Source = -> Face088
  Symmetric = false
FEATURE [Part::Feature] Face089
  shape: bbox 3.5 x 30.2 x 2e-07 mm, 1 faces, 0 solids (baked)
FEATURE [Part::Revolution] Revolve093  label="backCaseScrewPost002"
  Angle = 360
  Axis = (0,1,0)
  Base = (0,0,0)
  FaceMakerClass = Part::FaceMakerBullseye
  Placement = pos=(12.5,4.5,10) rot=(0,0,1;0rad)
  Solid = false
  Source = -> Face089
  Symmetric = false
FEATURE [Part::Feature] Face090
  shape: bbox 3.5 x 30.2 x 2e-07 mm, 1 faces, 0 solids (baked)
FEATURE [Part::Revolution] Revolve094  label="backCaseScrewPost003"
  Angle = 360
  Axis = (0,1,0)
  Base = (0,0,0)
  FaceMakerClass = Part::FaceMakerBullseye
  Placement = pos=(12.5,4.5,62) rot=(0,0,1;0rad)
  Solid = false
  Source = -> Face090
  Symmetric = false
FEATURE [Part::Box] Box015  label="Cube011"
  AttacherType = Attacher::AttachEngine3D
  Height = 28.8
  Length = 3
  Placement = pos=(107.3,28,21.6) rot=(0,0,1;0rad)
  Width = 7
FEATURE [Part::Box] Box016  label="Cube012"
  AttacherType = Attacher::AttachEngine3D
  Height = 3
  Length = 7.4
  Placement = pos=(107.3,28,18.6) rot=(0,0,1;0rad)
  Width = 7
FEATURE [Part::Box] Box017  label="Cube013"
  AttacherType = Attacher::AttachEngine3D
  Height = 3
  Length = 7.4
  Placement = pos=(107.3,28,50.4) rot=(0,0,1;0rad)
  Width = 7
FEATURE [Part::Cylinder] Cylinder024
  Angle = 360
  AttacherType = Attacher::AttachEngine3D
  Height = 20
  Placement = pos=(0,0,36.15) rot=(0,0,1;0rad)
  Radius = 14.3
FEATURE [Part::Cylinder] Cylinder025
  Angle = 360
  AttacherType = Attacher::AttachEngine3D
  Height = 10
  Placement = pos=(0,0,36.15) rot=(0,0,1;0rad)
  Radius = 4
FEATURE [Part::MultiFuse] Fusion066  label="removeToCreteHoleForPlugHousing009"
  Placement = pos=(70,19,36) rot=(0,1,0;1.5708rad)
  Shapes = -> [Cylinder024,Cylinder025]
FEATURE [Part::MultiFuse] Fusion065  label="plugHousingBracketHolder002"
  Shapes = -> [Box017,Box015,Box016]
FEATURE [Part::Cut] Cut025  label="plugHousingBracketHolder003"
  Base = -> Fusion065
  Placement = pos=(7,0,0) rot=(0,0,1;0rad)
  Tool = -> Fusion066
FEATURE [Sketcher::SketchObject] Sketch047
  FullyConstrained = false
  Placement = pos=(0,0,0) rot=(1,0,0;1.5708rad)
  sketch-geometry (24):
    g0: ArcOfCircle CenterX=-4 CenterY=-10.5 CenterZ=0 NormalX=0 NormalY=0 NormalZ=1 AngleXU=0 Radius=1.5 StartAngle=6e-16 EndAngle=3.14159
    g1: ArcOfCircle CenterX=-34.2 CenterY=-10.5 CenterZ=0 NormalX=0 NormalY=0 NormalZ=1 AngleXU=0 Radius=1.5 StartAngle=0 EndAngle=3.14159
    g2: ArcOfCircle CenterX=-34.2 CenterY=-27.7 CenterZ=0 NormalX=0 NormalY=0 NormalZ=1 AngleXU=0 Radius=1.5 StartAngle=3.14159 EndAngle=6.28319
    g3: ArcOfCircle CenterX=-4 CenterY=-27.7 CenterZ=0 NormalX=0 NormalY=0 NormalZ=1 AngleXU=0 Radius=1.5 StartAngle=3.1416 EndAngle=6.28319
    g4: ArcOfCircle CenterX=-10 CenterY=-4.3 CenterZ=0 NormalX=0 NormalY=0 NormalZ=1 AngleXU=0 Radius=1.5 StartAngle=2e-16 EndAngle=3.14159
    g5: ArcOfCircle CenterX=-16.1 CenterY=-1.8 CenterZ=0 NormalX=0 NormalY=0 NormalZ=1 AngleXU=0 Radius=1.5 StartAngle=5e-16 EndAngle=3.14159
    g6: ArcOfCircle CenterX=-22.1 CenterY=-1.8 CenterZ=0 NormalX=0 NormalY=0 NormalZ=1 AngleXU=0 Radius=1.5 StartAngle=5e-16 EndAngle=3.14159
    g7: ArcOfCircle CenterX=-28.2 CenterY=-4.3 CenterZ=0 NormalX=0 NormalY=0 NormalZ=1 AngleXU=0 Radius=1.5 StartAngle=2e-16 EndAngle=3.14159
    g8: ArcOfCircle CenterX=-10 CenterY=-33.9 CenterZ=0 NormalX=0 NormalY=0 NormalZ=1 AngleXU=0 Radius=1.5 StartAngle=3.14159 EndAngle=6.28319
    g9: ArcOfCircle CenterX=-16.1 CenterY=-36.4 CenterZ=0 NormalX=0 NormalY=0 NormalZ=1 AngleXU=0 Radius=1.5 StartAngle=3.14159 EndAngle=6.28319
    g10: ArcOfCircle CenterX=-22.1 CenterY=-36.4 CenterZ=0 NormalX=0 NormalY=0 NormalZ=1 AngleXU=0 Radius=1.5 StartAngle=3.14159 EndAngle=6.28319
    g11: ArcOfCircle CenterX=-28.2 CenterY=-33.9 CenterZ=0 NormalX=0 NormalY=0 NormalZ=1 AngleXU=0 Radius=1.5 StartAngle=3.14159 EndAngle=6.28319
    g12: LineSegment StartX=-35.7 StartY=-10.5 StartZ=0 EndX=-35.7 EndY=-27.7 EndZ=0
    g13: LineSegment StartX=-32.7 StartY=-10.5 StartZ=0 EndX=-32.7 EndY=-27.7 EndZ=0
    g14: LineSegment StartX=-29.7 StartY=-33.9 StartZ=0 EndX=-29.7 EndY=-4.3 EndZ=0
    g15: LineSegment StartX=-26.7 StartY=-33.9 StartZ=0 EndX=-26.7 EndY=-4.3 EndZ=0
    g16: LineSegment StartX=-2.5 StartY=-10.5 StartZ=0 EndX=-2.5 EndY=-27.7 EndZ=0
    g17: LineSegment StartX=-8.5 StartY=-4.3 StartZ=0 EndX=-8.5 EndY=-33.9 EndZ=0
    g18: LineSegment StartX=-5.5 StartY=-10.5 StartZ=0 EndX=-5.5 EndY=-27.7 EndZ=0
    g19: LineSegment StartX=-11.5 StartY=-4.3 StartZ=0 EndX=-11.5 EndY=-33.9 EndZ=0
    g20: LineSegment StartX=-14.6 StartY=-1.8 StartZ=0 EndX=-14.6 EndY=-36.4 EndZ=0
    g21: LineSegment StartX=-17.6 StartY=-1.8 StartZ=0 EndX=-17.6 EndY=-36.4 EndZ=0
    g22: LineSegment StartX=-20.6 StartY=-36.4 StartZ=0 EndX=-20.6 EndY=-1.8 EndZ=0
    g23: LineSegment StartX=-23.6 StartY=-1.8 StartZ=0 EndX=-23.6 EndY=-36.4 EndZ=0
  constraints (48):
    c: Block(g0)
    c: Block(g1)
    c: Block(g2)
    c: Block(g3)
    c: Block(g4)
    c: Block(g5)
    c: Block(g6)
    c: Block(g7)
    c: Block(g8)
    c: Block(g9)
    c: Block(g10)
    c: Block(g11)
    c: Coincident(g12,g1)
    c: Coincident(g12,g2)
    c: Vertical(g12)
    c: Coincident(g13,g1)
    c: Coincident(g13,g2)
    c: Vertical(g13)
    c: Coincident(g14,g11)
    c: Coincident(g14,g7)
    c: Vertical(g14)
    c: Coincident(g15,g11)
    c: Coincident(g15,g7)
    c: Vertical(g15)
    c: Coincident(g16,g0)
    c: Coincident(g16,g3)
    c: Vertical(g16)
    c: Coincident(g17,g4)
    c: Coincident(g17,g8)
    c: Vertical(g17)
    c: Coincident(g18,g0)
    c: Coincident(g18,g3)
    c: Vertical(g18)
    c: Coincident(g19,g4)
    c: Coincident(g19,g8)
    c: Vertical(g19)
    c: Coincident(g20,g5)
    c: Coincident(g20,g9)
    c: Vertical(g20)
    c: Coincident(g21,g5)
    c: Coincident(g21,g9)
    c: Vertical(g21)
    c: Coincident(g22,g10)
    c: Coincident(g22,g6)
    c: Vertical(g22)
    c: Coincident(g23,g6)
    c: Coincident(g23,g10)
    c: Vertical(g23)
FEATURE [Part::Extrusion] Extrude038  label="removeToCreateFanGrillHoles001"
  Base = -> Sketch047
  Dir = (0,-1,6e-16)
  DirMode = 2
  FaceMakerClass = Part::FaceMakerBullseye
  LengthFwd = 10
  LengthRev = 0
  Placement = pos=(65.4,44,54.82) rot=(0,0,1;0rad)
  Solid = true
  Symmetric = false
FEATURE [Part::Feature] Wire004
  shape: bbox 11 x 5.2 x 2e-07 mm, 0 faces, 0 solids (baked)
FEATURE [Part::Revolution] Revolve095
  Angle = 360
  Axis = (0,1,0)
  Base = (0,0,0)
  FaceMakerClass = Part::FaceMakerBullseye
  Placement = pos=(30.3,38,19.7) rot=(0,0,1;0rad)
  Solid = true
  Source = -> Wire004
  Symmetric = false
FEATURE [Part::Feature] Wire005
  shape: bbox 11 x 5.2 x 2e-07 mm, 0 faces, 0 solids (baked)
FEATURE [Part::Revolution] Revolve096
  Angle = 360
  Axis = (0,1,0)
  Base = (0,0,0)
  FaceMakerClass = Part::FaceMakerBullseye
  Placement = pos=(30.3,38,51.7) rot=(0,0,1;0rad)
  Solid = true
  Source = -> Wire005
  Symmetric = false
FEATURE [Part::Feature] Wire006
  shape: bbox 11 x 5.2 x 2e-07 mm, 0 faces, 0 solids (baked)
FEATURE [Part::Revolution] Revolve097
  Angle = 360
  Axis = (0,1,0)
  Base = (0,0,0)
  FaceMakerClass = Part::FaceMakerBullseye
  Placement = pos=(62.3,38,51.7) rot=(0,0,1;0rad)
  Solid = true
  Source = -> Wire006
  Symmetric = false
FEATURE [Part::Feature] Wire007
  shape: bbox 11 x 5.2 x 2e-07 mm, 0 faces, 0 solids (baked)
FEATURE [Part::Revolution] Revolve098
  Angle = 360
  Axis = (0,1,0)
  Base = (0,0,0)
  FaceMakerClass = Part::FaceMakerBullseye
  Placement = pos=(62.3,38,19.7) rot=(0,0,1;0rad)
  Solid = true
  Source = -> Wire007
  Symmetric = false
FEATURE [Part::MultiFuse] Fusion067  label="fanScrewHousing002"
  Shapes = -> [Revolve098,Revolve097,Revolve096,Revolve095]
FEATURE [Part::Feature] Face091 .. Face094  x4 (patterned run collapsed; names and placements below)
  shape: bbox 3.5 x 17.8 x 2e-07 mm, 1 faces, 0 solids (baked)
FEATURE [Part::Revolution] Revolve099  label="removeToCreateScrewAndThreadedInsertHole026"
  Angle = 360
  Axis = (0,1,0)
  Base = (0,0,0)
  FaceMakerClass = Part::FaceMakerBullseye
  Placement = pos=(62.3,30.3,19.7) rot=(0,0,1;0rad)
  Solid = false
  Source = -> Face091
  Symmetric = false
FEATURE [Part::Revolution] Revolve100  label="removeToCreateScrewAndThreadedInsertHole027"
  Angle = 360
  Axis = (0,1,0)
  Base = (0,0,0)
  FaceMakerClass = Part::FaceMakerBullseye
  Placement = pos=(62.3,30.3,51.7) rot=(0,0,1;0rad)
  Solid = false
  Source = -> Face092
  Symmetric = false
FEATURE [Part::Revolution] Revolve101  label="removeToCreateScrewAndThreadedInsertHole028"
  Angle = 360
  Axis = (0,1,0)
  Base = (0,0,0)
  FaceMakerClass = Part::FaceMakerBullseye
  Placement = pos=(30.3,30.3,19.7) rot=(0,0,1;0rad)
  Solid = false
  Source = -> Face093
  Symmetric = false
FEATURE [Part::Revolution] Revolve102  label="removeToCreateScrewAndThreadedInsertHole029"
  Angle = 360
  Axis = (0,1,0)
  Base = (0,0,0)
  FaceMakerClass = Part::FaceMakerBullseye
  Placement = pos=(30.3,30.3,51.7) rot=(0,0,1;0rad)
  Solid = false
  Source = -> Face094
  Symmetric = false
FEATURE [Part::MultiFuse] Fusion068  label="createThreadedInsertHolesForFan002"
  Shapes = -> [Revolve099,Revolve100,Revolve101,Revolve102]
FEATURE [Part::Cut] Cut026  label="fanScrewHousing003"
  Base = -> Fusion067
  Tool = -> Fusion068
FEATURE [Sketcher::SketchObject] Sketch048
  FullyConstrained = false
  Placement = pos=(0,0,0) rot=(1,0,0;1.5708rad)
  sketch-geometry (24):
    g0: ArcOfCircle CenterX=-4 CenterY=-10.5 CenterZ=0 NormalX=0 NormalY=0 NormalZ=1 AngleXU=0 Radius=1.5 StartAngle=6e-16 EndAngle=3.14159
    g1: ArcOfCircle CenterX=-34.2 CenterY=-10.5 CenterZ=0 NormalX=0 NormalY=0 NormalZ=1 AngleXU=0 Radius=1.5 StartAngle=0 EndAngle=3.14159
    g2: ArcOfCircle CenterX=-34.2 CenterY=-27.7 CenterZ=0 NormalX=0 NormalY=0 NormalZ=1 AngleXU=0 Radius=1.5 StartAngle=3.14159 EndAngle=6.28319
    g3: ArcOfCircle CenterX=-4 CenterY=-27.7 CenterZ=0 NormalX=0 NormalY=0 NormalZ=1 AngleXU=0 Radius=1.5 StartAngle=3.1416 EndAngle=6.28319
    g4: ArcOfCircle CenterX=-10 CenterY=-4.3 CenterZ=0 NormalX=0 NormalY=0 NormalZ=1 AngleXU=0 Radius=1.5 StartAngle=2e-16 EndAngle=3.14159
    g5: ArcOfCircle CenterX=-16.1 CenterY=-1.8 CenterZ=0 NormalX=0 NormalY=0 NormalZ=1 AngleXU=0 Radius=1.5 StartAngle=5e-16 EndAngle=3.14159
    g6: ArcOfCircle CenterX=-22.1 CenterY=-1.8 CenterZ=0 NormalX=0 NormalY=0 NormalZ=1 AngleXU=0 Radius=1.5 StartAngle=5e-16 EndAngle=3.14159
    g7: ArcOfCircle CenterX=-28.2 CenterY=-4.3 CenterZ=0 NormalX=0 NormalY=0 NormalZ=1 AngleXU=0 Radius=1.5 StartAngle=2e-16 EndAngle=3.14159
    g8: ArcOfCircle CenterX=-10 CenterY=-33.9 CenterZ=0 NormalX=0 NormalY=0 NormalZ=1 AngleXU=0 Radius=1.5 StartAngle=3.14159 EndAngle=6.28319
    g9: ArcOfCircle CenterX=-16.1 CenterY=-36.4 CenterZ=0 NormalX=0 NormalY=0 NormalZ=1 AngleXU=0 Radius=1.5 StartAngle=3.14159 EndAngle=6.28319
    g10: ArcOfCircle CenterX=-22.1 CenterY=-36.4 CenterZ=0 NormalX=0 NormalY=0 NormalZ=1 AngleXU=0 Radius=1.5 StartAngle=3.14159 EndAngle=6.28319
    g11: ArcOfCircle CenterX=-28.2 CenterY=-33.9 CenterZ=0 NormalX=0 NormalY=0 NormalZ=1 AngleXU=0 Radius=1.5 StartAngle=3.14159 EndAngle=6.28319
    g12: LineSegment StartX=-35.7 StartY=-10.5 StartZ=0 EndX=-35.7 EndY=-27.7 EndZ=0
    g13: LineSegment StartX=-32.7 StartY=-10.5 StartZ=0 EndX=-32.7 EndY=-27.7 EndZ=0
    g14: LineSegment StartX=-29.7 StartY=-33.9 StartZ=0 EndX=-29.7 EndY=-4.3 EndZ=0
    g15: LineSegment StartX=-26.7 StartY=-33.9 StartZ=0 EndX=-26.7 EndY=-4.3 EndZ=0
    g16: LineSegment StartX=-2.5 StartY=-10.5 StartZ=0 EndX=-2.5 EndY=-27.7 EndZ=0
    g17: LineSegment StartX=-8.5 StartY=-4.3 StartZ=0 EndX=-8.5 EndY=-33.9 EndZ=0
    g18: LineSegment StartX=-5.5 StartY=-10.5 StartZ=0 EndX=-5.5 EndY=-27.7 EndZ=0
    g19: LineSegment StartX=-11.5 StartY=-4.3 StartZ=0 EndX=-11.5 EndY=-33.9 EndZ=0
    g20: LineSegment StartX=-14.6 StartY=-1.8 StartZ=0 EndX=-14.6 EndY=-36.4 EndZ=0
    g21: LineSegment StartX=-17.6 StartY=-1.8 StartZ=0 EndX=-17.6 EndY=-36.4 EndZ=0
    g22: LineSegment StartX=-20.6 StartY=-36.4 StartZ=0 EndX=-20.6 EndY=-1.8 EndZ=0
    g23: LineSegment StartX=-23.6 StartY=-1.8 StartZ=0 EndX=-23.6 EndY=-36.4 EndZ=0
  constraints (48):
    c: Block(g0)
    c: Block(g1)
    c: Block(g2)
    c: Block(g3)
    c: Block(g4)
    c: Block(g5)
    c: Block(g6)
    c: Block(g7)
    c: Block(g8)
    c: Block(g9)
    c: Block(g10)
    c: Block(g11)
    c: Coincident(g12,g1)
    c: Coincident(g12,g2)
    c: Vertical(g12)
    c: Coincident(g13,g1)
    c: Coincident(g13,g2)
    c: Vertical(g13)
    c: Coincident(g14,g11)
    c: Coincident(g14,g7)
    c: Vertical(g14)
    c: Coincident(g15,g11)
    c: Coincident(g15,g7)
    c: Vertical(g15)
    c: Coincident(g16,g0)
    c: Coincident(g16,g3)
    c: Vertical(g16)
    c: Coincident(g17,g4)
    c: Coincident(g17,g8)
    c: Vertical(g17)
    c: Coincident(g18,g0)
    c: Coincident(g18,g3)
    c: Vertical(g18)
    c: Coincident(g19,g4)
    c: Coincident(g19,g8)
    c: Vertical(g19)
    c: Coincident(g20,g5)
    c: Coincident(g20,g9)
    c: Vertical(g20)
    c: Coincident(g21,g5)
    c: Coincident(g21,g9)
    c: Vertical(g21)
    c: Coincident(g22,g10)
    c: Coincident(g22,g6)
    c: Vertical(g22)
    c: Coincident(g23,g6)
    c: Coincident(g23,g10)
    c: Vertical(g23)
FEATURE [Part::Extrusion] Extrude039  label="removeToCreateFanGrillHoles002"
  Base = -> Sketch048
  Dir = (0,-1,6e-16)
  DirMode = 2
  FaceMakerClass = Part::FaceMakerBullseye
  LengthFwd = 10
  LengthRev = 0
  Placement = pos=(65.4,44,54.82) rot=(0,0,1;0rad)
  Solid = true
  Symmetric = false
FEATURE [Part::Cut] Cut027  label="fanScrewHousing004"
  Base = -> Cut026
  Tool = -> Extrude038
FEATURE [Part::Cut] Cut028  label="top014"
  Base = -> Fillet026
  Tool = -> Extrude039
FEATURE [Part::Feature] Face095 .. Face098  x4 (patterned run collapsed; names and placements below)
  shape: bbox 3.5 x 17.8 x 2e-07 mm, 1 faces, 0 solids (baked)
FEATURE [Part::Revolution] Revolve103  label="removeToCreateScrewAndThreadedInsertHole030"
  Angle = 360
  Axis = (0,1,0)
  Base = (0,0,0)
  FaceMakerClass = Part::FaceMakerBullseye
  Placement = pos=(62.3,30.3,19.7) rot=(0,0,1;0rad)
  Solid = false
  Source = -> Face095
  Symmetric = false
FEATURE [Part::Revolution] Revolve104  label="removeToCreateScrewAndThreadedInsertHole031"
  Angle = 360
  Axis = (0,1,0)
  Base = (0,0,0)
  FaceMakerClass = Part::FaceMakerBullseye
  Placement = pos=(62.3,30.3,51.7) rot=(0,0,1;0rad)
  Solid = false
  Source = -> Face096
  Symmetric = false
FEATURE [Part::Revolution] Revolve105  label="removeToCreateScrewAndThreadedInsertHole032"
  Angle = 360
  Axis = (0,1,0)
  Base = (0,0,0)
  FaceMakerClass = Part::FaceMakerBullseye
  Placement = pos=(30.3,30.3,19.7) rot=(0,0,1;0rad)
  Solid = false
  Source = -> Face097
  Symmetric = false
FEATURE [Part::Revolution] Revolve106  label="removeToCreateScrewAndThreadedInsertHole033"
  Angle = 360
  Axis = (0,1,0)
  Base = (0,0,0)
  FaceMakerClass = Part::FaceMakerBullseye
  Placement = pos=(30.3,30.3,51.7) rot=(0,0,1;0rad)
  Solid = false
  Source = -> Face098
  Symmetric = false
FEATURE [Part::MultiFuse] Fusion069  label="createThreadedInsertHolesForFan003"
  Shapes = -> [Revolve103,Revolve104,Revolve105,Revolve106]
FEATURE [Part::Cut] Cut029  label="top015"
  Base = -> Cut028
  Tool = -> Fusion054
FEATURE [Part::Cut] Cut030  label="fanScrewHousing005"
  Base = -> Cut027
  Tool = -> Fusion069
FEATURE [Part::Cylinder] Cylinder026  label="removeToCreteHoleForPlugHousing010"
  Angle = 360
  AttacherType = Attacher::AttachEngine3D
  Height = 20
  Placement = pos=(-2,19,36) rot=(0,1,0;1.5708rad)
  Radius = 14.3
FEATURE [Part::Box] Box018  label="removeToCreteHoleForPlugHousing011"
  AttacherType = Attacher::AttachEngine3D
  Height = 28.6
  Length = 10
  Placement = pos=(-2,0,21.7) rot=(0,0,1;0rad)
  Width = 19
FEATURE [Part::Box] Box019  label="wireHolderBottomCaseBit"
  AttacherType = Attacher::AttachEngine3D
  Height = 28
  Length = 3
  Placement = pos=(0,0,22) rot=(0,0,1;0rad)
  Width = 21
FEATURE [Part::Cylinder] Cylinder027  label="removeToCreteHoleForPlugHousing012"
  Angle = 360
  AttacherType = Attacher::AttachEngine3D
  Height = 20
  Placement = pos=(-2,19,36) rot=(0,1,0;1.5708rad)
  Radius = 14.3
FEATURE [Part::Cut] Cut031  label="wireHolderBottomCaseBit001"
  Base = -> Box019
  Tool = -> Cylinder027
FEATURE [Part::MultiFuse] Fusion070  label="removeToCreteHoleForPlugHousing013"
  Shapes = -> [Box018,Cylinder026]
FEATURE [Part::Cut] Cut032  label="top016"
  Base = -> Cut029
  Tool = -> Fusion070
FEATURE [Part::Cylinder] Cylinder028
  Angle = 360
  AttacherType = Attacher::AttachEngine3D
  Height = 20
  Placement = pos=(0,0,36.15) rot=(0,0,1;0rad)
  Radius = 14.3
FEATURE [Part::Cylinder] Cylinder029
  Angle = 360
  AttacherType = Attacher::AttachEngine3D
  Height = 10
  Placement = pos=(0,0,36.15) rot=(0,0,1;0rad)
  Radius = 4
FEATURE [Part::MultiFuse] Fusion071  label="removeToCreteHoleForPlugHousing014"
  Placement = pos=(70,19,36) rot=(0,1,0;1.5708rad)
  Shapes = -> [Cylinder028,Cylinder029]
FEATURE [Sketcher::SketchObject] Sketch049  label="topSketch011"
  FullyConstrained = true
  sketch-geometry (4):
    g0: ArcOfCircle CenterX=105 CenterY=19 CenterZ=0 NormalX=0 NormalY=0 NormalZ=1 AngleXU=0 Radius=20.6155 StartAngle=5.54125 EndAngle=6.28319
    g1: ArcOfCircle CenterX=105 CenterY=19 CenterZ=0 NormalX=0 NormalY=0 NormalZ=1 AngleXU=0 Radius=13 StartAngle=5.54125 EndAngle=6.28319
    g2: LineSegment StartX=118 StartY=19 StartZ=0 EndX=125.616 EndY=19 EndZ=0
    g3: LineSegment StartX=114.583 StartY=10.2157 StartZ=0 EndX=120.197 EndY=5.06982 EndZ=0
  constraints (7):
    c: Block(g0)
    c: Block(g1)
    c: Coincident(g2,g1)
    c: Coincident(g2,g0)
    c: Horizontal(g2)
    c: Coincident(g3,g1)
    c: Coincident(g3,g0)
FEATURE [Part::Box] Box020  label="removeToCreteHoleForPlugHousing015"
  AttacherType = Attacher::AttachEngine3D
  Height = 28.6
  Length = 20
  Placement = pos=(106.15,0,21.7) rot=(0,0,1;0rad)
  Width = 19
FEATURE [Part::MultiFuse] Fusion072  label="removeToCreteHoleForPlugHousing016"
  Shapes = -> [Box020,Fusion071]
FEATURE [Part::Cut] Cut033  label="removeToCreteHoleForPlugHousing017"
  Base = -> Cut032
  Tool = -> Fusion072
FEATURE [Part::Cylinder] Cylinder030
  Angle = 360
  AttacherType = Attacher::AttachEngine3D
  Height = 20
  Placement = pos=(0,0,36.15) rot=(0,0,1;0rad)
  Radius = 14.3
FEATURE [Part::Cylinder] Cylinder031
  Angle = 360
  AttacherType = Attacher::AttachEngine3D
  Height = 10
  Placement = pos=(0,0,36.15) rot=(0,0,1;0rad)
  Radius = 4
FEATURE [Part::Box] Box021  label="removeToCreteHoleForPlugHousing019"
  AttacherType = Attacher::AttachEngine3D
  Height = 28.6
  Length = 20
  Placement = pos=(106.15,0,21.7) rot=(0,0,1;0rad)
  Width = 19
FEATURE [Part::MultiFuse] Fusion074  label="removeToCreteHoleForPlugHousing020"
  Placement = pos=(70,19,36) rot=(0,1,0;1.5708rad)
  Shapes = -> [Cylinder030,Cylinder031]
FEATURE [Part::MultiFuse] Fusion073  label="removeToCreteHoleForPlugHousing018"
  Placement = pos=(0,0,28.3) rot=(0,0,1;0rad)
  Shapes = -> [Box021,Fusion074]
FEATURE [Part::Cylinder] Cylinder032
  Angle = 360
  AttacherType = Attacher::AttachEngine3D
  Height = 20
  Placement = pos=(0,0,36.15) rot=(0,0,1;0rad)
  Radius = 14.3
FEATURE [Part::Cylinder] Cylinder033
  Angle = 360
  AttacherType = Attacher::AttachEngine3D
  Height = 10
  Placement = pos=(0,0,36.15) rot=(0,0,1;0rad)
  Radius = 4
FEATURE [Part::Box] Box022  label="removeToCreteHoleForPlugHousing021"
  AttacherType = Attacher::AttachEngine3D
  Height = 28.6
  Length = 20
  Placement = pos=(106.15,0,21.7) rot=(0,0,1;0rad)
  Width = 19
FEATURE [Part::MultiFuse] Fusion076  label="removeToCreteHoleForPlugHousing023"
  Placement = pos=(70,19,36) rot=(0,1,0;1.5708rad)
  Shapes = -> [Cylinder032,Cylinder033]
FEATURE [Part::MultiFuse] Fusion075  label="removeToCreteHoleForPlugHousing022"
  Placement = pos=(0,0,-28.3) rot=(0,0,1;0rad)
  Shapes = -> [Box022,Fusion076]
FEATURE [Part::MultiFuse] Fusion077  label="removeToCreatePlugHousingBottomBit"
  Shapes = -> [Fusion075,Fusion073]
FEATURE [Part::Cylinder] Cylinder034
  Angle = 360
  AttacherType = Attacher::AttachEngine3D
  Height = 20
  Placement = pos=(0,0,36.15) rot=(0,0,1;0rad)
  Radius = 14
FEATURE [Part::Cylinder] Cylinder035
  Angle = 360
  AttacherType = Attacher::AttachEngine3D
  Height = 10
  Placement = pos=(0,0,36.15) rot=(0,0,1;0rad)
  Radius = 4
FEATURE [Part::MultiFuse] Fusion078  label="removeToCreteHoleForPlugHousing024"
  Placement = pos=(70,19,36) rot=(0,1,0;1.5708rad)
  Shapes = -> [Cylinder034,Cylinder035]
FEATURE [Part::MultiFuse] Fusion079  label="removeToCreatePlugHousingBottomBit001"
  Shapes = -> [Fusion078,Fusion077]
FEATURE [Part::Extrusion] Extrude040  label="bottomPlugHousingBit"
  Base = -> Sketch049
  Dir = (0,0,1)
  DirMode = 2
  FaceMakerClass = Part::FaceMakerBullseye
  LengthFwd = 72
  LengthRev = 0
  Solid = true
  Symmetric = false
FEATURE [Part::Cut] Cut034  label="bottomPlugHousingBit001"
  Base = -> Extrude040
  Placement = pos=(-0.09,0,0) rot=(0,0,1;0rad)
  Tool = -> Fusion079
FEATURE [Part::Box] Box023  label="Cube014"
  AttacherType = Attacher::AttachEngine3D
  Height = 16
  Length = 8
  Placement = pos=(12.7,31.52,28) rot=(0,0,1;0rad)
  Width = 4
FEATURE [Part::Cylinder] Cylinder036
  Angle = 360
  AttacherType = Attacher::AttachEngine3D
  Height = 10
  Placement = pos=(0,0,36.15) rot=(0,0,1;0rad)
  Radius = 4
FEATURE [Part::Cylinder] Cylinder037
  Angle = 360
  AttacherType = Attacher::AttachEngine3D
  Height = 20
  Placement = pos=(0,0,36.15) rot=(0,0,1;0rad)
  Radius = 8.2
FEATURE [Part::MultiFuse] Fusion080  label="removeToCreteHoleForPlugHousing025"
  Placement = pos=(-42,19,36) rot=(0,1,0;1.5708rad)
  Shapes = -> [Cylinder037,Cylinder036]
FEATURE [Sketcher::SketchObject] Sketch050  label="topSketch012"
  FullyConstrained = true
  sketch-geometry (4):
    g0: LineSegment StartX=16.8446 StartY=31.512 StartZ=0 EndX=16.3251 EndY=34.4666 EndZ=0
    g1: ArcOfCircle CenterX=19 CenterY=19.2524 CenterZ=0 NormalX=0 NormalY=0 NormalZ=1 AngleXU=0 Radius=15.4476 StartAngle=1.74483 EndAngle=2.72717
    g2: ArcOfCircle CenterX=19 CenterY=19.2524 CenterZ=0 NormalX=0 NormalY=0 NormalZ=1 AngleXU=0 Radius=12.4476 StartAngle=1.74483 EndAngle=2.73189
    g3: LineSegment StartX=4.86004 StartY=25.4725 StartZ=0 EndX=7.58253 EndY=24.2107 EndZ=0
  constraints (7):
    c: Block(g0)
    c: Coincident(g1,g0)
    c: Coincident(g2,g0)
    c: Coincident(g3,g1)
    c: Coincident(g3,g2)
    c: Block(g1)
    c: Block(g2)
FEATURE [Part::Extrusion] Extrude041
  Base = -> Sketch050
  Dir = (0,0,1)
  DirMode = 2
  FaceMakerClass = Part::FaceMakerBullseye
  LengthFwd = 10.6
  LengthRev = 0
  Placement = pos=(0,0,31) rot=(0,0,1;0rad)
  Solid = true
  Symmetric = false
FEATURE [Part::Cut] Cut035
  Base = -> Extrude041
  Placement = pos=(0,0,-0.3) rot=(0,0,1;0rad)
  Tool = -> Fusion080
FEATURE [Part::Cut] Cut036
  Base = -> Box023
  Tool = -> Cut035
FEATURE [Part::Fillet] Fillet027
  Base = -> Cut036
  Edges = 1 edges r=0.7: [Edge13]
FEATURE [Part::Fillet] Fillet028
  Base = -> Fillet027
  Edges = 1 edges r=0.7: [Edge13]
FEATURE [Part::Fillet] Fillet029
  Base = -> Fillet028
  Edges = 1 edges r=0.7: [Edge16]
FEATURE [Part::Fillet] Fillet030
  Base = -> Fillet029
  Edges = 1 edges r=0.7: [Edge11]
FEATURE [Part::Fillet] Fillet031
  Base = -> Fillet030
  Edges = 1 edges r=0.7: [Edge10]
FEATURE [Part::Fillet] Fillet032
  Base = -> Fillet031
  Edges = 1 edges r=1.2: [Edge5]
FEATURE [Part::Fillet] Fillet033
  Base = -> Fillet032
  Edges = 1 edges r=1.2: [Edge12]
FEATURE [Part::Fillet] Fillet034  label="wireHousingRetainer"
  Base = -> Fillet033
  Edges = 1 edges r=2: [Edge1]
  Placement = pos=(0.3,0,0) rot=(0,0,1;0rad)
FEATURE [Part::Feature] Face099
  shape: bbox 3.5 x 17.8 x 2e-07 mm, 1 faces, 0 solids (baked)
FEATURE [Part::Revolution] Revolve107  label="removeToCreateScrewAndThreadedInsertHole034"
  Angle = 360
  Axis = (0,1,0)
  Base = (0,0,0)
  FaceMakerClass = Part::FaceMakerBullseye
  Placement = pos=(12.5,0,10) rot=(0,0,1;0rad)
  Solid = false
  Source = -> Face099
  Symmetric = false
FEATURE [Part::Feature] Face100
  shape: bbox 3.5 x 17.8 x 2e-07 mm, 1 faces, 0 solids (baked)
FEATURE [Part::Revolution] Revolve108  label="removeToCreateScrewAndThreadedInsertHole035"
  Angle = 360
  Axis = (0,1,0)
  Base = (0,0,0)
  FaceMakerClass = Part::FaceMakerBullseye
  Placement = pos=(12.5,0,62) rot=(0,0,1;0rad)
  Solid = false
  Source = -> Face100
  Symmetric = false
FEATURE [Part::Feature] Face101
  shape: bbox 3.5 x 17.8 x 2e-07 mm, 1 faces, 0 solids (baked)
FEATURE [Part::Revolution] Revolve109  label="removeToCreateScrewAndThreadedInsertHole036"
  Angle = 360
  Axis = (0,1,0)
  Base = (0,0,0)
  FaceMakerClass = Part::FaceMakerBullseye
  Placement = pos=(89.5,0,68.5) rot=(0,0,1;0rad)
  Solid = false
  Source = -> Face101
  Symmetric = false
FEATURE [Part::Feature] Face102
  shape: bbox 3.5 x 17.8 x 2e-07 mm, 1 faces, 0 solids (baked)
FEATURE [Part::Revolution] Revolve110  label="removeToCreateScrewAndThreadedInsertHole037"
  Angle = 360
  Axis = (0,1,0)
  Base = (0,0,0)
  FaceMakerClass = Part::FaceMakerBullseye
  Placement = pos=(89.5,0,3.5) rot=(0,0,1;0rad)
  Solid = false
  Source = -> Face102
  Symmetric = false
FEATURE [Part::Feature] Face103
  shape: bbox 3.5 x 17.8 x 2e-07 mm, 1 faces, 0 solids (baked)
FEATURE [Part::Revolution] Revolve111  label="removeToCreateScrewAndThreadedInsertHole038"
  Angle = 360
  Axis = (0,1,0)
  Base = (0,0,0)
  FaceMakerClass = Part::FaceMakerBullseye
  Placement = pos=(109.5,4.7,3.5) rot=(0,0,1;0rad)
  Solid = false
  Source = -> Face103
  Symmetric = false
FEATURE [Part::Feature] Face104
  shape: bbox 3.5 x 17.8 x 2e-07 mm, 1 faces, 0 solids (baked)
FEATURE [Part::Revolution] Revolve112  label="removeToCreateScrewAndThreadedInsertHole039"
  Angle = 360
  Axis = (0,1,0)
  Base = (0,0,0)
  FaceMakerClass = Part::FaceMakerBullseye
  Placement = pos=(109.5,4.7,68.5) rot=(0,0,1;0rad)
  Solid = false
  Source = -> Face104
  Symmetric = false
FEATURE [Part::MultiFuse] Fusion081  label="removeToCreateScrewAndThreadedInsertHole040"
  Shapes = -> [Revolve107,Revolve108,Revolve109,Revolve110,Revolve111,Revolve112]
FEATURE [Part::MultiFuse] Fusion082  label="casePillars002"
  Shapes = -> [Revolve094,Revolve092,Revolve090,Revolve089,Revolve091,Revolve093]
FEATURE [Part::Cut] Cut037  label="casePillars003"
  Base = -> Fusion082
  Tool = -> Fusion081
FEATURE [Sketcher::SketchObject] Sketch051
  FullyConstrained = true
  Placement = pos=(117,19,0) rot=(0.57735,0.57735,0.57735;2.0944rad)
  sketch-geometry (48):
    g0: LineSegment StartX=-49.19 StartY=69.25 StartZ=0 EndX=-49.19 EndY=66.25 EndZ=0
    g1: LineSegment StartX=-49.19 StartY=63.5 StartZ=0 EndX=-49.19 EndY=60.5 EndZ=0
    g2: LineSegment StartX=-49.19 StartY=57.75 StartZ=0 EndX=-49.19 EndY=54.75 EndZ=0
    g3: LineSegment StartX=-49.19 StartY=52 StartZ=0 EndX=-49.19 EndY=49 EndZ=0
    g4: LineSegment StartX=-49.19 StartY=46.25 StartZ=0 EndX=-49.19 EndY=43.25 EndZ=0
    g5: LineSegment StartX=-49.19 StartY=40.5 StartZ=0 EndX=-49.19 EndY=37.5 EndZ=0
    g6: LineSegment StartX=-49.19 StartY=34.5 StartZ=0 EndX=-49.19 EndY=31.5 EndZ=0
    g7: LineSegment StartX=-49.19 StartY=28.75 StartZ=0 EndX=-49.19 EndY=25.75 EndZ=0
    g8: LineSegment StartX=-49.19 StartY=23 StartZ=0 EndX=-49.19 EndY=20 EndZ=0
    g9: LineSegment StartX=-49.19 StartY=17.25 StartZ=0 EndX=-49.19 EndY=14.25 EndZ=0
    g10: LineSegment StartX=-49.19 StartY=11.5 StartZ=0 EndX=-49.19 EndY=8.5 EndZ=0
    g11: LineSegment StartX=-49.19 StartY=5.75 StartZ=0 EndX=-49.19 EndY=2.75 EndZ=0
    g12: ArcOfCircle CenterX=-1.5 CenterY=67.75 CenterZ=0 NormalX=0 NormalY=0 NormalZ=1 AngleXU=0 Radius=1.5 StartAngle=4.71239 EndAngle=7.85398
    g13: ArcOfCircle CenterX=-1.5 CenterY=62 CenterZ=0 NormalX=0 NormalY=0 NormalZ=1 AngleXU=0 Radius=1.5 StartAngle=4.71239 EndAngle=7.85398
    g14: ArcOfCircle CenterX=-1.5 CenterY=56.25 CenterZ=0 NormalX=0 NormalY=0 NormalZ=1 AngleXU=0 Radius=1.5 StartAngle=4.71239 EndAngle=7.85398
    g15: ArcOfCircle CenterX=-11.49 CenterY=50.5 CenterZ=0 NormalX=0 NormalY=0 NormalZ=1 AngleXU=0 Radius=1.5 StartAngle=4.71239 EndAngle=7.85398
    g16: ArcOfCircle CenterX=-16.28 CenterY=44.75 CenterZ=0 NormalX=0 NormalY=0 NormalZ=1 AngleXU=0 Radius=1.5 StartAngle=4.71239 EndAngle=7.85398
    g17: ArcOfCircle CenterX=-18.2337 CenterY=39 CenterZ=0 NormalX=0 NormalY=0 NormalZ=1 AngleXU=0 Radius=1.5 StartAngle=4.71485 EndAngle=7.85398
    g18: ArcOfCircle CenterX=-16.2837 CenterY=27.25 CenterZ=0 NormalX=0 NormalY=0 NormalZ=1 AngleXU=0 Radius=1.5 StartAngle=4.71485 EndAngle=7.85398
    g19: ArcOfCircle CenterX=-18.2337 CenterY=33 CenterZ=0 NormalX=0 NormalY=0 NormalZ=1 AngleXU=0 Radius=1.5 StartAngle=4.71485 EndAngle=7.85398
    g20: ArcOfCircle CenterX=-11.49 CenterY=21.5 CenterZ=0 NormalX=0 NormalY=0 NormalZ=1 AngleXU=0 Radius=1.5 StartAngle=4.71239 EndAngle=7.85398
    g21: ArcOfCircle CenterX=-1.5 CenterY=4.25 CenterZ=0 NormalX=0 NormalY=0 NormalZ=1 AngleXU=0 Radius=1.5 StartAngle=4.71239 EndAngle=7.85398
    g22: ArcOfCircle CenterX=-1.5 CenterY=10 CenterZ=0 NormalX=0 NormalY=0 NormalZ=1 AngleXU=0 Radius=1.5 StartAngle=4.71239 EndAngle=7.85398
    g23: ArcOfCircle CenterX=-1.5 CenterY=15.75 CenterZ=0 NormalX=0 NormalY=0 NormalZ=1 AngleXU=0 Radius=1.5 StartAngle=4.71239 EndAngle=7.85398
    g24: LineSegment StartX=-49.19 StartY=69.25 StartZ=0 EndX=-1.5 EndY=69.25 EndZ=0
    g25: LineSegment StartX=-49.19 StartY=66.25 StartZ=0 EndX=-1.5 EndY=66.25 EndZ=0
    g26: LineSegment StartX=-49.19 StartY=63.5 StartZ=0 EndX=-1.5 EndY=63.5 EndZ=0
    g27: LineSegment StartX=-49.19 StartY=60.5 StartZ=0 EndX=-1.5 EndY=60.5 EndZ=0
    g28: LineSegment StartX=-49.19 StartY=57.75 StartZ=0 EndX=-1.5 EndY=57.75 EndZ=0
    g29: LineSegment StartX=-49.19 StartY=54.75 StartZ=0 EndX=-1.5 EndY=54.75 EndZ=0
    g30: LineSegment StartX=-49.19 StartY=52 StartZ=0 EndX=-11.49 EndY=52 EndZ=0
    g31: LineSegment StartX=-49.19 StartY=49 StartZ=0 EndX=-11.49 EndY=49 EndZ=0
    g32: LineSegment StartX=-49.19 StartY=46.25 StartZ=0 EndX=-16.28 EndY=46.25 EndZ=0
    g33: LineSegment StartX=-49.19 StartY=43.25 StartZ=0 EndX=-16.28 EndY=43.25 EndZ=0
    g34: LineSegment StartX=-49.19 StartY=40.5 StartZ=0 EndX=-18.2337 EndY=40.5 EndZ=0
    g35: LineSegment StartX=-49.19 StartY=37.5 StartZ=0 EndX=-18.23 EndY=37.5 EndZ=0
    g36: LineSegment StartX=-49.19 StartY=34.5 StartZ=0 EndX=-18.2337 EndY=34.5 EndZ=0
    g37: LineSegment StartX=-49.19 StartY=31.5 StartZ=0 EndX=-18.23 EndY=31.5 EndZ=0
    g38: LineSegment StartX=-49.19 StartY=28.75 StartZ=0 EndX=-16.2837 EndY=28.75 EndZ=0
    g39: LineSegment StartX=-49.19 StartY=25.75 StartZ=0 EndX=-16.28 EndY=25.75 EndZ=0
    g40: LineSegment StartX=-49.19 StartY=23 StartZ=0 EndX=-11.49 EndY=23 EndZ=0
    g41: LineSegment StartX=-49.19 StartY=20 StartZ=0 EndX=-11.49 EndY=20 EndZ=0
    g42: LineSegment StartX=-49.19 StartY=17.25 StartZ=0 EndX=-1.5 EndY=17.25 EndZ=0
    g43: LineSegment StartX=-49.19 StartY=14.25 StartZ=0 EndX=-1.5 EndY=14.25 EndZ=0
    g44: LineSegment StartX=-49.19 StartY=11.5 StartZ=0 EndX=-1.5 EndY=11.5 EndZ=0
    g45: LineSegment StartX=-49.19 StartY=8.5 StartZ=0 EndX=-1.5 EndY=8.5 EndZ=0
    g46: LineSegment StartX=-49.19 StartY=5.75 StartZ=0 EndX=-1.5 EndY=5.75 EndZ=0
    g47: LineSegment StartX=-49.19 StartY=2.75 StartZ=0 EndX=-1.5 EndY=2.75 EndZ=0
  constraints (120):
    c: Vertical(g0)
    c: Distance(g0) = 3
    c: Block(g0)
    c: Vertical(g1)
    c: Distance(g1) = 3
    c: Vertical(g2)
    c: Equal(g0,g2) = 3
    c: Block(g2)
    c: Vertical(g3)
    c: Equal(g1,g3) = 3
    c: Vertical(g4)
    c: Equal(g0,g4) = 3
    c: Block(g4)
    c: Vertical(g5)
    c: Equal(g1,g5) = 3
    c: Vertical(g6)
    c: Equal(g0,g6) = 3
    c: Block(g6)
    c: Vertical(g7)
    c: Equal(g1,g7) = 3
    c: Vertical(g8)
    c: Equal(g0,g8) = 3
    c: Block(g8)
    c: Vertical(g9)
    c: Equal(g1,g9) = 3
    c: Vertical(g10)
    c: Equal(g0,g10) = 3
    c: Block(g10)
    c: Vertical(g11)
    c: Equal(g1,g11) = 3
    c: Block(g12)
    c: Block(g13)
    c: Block(g14)
    c: Block(g15)
    c: Block(g16)
    c: Block(g17)
    c: Block(g18)
    c: Block(g19)
    c: Block(g20)
    c: Block(g21)
    c: Block(g22)
    c: Block(g23)
    c: Block(g11)
    c: Block(g9)
    c: Block(g7)
    c: Block(g5)
    c: Block(g3)
    c: Block(g1)
    c: Coincident(g24,g0)
    c: Coincident(g24,g12)
    c: Horizontal(g24)
    c: Coincident(g25,g0)
    c: Coincident(g25,g12)
    c: Horizontal(g25)
    c: Coincident(g26,g1)
    c: Coincident(g26,g13)
    c: Horizontal(g26)
    c: Coincident(g27,g1)
    c: Coincident(g27,g13)
    c: Horizontal(g27)
    c: Coincident(g28,g2)
    c: Coincident(g28,g14)
    c: Horizontal(g28)
    c: Coincident(g29,g2)
    c: Coincident(g29,g14)
    c: Horizontal(g29)
    c: Coincident(g30,g3)
    c: Coincident(g30,g15)
    c: Horizontal(g30)
    c: Coincident(g31,g3)
    c: Coincident(g31,g15)
    c: Horizontal(g31)
    c: Coincident(g32,g4)
    c: Coincident(g32,g16)
    c: Horizontal(g32)
    c: Coincident(g33,g4)
    c: Coincident(g33,g16)
    c: Horizontal(g33)
    c: Coincident(g34,g5)
    c: Coincident(g34,g17)
    c: Horizontal(g34)
    c: Coincident(g35,g5)
    c: Coincident(g35,g17)
    c: Horizontal(g35)
    c: Coincident(g36,g6)
    c: Coincident(g36,g19)
    c: Horizontal(g36)
    c: Coincident(g37,g6)
    c: Coincident(g37,g19)
    c: Horizontal(g37)
    c: Coincident(g38,g7)
    c: Coincident(g38,g18)
    c: Horizontal(g38)
    c: Coincident(g39,g7)
    c: Coincident(g39,g18)
    c: Horizontal(g39)
    c: Coincident(g40,g8)
    c: Coincident(g40,g20)
    c: Horizontal(g40)
    c: Coincident(g41,g8)
    c: Coincident(g41,g20)
    c: Horizontal(g41)
    c: Coincident(g42,g9)
    c: Coincident(g42,g23)
    c: Horizontal(g42)
    c: Coincident(g43,g9)
    c: Coincident(g43,g23)
    c: Horizontal(g43)
    c: Coincident(g44,g10)
    c: Coincident(g44,g22)
    c: Horizontal(g44)
    c: Coincident(g45,g10)
    c: Coincident(g45,g22)
    c: Horizontal(g45)
    c: Coincident(g46,g11)
    c: Coincident(g46,g21)
    c: Horizontal(g46)
    c: Coincident(g47,g11)
    c: Coincident(g47,g21)
    c: Horizontal(g47)
FEATURE [Part::Extrusion] Extrude042
  Base = -> Sketch051
  Dir = (1,-2e-16,2e-16)
  DirMode = 2
  FaceMakerClass = Part::FaceMakerBullseye
  LengthFwd = 19
  LengthRev = 0
  Placement = pos=(-19,0,0) rot=(0,0,1;0rad)
  Solid = true
  Symmetric = false
FEATURE [Part::Fillet] Fillet035  label="removeToCreateVentalationHoles"
  Base = -> Extrude042
  Edges = <same value as first occurrence — deduplicated (x6 in doc)>
  Placement = pos=(7,0,0) rot=(0,0,1;0rad)
FEATURE [Part::Cut] Cut038  label="top017"
  Base = -> Cut033
  Tool = -> Fillet035
FEATURE [Sketcher::SketchObject] Sketch052  label="bottomSketch001"
  FullyConstrained = true
  sketch-geometry (45):
    g0: LineSegment StartX=6.29999 StartY=8 StartZ=0 EndX=3.29999 EndY=8 EndZ=0
    g1: LineSegment StartX=3.29999 StartY=8 StartZ=0 EndX=3.29999 EndY=-6.03275e-07 EndZ=0
    g2: ArcOfCircle CenterX=8.29999 CenterY=5 CenterZ=0 NormalX=0 NormalY=0 NormalZ=1 AngleXU=0 Radius=2 StartAngle=3.14159 EndAngle=4.71239
    g3: LineSegment StartX=6.29999 StartY=8 StartZ=0 EndX=6.29999 EndY=5 EndZ=0
    g4: ArcOfCircle CenterX=105 CenterY=19 CenterZ=0 NormalX=0 NormalY=0 NormalZ=1 AngleXU=0 Radius=12.7 StartAngle=4.71239 EndAngle=5.94289
    g5-g11: Circle x7 (B-spline internal-alignment scaffolding for g12; pole/knot coordinates omitted)
    g12: BSplineCurve PolesCount=7 KnotsCount=5 Degree=3 IsPeriodic=0
    g13-g17: GeomPoint x5 (B-spline internal-alignment scaffolding for g12; pole/knot coordinates omitted)
    g18: ArcOfCircle CenterX=105 CenterY=19 CenterZ=0 NormalX=0 NormalY=0 NormalZ=1 AngleXU=0 Radius=15.7 StartAngle=5.81226 EndAngle=6.28319
    g19: BSplineCurve PolesCount=5 KnotsCount=3 Degree=3 IsPeriodic=0
    g20: LineSegment StartX=8.29999 StartY=3 StartZ=0 EndX=101.7 EndY=3 EndZ=0
    g21: LineSegment StartX=3.29999 StartY=-6.03275e-07 StartZ=0 EndX=105 EndY=-6.03275e-07 EndZ=0
    g22: LineSegment StartX=120.974 StartY=8.71251 StartZ=0 EndX=122.332 EndY=7.83778 EndZ=0
    g23: LineSegment StartX=105 StartY=-6.03274e-07 StartZ=0 EndX=113 EndY=-6.03274e-07 EndZ=0
    g24: ArcOfCircle CenterX=105 CenterY=19 CenterZ=0 NormalX=0 NormalY=0 NormalZ=1 AngleXU=0 Radius=20.6155 StartAngle=5.11091 EndAngle=5.71103
    g25: ArcOfCircle CenterX=117.7 CenterY=19 CenterZ=0 NormalX=0 NormalY=0 NormalZ=1 AngleXU=0 Radius=3 StartAngle=1.2e-15 EndAngle=2.10468
    g26: Circle CenterX=116.345 CenterY=16.3232 CenterZ=0 NormalX=0 NormalY=0 NormalZ=1 AngleXU=0 Radius=1
    g27: Circle CenterX=117.24 CenterY=15.7584 CenterZ=0 NormalX=0 NormalY=0 NormalZ=1 AngleXU=0 Radius=1
    g28: Circle CenterX=116.972 CenterY=14.7612 CenterZ=0 NormalX=0 NormalY=0 NormalZ=1 AngleXU=0 Radius=1
    g29: BSplineCurve PolesCount=3 KnotsCount=2 Degree=2 IsPeriodic=0
    g30: GeomPoint X=116.345 Y=16.3232 Z=0
    g31: GeomPoint X=116.972 Y=14.7612 Z=0
    g32: Circle CenterX=115.828 CenterY=17.157 CenterZ=0 NormalX=0 NormalY=0 NormalZ=1 AngleXU=0 Radius=1
    g33: Circle CenterX=115.841 CenterY=16.639 CenterZ=0 NormalX=0 NormalY=0 NormalZ=1 AngleXU=0 Radius=1
    g34: Circle CenterX=116.345 CenterY=16.3232 CenterZ=0 NormalX=0 NormalY=0 NormalZ=1 AngleXU=0 Radius=1
    g35: BSplineCurve PolesCount=3 KnotsCount=2 Degree=2 IsPeriodic=0
    g36: GeomPoint X=115.828 Y=17.157 Z=0
    g37: GeomPoint X=116.345 Y=16.3232 Z=0
    g38: LineSegment StartX=115.828 StartY=17.157 StartZ=0 EndX=115.828 EndY=20.8307 EndZ=0
    g39: Circle CenterX=115.828 CenterY=20.8307 CenterZ=0 NormalX=0 NormalY=0 NormalZ=1 AngleXU=0 Radius=1
    g40: Circle CenterX=115.831 CenterY=21.3396 CenterZ=0 NormalX=0 NormalY=0 NormalZ=1 AngleXU=0 Radius=1
    g41: Circle CenterX=116.173 CenterY=21.5825 CenterZ=0 NormalX=0 NormalY=0 NormalZ=1 AngleXU=0 Radius=1
    g42: BSplineCurve PolesCount=3 KnotsCount=2 Degree=2 IsPeriodic=0
    g43: GeomPoint X=115.828 Y=20.8307 Z=0
    g44: GeomPoint X=116.173 Y=21.5825 Z=0
  constraints (70):
    c: Horizontal(g0)
    c: Distance(g0) = 3
    c: Coincident(g1,g0)
    c: Vertical(g1)
    c: Block(g2)
    c: Block(g0)
    c: Coincident(g3,g0)
    c: Coincident(g3,g2)
    c: Vertical(g3)
    c: Block(g1)
    c: Block(g4)
    c: Coincident(g19,g4)
    c: Block(g19)
    c: Equal(g5, g6-g11) x6
    c: InternalAlignment(g5-g11 -> g12) x7
    c: InternalAlignment(g13-g17 -> g12) x5
    c: Block(g12)
    c: Coincident(g18,g12)
    c: Block(g18)
    c: Coincident(g20,g2)
    c: Coincident(g20,g19)
    c: Horizontal(g20)
    c: Distance(g20) = 93.4
    c: Coincident(g21,g1)
    c: Horizontal(g21)
    c: Distance(g21) = 101.7
    c: Horizontal(g23)
    c: Distance(g23) = 8
    c: Coincident(g24,g23)
    c: Block(g23)
    c: Coincident(g22,g24)
    c: Block(g24)
    c: Block(g22)
    c: Distance(g22) = 1.61553
    c: Coincident(g25,g18)
    c: Block(g25)
    c: Weight(g26) = 1
    c: Equal(g26,g27)
    c: Equal(g26,g28)
    c: Coincident(g29,g4)
    c: InternalAlignment(g26,g29)
    c: InternalAlignment(g27,g29)
    c: InternalAlignment(g28,g29)
    c: InternalAlignment(g30,g29)
    c: InternalAlignment(g31,g29)
    c: Block(g29)
    c: Weight(g32) = 1
    c: Equal(g32,g33)
    c: Equal(g32,g34)
    c: Coincident(g35,g29)
    c: InternalAlignment(g32,g35)
    c: InternalAlignment(g33,g35)
    c: InternalAlignment(g34,g35)
    c: InternalAlignment(g36,g35)
    c: InternalAlignment(g37,g35)
    c: Block(g35)
    c: Coincident(g38,g35)
    c: Vertical(g38)
    c: Block(g38)
    c: Coincident(g42,g38)
    c: Weight(g39) = 1
    c: Equal(g39,g40)
    c: Equal(g39,g41)
    c: Coincident(g42,g25)
    c: InternalAlignment(g39,g42)
    c: InternalAlignment(g40,g42)
    c: InternalAlignment(g41,g42)
    c: InternalAlignment(g43,g42)
    c: InternalAlignment(g44,g42)
    c: Block(g42)
FEATURE [Part::Extrusion] Extrude043  label="bottom010"
  Base = -> Sketch052
  Dir = (0,0,1)
  DirMode = 2
  FaceMakerClass = Part::FaceMakerBullseye
  LengthFwd = 71.4
  LengthRev = 0
  Placement = pos=(0,0,0.3) rot=(0,0,1;0rad)
  Solid = true
  Symmetric = false
FEATURE [Sketcher::SketchObject] Sketch053  label="topSketch013"
  FullyConstrained = true
  sketch-geometry (22):
    g0: LineSegment StartX=5.21097e-06 StartY=3 StartZ=0 EndX=5.21097e-06 EndY=19 EndZ=0
    g1: ArcOfCircle CenterX=19 CenterY=19 CenterZ=0 NormalX=0 NormalY=0 NormalZ=1 AngleXU=0 Radius=19 StartAngle=1.5708 EndAngle=3.14159
    g2: ArcOfCircle CenterX=19 CenterY=19 CenterZ=0 NormalX=0 NormalY=0 NormalZ=1 AngleXU=0 Radius=16 StartAngle=1.5708 EndAngle=3.14159
    g3: LineSegment StartX=114 StartY=35 StartZ=0 EndX=19 EndY=35 EndZ=0
    g4: LineSegment StartX=5.21097e-06 StartY=3 StartZ=0 EndX=5.21097e-06 EndY=0 EndZ=0
    g5: LineSegment StartX=3 StartY=0 StartZ=0 EndX=5.21097e-06 EndY=0 EndZ=0
    g6: LineSegment StartX=3 StartY=19 StartZ=0 EndX=3 EndY=0 EndZ=0
    g7: LineSegment StartX=19 StartY=38 StartZ=0 EndX=124 EndY=38 EndZ=0
    g8: Circle CenterX=119 CenterY=35 CenterZ=0 NormalX=0 NormalY=0 NormalZ=1 AngleXU=0 Radius=1
    g9: Circle CenterX=121 CenterY=35 CenterZ=0 NormalX=0 NormalY=0 NormalZ=1 AngleXU=0 Radius=1
    g10: Circle CenterX=121 CenterY=33 CenterZ=0 NormalX=0 NormalY=0 NormalZ=1 AngleXU=0 Radius=1
    g11: BSplineCurve PolesCount=3 KnotsCount=2 Degree=2 IsPeriodic=0
    g12: GeomPoint X=119 Y=35 Z=0
    g13: GeomPoint X=121 Y=33 Z=0
    g14: LineSegment StartX=119 StartY=35 StartZ=0 EndX=114 EndY=35 EndZ=0
    g15: ArcOfCircle CenterX=105 CenterY=19 CenterZ=0 NormalX=0 NormalY=0 NormalZ=1 AngleXU=0 Radius=16 StartAngle=5.60905 EndAngle=6.28319
    g16: LineSegment StartX=121 StartY=33 StartZ=0 EndX=121 EndY=19 EndZ=0
    g17: LineSegment StartX=117.5 StartY=9.01251 StartZ=0 EndX=121.163 EndY=9.0125 EndZ=0
    g18: ArcOfCircle CenterX=105 CenterY=19 CenterZ=0 NormalX=0 NormalY=0 NormalZ=1 AngleXU=0 Radius=20.6155 StartAngle=5.7297 EndAngle=6.28319
    g19: LineSegment StartX=121.163 StartY=9.0125 StartZ=0 EndX=122.538 EndY=8.16329 EndZ=0
    g20: LineSegment StartX=124 StartY=38 StartZ=0 EndX=125.616 EndY=38 EndZ=0
    g21: LineSegment StartX=125.616 StartY=19 StartZ=0 EndX=125.616 EndY=38 EndZ=0
  constraints (50):
    c: Vertical(g0)
    c: Block(g0)
    c: Coincident(g1,g0)
    c: Block(g1)
    c: Coincident(g2,g1)
    c: Block(g2)
    c: Coincident(g3,g2)
    c: Horizontal(g3)
    c: Tangent(g3,g2)
    c: Coincident(g4,g0)
    c: Distance(g4) = 3
    c: Vertical(g4)
    c: Coincident(g5,g4)
    c: Horizontal(g5)
    c: Coincident(g6,g2)
    c: Coincident(g6,g5)
    c: Vertical(g6)
    c: Horizontal(g7)
    c: Distance(g7) = 105
    c: Coincident(g7,g1)
    c: Block(g3)
    c: Weight(g8) = 1
    c: Equal(g8,g9)
    c: Equal(g8,g10)
    c: InternalAlignment(g8,g11)
    c: InternalAlignment(g9,g11)
    c: InternalAlignment(g10,g11)
    c: InternalAlignment(g12,g11)
    c: InternalAlignment(g13,g11)
    c: Block(g11)
    c: Coincident(g14,g11)
    c: Coincident(g14,g3)
    c: Horizontal(g14)
    c: Block(g15)
    c: Coincident(g16,g11)
    c: Coincident(g16,g15)
    c: Vertical(g16)
    c: Distance(g16) = 14
    c: Coincident(g17,g15)
    c: Block(g18)
    c: Coincident(g19,g18)
    c: Coincident(g20,g7)
    c: Horizontal(g20)
    c: Vertical(g21)
    c: Coincident(g20,g21)
    c: Block(g20)
    c: Block(g21)
    c: Block(g19)
    c: Block(g17)
    c: Distance(g20) = 1.61553
FEATURE [Part::Extrusion] Extrude044
  Base = -> Sketch053
  Dir = (0,0,1)
  DirMode = 2
  FaceMakerClass = Part::FaceMakerBullseye
  LengthFwd = 72
  LengthRev = 0
  Solid = true
  Symmetric = false
FEATURE [Part::Fillet] Fillet036  label="top018"
  Base = -> Extrude044
  Edges = 1 edges r=2: [Edge41]
FEATURE [Sketcher::SketchObject] Sketch054
  FullyConstrained = false
  Placement = pos=(0,0,0) rot=(1,0,0;1.5708rad)
  sketch-geometry (24):
    g0: ArcOfCircle CenterX=-4 CenterY=-10.5 CenterZ=0 NormalX=0 NormalY=0 NormalZ=1 AngleXU=0 Radius=1.5 StartAngle=6e-16 EndAngle=3.14159
    g1: ArcOfCircle CenterX=-34.2 CenterY=-10.5 CenterZ=0 NormalX=0 NormalY=0 NormalZ=1 AngleXU=0 Radius=1.5 StartAngle=0 EndAngle=3.14159
    g2: ArcOfCircle CenterX=-34.2 CenterY=-27.7 CenterZ=0 NormalX=0 NormalY=0 NormalZ=1 AngleXU=0 Radius=1.5 StartAngle=3.14159 EndAngle=6.28319
    g3: ArcOfCircle CenterX=-4 CenterY=-27.7 CenterZ=0 NormalX=0 NormalY=0 NormalZ=1 AngleXU=0 Radius=1.5 StartAngle=3.1416 EndAngle=6.28319
    g4: ArcOfCircle CenterX=-10 CenterY=-4.3 CenterZ=0 NormalX=0 NormalY=0 NormalZ=1 AngleXU=0 Radius=1.5 StartAngle=2e-16 EndAngle=3.14159
    g5: ArcOfCircle CenterX=-16.1 CenterY=-1.8 CenterZ=0 NormalX=0 NormalY=0 NormalZ=1 AngleXU=0 Radius=1.5 StartAngle=5e-16 EndAngle=3.14159
    g6: ArcOfCircle CenterX=-22.1 CenterY=-1.8 CenterZ=0 NormalX=0 NormalY=0 NormalZ=1 AngleXU=0 Radius=1.5 StartAngle=5e-16 EndAngle=3.14159
    g7: ArcOfCircle CenterX=-28.2 CenterY=-4.3 CenterZ=0 NormalX=0 NormalY=0 NormalZ=1 AngleXU=0 Radius=1.5 StartAngle=2e-16 EndAngle=3.14159
    g8: ArcOfCircle CenterX=-10 CenterY=-33.9 CenterZ=0 NormalX=0 NormalY=0 NormalZ=1 AngleXU=0 Radius=1.5 StartAngle=3.14159 EndAngle=6.28319
    g9: ArcOfCircle CenterX=-16.1 CenterY=-36.4 CenterZ=0 NormalX=0 NormalY=0 NormalZ=1 AngleXU=0 Radius=1.5 StartAngle=3.14159 EndAngle=6.28319
    g10: ArcOfCircle CenterX=-22.1 CenterY=-36.4 CenterZ=0 NormalX=0 NormalY=0 NormalZ=1 AngleXU=0 Radius=1.5 StartAngle=3.14159 EndAngle=6.28319
    g11: ArcOfCircle CenterX=-28.2 CenterY=-33.9 CenterZ=0 NormalX=0 NormalY=0 NormalZ=1 AngleXU=0 Radius=1.5 StartAngle=3.14159 EndAngle=6.28319
    g12: LineSegment StartX=-35.7 StartY=-10.5 StartZ=0 EndX=-35.7 EndY=-27.7 EndZ=0
    g13: LineSegment StartX=-32.7 StartY=-10.5 StartZ=0 EndX=-32.7 EndY=-27.7 EndZ=0
    g14: LineSegment StartX=-29.7 StartY=-33.9 StartZ=0 EndX=-29.7 EndY=-4.3 EndZ=0
    g15: LineSegment StartX=-26.7 StartY=-33.9 StartZ=0 EndX=-26.7 EndY=-4.3 EndZ=0
    g16: LineSegment StartX=-2.5 StartY=-10.5 StartZ=0 EndX=-2.5 EndY=-27.7 EndZ=0
    g17: LineSegment StartX=-8.5 StartY=-4.3 StartZ=0 EndX=-8.5 EndY=-33.9 EndZ=0
    g18: LineSegment StartX=-5.5 StartY=-10.5 StartZ=0 EndX=-5.5 EndY=-27.7 EndZ=0
    g19: LineSegment StartX=-11.5 StartY=-4.3 StartZ=0 EndX=-11.5 EndY=-33.9 EndZ=0
    g20: LineSegment StartX=-14.6 StartY=-1.8 StartZ=0 EndX=-14.6 EndY=-36.4 EndZ=0
    g21: LineSegment StartX=-17.6 StartY=-1.8 StartZ=0 EndX=-17.6 EndY=-36.4 EndZ=0
    g22: LineSegment StartX=-20.6 StartY=-36.4 StartZ=0 EndX=-20.6 EndY=-1.8 EndZ=0
    g23: LineSegment StartX=-23.6 StartY=-1.8 StartZ=0 EndX=-23.6 EndY=-36.4 EndZ=0
  constraints (48):
    c: Block(g0)
    c: Block(g1)
    c: Block(g2)
    c: Block(g3)
    c: Block(g4)
    c: Block(g5)
    c: Block(g6)
    c: Block(g7)
    c: Block(g8)
    c: Block(g9)
    c: Block(g10)
    c: Block(g11)
    c: Coincident(g12,g1)
    c: Coincident(g12,g2)
    c: Vertical(g12)
    c: Coincident(g13,g1)
    c: Coincident(g13,g2)
    c: Vertical(g13)
    c: Coincident(g14,g11)
    c: Coincident(g14,g7)
    c: Vertical(g14)
    c: Coincident(g15,g11)
    c: Coincident(g15,g7)
    c: Vertical(g15)
    c: Coincident(g16,g0)
    c: Coincident(g16,g3)
    c: Vertical(g16)
    c: Coincident(g17,g4)
    c: Coincident(g17,g8)
    c: Vertical(g17)
    c: Coincident(g18,g0)
    c: Coincident(g18,g3)
    c: Vertical(g18)
    c: Coincident(g19,g4)
    c: Coincident(g19,g8)
    c: Vertical(g19)
    c: Coincident(g20,g5)
    c: Coincident(g20,g9)
    c: Vertical(g20)
    c: Coincident(g21,g5)
    c: Coincident(g21,g9)
    c: Vertical(g21)
    c: Coincident(g22,g10)
    c: Coincident(g22,g6)
    c: Vertical(g22)
    c: Coincident(g23,g6)
    c: Coincident(g23,g10)
    c: Vertical(g23)
FEATURE [Part::Extrusion] Extrude045  label="removeToCreateFanGrillHoles003"
  Base = -> Sketch054
  Dir = (0,-1,6e-16)
  DirMode = 2
  FaceMakerClass = Part::FaceMakerBullseye
  LengthFwd = 10
  LengthRev = 0
  Placement = pos=(65.4,44,54.82) rot=(0,0,1;0rad)
  Solid = true
  Symmetric = false
FEATURE [Part::Feature] Face105 .. Face108  x4 (patterned run collapsed; names and placements below)
  shape: bbox 3.5 x 17.8 x 2e-07 mm, 1 faces, 0 solids (baked)
FEATURE [Part::Revolution] Revolve113  label="removeToCreateScrewAndThreadedInsertHole041"
  Angle = 360
  Axis = (0,1,0)
  Base = (0,0,0)
  FaceMakerClass = Part::FaceMakerBullseye
  Placement = pos=(62.3,30.3,19.7) rot=(0,0,1;0rad)
  Solid = false
  Source = -> Face105
  Symmetric = false
FEATURE [Part::Revolution] Revolve114  label="removeToCreateScrewAndThreadedInsertHole042"
  Angle = 360
  Axis = (0,1,0)
  Base = (0,0,0)
  FaceMakerClass = Part::FaceMakerBullseye
  Placement = pos=(62.3,30.3,51.7) rot=(0,0,1;0rad)
  Solid = false
  Source = -> Face106
  Symmetric = false
FEATURE [Part::Revolution] Revolve115  label="removeToCreateScrewAndThreadedInsertHole043"
  Angle = 360
  Axis = (0,1,0)
  Base = (0,0,0)
  FaceMakerClass = Part::FaceMakerBullseye
  Placement = pos=(30.3,30.3,19.7) rot=(0,0,1;0rad)
  Solid = false
  Source = -> Face107
  Symmetric = false
FEATURE [Part::Revolution] Revolve116  label="removeToCreateScrewAndThreadedInsertHole044"
  Angle = 360
  Axis = (0,1,0)
  Base = (0,0,0)
  FaceMakerClass = Part::FaceMakerBullseye
  Placement = pos=(30.3,30.3,51.7) rot=(0,0,1;0rad)
  Solid = false
  Source = -> Face108
  Symmetric = false
FEATURE [Part::MultiFuse] Fusion083  label="createThreadedInsertHolesForFan004"
  Shapes = -> [Revolve113,Revolve114,Revolve115,Revolve116]
FEATURE [Part::Box] Box024  label="removeToCreteHoleForPlugHousing026"
  AttacherType = Attacher::AttachEngine3D
  Height = 28.6
  Length = 10
  Placement = pos=(-2,0,21.7) rot=(0,0,1;0rad)
  Width = 19
FEATURE [Part::Cylinder] Cylinder038  label="removeToCreteHoleForPlugHousing027"
  Angle = 360
  AttacherType = Attacher::AttachEngine3D
  Height = 20
  Placement = pos=(-2,19,36) rot=(0,1,0;1.5708rad)
  Radius = 14.3
FEATURE [Part::MultiFuse] Fusion084  label="removeToCreteHoleForPlugHousing028"
  Shapes = -> [Box024,Cylinder038]
FEATURE [Part::Cylinder] Cylinder039
  Angle = 360
  AttacherType = Attacher::AttachEngine3D
  Height = 20
  Placement = pos=(0,0,36.15) rot=(0,0,1;0rad)
  Radius = 14.3
FEATURE [Part::Cylinder] Cylinder040
  Angle = 360
  AttacherType = Attacher::AttachEngine3D
  Height = 10
  Placement = pos=(0,0,36.15) rot=(0,0,1;0rad)
  Radius = 4
FEATURE [Part::Box] Box025  label="removeToCreteHoleForPlugHousing030"
  AttacherType = Attacher::AttachEngine3D
  Height = 28.6
  Length = 20
  Placement = pos=(106.15,0,21.7) rot=(0,0,1;0rad)
  Width = 19
FEATURE [Part::MultiFuse] Fusion086  label="removeToCreteHoleForPlugHousing031"
  Placement = pos=(70,19,36) rot=(0,1,0;1.5708rad)
  Shapes = -> [Cylinder039,Cylinder040]
FEATURE [Part::MultiFuse] Fusion085  label="removeToCreteHoleForPlugHousing029"
  Shapes = -> [Box025,Fusion086]
FEATURE [Sketcher::SketchObject] Sketch055
  FullyConstrained = true
  Placement = pos=(117,19,0) rot=(0.57735,0.57735,0.57735;2.0944rad)
  sketch-geometry (48):
    g0: LineSegment StartX=-49.19 StartY=69.25 StartZ=0 EndX=-49.19 EndY=66.25 EndZ=0
    g1: LineSegment StartX=-49.19 StartY=63.5 StartZ=0 EndX=-49.19 EndY=60.5 EndZ=0
    g2: LineSegment StartX=-49.19 StartY=57.75 StartZ=0 EndX=-49.19 EndY=54.75 EndZ=0
    g3: LineSegment StartX=-49.19 StartY=52 StartZ=0 EndX=-49.19 EndY=49 EndZ=0
    g4: LineSegment StartX=-49.19 StartY=46.25 StartZ=0 EndX=-49.19 EndY=43.25 EndZ=0
    g5: LineSegment StartX=-49.19 StartY=40.5 StartZ=0 EndX=-49.19 EndY=37.5 EndZ=0
    g6: LineSegment StartX=-49.19 StartY=34.5 StartZ=0 EndX=-49.19 EndY=31.5 EndZ=0
    g7: LineSegment StartX=-49.19 StartY=28.75 StartZ=0 EndX=-49.19 EndY=25.75 EndZ=0
    g8: LineSegment StartX=-49.19 StartY=23 StartZ=0 EndX=-49.19 EndY=20 EndZ=0
    g9: LineSegment StartX=-49.19 StartY=17.25 StartZ=0 EndX=-49.19 EndY=14.25 EndZ=0
    g10: LineSegment StartX=-49.19 StartY=11.5 StartZ=0 EndX=-49.19 EndY=8.5 EndZ=0
    g11: LineSegment StartX=-49.19 StartY=5.75 StartZ=0 EndX=-49.19 EndY=2.75 EndZ=0
    g12: ArcOfCircle CenterX=-1.5 CenterY=67.75 CenterZ=0 NormalX=0 NormalY=0 NormalZ=1 AngleXU=0 Radius=1.5 StartAngle=4.71239 EndAngle=7.85398
    g13: ArcOfCircle CenterX=-1.5 CenterY=62 CenterZ=0 NormalX=0 NormalY=0 NormalZ=1 AngleXU=0 Radius=1.5 StartAngle=4.71239 EndAngle=7.85398
    g14: ArcOfCircle CenterX=-1.5 CenterY=56.25 CenterZ=0 NormalX=0 NormalY=0 NormalZ=1 AngleXU=0 Radius=1.5 StartAngle=4.71239 EndAngle=7.85398
    g15: ArcOfCircle CenterX=-11.49 CenterY=50.5 CenterZ=0 NormalX=0 NormalY=0 NormalZ=1 AngleXU=0 Radius=1.5 StartAngle=4.71239 EndAngle=7.85398
    g16: ArcOfCircle CenterX=-16.28 CenterY=44.75 CenterZ=0 NormalX=0 NormalY=0 NormalZ=1 AngleXU=0 Radius=1.5 StartAngle=4.71239 EndAngle=7.85398
    g17: ArcOfCircle CenterX=-18.2337 CenterY=39 CenterZ=0 NormalX=0 NormalY=0 NormalZ=1 AngleXU=0 Radius=1.5 StartAngle=4.71485 EndAngle=7.85398
    g18: ArcOfCircle CenterX=-16.2837 CenterY=27.25 CenterZ=0 NormalX=0 NormalY=0 NormalZ=1 AngleXU=0 Radius=1.5 StartAngle=4.71485 EndAngle=7.85398
    g19: ArcOfCircle CenterX=-18.2337 CenterY=33 CenterZ=0 NormalX=0 NormalY=0 NormalZ=1 AngleXU=0 Radius=1.5 StartAngle=4.71485 EndAngle=7.85398
    g20: ArcOfCircle CenterX=-11.49 CenterY=21.5 CenterZ=0 NormalX=0 NormalY=0 NormalZ=1 AngleXU=0 Radius=1.5 StartAngle=4.71239 EndAngle=7.85398
    g21: ArcOfCircle CenterX=-1.5 CenterY=4.25 CenterZ=0 NormalX=0 NormalY=0 NormalZ=1 AngleXU=0 Radius=1.5 StartAngle=4.71239 EndAngle=7.85398
    g22: ArcOfCircle CenterX=-1.5 CenterY=10 CenterZ=0 NormalX=0 NormalY=0 NormalZ=1 AngleXU=0 Radius=1.5 StartAngle=4.71239 EndAngle=7.85398
    g23: ArcOfCircle CenterX=-1.5 CenterY=15.75 CenterZ=0 NormalX=0 NormalY=0 NormalZ=1 AngleXU=0 Radius=1.5 StartAngle=4.71239 EndAngle=7.85398
    g24: LineSegment StartX=-49.19 StartY=69.25 StartZ=0 EndX=-1.5 EndY=69.25 EndZ=0
    g25: LineSegment StartX=-49.19 StartY=66.25 StartZ=0 EndX=-1.5 EndY=66.25 EndZ=0
    g26: LineSegment StartX=-49.19 StartY=63.5 StartZ=0 EndX=-1.5 EndY=63.5 EndZ=0
    g27: LineSegment StartX=-49.19 StartY=60.5 StartZ=0 EndX=-1.5 EndY=60.5 EndZ=0
    g28: LineSegment StartX=-49.19 StartY=57.75 StartZ=0 EndX=-1.5 EndY=57.75 EndZ=0
    g29: LineSegment StartX=-49.19 StartY=54.75 StartZ=0 EndX=-1.5 EndY=54.75 EndZ=0
    g30: LineSegment StartX=-49.19 StartY=52 StartZ=0 EndX=-11.49 EndY=52 EndZ=0
    g31: LineSegment StartX=-49.19 StartY=49 StartZ=0 EndX=-11.49 EndY=49 EndZ=0
    g32: LineSegment StartX=-49.19 StartY=46.25 StartZ=0 EndX=-16.28 EndY=46.25 EndZ=0
    g33: LineSegment StartX=-49.19 StartY=43.25 StartZ=0 EndX=-16.28 EndY=43.25 EndZ=0
    g34: LineSegment StartX=-49.19 StartY=40.5 StartZ=0 EndX=-18.2337 EndY=40.5 EndZ=0
    g35: LineSegment StartX=-49.19 StartY=37.5 StartZ=0 EndX=-18.23 EndY=37.5 EndZ=0
    g36: LineSegment StartX=-49.19 StartY=34.5 StartZ=0 EndX=-18.2337 EndY=34.5 EndZ=0
    g37: LineSegment StartX=-49.19 StartY=31.5 StartZ=0 EndX=-18.23 EndY=31.5 EndZ=0
    g38: LineSegment StartX=-49.19 StartY=28.75 StartZ=0 EndX=-16.2837 EndY=28.75 EndZ=0
    g39: LineSegment StartX=-49.19 StartY=25.75 StartZ=0 EndX=-16.28 EndY=25.75 EndZ=0
    g40: LineSegment StartX=-49.19 StartY=23 StartZ=0 EndX=-11.49 EndY=23 EndZ=0
    g41: LineSegment StartX=-49.19 StartY=20 StartZ=0 EndX=-11.49 EndY=20 EndZ=0
    g42: LineSegment StartX=-49.19 StartY=17.25 StartZ=0 EndX=-1.5 EndY=17.25 EndZ=0
    g43: LineSegment StartX=-49.19 StartY=14.25 StartZ=0 EndX=-1.5 EndY=14.25 EndZ=0
    g44: LineSegment StartX=-49.19 StartY=11.5 StartZ=0 EndX=-1.5 EndY=11.5 EndZ=0
    g45: LineSegment StartX=-49.19 StartY=8.5 StartZ=0 EndX=-1.5 EndY=8.5 EndZ=0
    g46: LineSegment StartX=-49.19 StartY=5.75 StartZ=0 EndX=-1.5 EndY=5.75 EndZ=0
    g47: LineSegment StartX=-49.19 StartY=2.75 StartZ=0 EndX=-1.5 EndY=2.75 EndZ=0
  constraints (120):
    c: Vertical(g0)
    c: Distance(g0) = 3
    c: Block(g0)
    c: Vertical(g1)
    c: Distance(g1) = 3
    c: Vertical(g2)
    c: Equal(g0,g2) = 3
    c: Block(g2)
    c: Vertical(g3)
    c: Equal(g1,g3) = 3
    c: Vertical(g4)
    c: Equal(g0,g4) = 3
    c: Block(g4)
    c: Vertical(g5)
    c: Equal(g1,g5) = 3
    c: Vertical(g6)
    c: Equal(g0,g6) = 3
    c: Block(g6)
    c: Vertical(g7)
    c: Equal(g1,g7) = 3
    c: Vertical(g8)
    c: Equal(g0,g8) = 3
    c: Block(g8)
    c: Vertical(g9)
    c: Equal(g1,g9) = 3
    c: Vertical(g10)
    c: Equal(g0,g10) = 3
    c: Block(g10)
    c: Vertical(g11)
    c: Equal(g1,g11) = 3
    c: Block(g12)
    c: Block(g13)
    c: Block(g14)
    c: Block(g15)
    c: Block(g16)
    c: Block(g17)
    c: Block(g18)
    c: Block(g19)
    c: Block(g20)
    c: Block(g21)
    c: Block(g22)
    c: Block(g23)
    c: Block(g11)
    c: Block(g9)
    c: Block(g7)
    c: Block(g5)
    c: Block(g3)
    c: Block(g1)
    c: Coincident(g24,g0)
    c: Coincident(g24,g12)
    c: Horizontal(g24)
    c: Coincident(g25,g0)
    c: Coincident(g25,g12)
    c: Horizontal(g25)
    c: Coincident(g26,g1)
    c: Coincident(g26,g13)
    c: Horizontal(g26)
    c: Coincident(g27,g1)
    c: Coincident(g27,g13)
    c: Horizontal(g27)
    c: Coincident(g28,g2)
    c: Coincident(g28,g14)
    c: Horizontal(g28)
    c: Coincident(g29,g2)
    c: Coincident(g29,g14)
    c: Horizontal(g29)
    c: Coincident(g30,g3)
    c: Coincident(g30,g15)
    c: Horizontal(g30)
    c: Coincident(g31,g3)
    c: Coincident(g31,g15)
    c: Horizontal(g31)
    c: Coincident(g32,g4)
    c: Coincident(g32,g16)
    c: Horizontal(g32)
    c: Coincident(g33,g4)
    c: Coincident(g33,g16)
    c: Horizontal(g33)
    c: Coincident(g34,g5)
    c: Coincident(g34,g17)
    c: Horizontal(g34)
    c: Coincident(g35,g5)
    c: Coincident(g35,g17)
    c: Horizontal(g35)
    c: Coincident(g36,g6)
    c: Coincident(g36,g19)
    c: Horizontal(g36)
    c: Coincident(g37,g6)
    c: Coincident(g37,g19)
    c: Horizontal(g37)
    c: Coincident(g38,g7)
    c: Coincident(g38,g18)
    c: Horizontal(g38)
    c: Coincident(g39,g7)
    c: Coincident(g39,g18)
    c: Horizontal(g39)
    c: Coincident(g40,g8)
    c: Coincident(g40,g20)
    c: Horizontal(g40)
    c: Coincident(g41,g8)
    c: Coincident(g41,g20)
    c: Horizontal(g41)
    c: Coincident(g42,g9)
    c: Coincident(g42,g23)
    c: Horizontal(g42)
    c: Coincident(g43,g9)
    c: Coincident(g43,g23)
    c: Horizontal(g43)
    c: Coincident(g44,g10)
    c: Coincident(g44,g22)
    c: Horizontal(g44)
    c: Coincident(g45,g10)
    c: Coincident(g45,g22)
    c: Horizontal(g45)
    c: Coincident(g46,g11)
    c: Coincident(g46,g21)
    c: Horizontal(g46)
    c: Coincident(g47,g11)
    c: Coincident(g47,g21)
    c: Horizontal(g47)
FEATURE [Part::Extrusion] Extrude046
  Base = -> Sketch055
  Dir = (1,0,0)
  DirMode = 2
  FaceMakerClass = Part::FaceMakerBullseye
  LengthFwd = 23
  LengthRev = 0
  Placement = pos=(-19,0,0) rot=(0,0,1;0rad)
  Solid = true
  Symmetric = false
FEATURE [Part::Fillet] Fillet038  label="removeToCreateVentalationHoles001"
  Base = -> Extrude046
  Edges = <same value as first occurrence — deduplicated (x6 in doc)>
  Placement = pos=(7,0,0) rot=(0,0,1;0rad)
FEATURE [Sketcher::SketchObject] Sketch056  label="topSketch014"
  FullyConstrained = true
  sketch-geometry (22):
    g0: LineSegment StartX=5.21097e-06 StartY=3 StartZ=0 EndX=5.21097e-06 EndY=19 EndZ=0
    g1: ArcOfCircle CenterX=19 CenterY=19 CenterZ=0 NormalX=0 NormalY=0 NormalZ=1 AngleXU=0 Radius=19 StartAngle=1.5708 EndAngle=3.14159
    g2: ArcOfCircle CenterX=19 CenterY=19 CenterZ=0 NormalX=0 NormalY=0 NormalZ=1 AngleXU=0 Radius=16 StartAngle=1.5708 EndAngle=3.14159
    g3: LineSegment StartX=114 StartY=35 StartZ=0 EndX=19 EndY=35 EndZ=0
    g4: LineSegment StartX=5.21097e-06 StartY=3 StartZ=0 EndX=5.21097e-06 EndY=0 EndZ=0
    g5: LineSegment StartX=3 StartY=0 StartZ=0 EndX=5.21097e-06 EndY=0 EndZ=0
    g6: LineSegment StartX=3 StartY=19 StartZ=0 EndX=3 EndY=0 EndZ=0
    g7: LineSegment StartX=19 StartY=38 StartZ=0 EndX=124 EndY=38 EndZ=0
    g8: Circle CenterX=119 CenterY=35 CenterZ=0 NormalX=0 NormalY=0 NormalZ=1 AngleXU=0 Radius=1
    g9: Circle CenterX=121 CenterY=35 CenterZ=0 NormalX=0 NormalY=0 NormalZ=1 AngleXU=0 Radius=1
    g10: Circle CenterX=121 CenterY=33 CenterZ=0 NormalX=0 NormalY=0 NormalZ=1 AngleXU=0 Radius=1
    g11: BSplineCurve PolesCount=3 KnotsCount=2 Degree=2 IsPeriodic=0
    g12: GeomPoint X=119 Y=35 Z=0
    g13: GeomPoint X=121 Y=33 Z=0
    g14: LineSegment StartX=119 StartY=35 StartZ=0 EndX=114 EndY=35 EndZ=0
    g15: ArcOfCircle CenterX=105 CenterY=19 CenterZ=0 NormalX=0 NormalY=0 NormalZ=1 AngleXU=0 Radius=16 StartAngle=5.60905 EndAngle=6.28319
    g16: LineSegment StartX=121 StartY=33 StartZ=0 EndX=121 EndY=19 EndZ=0
    g17: LineSegment StartX=117.5 StartY=9.01251 StartZ=0 EndX=121.163 EndY=9.0125 EndZ=0
    g18: ArcOfCircle CenterX=105 CenterY=19 CenterZ=0 NormalX=0 NormalY=0 NormalZ=1 AngleXU=0 Radius=20.6155 StartAngle=5.7297 EndAngle=6.28319
    g19: LineSegment StartX=121.163 StartY=9.0125 StartZ=0 EndX=122.538 EndY=8.16329 EndZ=0
    g20: LineSegment StartX=124 StartY=38 StartZ=0 EndX=125.616 EndY=38 EndZ=0
    g21: LineSegment StartX=125.616 StartY=19 StartZ=0 EndX=125.616 EndY=38 EndZ=0
  constraints (49):
    c: Vertical(g0)
    c: Block(g0)
    c: Coincident(g1,g0)
    c: Block(g1)
    c: Coincident(g2,g1)
    c: Block(g2)
    c: Coincident(g3,g2)
    c: Horizontal(g3)
    c: Tangent(g3,g2)
    c: Coincident(g4,g0)
    c: Distance(g4) = 3
    c: Vertical(g4)
    c: Coincident(g5,g4)
    c: Horizontal(g5)
    c: Coincident(g6,g2)
    c: Coincident(g6,g5)
    c: Vertical(g6)
    c: Horizontal(g7)
    c: Distance(g7) = 105
    c: Coincident(g7,g1)
    c: Block(g3)
    c: Weight(g8) = 1
    c: Equal(g8,g9)
    c: Equal(g8,g10)
    c: InternalAlignment(g8,g11)
    c: InternalAlignment(g9,g11)
    c: InternalAlignment(g10,g11)
    c: InternalAlignment(g12,g11)
    c: InternalAlignment(g13,g11)
    c: Block(g11)
    c: Coincident(g14,g11)
    c: Coincident(g14,g3)
    c: Horizontal(g14)
    c: Block(g15)
    c: Coincident(g16,g11)
    c: Coincident(g16,g15)
    c: Vertical(g16)
    c: Distance(g16) = 14
    c: Coincident(g17,g15)
    c: Block(g18)
    c: Coincident(g19,g18)
    c: Coincident(g20,g7)
    c: Horizontal(g20)
    c: Vertical(g21)
    c: Coincident(g20,g21)
    c: Block(g20)
    c: Block(g21)
    c: Block(g19)
    c: Block(g17)
FEATURE [Part::Box] Box026  label="removeToCreteHoleForPlugHousing032"
  AttacherType = Attacher::AttachEngine3D
  Height = 28.6
  Length = 10
  Placement = pos=(-2,0,21.7) rot=(0,0,1;0rad)
  Width = 19
FEATURE [Part::Feature] Face109 .. Face112  x4 (patterned run collapsed; names and placements below)
  shape: bbox 3.5 x 17.8 x 2e-07 mm, 1 faces, 0 solids (baked)
FEATURE [Part::Revolution] Revolve117  label="removeToCreateScrewAndThreadedInsertHole045"
  Angle = 360
  Axis = (0,1,0)
  Base = (0,0,0)
  FaceMakerClass = Part::FaceMakerBullseye
  Placement = pos=(62.3,30.3,19.7) rot=(0,0,1;0rad)
  Solid = false
  Source = -> Face109
  Symmetric = false
FEATURE [Part::Revolution] Revolve118  label="removeToCreateScrewAndThreadedInsertHole046"
  Angle = 360
  Axis = (0,1,0)
  Base = (0,0,0)
  FaceMakerClass = Part::FaceMakerBullseye
  Placement = pos=(62.3,30.3,51.7) rot=(0,0,1;0rad)
  Solid = false
  Source = -> Face110
  Symmetric = false
FEATURE [Part::Revolution] Revolve119  label="removeToCreateScrewAndThreadedInsertHole047"
  Angle = 360
  Axis = (0,1,0)
  Base = (0,0,0)
  FaceMakerClass = Part::FaceMakerBullseye
  Placement = pos=(30.3,30.3,19.7) rot=(0,0,1;0rad)
  Solid = false
  Source = -> Face111
  Symmetric = false
FEATURE [Part::Revolution] Revolve120  label="removeToCreateScrewAndThreadedInsertHole048"
  Angle = 360
  Axis = (0,1,0)
  Base = (0,0,0)
  FaceMakerClass = Part::FaceMakerBullseye
  Placement = pos=(30.3,30.3,51.7) rot=(0,0,1;0rad)
  Solid = false
  Source = -> Face112
  Symmetric = false
FEATURE [Part::MultiFuse] Fusion087  label="createThreadedInsertHolesForFan005"
  Shapes = -> [Revolve117,Revolve118,Revolve119,Revolve120]
FEATURE [Part::Extrusion] Extrude047
  Base = -> Sketch056
  Dir = (0,0,1)
  DirMode = 2
  FaceMakerClass = Part::FaceMakerBullseye
  LengthFwd = 72
  LengthRev = 0
  Solid = true
  Symmetric = false
FEATURE [Part::Fillet] Fillet039  label="top019"
  Base = -> Extrude047
  Edges = 1 edges r=2: [Edge35]
FEATURE [Sketcher::SketchObject] Sketch057
  FullyConstrained = false
  Placement = pos=(0,0,0) rot=(1,0,0;1.5708rad)
  sketch-geometry (24):
    g0: ArcOfCircle CenterX=-4 CenterY=-10.5 CenterZ=0 NormalX=0 NormalY=0 NormalZ=1 AngleXU=0 Radius=1.5 StartAngle=6e-16 EndAngle=3.14159
    g1: ArcOfCircle CenterX=-34.2 CenterY=-10.5 CenterZ=0 NormalX=0 NormalY=0 NormalZ=1 AngleXU=0 Radius=1.5 StartAngle=0 EndAngle=3.14159
    g2: ArcOfCircle CenterX=-34.2 CenterY=-27.7 CenterZ=0 NormalX=0 NormalY=0 NormalZ=1 AngleXU=0 Radius=1.5 StartAngle=3.14159 EndAngle=6.28319
    g3: ArcOfCircle CenterX=-4 CenterY=-27.7 CenterZ=0 NormalX=0 NormalY=0 NormalZ=1 AngleXU=0 Radius=1.5 StartAngle=3.1416 EndAngle=6.28319
    g4: ArcOfCircle CenterX=-10 CenterY=-4.3 CenterZ=0 NormalX=0 NormalY=0 NormalZ=1 AngleXU=0 Radius=1.5 StartAngle=2e-16 EndAngle=3.14159
    g5: ArcOfCircle CenterX=-16.1 CenterY=-1.8 CenterZ=0 NormalX=0 NormalY=0 NormalZ=1 AngleXU=0 Radius=1.5 StartAngle=5e-16 EndAngle=3.14159
    g6: ArcOfCircle CenterX=-22.1 CenterY=-1.8 CenterZ=0 NormalX=0 NormalY=0 NormalZ=1 AngleXU=0 Radius=1.5 StartAngle=5e-16 EndAngle=3.14159
    g7: ArcOfCircle CenterX=-28.2 CenterY=-4.3 CenterZ=0 NormalX=0 NormalY=0 NormalZ=1 AngleXU=0 Radius=1.5 StartAngle=2e-16 EndAngle=3.14159
    g8: ArcOfCircle CenterX=-10 CenterY=-33.9 CenterZ=0 NormalX=0 NormalY=0 NormalZ=1 AngleXU=0 Radius=1.5 StartAngle=3.14159 EndAngle=6.28319
    g9: ArcOfCircle CenterX=-16.1 CenterY=-36.4 CenterZ=0 NormalX=0 NormalY=0 NormalZ=1 AngleXU=0 Radius=1.5 StartAngle=3.14159 EndAngle=6.28319
    g10: ArcOfCircle CenterX=-22.1 CenterY=-36.4 CenterZ=0 NormalX=0 NormalY=0 NormalZ=1 AngleXU=0 Radius=1.5 StartAngle=3.14159 EndAngle=6.28319
    g11: ArcOfCircle CenterX=-28.2 CenterY=-33.9 CenterZ=0 NormalX=0 NormalY=0 NormalZ=1 AngleXU=0 Radius=1.5 StartAngle=3.14159 EndAngle=6.28319
    g12: LineSegment StartX=-35.7 StartY=-10.5 StartZ=0 EndX=-35.7 EndY=-27.7 EndZ=0
    g13: LineSegment StartX=-32.7 StartY=-10.5 StartZ=0 EndX=-32.7 EndY=-27.7 EndZ=0
    g14: LineSegment StartX=-29.7 StartY=-33.9 StartZ=0 EndX=-29.7 EndY=-4.3 EndZ=0
    g15: LineSegment StartX=-26.7 StartY=-33.9 StartZ=0 EndX=-26.7 EndY=-4.3 EndZ=0
    g16: LineSegment StartX=-2.5 StartY=-10.5 StartZ=0 EndX=-2.5 EndY=-27.7 EndZ=0
    g17: LineSegment StartX=-8.5 StartY=-4.3 StartZ=0 EndX=-8.5 EndY=-33.9 EndZ=0
    g18: LineSegment StartX=-5.5 StartY=-10.5 StartZ=0 EndX=-5.5 EndY=-27.7 EndZ=0
    g19: LineSegment StartX=-11.5 StartY=-4.3 StartZ=0 EndX=-11.5 EndY=-33.9 EndZ=0
    g20: LineSegment StartX=-14.6 StartY=-1.8 StartZ=0 EndX=-14.6 EndY=-36.4 EndZ=0
    g21: LineSegment StartX=-17.6 StartY=-1.8 StartZ=0 EndX=-17.6 EndY=-36.4 EndZ=0
    g22: LineSegment StartX=-20.6 StartY=-36.4 StartZ=0 EndX=-20.6 EndY=-1.8 EndZ=0
    g23: LineSegment StartX=-23.6 StartY=-1.8 StartZ=0 EndX=-23.6 EndY=-36.4 EndZ=0
  constraints (48):
    c: Block(g0)
    c: Block(g1)
    c: Block(g2)
    c: Block(g3)
    c: Block(g4)
    c: Block(g5)
    c: Block(g6)
    c: Block(g7)
    c: Block(g8)
    c: Block(g9)
    c: Block(g10)
    c: Block(g11)
    c: Coincident(g12,g1)
    c: Coincident(g12,g2)
    c: Vertical(g12)
    c: Coincident(g13,g1)
    c: Coincident(g13,g2)
    c: Vertical(g13)
    c: Coincident(g14,g11)
    c: Coincident(g14,g7)
    c: Vertical(g14)
    c: Coincident(g15,g11)
    c: Coincident(g15,g7)
    c: Vertical(g15)
    c: Coincident(g16,g0)
    c: Coincident(g16,g3)
    c: Vertical(g16)
    c: Coincident(g17,g4)
    c: Coincident(g17,g8)
    c: Vertical(g17)
    c: Coincident(g18,g0)
    c: Coincident(g18,g3)
    c: Vertical(g18)
    c: Coincident(g19,g4)
    c: Coincident(g19,g8)
    c: Vertical(g19)
    c: Coincident(g20,g5)
    c: Coincident(g20,g9)
    c: Vertical(g20)
    c: Coincident(g21,g5)
    c: Coincident(g21,g9)
    c: Vertical(g21)
    c: Coincident(g22,g10)
    c: Coincident(g22,g6)
    c: Vertical(g22)
    c: Coincident(g23,g6)
    c: Coincident(g23,g10)
    c: Vertical(g23)
FEATURE [Part::Extrusion] Extrude048  label="removeToCreateFanGrillHoles004"
  Base = -> Sketch057
  Dir = (0,-1,6e-16)
  DirMode = 2
  FaceMakerClass = Part::FaceMakerBullseye
  LengthFwd = 10
  LengthRev = 0
  Placement = pos=(65.4,44,54.82) rot=(0,0,1;0rad)
  Solid = true
  Symmetric = false
FEATURE [Part::Cut] Cut040  label="top021"
  Base = -> Fillet039
  Tool = -> Extrude048
FEATURE [Part::Cylinder] Cylinder041  label="removeToCreteHoleForPlugHousing034"
  Angle = 360
  AttacherType = Attacher::AttachEngine3D
  Height = 20
  Placement = pos=(-2,19,36) rot=(0,1,0;1.5708rad)
  Radius = 14.3
FEATURE [Part::MultiFuse] Fusion089  label="removeToCreteHoleForPlugHousing035"
  Shapes = -> [Box026,Cylinder041]
FEATURE [Part::Cylinder] Cylinder042
  Angle = 360
  AttacherType = Attacher::AttachEngine3D
  Height = 20
  Placement = pos=(0,0,36.15) rot=(0,0,1;0rad)
  Radius = 14.3
FEATURE [Part::Cylinder] Cylinder043
  Angle = 360
  AttacherType = Attacher::AttachEngine3D
  Height = 10
  Placement = pos=(0,0,36.15) rot=(0,0,1;0rad)
  Radius = 4
FEATURE [Part::Box] Box027  label="removeToCreteHoleForPlugHousing036"
  AttacherType = Attacher::AttachEngine3D
  Height = 28.6
  Length = 20
  Placement = pos=(106.15,0,21.7) rot=(0,0,1;0rad)
  Width = 19
FEATURE [Part::Cut] Cut041  label="top022"
  Base = -> Cut040
  Tool = -> Fusion087
FEATURE [Part::Cut] Cut039  label="top020"
  Base = -> Cut041
  Tool = -> Fusion089
FEATURE [Part::MultiFuse] Fusion090  label="removeToCreteHoleForPlugHousing037"
  Placement = pos=(70,19,36) rot=(0,1,0;1.5708rad)
  Shapes = -> [Cylinder042,Cylinder043]
FEATURE [Part::MultiFuse] Fusion088  label="removeToCreteHoleForPlugHousing033"
  Shapes = -> [Box027,Fusion090]
FEATURE [Part::Cut] Cut042  label="removeToCreteHoleForPlugHousing038"
  Base = -> Cut039
  Tool = -> Fusion088
FEATURE [Part::MultiFuse] Fusion091  label="removeFromTop"
  Shapes = -> [Fillet038,Fusion085,Fusion084,Fusion083,Extrude045]
FEATURE [Part::Cut] Cut043  label="REAL TOP ====="
  Base = -> Fillet036
  Tool = -> Fusion091
FEATURE [Part::MultiFuse] Fusion092  label="caseScrewPillarBracket016"
  Shapes = -> [Extrude030,Extrude031,Extrude032,Extrude033,Extrude034,Extrude035,Extrude036,Extrude037,Box013,Box014]
FEATURE [Sketcher::SketchObject] Sketch058  label="topSketch015"
  FullyConstrained = true
  sketch-geometry (20):
    g0: LineSegment StartX=5.21097e-06 StartY=3 StartZ=0 EndX=5.21097e-06 EndY=19 EndZ=0
    g1: ArcOfCircle CenterX=19 CenterY=19 CenterZ=0 NormalX=0 NormalY=0 NormalZ=1 AngleXU=0 Radius=19 StartAngle=1.5708 EndAngle=3.14159
    g2: ArcOfCircle CenterX=19 CenterY=19 CenterZ=0 NormalX=0 NormalY=0 NormalZ=1 AngleXU=0 Radius=16 StartAngle=1.5708 EndAngle=3.14159
    g3: LineSegment StartX=114 StartY=35 StartZ=0 EndX=19 EndY=35 EndZ=0
    g4: LineSegment StartX=5.21097e-06 StartY=3 StartZ=0 EndX=5.21097e-06 EndY=0 EndZ=0
    g5: LineSegment StartX=3 StartY=0 StartZ=0 EndX=5.21097e-06 EndY=0 EndZ=0
    g6: LineSegment StartX=3 StartY=19 StartZ=0 EndX=3 EndY=0 EndZ=0
    g7: LineSegment StartX=19 StartY=38 StartZ=0 EndX=124 EndY=38 EndZ=0
    g8: Circle CenterX=119 CenterY=35 CenterZ=0 NormalX=0 NormalY=0 NormalZ=1 AngleXU=0 Radius=1
    g9: Circle CenterX=121 CenterY=35 CenterZ=0 NormalX=0 NormalY=0 NormalZ=1 AngleXU=0 Radius=1
    g10: Circle CenterX=121 CenterY=33 CenterZ=0 NormalX=0 NormalY=0 NormalZ=1 AngleXU=0 Radius=1
    g11: BSplineCurve PolesCount=3 KnotsCount=2 Degree=2 IsPeriodic=0
    g12: GeomPoint X=119 Y=35 Z=0
    g13: GeomPoint X=121 Y=33 Z=0
    g14: LineSegment StartX=119 StartY=35 StartZ=0 EndX=114 EndY=35 EndZ=0
    g15: ArcOfCircle CenterX=105 CenterY=19 CenterZ=0 NormalX=0 NormalY=0 NormalZ=1 AngleXU=0 Radius=19 StartAngle=5.7297 EndAngle=6.28319
    g16: ArcOfCircle CenterX=105 CenterY=19 CenterZ=0 NormalX=0 NormalY=0 NormalZ=1 AngleXU=0 Radius=16 StartAngle=5.60905 EndAngle=6.28319
    g17: LineSegment StartX=121 StartY=33 StartZ=0 EndX=121 EndY=19 EndZ=0
    g18: LineSegment StartX=124 StartY=38 StartZ=0 EndX=124 EndY=19 EndZ=0
    g19: LineSegment StartX=117.5 StartY=9.01251 StartZ=0 EndX=121.163 EndY=9.0125 EndZ=0
  constraints (46):
    c: Vertical(g0)
    c: Block(g0)
    c: Coincident(g1,g0)
    c: Block(g1)
    c: Coincident(g2,g1)
    c: Block(g2)
    c: Coincident(g3,g2)
    c: Horizontal(g3)
    c: Tangent(g3,g2)
    c: Coincident(g4,g0)
    c: Distance(g4) = 3
    c: Vertical(g4)
    c: Coincident(g5,g4)
    c: Horizontal(g5)
    c: Coincident(g6,g2)
    c: Coincident(g6,g5)
    c: Vertical(g6)
    c: Horizontal(g7)
    c: Distance(g7) = 105
    c: Coincident(g7,g1)
    c: Block(g3)
    c: Weight(g8) = 1
    c: Equal(g8,g9)
    c: Equal(g8,g10)
    c: InternalAlignment(g8,g11)
    c: InternalAlignment(g9,g11)
    c: InternalAlignment(g10,g11)
    c: InternalAlignment(g12,g11)
    c: InternalAlignment(g13,g11)
    c: Block(g11)
    c: Coincident(g14,g11)
    c: Coincident(g14,g3)
    c: Horizontal(g14)
    c: Block(g15)
    c: Coincident(g16,g15)
    c: Block(g16)
    c: Coincident(g17,g11)
    c: Coincident(g17,g16)
    c: Vertical(g17)
    c: Distance(g17) = 14
    c: Coincident(g18,g7)
    c: Coincident(g18,g15)
    c: Vertical(g18)
    c: Distance(g18) = 19
    c: Coincident(g19,g16)
    c: Coincident(g19,g15)
FEATURE [Part::Extrusion] Extrude049  label="top023"
  Base = -> Sketch058
  Dir = (0,0,1)
  DirMode = 2
  FaceMakerClass = Part::FaceMakerBullseye
  LengthFwd = 72
  LengthRev = 0
  Solid = true
  Symmetric = false
FEATURE [Sketcher::SketchObject] Sketch059
  FullyConstrained = true
  MapMode = 3
  Placement = pos=(0,0,0) rot=(1,0,0;1.5708rad)
  Support = -> [Extrude049]
  sketch-geometry (8):
    g0: Circle CenterX=80.351 CenterY=-67.6202 CenterZ=0 NormalX=0 NormalY=0 NormalZ=1 AngleXU=0 Radius=2
    g1: Circle CenterX=80.351 CenterY=-67.6202 CenterZ=0 NormalX=0 NormalY=0 NormalZ=1 AngleXU=0 Radius=3
    g2: Circle CenterX=80.351 CenterY=-4.92017 CenterZ=0 NormalX=0 NormalY=0 NormalZ=1 AngleXU=0 Radius=2
    g3: Circle CenterX=80.351 CenterY=-4.92017 CenterZ=0 NormalX=0 NormalY=0 NormalZ=1 AngleXU=0 Radius=3
    g4: Circle CenterX=23.851 CenterY=-4.92017 CenterZ=0 NormalX=0 NormalY=0 NormalZ=1 AngleXU=0 Radius=2
    g5: Circle CenterX=23.851 CenterY=-4.92017 CenterZ=0 NormalX=0 NormalY=0 NormalZ=1 AngleXU=0 Radius=3
    g6: Circle CenterX=23.851 CenterY=-67.6202 CenterZ=0 NormalX=0 NormalY=0 NormalZ=1 AngleXU=0 Radius=2
    g7: Circle CenterX=23.851 CenterY=-67.6202 CenterZ=0 NormalX=0 NormalY=0 NormalZ=1 AngleXU=0 Radius=3
  constraints (8):
    c: Block(g3)
    c: Block(g2)
    c: Block(g1)
    c: Block(g0)
    c: Block(g6)
    c: Block(g7)
    c: Block(g4)
    c: Block(g5)
FEATURE [Sketcher::SketchObject] Sketch060
  FullyConstrained = true
  MapMode = 3
  Placement = pos=(0,0,0) rot=(1,0,0;1.5708rad)
  Support = -> [Extrude049]
  sketch-geometry (8):
    g0: Circle CenterX=80.351 CenterY=-67.6202 CenterZ=0 NormalX=0 NormalY=0 NormalZ=1 AngleXU=0 Radius=3
    g1: Circle CenterX=80.351 CenterY=-4.92017 CenterZ=0 NormalX=0 NormalY=0 NormalZ=1 AngleXU=0 Radius=3
    g2: Circle CenterX=23.851 CenterY=-4.92017 CenterZ=0 NormalX=0 NormalY=0 NormalZ=1 AngleXU=0 Radius=3
    g3: Circle CenterX=23.851 CenterY=-67.6202 CenterZ=0 NormalX=0 NormalY=0 NormalZ=1 AngleXU=0 Radius=3
    g4: Circle CenterX=23.851 CenterY=-67.6202 CenterZ=0 NormalX=0 NormalY=0 NormalZ=1 AngleXU=0 Radius=5
    g5: Circle CenterX=80.351 CenterY=-67.6202 CenterZ=0 NormalX=0 NormalY=0 NormalZ=1 AngleXU=0 Radius=5
    g6: Circle CenterX=23.851 CenterY=-4.92017 CenterZ=0 NormalX=0 NormalY=0 NormalZ=1 AngleXU=0 Radius=5
    g7: Circle CenterX=80.351 CenterY=-4.92017 CenterZ=0 NormalX=0 NormalY=0 NormalZ=1 AngleXU=0 Radius=5
  constraints (8):
    c: Block(g1)
    c: Block(g0)
    c: Block(g3)
    c: Block(g2)
    c: Block(g5)
    c: Block(g4)
    c: Block(g6)
    c: Block(g7)
FEATURE [Sketcher::SketchObject] Sketch061
  FullyConstrained = true
  MapMode = 3
  Placement = pos=(0,0,0) rot=(1,0,0;1.5708rad)
  sketch-geometry (8):
    g0: Circle CenterX=80.351 CenterY=-67.6202 CenterZ=0 NormalX=0 NormalY=0 NormalZ=1 AngleXU=0 Radius=3
    g1: Circle CenterX=80.351 CenterY=-4.92017 CenterZ=0 NormalX=0 NormalY=0 NormalZ=1 AngleXU=0 Radius=3
    g2: Circle CenterX=23.851 CenterY=-4.92017 CenterZ=0 NormalX=0 NormalY=0 NormalZ=1 AngleXU=0 Radius=3
    g3: Circle CenterX=23.851 CenterY=-67.6202 CenterZ=0 NormalX=0 NormalY=0 NormalZ=1 AngleXU=0 Radius=3
    g4: Circle CenterX=23.851 CenterY=-67.6202 CenterZ=0 NormalX=0 NormalY=0 NormalZ=1 AngleXU=0 Radius=5
    g5: Circle CenterX=80.351 CenterY=-67.6202 CenterZ=0 NormalX=0 NormalY=0 NormalZ=1 AngleXU=0 Radius=5
    g6: Circle CenterX=23.851 CenterY=-4.92017 CenterZ=0 NormalX=0 NormalY=0 NormalZ=1 AngleXU=0 Radius=5
    g7: Circle CenterX=80.351 CenterY=-4.92017 CenterZ=0 NormalX=0 NormalY=0 NormalZ=1 AngleXU=0 Radius=5
  constraints (8):
    c: Block(g1)
    c: Block(g0)
    c: Block(g3)
    c: Block(g2)
    c: Block(g5)
    c: Block(g4)
    c: Block(g6)
    c: Block(g7)
FEATURE [Sketcher::SketchObject] Sketch062  label="topSketch016"
  FullyConstrained = true
  sketch-geometry (20):
    g0: LineSegment StartX=5.21097e-06 StartY=3 StartZ=0 EndX=5.21097e-06 EndY=19 EndZ=0
    g1: ArcOfCircle CenterX=19 CenterY=19 CenterZ=0 NormalX=0 NormalY=0 NormalZ=1 AngleXU=0 Radius=19 StartAngle=1.5708 EndAngle=3.14159
    g2: ArcOfCircle CenterX=19 CenterY=19 CenterZ=0 NormalX=0 NormalY=0 NormalZ=1 AngleXU=0 Radius=16 StartAngle=1.5708 EndAngle=3.14159
    g3: LineSegment StartX=114 StartY=35 StartZ=0 EndX=19 EndY=35 EndZ=0
    g4: LineSegment StartX=5.21097e-06 StartY=3 StartZ=0 EndX=5.21097e-06 EndY=0 EndZ=0
    g5: LineSegment StartX=3 StartY=0 StartZ=0 EndX=5.21097e-06 EndY=0 EndZ=0
    g6: LineSegment StartX=3 StartY=19 StartZ=0 EndX=3 EndY=0 EndZ=0
    g7: LineSegment StartX=19 StartY=38 StartZ=0 EndX=124 EndY=38 EndZ=0
    g8: Circle CenterX=119 CenterY=35 CenterZ=0 NormalX=0 NormalY=0 NormalZ=1 AngleXU=0 Radius=1
    g9: Circle CenterX=121 CenterY=35 CenterZ=0 NormalX=0 NormalY=0 NormalZ=1 AngleXU=0 Radius=1
    g10: Circle CenterX=121 CenterY=33 CenterZ=0 NormalX=0 NormalY=0 NormalZ=1 AngleXU=0 Radius=1
    g11: BSplineCurve PolesCount=3 KnotsCount=2 Degree=2 IsPeriodic=0
    g12: GeomPoint X=119 Y=35 Z=0
    g13: GeomPoint X=121 Y=33 Z=0
    g14: LineSegment StartX=119 StartY=35 StartZ=0 EndX=114 EndY=35 EndZ=0
    g15: ArcOfCircle CenterX=105 CenterY=19 CenterZ=0 NormalX=0 NormalY=0 NormalZ=1 AngleXU=0 Radius=19 StartAngle=5.7297 EndAngle=6.28319
    g16: ArcOfCircle CenterX=105 CenterY=19 CenterZ=0 NormalX=0 NormalY=0 NormalZ=1 AngleXU=0 Radius=16 StartAngle=5.60905 EndAngle=6.28319
    g17: LineSegment StartX=121 StartY=33 StartZ=0 EndX=121 EndY=19 EndZ=0
    g18: LineSegment StartX=124 StartY=38 StartZ=0 EndX=124 EndY=19 EndZ=0
    g19: LineSegment StartX=117.5 StartY=9.01251 StartZ=0 EndX=121.163 EndY=9.0125 EndZ=0
  constraints (46):
    c: Vertical(g0)
    c: Block(g0)
    c: Coincident(g1,g0)
    c: Block(g1)
    c: Coincident(g2,g1)
    c: Block(g2)
    c: Coincident(g3,g2)
    c: Horizontal(g3)
    c: Tangent(g3,g2)
    c: Coincident(g4,g0)
    c: Distance(g4) = 3
    c: Vertical(g4)
    c: Coincident(g5,g4)
    c: Horizontal(g5)
    c: Coincident(g6,g2)
    c: Coincident(g6,g5)
    c: Vertical(g6)
    c: Horizontal(g7)
    c: Distance(g7) = 105
    c: Coincident(g7,g1)
    c: Block(g3)
    c: Weight(g8) = 1
    c: Equal(g8,g9)
    c: Equal(g8,g10)
    c: InternalAlignment(g8,g11)
    c: InternalAlignment(g9,g11)
    c: InternalAlignment(g10,g11)
    c: InternalAlignment(g12,g11)
    c: InternalAlignment(g13,g11)
    c: Block(g11)
    c: Coincident(g14,g11)
    c: Coincident(g14,g3)
    c: Horizontal(g14)
    c: Block(g15)
    c: Coincident(g16,g15)
    c: Block(g16)
    c: Coincident(g17,g11)
    c: Coincident(g17,g16)
    c: Vertical(g17)
    c: Distance(g17) = 14
    c: Coincident(g18,g7)
    c: Coincident(g18,g15)
    c: Vertical(g18)
    c: Distance(g18) = 19
    c: Coincident(g19,g16)
    c: Coincident(g19,g15)
FEATURE [Part::Extrusion] Extrude053  label="top024"
  Base = -> Sketch062
  Dir = (0,0,1)
  DirMode = 2
  FaceMakerClass = Part::FaceMakerBullseye
  LengthFwd = 72
  LengthRev = 0
  Solid = true
  Symmetric = false
FEATURE [Sketcher::SketchObject] Sketch063
  FullyConstrained = true
  MapMode = 3
  Placement = pos=(0,0,0) rot=(1,0,0;1.5708rad)
  Support = -> [Extrude053]
  sketch-geometry (8):
    g0: Circle CenterX=80.351 CenterY=-67.6202 CenterZ=0 NormalX=0 NormalY=0 NormalZ=1 AngleXU=0 Radius=2
    g1: Circle CenterX=80.351 CenterY=-67.6202 CenterZ=0 NormalX=0 NormalY=0 NormalZ=1 AngleXU=0 Radius=3
    g2: Circle CenterX=80.351 CenterY=-4.92017 CenterZ=0 NormalX=0 NormalY=0 NormalZ=1 AngleXU=0 Radius=2
    g3: Circle CenterX=80.351 CenterY=-4.92017 CenterZ=0 NormalX=0 NormalY=0 NormalZ=1 AngleXU=0 Radius=3
    g4: Circle CenterX=23.851 CenterY=-4.92017 CenterZ=0 NormalX=0 NormalY=0 NormalZ=1 AngleXU=0 Radius=2
    g5: Circle CenterX=23.851 CenterY=-4.92017 CenterZ=0 NormalX=0 NormalY=0 NormalZ=1 AngleXU=0 Radius=3
    g6: Circle CenterX=23.851 CenterY=-67.6202 CenterZ=0 NormalX=0 NormalY=0 NormalZ=1 AngleXU=0 Radius=2
    g7: Circle CenterX=23.851 CenterY=-67.6202 CenterZ=0 NormalX=0 NormalY=0 NormalZ=1 AngleXU=0 Radius=3
  constraints (8):
    c: Block(g3)
    c: Block(g2)
    c: Block(g1)
    c: Block(g0)
    c: Block(g6)
    c: Block(g7)
    c: Block(g4)
    c: Block(g5)
FEATURE [Part::Extrusion] Extrude054
  Base = -> Sketch063
  Dir = (0,-1,2e-16)
  DirMode = 2
  FaceMakerClass = Part::FaceMakerBullseye
  LengthFwd = 6
  LengthRev = 0
  Placement = pos=(0,9,0) rot=(0,0,1;0rad)
  Solid = true
  Symmetric = false
FEATURE [Sketcher::SketchObject] Sketch064  label="topSketch017"
  FullyConstrained = true
  sketch-geometry (20):
    g0: LineSegment StartX=5.21097e-06 StartY=3 StartZ=0 EndX=5.21097e-06 EndY=19 EndZ=0
    g1: ArcOfCircle CenterX=19 CenterY=19 CenterZ=0 NormalX=0 NormalY=0 NormalZ=1 AngleXU=0 Radius=19 StartAngle=1.5708 EndAngle=3.14159
    g2: ArcOfCircle CenterX=19 CenterY=19 CenterZ=0 NormalX=0 NormalY=0 NormalZ=1 AngleXU=0 Radius=16 StartAngle=1.5708 EndAngle=3.14159
    g3: LineSegment StartX=114 StartY=35 StartZ=0 EndX=19 EndY=35 EndZ=0
    g4: LineSegment StartX=5.21097e-06 StartY=3 StartZ=0 EndX=5.21097e-06 EndY=0 EndZ=0
    g5: LineSegment StartX=3 StartY=0 StartZ=0 EndX=5.21097e-06 EndY=0 EndZ=0
    g6: LineSegment StartX=3 StartY=19 StartZ=0 EndX=3 EndY=0 EndZ=0
    g7: LineSegment StartX=19 StartY=38 StartZ=0 EndX=124 EndY=38 EndZ=0
    g8: Circle CenterX=119 CenterY=35 CenterZ=0 NormalX=0 NormalY=0 NormalZ=1 AngleXU=0 Radius=1
    g9: Circle CenterX=121 CenterY=35 CenterZ=0 NormalX=0 NormalY=0 NormalZ=1 AngleXU=0 Radius=1
    g10: Circle CenterX=121 CenterY=33 CenterZ=0 NormalX=0 NormalY=0 NormalZ=1 AngleXU=0 Radius=1
    g11: BSplineCurve PolesCount=3 KnotsCount=2 Degree=2 IsPeriodic=0
    g12: GeomPoint X=119 Y=35 Z=0
    g13: GeomPoint X=121 Y=33 Z=0
    g14: LineSegment StartX=119 StartY=35 StartZ=0 EndX=114 EndY=35 EndZ=0
    g15: ArcOfCircle CenterX=105 CenterY=19 CenterZ=0 NormalX=0 NormalY=0 NormalZ=1 AngleXU=0 Radius=19 StartAngle=5.7297 EndAngle=6.28319
    g16: ArcOfCircle CenterX=105 CenterY=19 CenterZ=0 NormalX=0 NormalY=0 NormalZ=1 AngleXU=0 Radius=16 StartAngle=5.60905 EndAngle=6.28319
    g17: LineSegment StartX=121 StartY=33 StartZ=0 EndX=121 EndY=19 EndZ=0
    g18: LineSegment StartX=124 StartY=38 StartZ=0 EndX=124 EndY=19 EndZ=0
    g19: LineSegment StartX=117.5 StartY=9.01251 StartZ=0 EndX=121.163 EndY=9.0125 EndZ=0
  constraints (46):
    c: Vertical(g0)
    c: Block(g0)
    c: Coincident(g1,g0)
    c: Block(g1)
    c: Coincident(g2,g1)
    c: Block(g2)
    c: Coincident(g3,g2)
    c: Horizontal(g3)
    c: Tangent(g3,g2)
    c: Coincident(g4,g0)
    c: Distance(g4) = 3
    c: Vertical(g4)
    c: Coincident(g5,g4)
    c: Horizontal(g5)
    c: Coincident(g6,g2)
    c: Coincident(g6,g5)
    c: Vertical(g6)
    c: Horizontal(g7)
    c: Distance(g7) = 105
    c: Coincident(g7,g1)
    c: Block(g3)
    c: Weight(g8) = 1
    c: Equal(g8,g9)
    c: Equal(g8,g10)
    c: InternalAlignment(g8,g11)
    c: InternalAlignment(g9,g11)
    c: InternalAlignment(g10,g11)
    c: InternalAlignment(g12,g11)
    c: InternalAlignment(g13,g11)
    c: Block(g11)
    c: Coincident(g14,g11)
    c: Coincident(g14,g3)
    c: Horizontal(g14)
    c: Block(g15)
    c: Coincident(g16,g15)
    c: Block(g16)
    c: Coincident(g17,g11)
    c: Coincident(g17,g16)
    c: Vertical(g17)
    c: Distance(g17) = 14
    c: Coincident(g18,g7)
    c: Coincident(g18,g15)
    c: Vertical(g18)
    c: Distance(g18) = 19
    c: Coincident(g19,g16)
    c: Coincident(g19,g15)
FEATURE [Sketcher::SketchObject] Sketch065
  FullyConstrained = true
  MapMode = 3
  Placement = pos=(0,0,0) rot=(1,0,0;1.5708rad)
  sketch-geometry (8):
    g0: Circle CenterX=80.351 CenterY=-67.6202 CenterZ=0 NormalX=0 NormalY=0 NormalZ=1 AngleXU=0 Radius=3
    g1: Circle CenterX=80.351 CenterY=-4.92017 CenterZ=0 NormalX=0 NormalY=0 NormalZ=1 AngleXU=0 Radius=3
    g2: Circle CenterX=23.851 CenterY=-4.92017 CenterZ=0 NormalX=0 NormalY=0 NormalZ=1 AngleXU=0 Radius=3
    g3: Circle CenterX=23.851 CenterY=-67.6202 CenterZ=0 NormalX=0 NormalY=0 NormalZ=1 AngleXU=0 Radius=3
    g4: Circle CenterX=23.851 CenterY=-67.6202 CenterZ=0 NormalX=0 NormalY=0 NormalZ=1 AngleXU=0 Radius=5
    g5: Circle CenterX=80.351 CenterY=-67.6202 CenterZ=0 NormalX=0 NormalY=0 NormalZ=1 AngleXU=0 Radius=5
    g6: Circle CenterX=23.851 CenterY=-4.92017 CenterZ=0 NormalX=0 NormalY=0 NormalZ=1 AngleXU=0 Radius=5
    g7: Circle CenterX=80.351 CenterY=-4.92017 CenterZ=0 NormalX=0 NormalY=0 NormalZ=1 AngleXU=0 Radius=5
  constraints (8):
    c: Block(g1)
    c: Block(g0)
    c: Block(g3)
    c: Block(g2)
    c: Block(g5)
    c: Block(g4)
    c: Block(g6)
    c: Block(g7)
FEATURE [Part::Extrusion] Extrude056
  Base = -> Sketch065
  Dir = (0,-1,2e-16)
  DirMode = 2
  FaceMakerClass = Part::FaceMakerBullseye
  LengthFwd = 2
  LengthRev = 0
  Solid = true
  Symmetric = false
FEATURE [Part::Extrusion] Extrude057  label="top025"
  Base = -> Sketch064
  Dir = (0,0,1)
  DirMode = 2
  FaceMakerClass = Part::FaceMakerBullseye
  LengthFwd = 72
  LengthRev = 0
  Solid = true
  Symmetric = false
FEATURE [Sketcher::SketchObject] Sketch066
  FullyConstrained = true
  MapMode = 3
  Placement = pos=(0,0,0) rot=(1,0,0;1.5708rad)
  Support = -> [Extrude057]
  sketch-geometry (8):
    g0: Circle CenterX=80.351 CenterY=-67.6202 CenterZ=0 NormalX=0 NormalY=0 NormalZ=1 AngleXU=0 Radius=3
    g1: Circle CenterX=80.351 CenterY=-4.92017 CenterZ=0 NormalX=0 NormalY=0 NormalZ=1 AngleXU=0 Radius=3
    g2: Circle CenterX=23.851 CenterY=-4.92017 CenterZ=0 NormalX=0 NormalY=0 NormalZ=1 AngleXU=0 Radius=3
    g3: Circle CenterX=23.851 CenterY=-67.6202 CenterZ=0 NormalX=0 NormalY=0 NormalZ=1 AngleXU=0 Radius=3
    g4: Circle CenterX=23.851 CenterY=-67.6202 CenterZ=0 NormalX=0 NormalY=0 NormalZ=1 AngleXU=0 Radius=5
    g5: Circle CenterX=80.351 CenterY=-67.6202 CenterZ=0 NormalX=0 NormalY=0 NormalZ=1 AngleXU=0 Radius=5
    g6: Circle CenterX=23.851 CenterY=-4.92017 CenterZ=0 NormalX=0 NormalY=0 NormalZ=1 AngleXU=0 Radius=5
    g7: Circle CenterX=80.351 CenterY=-4.92017 CenterZ=0 NormalX=0 NormalY=0 NormalZ=1 AngleXU=0 Radius=5
  constraints (8):
    c: Block(g1)
    c: Block(g0)
    c: Block(g3)
    c: Block(g2)
    c: Block(g5)
    c: Block(g4)
    c: Block(g6)
    c: Block(g7)
FEATURE [Part::Extrusion] Extrude055
  Base = -> Sketch066
  Dir = (0,-1,2e-16)
  DirMode = 2
  FaceMakerClass = Part::FaceMakerBullseye
  LengthFwd = 2
  LengthRev = 0
  Solid = true
  Symmetric = false
FEATURE [Part::Fillet] Fillet041
  Base = -> Extrude056
  Edges = 4 edges r=1.99: [Edge6,Edge12,Edge18,Edge24]
FEATURE [Part::Cut] Cut045
  Base = -> Extrude055
  Placement = pos=(0,6,0) rot=(0,0,1;0rad)
  Tool = -> Fillet041
FEATURE [Part::MultiFuse] Fusion095  label="pcbScrewPillars"
  Placement = pos=(-3.2,-1,72.3) rot=(0,0,1;0rad)
  Shapes = -> [Cut045,Extrude054]
FEATURE [Part::Feature] Face113
  shape: bbox 3.2 x 1.5 x 2e-07 mm, 1 faces, 0 solids (baked)
FEATURE [Part::Revolution] Revolve121  label="backCaseScrewRetainer002"
  Angle = 360
  Axis = (0,1,0)
  Base = (0,0,0)
  FaceMakerClass = Part::FaceMakerBullseye
  Placement = pos=(12.5,3,62) rot=(0,0,1;0rad)
  Solid = false
  Source = -> Face113
  Symmetric = false
FEATURE [Part::Feature] Face114
  shape: bbox 3.2 x 1.5 x 2e-07 mm, 1 faces, 0 solids (baked)
FEATURE [Part::Feature] Face115
  shape: bbox 3.2 x 1.5 x 2e-07 mm, 1 faces, 0 solids (baked)
FEATURE [Part::Feature] Face116
  shape: bbox 3.2 x 1.5 x 2e-07 mm, 1 faces, 0 solids (baked)
FEATURE [Part::Revolution] Revolve122  label="frontCaseScrewRetainer004"
  Angle = 360
  Axis = (0,1,0)
  Base = (0,0,0)
  FaceMakerClass = Part::FaceMakerBullseye
  Placement = pos=(89.5,3,68.5) rot=(0,0,1;0rad)
  Solid = false
  Source = -> Face115
  Symmetric = false
FEATURE [Part::Revolution] Revolve123  label="frontCaseScrewRetainer005"
  Angle = 360
  Axis = (0,1,0)
  Base = (0,0,0)
  FaceMakerClass = Part::FaceMakerBullseye
  Placement = pos=(89.5,3,3.5) rot=(0,0,1;0rad)
  Solid = false
  Source = -> Face116
  Symmetric = false
FEATURE [Part::Revolution] Revolve124  label="backCaseScrewRetainer003"
  Angle = 360
  Axis = (0,1,0)
  Base = (0,0,0)
  FaceMakerClass = Part::FaceMakerBullseye
  Placement = pos=(12.5,3,10) rot=(0,0,1;0rad)
  Solid = false
  Source = -> Face114
  Symmetric = false
FEATURE [Part::Feature] Face117
  shape: bbox 3.6 x 3.2 x 2e-07 mm, 1 faces, 0 solids (baked)
FEATURE [Part::Revolution] Revolve125  label="moreFrontCaseScrewRetainer004"
  Angle = 360
  Axis = (0,1,0)
  Base = (0,0,0)
  FaceMakerClass = Part::FaceMakerBullseye
  Placement = pos=(109.5,4.5,68.5) rot=(0,0,1;0rad)
  Solid = false
  Source = -> Face117
  Symmetric = false
FEATURE [Part::Feature] Face118
  shape: bbox 3.6 x 3.2 x 2e-07 mm, 1 faces, 0 solids (baked)
FEATURE [Part::Revolution] Revolve126  label="moreFrontCaseScrewRetainer005"
  Angle = 360
  Axis = (0,1,0)
  Base = (0,0,0)
  FaceMakerClass = Part::FaceMakerBullseye
  Placement = pos=(109.5,4.5,3.5) rot=(0,0,1;0rad)
  Solid = false
  Source = -> Face118
  Symmetric = false
FEATURE [Part::MultiFuse] Fusion096  label="screwRetainers001"
  Shapes = -> [Revolve126,Revolve125,Revolve124,Revolve123,Revolve122,Revolve121]
FEATURE [Part::Feature] Face119
  shape: bbox 10 x 16.5 x 2e-07 mm, 1 faces, 0 solids (baked)
FEATURE [Part::Revolution] Revolve130  label="plugHousing050"
  Angle = 360
  Axis = (0,1,0)
  Base = (0,0,0)
  FaceMakerClass = Part::FaceMakerBullseye
  Placement = pos=(0,0,36.15) rot=(0,0,1;0rad)
  Solid = false
  Source = -> Face119
  Symmetric = false
FEATURE [Part::Feature] Face120
  shape: bbox 10 x 16.5 x 2e-07 mm, 1 faces, 0 solids (baked)
FEATURE [Part::Feature] Face121
  shape: bbox 10 x 16.5 x 2e-07 mm, 1 faces, 0 solids (baked)
FEATURE [Part::Revolution] Revolve127  label="plugHousing047"
  Angle = 360
  Axis = (0,1,0)
  Base = (0,0,0)
  FaceMakerClass = Part::FaceMakerBullseye
  Placement = pos=(0,0,36.15) rot=(0,0,1;0rad)
  Solid = false
  Source = -> Face121
  Symmetric = false
FEATURE [Part::Feature] Face122
  shape: bbox 10 x 16.5 x 2e-07 mm, 1 faces, 0 solids (baked)
FEATURE [Part::Feature] Face123
  shape: bbox 10 x 16.5 x 2e-07 mm, 1 faces, 0 solids (baked)
FEATURE [Part::Revolution] Revolve128  label="plugHousing048"
  Angle = 360
  Axis = (0,1,0)
  Base = (0,0,0)
  FaceMakerClass = Part::FaceMakerBullseye
  Placement = pos=(0,0,36.15) rot=(0,0,1;0rad)
  Solid = false
  Source = -> Face123
  Symmetric = false
FEATURE [Part::MultiFuse] Fusion100  label="plugHousing054"
  Placement = pos=(0,0,0) rot=(0,0,1;1.5708rad)
  Shapes = -> [Revolve130,Revolve128]
FEATURE [Part::Feature] Face124
  shape: bbox 10 x 16.5 x 2e-07 mm, 1 faces, 0 solids (baked)
FEATURE [Part::Feature] Face125
  shape: bbox 10 x 16.5 x 2e-07 mm, 1 faces, 0 solids (baked)
FEATURE [Part::Revolution] Revolve129  label="plugHousing049"
  Angle = 360
  Axis = (0,1,0)
  Base = (0,0,0)
  FaceMakerClass = Part::FaceMakerBullseye
  Placement = pos=(0,0,36.15) rot=(0,0,1;0rad)
  Solid = false
  Source = -> Face125
  Symmetric = false
FEATURE [Part::Feature] Face126
  shape: bbox 10 x 16.5 x 2e-07 mm, 1 faces, 0 solids (baked)
FEATURE [Part::Revolution] Revolve131  label="plugHousing058"
  Angle = 360
  Axis = (0,1,0)
  Base = (0,0,0)
  FaceMakerClass = Part::FaceMakerBullseye
  Placement = pos=(0,0,36.15) rot=(0,0,1;0rad)
  Solid = false
  Source = -> Face120
  Symmetric = false
FEATURE [Part::MultiFuse] Fusion099  label="plugHousing053"
  Placement = pos=(0,0,0) rot=(0,0,1;1.5708rad)
  Shapes = -> [Revolve127,Revolve131]
FEATURE [Part::MultiFuse] Fusion102  label="plugHousing056"
  Placement = pos=(0,19,0) rot=(0,0,1;3.14159rad)
  Shapes = -> [Fusion100,Fusion099]
FEATURE [Part::Revolution] Revolve132  label="plugHousing059"
  Angle = 360
  Axis = (0,1,0)
  Base = (0,0,0)
  FaceMakerClass = Part::FaceMakerBullseye
  Placement = pos=(0,0,36.15) rot=(0,0,1;0rad)
  Solid = false
  Source = -> Face126
  Symmetric = false
FEATURE [Part::Revolution] Revolve133  label="plugHousing060"
  Angle = 360
  Axis = (0,1,0)
  Base = (0,0,0)
  FaceMakerClass = Part::FaceMakerBullseye
  Placement = pos=(0,0,36.15) rot=(0,0,1;0rad)
  Solid = false
  Source = -> Face122
  Symmetric = false
FEATURE [Part::MultiFuse] Fusion097  label="plugHousing051"
  Placement = pos=(0,0,0) rot=(0,0,1;1.5708rad)
  Shapes = -> [Revolve133,Revolve132]
FEATURE [Part::Revolution] Revolve134  label="plugHousing061"
  Angle = 360
  Axis = (0,1,0)
  Base = (0,0,0)
  FaceMakerClass = Part::FaceMakerBullseye
  Placement = pos=(0,0,36.15) rot=(0,0,1;0rad)
  Solid = false
  Source = -> Face124
  Symmetric = false
FEATURE [Part::MultiFuse] Fusion101  label="plugHousing055"
  Placement = pos=(0,0,0) rot=(0,0,1;1.5708rad)
  Shapes = -> [Revolve129,Revolve134]
FEATURE [Part::MultiFuse] Fusion098  label="plugHousing052"
  Placement = pos=(0,19,0) rot=(0,0,1;3.14159rad)
  Shapes = -> [Fusion097,Fusion101]
FEATURE [Part::MultiFuse] Fusion103  label="plugHousing057"
  Placement = pos=(122.621,0,-0.15) rot=(0,0,1;0rad)
  Shapes = -> [Fusion102,Fusion098]
FEATURE [Part::Box] Box028  label="Cube015"
  AttacherType = Attacher::AttachEngine3D
  Height = 28
  Length = 3
  Placement = pos=(110.7,19,22) rot=(0,0,1;0rad)
  Width = 15.7
FEATURE [Part::Cylinder] Cylinder044
  Angle = 360
  AttacherType = Attacher::AttachEngine3D
  Height = 20
  Placement = pos=(0,0,36.15) rot=(0,0,1;0rad)
  Radius = 10.3
FEATURE [Part::Cylinder] Cylinder045
  Angle = 360
  AttacherType = Attacher::AttachEngine3D
  Height = 10
  Placement = pos=(0,0,36.15) rot=(0,0,1;0rad)
  Radius = 4
FEATURE [Part::MultiFuse] Fusion104  label="removeToCreteHoleForPlugHousing040"
  Placement = pos=(70,19,36) rot=(0,1,0;1.5708rad)
  Shapes = -> [Cylinder044,Cylinder045]
FEATURE [Part::Cut] Cut046  label="plugHousingTab003"
  Base = -> Box028
  Tool = -> Fusion104
FEATURE [Part::MultiFuse] Fusion105  label="plugHousing062"
  Shapes = -> [Fusion103,Cut046]
FEATURE [Part::Fillet] Fillet042
  Base = -> Fusion105
  Edges = 1 edges r=2: [Edge25]
FEATURE [Part::Fillet] Fillet043  label="plugHousing063"
  Base = -> Fillet042
  Edges = 1 edges r=2: [Edge8]
  Placement = pos=(7,0,0) rot=(0,0,1;0rad)
FEATURE [Part::Feature] Face127
  shape: bbox 10 x 16.5 x 2e-07 mm, 1 faces, 0 solids (baked)
FEATURE [Part::Feature] Face128
  shape: bbox 10 x 16.5 x 2e-07 mm, 1 faces, 0 solids (baked)
FEATURE [Part::Revolution] Revolve137  label="plugHousing070"
  Angle = 360
  Axis = (0,1,0)
  Base = (0,0,0)
  FaceMakerClass = Part::FaceMakerBullseye
  Placement = pos=(0,0,36.15) rot=(0,0,1;0rad)
  Solid = false
  Source = -> Face127
  Symmetric = false
FEATURE [Part::Revolution] Revolve140  label="plugHousing073"
  Angle = 360
  Axis = (0,1,0)
  Base = (0,0,0)
  FaceMakerClass = Part::FaceMakerBullseye
  Placement = pos=(0,0,36.15) rot=(0,0,1;0rad)
  Solid = false
  Source = -> Face128
  Symmetric = false
FEATURE [Part::Feature] Face129
  shape: bbox 10 x 16.5 x 2e-07 mm, 1 faces, 0 solids (baked)
FEATURE [Part::Revolution] Revolve138  label="plugHousing071"
  Angle = 360
  Axis = (0,1,0)
  Base = (0,0,0)
  FaceMakerClass = Part::FaceMakerBullseye
  Placement = pos=(0,0,36.15) rot=(0,0,1;0rad)
  Solid = false
  Source = -> Face129
  Symmetric = false
FEATURE [Part::Feature] Face130
  shape: bbox 10 x 16.5 x 2e-07 mm, 1 faces, 0 solids (baked)
FEATURE [Part::Revolution] Revolve139  label="plugHousing072"
  Angle = 360
  Axis = (0,1,0)
  Base = (0,0,0)
  FaceMakerClass = Part::FaceMakerBullseye
  Placement = pos=(0,0,36.15) rot=(0,0,1;0rad)
  Solid = false
  Source = -> Face130
  Symmetric = false
FEATURE [Part::Feature] Face131
  shape: bbox 10 x 16.5 x 2e-07 mm, 1 faces, 0 solids (baked)
FEATURE [Part::Revolution] Revolve135  label="plugHousing068"
  Angle = 360
  Axis = (0,1,0)
  Base = (0,0,0)
  FaceMakerClass = Part::FaceMakerBullseye
  Placement = pos=(0,0,36.15) rot=(0,0,1;0rad)
  Solid = false
  Source = -> Face131
  Symmetric = false
FEATURE [Part::MultiFuse] Fusion112  label="plugHousing078"
  Placement = pos=(0,0,0) rot=(0,0,1;1.5708rad)
  Shapes = -> [Revolve135,Revolve139]
FEATURE [Part::Feature] Face132
  shape: bbox 10 x 16.5 x 2e-07 mm, 1 faces, 0 solids (baked)
FEATURE [Part::Revolution] Revolve141  label="plugHousing074"
  Angle = 360
  Axis = (0,1,0)
  Base = (0,0,0)
  FaceMakerClass = Part::FaceMakerBullseye
  Placement = pos=(0,0,36.15) rot=(0,0,1;0rad)
  Solid = false
  Source = -> Face132
  Symmetric = false
FEATURE [Part::MultiFuse] Fusion110  label="plugHousing076"
  Placement = pos=(0,0,0) rot=(0,0,1;1.5708rad)
  Shapes = -> [Revolve141,Revolve140]
FEATURE [Part::Feature] Face133
  shape: bbox 10 x 16.5 x 2e-07 mm, 1 faces, 0 solids (baked)
FEATURE [Part::Revolution] Revolve136  label="plugHousing069"
  Angle = 360
  Axis = (0,1,0)
  Base = (0,0,0)
  FaceMakerClass = Part::FaceMakerBullseye
  Placement = pos=(0,0,36.15) rot=(0,0,1;0rad)
  Solid = false
  Source = -> Face133
  Symmetric = false
FEATURE [Part::MultiFuse] Fusion106  label="plugHousing064"
  Placement = pos=(0,0,0) rot=(0,0,1;1.5708rad)
  Shapes = -> [Revolve138,Revolve136]
FEATURE [Part::MultiFuse] Fusion108  label="plugHousing066"
  Placement = pos=(0,19,0) rot=(0,0,1;3.14159rad)
  Shapes = -> [Fusion106,Fusion112]
FEATURE [Part::Feature] Face134
  shape: bbox 10 x 16.5 x 2e-07 mm, 1 faces, 0 solids (baked)
FEATURE [Part::Revolution] Revolve142  label="plugHousing075"
  Angle = 360
  Axis = (0,1,0)
  Base = (0,0,0)
  FaceMakerClass = Part::FaceMakerBullseye
  Placement = pos=(0,0,36.15) rot=(0,0,1;0rad)
  Solid = false
  Source = -> Face134
  Symmetric = false
FEATURE [Part::MultiFuse] Fusion107  label="plugHousing065"
  Placement = pos=(0,0,0) rot=(0,0,1;1.5708rad)
  Shapes = -> [Revolve137,Revolve142]
FEATURE [Part::MultiFuse] Fusion111  label="plugHousing077"
  Placement = pos=(0,19,0) rot=(0,0,1;3.14159rad)
  Shapes = -> [Fusion110,Fusion107]
FEATURE [Part::MultiFuse] Fusion109  label="plugHousing067"
  Placement = pos=(131.236,0,-0.15) rot=(0,0,1;0rad)
  Shapes = -> [Fusion108,Fusion111]
FEATURE [Part::MultiFuse] Fusion113  label="plugHousing079"
  Shapes = -> [Fillet043,Fusion109]
FEATURE [Part::Feature] Face135
  shape: bbox 3.5 x 17.8 x 2e-07 mm, 1 faces, 0 solids (baked)
FEATURE [Part::Revolution] Revolve143  label="removeToCreateScrewAndThreadedInsertHole049"
  Angle = 360
  Axis = (0,1,0)
  Base = (0,0,0)
  FaceMakerClass = Part::FaceMakerBullseye
  Placement = pos=(12.5,0,10) rot=(0,0,1;0rad)
  Solid = false
  Source = -> Face135
  Symmetric = false
FEATURE [Part::Feature] Face136
  shape: bbox 3.5 x 17.8 x 2e-07 mm, 1 faces, 0 solids (baked)
FEATURE [Part::Revolution] Revolve144  label="removeToCreateScrewAndThreadedInsertHole050"
  Angle = 360
  Axis = (0,1,0)
  Base = (0,0,0)
  FaceMakerClass = Part::FaceMakerBullseye
  Placement = pos=(12.5,0,62) rot=(0,0,1;0rad)
  Solid = false
  Source = -> Face136
  Symmetric = false
FEATURE [Part::Feature] Face137
  shape: bbox 3.5 x 17.8 x 2e-07 mm, 1 faces, 0 solids (baked)
FEATURE [Part::Revolution] Revolve145  label="removeToCreateScrewAndThreadedInsertHole051"
  Angle = 360
  Axis = (0,1,0)
  Base = (0,0,0)
  FaceMakerClass = Part::FaceMakerBullseye
  Placement = pos=(89.5,0,68.5) rot=(0,0,1;0rad)
  Solid = false
  Source = -> Face137
  Symmetric = false
FEATURE [Part::Feature] Face138
  shape: bbox 3.5 x 17.8 x 2e-07 mm, 1 faces, 0 solids (baked)
FEATURE [Part::Revolution] Revolve146  label="removeToCreateScrewAndThreadedInsertHole052"
  Angle = 360
  Axis = (0,1,0)
  Base = (0,0,0)
  FaceMakerClass = Part::FaceMakerBullseye
  Placement = pos=(89.5,0,3.5) rot=(0,0,1;0rad)
  Solid = false
  Source = -> Face138
  Symmetric = false
FEATURE [Part::Feature] Face139
  shape: bbox 3.5 x 17.8 x 2e-07 mm, 1 faces, 0 solids (baked)
FEATURE [Part::Revolution] Revolve147  label="removeToCreateScrewAndThreadedInsertHole053"
  Angle = 360
  Axis = (0,1,0)
  Base = (0,0,0)
  FaceMakerClass = Part::FaceMakerBullseye
  Placement = pos=(109.5,4.7,3.5) rot=(0,0,1;0rad)
  Solid = false
  Source = -> Face139
  Symmetric = false
FEATURE [Part::Feature] Face140
  shape: bbox 3.5 x 17.8 x 2e-07 mm, 1 faces, 0 solids (baked)
FEATURE [Part::Revolution] Revolve148  label="removeToCreateScrewAndThreadedInsertHole054"
  Angle = 360
  Axis = (0,1,0)
  Base = (0,0,0)
  FaceMakerClass = Part::FaceMakerBullseye
  Placement = pos=(109.5,4.7,68.5) rot=(0,0,1;0rad)
  Solid = false
  Source = -> Face140
  Symmetric = false
FEATURE [Part::MultiFuse] Fusion114  label="removeToCreateScrewAndThreadedInsertHole055"
  Shapes = -> [Revolve148,Revolve147,Revolve146,Revolve145,Revolve144,Revolve143]
FEATURE [Part::Cut] Cut047  label="casePillars004"
  Base = -> Cut037
  Tool = -> Fusion114
FEATURE [Part::Feature] Face141
  shape: bbox 3.5 x 17.8 x 2e-07 mm, 1 faces, 0 solids (baked)
FEATURE [Part::Feature] Face142
  shape: bbox 3.5 x 17.8 x 2e-07 mm, 1 faces, 0 solids (baked)
FEATURE [Part::Feature] Face143
  shape: bbox 3.5 x 17.8 x 2e-07 mm, 1 faces, 0 solids (baked)
FEATURE [Part::Revolution] Revolve149  label="removeToCreateScrewAndThreadedInsertHole057"
  Angle = 360
  Axis = (0,1,0)
  Base = (0,0,0)
  FaceMakerClass = Part::FaceMakerBullseye
  Placement = pos=(12.5,0,10) rot=(0,0,1;0rad)
  Solid = false
  Source = -> Face141
  Symmetric = false
FEATURE [Part::Feature] Face144
  shape: bbox 3.5 x 17.8 x 2e-07 mm, 1 faces, 0 solids (baked)
FEATURE [Part::Feature] Face145
  shape: bbox 3.5 x 17.8 x 2e-07 mm, 1 faces, 0 solids (baked)
FEATURE [Part::Feature] Face146
  shape: bbox 3.5 x 17.8 x 2e-07 mm, 1 faces, 0 solids (baked)
FEATURE [Part::Revolution] Revolve150  label="removeToCreateScrewAndThreadedInsertHole058"
  Angle = 360
  Axis = (0,1,0)
  Base = (0,0,0)
  FaceMakerClass = Part::FaceMakerBullseye
  Placement = pos=(12.5,0,62) rot=(0,0,1;0rad)
  Solid = false
  Source = -> Face146
  Symmetric = false
FEATURE [Part::Revolution] Revolve151  label="removeToCreateScrewAndThreadedInsertHole059"
  Angle = 360
  Axis = (0,1,0)
  Base = (0,0,0)
  FaceMakerClass = Part::FaceMakerBullseye
  Placement = pos=(89.5,0,68.5) rot=(0,0,1;0rad)
  Solid = false
  Source = -> Face143
  Symmetric = false
FEATURE [Part::Revolution] Revolve152  label="removeToCreateScrewAndThreadedInsertHole060"
  Angle = 360
  Axis = (0,1,0)
  Base = (0,0,0)
  FaceMakerClass = Part::FaceMakerBullseye
  Placement = pos=(89.5,0,3.5) rot=(0,0,1;0rad)
  Solid = false
  Source = -> Face142
  Symmetric = false
FEATURE [Part::Revolution] Revolve153  label="removeToCreateScrewAndThreadedInsertHole061"
  Angle = 360
  Axis = (0,1,0)
  Base = (0,0,0)
  FaceMakerClass = Part::FaceMakerBullseye
  Placement = pos=(109.5,4.7,3.5) rot=(0,0,1;0rad)
  Solid = false
  Source = -> Face145
  Symmetric = false
FEATURE [Part::Revolution] Revolve154  label="removeToCreateScrewAndThreadedInsertHole062"
  Angle = 360
  Axis = (0,1,0)
  Base = (0,0,0)
  FaceMakerClass = Part::FaceMakerBullseye
  Placement = pos=(109.5,4.7,68.5) rot=(0,0,1;0rad)
  Solid = false
  Source = -> Face144
  Symmetric = false
FEATURE [Part::MultiFuse] Fusion115  label="removeToCreateScrewAndThreadedInsertHole056"
  Shapes = -> [Revolve154,Revolve153,Revolve152,Revolve151,Revolve150,Revolve149]
FEATURE [Part::Feature] Face147
  shape: bbox 9.8 x 26.5 x 2e-07 mm, 1 faces, 0 solids (baked)
FEATURE [Part::Revolution] Revolve155
  Angle = 360
  Axis = (0,1,0)
  Base = (0,0,0)
  FaceMakerClass = Part::FaceMakerBullseye
  Placement = pos=(0,0,0) rot=(0,0,1;1.5708rad)
  Solid = false
  Source = -> Face147
  Symmetric = false
FEATURE [Part::Feature] Face148
  shape: bbox 9.8 x 26.5 x 2e-07 mm, 1 faces, 0 solids (baked)
FEATURE [Part::Revolution] Revolve156
  Angle = 360
  Axis = (0,1,0)
  Base = (0,0,0)
  FaceMakerClass = Part::FaceMakerBullseye
  Placement = pos=(0,0,0) rot=(0,0,1;1.5708rad)
  Solid = false
  Source = -> Face148
  Symmetric = false
FEATURE [Part::MultiFuse] Fusion116
  Placement = pos=(-18,19,36) rot=(0,0,1;0rad)
  Shapes = -> [Revolve156,Revolve155]
FEATURE [Part::Box] Box029  label="Cube016"
  AttacherType = Attacher::AttachEngine3D
  Height = 28
  Length = 3
  Placement = pos=(110.7,19,22) rot=(0,0,1;0rad)
  Width = 15.7
FEATURE [Part::Cylinder] Cylinder046
  Angle = 360
  AttacherType = Attacher::AttachEngine3D
  Height = 10
  Placement = pos=(0,0,36.15) rot=(0,0,1;0rad)
  Radius = 4
FEATURE [Part::Cylinder] Cylinder047
  Angle = 360
  AttacherType = Attacher::AttachEngine3D
  Height = 20
  Placement = pos=(0,0,36.15) rot=(0,0,1;0rad)
  Radius = 10.3
FEATURE [Part::MultiFuse] Fusion117  label="removeToCreteHoleForPlugHousing041"
  Placement = pos=(70,19,36) rot=(0,1,0;1.5708rad)
  Shapes = -> [Cylinder047,Cylinder046]
FEATURE [Part::Cut] Cut049  label="plugHousingTab004"
  Base = -> Box029
  Placement = pos=(-107.4,-14,0) rot=(0,0,1;0rad)
  Tool = -> Fusion117
FEATURE [Part::Box] Box030  label="Cube017"
  AttacherType = Attacher::AttachEngine3D
  Height = 28
  Length = 3
  Placement = pos=(110.7,19,22) rot=(0,0,1;0rad)
  Width = 15.7
FEATURE [Part::Cylinder] Cylinder048
  Angle = 360
  AttacherType = Attacher::AttachEngine3D
  Height = 10
  Placement = pos=(0,0,36.15) rot=(0,0,1;0rad)
  Radius = 4
FEATURE [Part::Cylinder] Cylinder049
  Angle = 360
  AttacherType = Attacher::AttachEngine3D
  Height = 20
  Placement = pos=(0,0,36.15) rot=(0,0,1;0rad)
  Radius = 10.3
FEATURE [Part::MultiFuse] Fusion118  label="removeToCreteHoleForPlugHousing042"
  Placement = pos=(70,19,36) rot=(0,1,0;1.5708rad)
  Shapes = -> [Cylinder049,Cylinder048]
FEATURE [Part::Cut] Cut050  label="plugHousingTab005"
  Base = -> Box030
  Placement = pos=(-107.4,-14,0) rot=(0,0,1;0rad)
  Tool = -> Fusion118
FEATURE [Part::MultiFuse] Fusion119
  Placement = pos=(9.6,23,0) rot=(0,0,1;3.14159rad)
  Shapes = -> [Cut049,Cut050]
FEATURE [Part::Box] Box031  label="Cube018"
  AttacherType = Attacher::AttachEngine3D
  Height = 10
  Length = 3
  Placement = pos=(3.3,4,12) rot=(0,0,1;0rad)
  Width = 10
FEATURE [Part::Fillet] Fillet044
  Base = -> Box031
  Edges = 1 edges r=2: [Edge11]
FEATURE [Part::Box] Box032  label="Cube019"
  AttacherType = Attacher::AttachEngine3D
  Height = 10
  Length = 3
  Placement = pos=(3.3,4,50) rot=(0,0,1;0rad)
  Width = 10
FEATURE [Part::Fillet] Fillet045
  Base = -> Box032
  Edges = 1 edges r=2: [Edge12]
FEATURE [Part::Box] Box033  label="Cube020"
  AttacherType = Attacher::AttachEngine3D
  Height = 28
  Length = 4
  Placement = pos=(5,0,22) rot=(0,0,1;0rad)
  Width = 10
FEATURE [Part::Fillet] Fillet046
  Base = -> Box033
  Edges = 1 edges r=1: [Edge7]
FEATURE [Part::Fillet] Fillet047
  Base = -> Fillet046
  Edges = 1 edges r=2: [Edge5]
FEATURE [Part::Fillet] Fillet048
  Base = -> Fillet047
  Edges = 1 edges r=2: [Edge2]
FEATURE [Part::Cylinder] Cylinder050
  Angle = 360
  AttacherType = Attacher::AttachEngine3D
  Height = 20
  Placement = pos=(0,0,36.15) rot=(0,0,1;0rad)
  Radius = 8.2
FEATURE [Part::Cylinder] Cylinder051
  Angle = 360
  AttacherType = Attacher::AttachEngine3D
  Height = 10
  Placement = pos=(0,0,36.15) rot=(0,0,1;0rad)
  Radius = 4
FEATURE [Part::MultiFuse] Fusion120  label="removeToCreteHoleForPlugHousing043"
  Placement = pos=(-42,19,36) rot=(0,1,0;1.5708rad)
  Shapes = -> [Cylinder050,Cylinder051]
FEATURE [Sketcher::SketchObject] Sketch067  label="topSketch018"
  FullyConstrained = true
  sketch-geometry (4):
    g0: LineSegment StartX=16.8446 StartY=31.512 StartZ=0 EndX=16.3251 EndY=34.4666 EndZ=0
    g1: ArcOfCircle CenterX=19 CenterY=19.2524 CenterZ=0 NormalX=0 NormalY=0 NormalZ=1 AngleXU=0 Radius=15.4476 StartAngle=1.74483 EndAngle=2.72717
    g2: ArcOfCircle CenterX=19 CenterY=19.2524 CenterZ=0 NormalX=0 NormalY=0 NormalZ=1 AngleXU=0 Radius=12.4476 StartAngle=1.74483 EndAngle=2.73189
    g3: LineSegment StartX=4.86004 StartY=25.4725 StartZ=0 EndX=7.58253 EndY=24.2107 EndZ=0
  constraints (7):
    c: Block(g0)
    c: Coincident(g1,g0)
    c: Coincident(g2,g0)
    c: Coincident(g3,g1)
    c: Coincident(g3,g2)
    c: Block(g1)
    c: Block(g2)
FEATURE [Part::Extrusion] Extrude058
  Base = -> Sketch067
  Dir = (0,0,1)
  DirMode = 2
  FaceMakerClass = Part::FaceMakerBullseye
  LengthFwd = 10
  LengthRev = 0
  Placement = pos=(0,0,31) rot=(0,0,1;0rad)
  Solid = true
  Symmetric = false
FEATURE [Part::Cut] Cut051
  Base = -> Extrude058
  Tool = -> Fusion120
FEATURE [Part::Fillet] Fillet049
  Base = -> Cut051
  Edges = 1 edges r=2: [Edge1]
FEATURE [Part::Fillet] Fillet050
  Base = -> Fillet049
  Edges = 1 edges r=2.5: [Edge1]
FEATURE [Part::Fillet] Fillet051
  Base = -> Fillet050
  Edges = 1 edges r=2.5: [Edge2]
FEATURE [Part::MultiFuse] Fusion121  label="wireHolder003"
  Shapes = -> [Fusion116,Fillet051]
FEATURE [Part::MultiFuse] Fusion122
  Shapes = -> [Fillet045,Fusion121]
FEATURE [Part::MultiFuse] Fusion123  label="wireHolder004"
  Shapes = -> [Fusion122,Fillet048]
FEATURE [Part::MultiFuse] Fusion124  label="wireHolder005"
  Shapes = -> [Fillet044,Fusion119,Fusion123]
FEATURE [Sketcher::SketchObject] Sketch068  label="topSketch019"
  FullyConstrained = true
  sketch-geometry (6):
    g0: LineSegment StartX=19 StartY=38 StartZ=0 EndX=117 EndY=38 EndZ=0
    g1: ArcOfCircle CenterX=19 CenterY=19 CenterZ=0 NormalX=0 NormalY=0 NormalZ=1 AngleXU=0 Radius=19 StartAngle=1.5708 EndAngle=3.14159
    g2: LineSegment StartX=117 StartY=38 StartZ=0 EndX=117 EndY=19 EndZ=0
    g3: LineSegment StartX=98 StartY=1.0161e-12 StartZ=0 EndX=5.22862e-06 EndY=1.0161e-12 EndZ=0
    g4: LineSegment StartX=5.22862e-06 StartY=19 StartZ=0 EndX=5.22862e-06 EndY=1.0161e-12 EndZ=0
    g5: ArcOfCircle CenterX=98 CenterY=19 CenterZ=0 NormalX=0 NormalY=0 NormalZ=1 AngleXU=0 Radius=19 StartAngle=4.71239 EndAngle=6.28319
  constraints (16):
    c: Horizontal(g0)
    c: Distance(g0) = 98
    c: Coincident(g1,g0)
    c: Block(g1)
    c: Coincident(g2,g0)
    c: Vertical(g2)
    c: Distance(g2) = 19
    c: Horizontal(g3)
    c: Coincident(g4,g1)
    c: Vertical(g4)
    c: Coincident(g3,g4)
    c: Block(g3)
    c: Coincident(g5,g2)
    c: Coincident(g5,g3)
    c: Block(g0)
    c: Block(g5)
FEATURE [Part::Extrusion] Extrude059  label="sideA002"
  Base = -> Sketch068
  Dir = (0,0,1)
  DirMode = 2
  FaceMakerClass = Part::FaceMakerBullseye
  LengthFwd = 3
  LengthRev = 0
  Placement = pos=(0,0,-2.7) rot=(0,0,1;0rad)
  Solid = true
  Symmetric = false
FEATURE [Sketcher::SketchObject] Sketch069  label="topSketch020"
  FullyConstrained = true
  sketch-geometry (6):
    g0: LineSegment StartX=19 StartY=38 StartZ=0 EndX=117 EndY=38 EndZ=0
    g1: ArcOfCircle CenterX=19 CenterY=19 CenterZ=0 NormalX=0 NormalY=0 NormalZ=1 AngleXU=0 Radius=19 StartAngle=1.5708 EndAngle=3.14159
    g2: LineSegment StartX=117 StartY=38 StartZ=0 EndX=117 EndY=19 EndZ=0
    g3: LineSegment StartX=98 StartY=1.0161e-12 StartZ=0 EndX=5.22862e-06 EndY=1.0161e-12 EndZ=0
    g4: LineSegment StartX=5.22862e-06 StartY=19 StartZ=0 EndX=5.22862e-06 EndY=1.0161e-12 EndZ=0
    g5: ArcOfCircle CenterX=98 CenterY=19 CenterZ=0 NormalX=0 NormalY=0 NormalZ=1 AngleXU=0 Radius=19 StartAngle=4.71239 EndAngle=6.28319
  constraints (16):
    c: Horizontal(g0)
    c: Distance(g0) = 98
    c: Coincident(g1,g0)
    c: Block(g1)
    c: Coincident(g2,g0)
    c: Vertical(g2)
    c: Distance(g2) = 19
    c: Horizontal(g3)
    c: Coincident(g4,g1)
    c: Vertical(g4)
    c: Coincident(g3,g4)
    c: Block(g3)
    c: Coincident(g5,g2)
    c: Coincident(g5,g3)
    c: Block(g0)
    c: Block(g5)
FEATURE [Part::Extrusion] Extrude060  label="sideB002"
  Base = -> Sketch069
  Dir = (0,0,1)
  DirMode = 2
  FaceMakerClass = Part::FaceMakerBullseye
  LengthFwd = 3
  LengthRev = 0
  Placement = pos=(0,0,71.7) rot=(0,0,1;0rad)
  Solid = true
  Symmetric = false
FEATURE [Part::MultiFuse] Fusion127  label="removeFromBottom001"
  Placement = pos=(2,0,0) rot=(0,0,1;0rad)
  Shapes = -> [Extrude059,Extrude060]
FEATURE [Part::Cylinder] Cylinder052
  Angle = 360
  AttacherType = Attacher::AttachEngine3D
  Height = 20
  Placement = pos=(0,0,36.15) rot=(0,0,1;0rad)
  Radius = 14
FEATURE [Part::Cylinder] Cylinder053
  Angle = 360
  AttacherType = Attacher::AttachEngine3D
  Height = 10
  Placement = pos=(0,0,36.15) rot=(0,0,1;0rad)
  Radius = 4
FEATURE [Part::MultiFuse] Fusion128  label="removeToCreteHoleForPlugHousing044"
  Placement = pos=(70,19,36) rot=(0,1,0;1.5708rad)
  Shapes = -> [Cylinder052,Cylinder053]
FEATURE [Part::Cut] Cut052  label="bottom011"
  Base = -> Extrude043
  Tool = -> Fusion128
FEATURE [Part::Cut] Cut054  label="bottom012"
  Base = -> Cut052
  Tool = -> Fusion115
FEATURE [Sketcher::SketchObject] Sketch070
  FullyConstrained = true
  Placement = pos=(117,19,0) rot=(0.57735,0.57735,0.57735;2.0944rad)
  sketch-geometry (48):
    g0: LineSegment StartX=-49.19 StartY=69.25 StartZ=0 EndX=-49.19 EndY=66.25 EndZ=0
    g1: LineSegment StartX=-49.19 StartY=63.5 StartZ=0 EndX=-49.19 EndY=60.5 EndZ=0
    g2: LineSegment StartX=-49.19 StartY=57.75 StartZ=0 EndX=-49.19 EndY=54.75 EndZ=0
    g3: LineSegment StartX=-49.19 StartY=52 StartZ=0 EndX=-49.19 EndY=49 EndZ=0
    g4: LineSegment StartX=-49.19 StartY=46.25 StartZ=0 EndX=-49.19 EndY=43.25 EndZ=0
    g5: LineSegment StartX=-49.19 StartY=40.5 StartZ=0 EndX=-49.19 EndY=37.5 EndZ=0
    g6: LineSegment StartX=-49.19 StartY=34.5 StartZ=0 EndX=-49.19 EndY=31.5 EndZ=0
    g7: LineSegment StartX=-49.19 StartY=28.75 StartZ=0 EndX=-49.19 EndY=25.75 EndZ=0
    g8: LineSegment StartX=-49.19 StartY=23 StartZ=0 EndX=-49.19 EndY=20 EndZ=0
    g9: LineSegment StartX=-49.19 StartY=17.25 StartZ=0 EndX=-49.19 EndY=14.25 EndZ=0
    g10: LineSegment StartX=-49.19 StartY=11.5 StartZ=0 EndX=-49.19 EndY=8.5 EndZ=0
    g11: LineSegment StartX=-49.19 StartY=5.75 StartZ=0 EndX=-49.19 EndY=2.75 EndZ=0
    g12: ArcOfCircle CenterX=-1.5 CenterY=67.75 CenterZ=0 NormalX=0 NormalY=0 NormalZ=1 AngleXU=0 Radius=1.5 StartAngle=4.71239 EndAngle=7.85398
    g13: ArcOfCircle CenterX=-1.5 CenterY=62 CenterZ=0 NormalX=0 NormalY=0 NormalZ=1 AngleXU=0 Radius=1.5 StartAngle=4.71239 EndAngle=7.85398
    g14: ArcOfCircle CenterX=-1.5 CenterY=56.25 CenterZ=0 NormalX=0 NormalY=0 NormalZ=1 AngleXU=0 Radius=1.5 StartAngle=4.71239 EndAngle=7.85398
    g15: ArcOfCircle CenterX=-11.49 CenterY=50.5 CenterZ=0 NormalX=0 NormalY=0 NormalZ=1 AngleXU=0 Radius=1.5 StartAngle=4.71239 EndAngle=7.85398
    g16: ArcOfCircle CenterX=-16.28 CenterY=44.75 CenterZ=0 NormalX=0 NormalY=0 NormalZ=1 AngleXU=0 Radius=1.5 StartAngle=4.71239 EndAngle=7.85398
    g17: ArcOfCircle CenterX=-18.2337 CenterY=39 CenterZ=0 NormalX=0 NormalY=0 NormalZ=1 AngleXU=0 Radius=1.5 StartAngle=4.71485 EndAngle=7.85398
    g18: ArcOfCircle CenterX=-16.2837 CenterY=27.25 CenterZ=0 NormalX=0 NormalY=0 NormalZ=1 AngleXU=0 Radius=1.5 StartAngle=4.71485 EndAngle=7.85398
    g19: ArcOfCircle CenterX=-18.2337 CenterY=33 CenterZ=0 NormalX=0 NormalY=0 NormalZ=1 AngleXU=0 Radius=1.5 StartAngle=4.71485 EndAngle=7.85398
    g20: ArcOfCircle CenterX=-11.49 CenterY=21.5 CenterZ=0 NormalX=0 NormalY=0 NormalZ=1 AngleXU=0 Radius=1.5 StartAngle=4.71239 EndAngle=7.85398
    g21: ArcOfCircle CenterX=-1.5 CenterY=4.25 CenterZ=0 NormalX=0 NormalY=0 NormalZ=1 AngleXU=0 Radius=1.5 StartAngle=4.71239 EndAngle=7.85398
    g22: ArcOfCircle CenterX=-1.5 CenterY=10 CenterZ=0 NormalX=0 NormalY=0 NormalZ=1 AngleXU=0 Radius=1.5 StartAngle=4.71239 EndAngle=7.85398
    g23: ArcOfCircle CenterX=-1.5 CenterY=15.75 CenterZ=0 NormalX=0 NormalY=0 NormalZ=1 AngleXU=0 Radius=1.5 StartAngle=4.71239 EndAngle=7.85398
    g24: LineSegment StartX=-49.19 StartY=69.25 StartZ=0 EndX=-1.5 EndY=69.25 EndZ=0
    g25: LineSegment StartX=-49.19 StartY=66.25 StartZ=0 EndX=-1.5 EndY=66.25 EndZ=0
    g26: LineSegment StartX=-49.19 StartY=63.5 StartZ=0 EndX=-1.5 EndY=63.5 EndZ=0
    g27: LineSegment StartX=-49.19 StartY=60.5 StartZ=0 EndX=-1.5 EndY=60.5 EndZ=0
    g28: LineSegment StartX=-49.19 StartY=57.75 StartZ=0 EndX=-1.5 EndY=57.75 EndZ=0
    g29: LineSegment StartX=-49.19 StartY=54.75 StartZ=0 EndX=-1.5 EndY=54.75 EndZ=0
    g30: LineSegment StartX=-49.19 StartY=52 StartZ=0 EndX=-11.49 EndY=52 EndZ=0
    g31: LineSegment StartX=-49.19 StartY=49 StartZ=0 EndX=-11.49 EndY=49 EndZ=0
    g32: LineSegment StartX=-49.19 StartY=46.25 StartZ=0 EndX=-16.28 EndY=46.25 EndZ=0
    g33: LineSegment StartX=-49.19 StartY=43.25 StartZ=0 EndX=-16.28 EndY=43.25 EndZ=0
    g34: LineSegment StartX=-49.19 StartY=40.5 StartZ=0 EndX=-18.2337 EndY=40.5 EndZ=0
    g35: LineSegment StartX=-49.19 StartY=37.5 StartZ=0 EndX=-18.23 EndY=37.5 EndZ=0
    g36: LineSegment StartX=-49.19 StartY=34.5 StartZ=0 EndX=-18.2337 EndY=34.5 EndZ=0
    g37: LineSegment StartX=-49.19 StartY=31.5 StartZ=0 EndX=-18.23 EndY=31.5 EndZ=0
    g38: LineSegment StartX=-49.19 StartY=28.75 StartZ=0 EndX=-16.2837 EndY=28.75 EndZ=0
    g39: LineSegment StartX=-49.19 StartY=25.75 StartZ=0 EndX=-16.28 EndY=25.75 EndZ=0
    g40: LineSegment StartX=-49.19 StartY=23 StartZ=0 EndX=-11.49 EndY=23 EndZ=0
    g41: LineSegment StartX=-49.19 StartY=20 StartZ=0 EndX=-11.49 EndY=20 EndZ=0
    g42: LineSegment StartX=-49.19 StartY=17.25 StartZ=0 EndX=-1.5 EndY=17.25 EndZ=0
    g43: LineSegment StartX=-49.19 StartY=14.25 StartZ=0 EndX=-1.5 EndY=14.25 EndZ=0
    g44: LineSegment StartX=-49.19 StartY=11.5 StartZ=0 EndX=-1.5 EndY=11.5 EndZ=0
    g45: LineSegment StartX=-49.19 StartY=8.5 StartZ=0 EndX=-1.5 EndY=8.5 EndZ=0
    g46: LineSegment StartX=-49.19 StartY=5.75 StartZ=0 EndX=-1.5 EndY=5.75 EndZ=0
    g47: LineSegment StartX=-49.19 StartY=2.75 StartZ=0 EndX=-1.5 EndY=2.75 EndZ=0
  constraints (120):
    c: Vertical(g0)
    c: Distance(g0) = 3
    c: Block(g0)
    c: Vertical(g1)
    c: Distance(g1) = 3
    c: Vertical(g2)
    c: Equal(g0,g2) = 3
    c: Block(g2)
    c: Vertical(g3)
    c: Equal(g1,g3) = 3
    c: Vertical(g4)
    c: Equal(g0,g4) = 3
    c: Block(g4)
    c: Vertical(g5)
    c: Equal(g1,g5) = 3
    c: Vertical(g6)
    c: Equal(g0,g6) = 3
    c: Block(g6)
    c: Vertical(g7)
    c: Equal(g1,g7) = 3
    c: Vertical(g8)
    c: Equal(g0,g8) = 3
    c: Block(g8)
    c: Vertical(g9)
    c: Equal(g1,g9) = 3
    c: Vertical(g10)
    c: Equal(g0,g10) = 3
    c: Block(g10)
    c: Vertical(g11)
    c: Equal(g1,g11) = 3
    c: Block(g12)
    c: Block(g13)
    c: Block(g14)
    c: Block(g15)
    c: Block(g16)
    c: Block(g17)
    c: Block(g18)
    c: Block(g19)
    c: Block(g20)
    c: Block(g21)
    c: Block(g22)
    c: Block(g23)
    c: Block(g11)
    c: Block(g9)
    c: Block(g7)
    c: Block(g5)
    c: Block(g3)
    c: Block(g1)
    c: Coincident(g24,g0)
    c: Coincident(g24,g12)
    c: Horizontal(g24)
    c: Coincident(g25,g0)
    c: Coincident(g25,g12)
    c: Horizontal(g25)
    c: Coincident(g26,g1)
    c: Coincident(g26,g13)
    c: Horizontal(g26)
    c: Coincident(g27,g1)
    c: Coincident(g27,g13)
    c: Horizontal(g27)
    c: Coincident(g28,g2)
    c: Coincident(g28,g14)
    c: Horizontal(g28)
    c: Coincident(g29,g2)
    c: Coincident(g29,g14)
    c: Horizontal(g29)
    c: Coincident(g30,g3)
    c: Coincident(g30,g15)
    c: Horizontal(g30)
    c: Coincident(g31,g3)
    c: Coincident(g31,g15)
    c: Horizontal(g31)
    c: Coincident(g32,g4)
    c: Coincident(g32,g16)
    c: Horizontal(g32)
    c: Coincident(g33,g4)
    c: Coincident(g33,g16)
    c: Horizontal(g33)
    c: Coincident(g34,g5)
    c: Coincident(g34,g17)
    c: Horizontal(g34)
    c: Coincident(g35,g5)
    c: Coincident(g35,g17)
    c: Horizontal(g35)
    c: Coincident(g36,g6)
    c: Coincident(g36,g19)
    c: Horizontal(g36)
    c: Coincident(g37,g6)
    c: Coincident(g37,g19)
    c: Horizontal(g37)
    c: Coincident(g38,g7)
    c: Coincident(g38,g18)
    c: Horizontal(g38)
    c: Coincident(g39,g7)
    c: Coincident(g39,g18)
    c: Horizontal(g39)
    c: Coincident(g40,g8)
    c: Coincident(g40,g20)
    c: Horizontal(g40)
    c: Coincident(g41,g8)
    c: Coincident(g41,g20)
    c: Horizontal(g41)
    c: Coincident(g42,g9)
    c: Coincident(g42,g23)
    c: Horizontal(g42)
    c: Coincident(g43,g9)
    c: Coincident(g43,g23)
    c: Horizontal(g43)
    c: Coincident(g44,g10)
    c: Coincident(g44,g22)
    c: Horizontal(g44)
    c: Coincident(g45,g10)
    c: Coincident(g45,g22)
    c: Horizontal(g45)
    c: Coincident(g46,g11)
    c: Coincident(g46,g21)
    c: Horizontal(g46)
    c: Coincident(g47,g11)
    c: Coincident(g47,g21)
    c: Horizontal(g47)
FEATURE [Part::Extrusion] Extrude061
  Base = -> Sketch070
  Dir = (1,0,0)
  DirMode = 2
  FaceMakerClass = Part::FaceMakerBullseye
  LengthFwd = 23
  LengthRev = 0
  Placement = pos=(-19,0,0) rot=(0,0,1;0rad)
  Solid = true
  Symmetric = false
FEATURE [Part::Fillet] Fillet052  label="removeToCreateVentalationHoles002"
  Base = -> Extrude061
  Edges = <same value as first occurrence — deduplicated (x6 in doc)>
  Placement = pos=(7,0.02,0) rot=(0,0,1;0rad)
FEATURE [Part::MultiFuse] Fusion130  label="bottom013"
  Shapes = -> [Cut054,Cut034]
FEATURE [Part::Cut] Cut055
  Base = -> Fusion130
  Tool = -> Fillet052
FEATURE [Part::Cylinder] Cylinder054
  Angle = 360
  AttacherType = Attacher::AttachEngine3D
  Height = 20
  Placement = pos=(0,0,36.15) rot=(0,0,1;0rad)
  Radius = 4
FEATURE [Sketcher::SketchObject] Sketch071  label="bottomSketch002"
  FullyConstrained = true
  sketch-geometry (32):
    g0: LineSegment StartX=3.3 StartY=-6.03275e-07 StartZ=0 EndX=98 EndY=-6.03275e-07 EndZ=0
    g1: ArcOfCircle CenterX=98 CenterY=19 CenterZ=0 NormalX=0 NormalY=0 NormalZ=1 AngleXU=0 Radius=19 StartAngle=4.71239 EndAngle=5.71103
    g2: LineSegment StartX=6.3 StartY=8 StartZ=0 EndX=3.3 EndY=8 EndZ=0
    g3: LineSegment StartX=3.3 StartY=8 StartZ=0 EndX=3.3 EndY=-6.03275e-07 EndZ=0
    g4: ArcOfCircle CenterX=8.3 CenterY=5 CenterZ=0 NormalX=0 NormalY=0 NormalZ=1 AngleXU=0 Radius=2 StartAngle=3.14159 EndAngle=4.71239
    g5: LineSegment StartX=6.3 StartY=8 StartZ=0 EndX=6.3 EndY=5 EndZ=0
    g6: ArcOfCircle CenterX=98 CenterY=19 CenterZ=0 NormalX=0 NormalY=0 NormalZ=1 AngleXU=0 Radius=12.7 StartAngle=4.71239 EndAngle=6.28319
    g7: LineSegment StartX=94.7 StartY=3 StartZ=0 EndX=8.3 EndY=3 EndZ=0
    g8-g12: Circle x5 (B-spline internal-alignment scaffolding for g13; pole/knot coordinates omitted)
    g13: BSplineCurve PolesCount=5 KnotsCount=3 Degree=3 IsPeriodic=0
    g14: GeomPoint X=98 Y=6.3 Z=0
    g15: GeomPoint X=96.3938 Y=4.71946 Z=0
    g16: GeomPoint X=94.7 Y=3 Z=0
    g17-g23: Circle x7 (B-spline internal-alignment scaffolding for g24; pole/knot coordinates omitted)
    g24: BSplineCurve PolesCount=7 KnotsCount=5 Degree=3 IsPeriodic=0
    g25-g29: GeomPoint x5 (B-spline internal-alignment scaffolding for g24; pole/knot coordinates omitted)
    g30: ArcOfCircle CenterX=98 CenterY=19 CenterZ=0 NormalX=0 NormalY=0 NormalZ=1 AngleXU=0 Radius=15.7 StartAngle=5.81226 EndAngle=6.28319
    g31: LineSegment StartX=110.7 StartY=19 StartZ=0 EndX=113.7 EndY=19 EndZ=0
  constraints (41):
    c: Horizontal(g0)
    c: Coincident(g1,g0)
    c: Block(g1)
    c: Horizontal(g2)
    c: Distance(g2) = 3
    c: Coincident(g3,g2)
    c: Vertical(g3)
    c: Coincident(g3,g0)
    c: Block(g4)
    c: Block(g2)
    c: Coincident(g5,g2)
    c: Coincident(g5,g4)
    c: Vertical(g5)
    c: Coincident(g6,g1)
    c: Block(g6)
    c: Coincident(g7,g4)
    c: Horizontal(g7)
    c: Block(g0)
    c: Block(g7)
    c: Block(g3)
    c: Coincident(g13,g6)
    c: Weight(g8) = 1
    c: Equal(g8, g9-g12) x4
    c: Coincident(g13,g7)
    c: InternalAlignment(g8-g12 -> g13) x5
    c: InternalAlignment(g14,g13)
    c: InternalAlignment(g15,g13)
    c: InternalAlignment(g16,g13)
    c: Block(g13)
    c: Weight(g17) = 1
    c: Equal(g17, g18-g23) x6
    c: Coincident(g24,g1)
    c: InternalAlignment(g17-g23 -> g24) x7
    c: InternalAlignment(g25-g29 -> g24) x5
    c: Block(g24)
    c: Coincident(g30,g24)
    c: Coincident(g31,g6)
    c: Coincident(g31,g30)
    c: Horizontal(g31)
    c: Block(g31)
    c: Block(g30)
FEATURE [Part::Extrusion] Extrude062  label="bottom014"
  Base = -> Sketch071
  Dir = (0,0,1)
  DirMode = 2
  FaceMakerClass = Part::FaceMakerBullseye
  LengthFwd = 71.4
  LengthRev = 0
  Placement = pos=(0,0,0.3) rot=(0,0,1;0rad)
  Solid = true
  Symmetric = false
FEATURE [Part::Fillet] Fillet054
  Base = -> Extrude062
  Edges = 1 edges r=2.4: [Edge17]
FEATURE [Part::Fillet] Fillet055  label="bottom015"
  Base = -> Fillet054
  Edges = 1 edges r=2.4: [Edge36]
FEATURE [Part::Cylinder] Cylinder055
  Angle = 360
  AttacherType = Attacher::AttachEngine3D
  Height = 10
  Placement = pos=(0,0,36.15) rot=(0,0,1;0rad)
  Radius = 4
FEATURE [Part::MultiFuse] Fusion131  label="removeToCreateHoleForPlugHousing002"
  Placement = pos=(70,19,36.15) rot=(0,1,0;1.5708rad)
  Shapes = -> [Cylinder054,Cylinder055]
FEATURE [Part::Cut] Cut056  label="Bottom001"
  Base = -> Fillet055
  Placement = pos=(9,0,0) rot=(0,0,1;0rad)
  Tool = -> Fusion131
FEATURE [Part::Cut] Cut057
  Base = -> Cut055
  Tool = -> Cut056
FEATURE [Sketcher::SketchObject] Sketch072  label="topSketch021"
  FullyConstrained = true
  sketch-geometry (4):
    g0: ArcOfCircle CenterX=105 CenterY=19 CenterZ=0 NormalX=0 NormalY=0 NormalZ=1 AngleXU=0 Radius=20.6155 StartAngle=5.54125 EndAngle=6.28319
    g1: ArcOfCircle CenterX=105 CenterY=19 CenterZ=0 NormalX=0 NormalY=0 NormalZ=1 AngleXU=0 Radius=13 StartAngle=5.54125 EndAngle=6.28319
    g2: LineSegment StartX=118 StartY=19 StartZ=0 EndX=125.616 EndY=19 EndZ=0
    g3: LineSegment StartX=114.583 StartY=10.2157 StartZ=0 EndX=120.197 EndY=5.06982 EndZ=0
  constraints (7):
    c: Block(g0)
    c: Block(g1)
    c: Coincident(g2,g1)
    c: Coincident(g2,g0)
    c: Horizontal(g2)
    c: Coincident(g3,g1)
    c: Coincident(g3,g0)
FEATURE [Part::Extrusion] Extrude063  label="bottomPlugHousingBit003"
  Base = -> Sketch072
  Dir = (0,0,1)
  DirMode = 2
  FaceMakerClass = Part::FaceMakerBullseye
  LengthFwd = 72
  LengthRev = 0
  Solid = true
  Symmetric = false
FEATURE [Part::Cylinder] Cylinder056
  Angle = 360
  AttacherType = Attacher::AttachEngine3D
  Height = 20
  Placement = pos=(0,0,36.15) rot=(0,0,1;0rad)
  Radius = 14.3
FEATURE [Part::Cylinder] Cylinder057
  Angle = 360
  AttacherType = Attacher::AttachEngine3D
  Height = 10
  Placement = pos=(0,0,36.15) rot=(0,0,1;0rad)
  Radius = 4
FEATURE [Part::Box] Box034  label="removeToCreteHoleForPlugHousing047"
  AttacherType = Attacher::AttachEngine3D
  Height = 28.6
  Length = 20
  Placement = pos=(106.15,0,21.7) rot=(0,0,1;0rad)
  Width = 19
FEATURE [Part::Cylinder] Cylinder058
  Angle = 360
  AttacherType = Attacher::AttachEngine3D
  Height = 20
  Placement = pos=(0,0,36.15) rot=(0,0,1;0rad)
  Radius = 14.3
FEATURE [Part::Cylinder] Cylinder059
  Angle = 360
  AttacherType = Attacher::AttachEngine3D
  Height = 10
  Placement = pos=(0,0,36.15) rot=(0,0,1;0rad)
  Radius = 4
FEATURE [Part::MultiFuse] Fusion134  label="removeToCreteHoleForPlugHousing046"
  Placement = pos=(70,19,36) rot=(0,1,0;1.5708rad)
  Shapes = -> [Cylinder058,Cylinder059]
FEATURE [Part::Cylinder] Cylinder060
  Angle = 360
  AttacherType = Attacher::AttachEngine3D
  Height = 20
  Placement = pos=(0,0,36.15) rot=(0,0,1;0rad)
  Radius = 14
FEATURE [Part::Cylinder] Cylinder061
  Angle = 360
  AttacherType = Attacher::AttachEngine3D
  Height = 10
  Placement = pos=(0,0,36.15) rot=(0,0,1;0rad)
  Radius = 4
FEATURE [Part::MultiFuse] Fusion135  label="removeToCreteHoleForPlugHousing048"
  Placement = pos=(70,19,36) rot=(0,1,0;1.5708rad)
  Shapes = -> [Cylinder060,Cylinder061]
FEATURE [Part::Box] Box035  label="removeToCreteHoleForPlugHousing049"
  AttacherType = Attacher::AttachEngine3D
  Height = 28.6
  Length = 20
  Placement = pos=(106.15,0,21.7) rot=(0,0,1;0rad)
  Width = 19
FEATURE [Part::MultiFuse] Fusion133  label="removeToCreteHoleForPlugHousing045"
  Placement = pos=(0,0,-28.3) rot=(0,0,1;0rad)
  Shapes = -> [Box035,Fusion134]
FEATURE [Part::MultiFuse] Fusion138  label="removeToCreteHoleForPlugHousing051"
  Placement = pos=(70,19,36) rot=(0,1,0;1.5708rad)
  Shapes = -> [Cylinder056,Cylinder057]
FEATURE [Part::MultiFuse] Fusion137  label="removeToCreteHoleForPlugHousing050"
  Placement = pos=(0,0,28.3) rot=(0,0,1;0rad)
  Shapes = -> [Box034,Fusion138]
FEATURE [Part::MultiFuse] Fusion132  label="removeToCreatePlugHousingBottomBit002"
  Shapes = -> [Fusion133,Fusion137]
FEATURE [Part::MultiFuse] Fusion136  label="removeToCreatePlugHousingBottomBit003"
  Shapes = -> [Fusion135,Fusion132]
FEATURE [Part::Cut] Cut058  label="bottomPlugHousingBit002"
  Base = -> Extrude063
  Placement = pos=(-0.09,0,0) rot=(0,0,1;0rad)
  Tool = -> Fusion136
FEATURE [Sketcher::SketchObject] Sketch073  label="bottomSketch003"
  FullyConstrained = true
  sketch-geometry (45):
    g0: LineSegment StartX=6.29999 StartY=8 StartZ=0 EndX=3.29999 EndY=8 EndZ=0
    g1: LineSegment StartX=3.29999 StartY=8 StartZ=0 EndX=3.29999 EndY=-6.03275e-07 EndZ=0
    g2: ArcOfCircle CenterX=8.29999 CenterY=5 CenterZ=0 NormalX=0 NormalY=0 NormalZ=1 AngleXU=0 Radius=2 StartAngle=3.14159 EndAngle=4.71239
    g3: LineSegment StartX=6.29999 StartY=8 StartZ=0 EndX=6.29999 EndY=5 EndZ=0
    g4: ArcOfCircle CenterX=105 CenterY=19 CenterZ=0 NormalX=0 NormalY=0 NormalZ=1 AngleXU=0 Radius=12.7 StartAngle=4.71239 EndAngle=5.94289
    g5-g11: Circle x7 (B-spline internal-alignment scaffolding for g12; pole/knot coordinates omitted)
    g12: BSplineCurve PolesCount=7 KnotsCount=5 Degree=3 IsPeriodic=0
    g13-g17: GeomPoint x5 (B-spline internal-alignment scaffolding for g12; pole/knot coordinates omitted)
    g18: ArcOfCircle CenterX=105 CenterY=19 CenterZ=0 NormalX=0 NormalY=0 NormalZ=1 AngleXU=0 Radius=15.7 StartAngle=5.81226 EndAngle=6.28319
    g19: BSplineCurve PolesCount=5 KnotsCount=3 Degree=3 IsPeriodic=0
    g20: LineSegment StartX=8.29999 StartY=3 StartZ=0 EndX=101.7 EndY=3 EndZ=0
    g21: LineSegment StartX=3.29999 StartY=-6.03275e-07 StartZ=0 EndX=105 EndY=-6.03275e-07 EndZ=0
    g22: LineSegment StartX=120.974 StartY=8.71251 StartZ=0 EndX=122.332 EndY=7.83778 EndZ=0
    g23: LineSegment StartX=105 StartY=-6.03274e-07 StartZ=0 EndX=113 EndY=-6.03274e-07 EndZ=0
    g24: ArcOfCircle CenterX=105 CenterY=19 CenterZ=0 NormalX=0 NormalY=0 NormalZ=1 AngleXU=0 Radius=20.6155 StartAngle=5.11091 EndAngle=5.71103
    g25: ArcOfCircle CenterX=117.7 CenterY=19 CenterZ=0 NormalX=0 NormalY=0 NormalZ=1 AngleXU=0 Radius=3 StartAngle=1.2e-15 EndAngle=2.10468
    g26: Circle CenterX=116.345 CenterY=16.3232 CenterZ=0 NormalX=0 NormalY=0 NormalZ=1 AngleXU=0 Radius=1
    g27: Circle CenterX=117.24 CenterY=15.7584 CenterZ=0 NormalX=0 NormalY=0 NormalZ=1 AngleXU=0 Radius=1
    g28: Circle CenterX=116.972 CenterY=14.7612 CenterZ=0 NormalX=0 NormalY=0 NormalZ=1 AngleXU=0 Radius=1
    g29: BSplineCurve PolesCount=3 KnotsCount=2 Degree=2 IsPeriodic=0
    g30: GeomPoint X=116.345 Y=16.3232 Z=0
    g31: GeomPoint X=116.972 Y=14.7612 Z=0
    g32: Circle CenterX=115.828 CenterY=17.157 CenterZ=0 NormalX=0 NormalY=0 NormalZ=1 AngleXU=0 Radius=1
    g33: Circle CenterX=115.841 CenterY=16.639 CenterZ=0 NormalX=0 NormalY=0 NormalZ=1 AngleXU=0 Radius=1
    g34: Circle CenterX=116.345 CenterY=16.3232 CenterZ=0 NormalX=0 NormalY=0 NormalZ=1 AngleXU=0 Radius=1
    g35: BSplineCurve PolesCount=3 KnotsCount=2 Degree=2 IsPeriodic=0
    g36: GeomPoint X=115.828 Y=17.157 Z=0
    g37: GeomPoint X=116.345 Y=16.3232 Z=0
    g38: LineSegment StartX=115.828 StartY=17.157 StartZ=0 EndX=115.828 EndY=20.8307 EndZ=0
    g39: Circle CenterX=115.828 CenterY=20.8307 CenterZ=0 NormalX=0 NormalY=0 NormalZ=1 AngleXU=0 Radius=1
    g40: Circle CenterX=115.831 CenterY=21.3396 CenterZ=0 NormalX=0 NormalY=0 NormalZ=1 AngleXU=0 Radius=1
    g41: Circle CenterX=116.173 CenterY=21.5825 CenterZ=0 NormalX=0 NormalY=0 NormalZ=1 AngleXU=0 Radius=1
    g42: BSplineCurve PolesCount=3 KnotsCount=2 Degree=2 IsPeriodic=0
    g43: GeomPoint X=115.828 Y=20.8307 Z=0
    g44: GeomPoint X=116.173 Y=21.5825 Z=0
  constraints (70):
    c: Horizontal(g0)
    c: Distance(g0) = 3
    c: Coincident(g1,g0)
    c: Vertical(g1)
    c: Block(g2)
    c: Block(g0)
    c: Coincident(g3,g0)
    c: Coincident(g3,g2)
    c: Vertical(g3)
    c: Block(g1)
    c: Block(g4)
    c: Coincident(g19,g4)
    c: Block(g19)
    c: Equal(g5, g6-g11) x6
    c: InternalAlignment(g5-g11 -> g12) x7
    c: InternalAlignment(g13-g17 -> g12) x5
    c: Block(g12)
    c: Coincident(g18,g12)
    c: Block(g18)
    c: Coincident(g20,g2)
    c: Coincident(g20,g19)
    c: Horizontal(g20)
    c: Distance(g20) = 93.4
    c: Coincident(g21,g1)
    c: Horizontal(g21)
    c: Distance(g21) = 101.7
    c: Horizontal(g23)
    c: Distance(g23) = 8
    c: Coincident(g24,g23)
    c: Block(g23)
    c: Coincident(g22,g24)
    c: Block(g24)
    c: Block(g22)
    c: Distance(g22) = 1.61553
    c: Coincident(g25,g18)
    c: Block(g25)
    c: Weight(g26) = 1
    c: Equal(g26,g27)
    c: Equal(g26,g28)
    c: Coincident(g29,g4)
    c: InternalAlignment(g26,g29)
    c: InternalAlignment(g27,g29)
    c: InternalAlignment(g28,g29)
    c: InternalAlignment(g30,g29)
    c: InternalAlignment(g31,g29)
    c: Block(g29)
    c: Weight(g32) = 1
    c: Equal(g32,g33)
    c: Equal(g32,g34)
    c: Coincident(g35,g29)
    c: InternalAlignment(g32,g35)
    c: InternalAlignment(g33,g35)
    c: InternalAlignment(g34,g35)
    c: InternalAlignment(g36,g35)
    c: InternalAlignment(g37,g35)
    c: Block(g35)
    c: Coincident(g38,g35)
    c: Vertical(g38)
    c: Block(g38)
    c: Coincident(g42,g38)
    c: Weight(g39) = 1
    c: Equal(g39,g40)
    c: Equal(g39,g41)
    c: Coincident(g42,g25)
    c: InternalAlignment(g39,g42)
    c: InternalAlignment(g40,g42)
    c: InternalAlignment(g41,g42)
    c: InternalAlignment(g43,g42)
    c: InternalAlignment(g44,g42)
    c: Block(g42)
FEATURE [Part::Extrusion] Extrude064  label="bottom016"
  Base = -> Sketch073
  Dir = (0,0,1)
  DirMode = 2
  FaceMakerClass = Part::FaceMakerBullseye
  LengthFwd = 71.4
  LengthRev = 0
  Placement = pos=(0,0,0.3) rot=(0,0,1;0rad)
  Solid = true
  Symmetric = false
FEATURE [Part::Revolution] Revolve157  label="removeToCreateScrewAndThreadedInsertHole063"
  Angle = 360
  Axis = (0,1,0)
  Base = (0,0,0)
  FaceMakerClass = Part::FaceMakerBullseye
  Placement = pos=(12.5,0,10) rot=(0,0,1;0rad)
  Solid = false
  Source = -> Face141
  Symmetric = false
FEATURE [Sketcher::SketchObject] Sketch074
  FullyConstrained = true
  Placement = pos=(117,19,0) rot=(0.57735,0.57735,0.57735;2.0944rad)
  sketch-geometry (48):
    g0: LineSegment StartX=-49.19 StartY=69.25 StartZ=0 EndX=-49.19 EndY=66.25 EndZ=0
    g1: LineSegment StartX=-49.19 StartY=63.5 StartZ=0 EndX=-49.19 EndY=60.5 EndZ=0
    g2: LineSegment StartX=-49.19 StartY=57.75 StartZ=0 EndX=-49.19 EndY=54.75 EndZ=0
    g3: LineSegment StartX=-49.19 StartY=52 StartZ=0 EndX=-49.19 EndY=49 EndZ=0
    g4: LineSegment StartX=-49.19 StartY=46.25 StartZ=0 EndX=-49.19 EndY=43.25 EndZ=0
    g5: LineSegment StartX=-49.19 StartY=40.5 StartZ=0 EndX=-49.19 EndY=37.5 EndZ=0
    g6: LineSegment StartX=-49.19 StartY=34.5 StartZ=0 EndX=-49.19 EndY=31.5 EndZ=0
    g7: LineSegment StartX=-49.19 StartY=28.75 StartZ=0 EndX=-49.19 EndY=25.75 EndZ=0
    g8: LineSegment StartX=-49.19 StartY=23 StartZ=0 EndX=-49.19 EndY=20 EndZ=0
    g9: LineSegment StartX=-49.19 StartY=17.25 StartZ=0 EndX=-49.19 EndY=14.25 EndZ=0
    g10: LineSegment StartX=-49.19 StartY=11.5 StartZ=0 EndX=-49.19 EndY=8.5 EndZ=0
    g11: LineSegment StartX=-49.19 StartY=5.75 StartZ=0 EndX=-49.19 EndY=2.75 EndZ=0
    g12: ArcOfCircle CenterX=-1.5 CenterY=67.75 CenterZ=0 NormalX=0 NormalY=0 NormalZ=1 AngleXU=0 Radius=1.5 StartAngle=4.71239 EndAngle=7.85398
    g13: ArcOfCircle CenterX=-1.5 CenterY=62 CenterZ=0 NormalX=0 NormalY=0 NormalZ=1 AngleXU=0 Radius=1.5 StartAngle=4.71239 EndAngle=7.85398
    g14: ArcOfCircle CenterX=-1.5 CenterY=56.25 CenterZ=0 NormalX=0 NormalY=0 NormalZ=1 AngleXU=0 Radius=1.5 StartAngle=4.71239 EndAngle=7.85398
    g15: ArcOfCircle CenterX=-11.49 CenterY=50.5 CenterZ=0 NormalX=0 NormalY=0 NormalZ=1 AngleXU=0 Radius=1.5 StartAngle=4.71239 EndAngle=7.85398
    g16: ArcOfCircle CenterX=-16.28 CenterY=44.75 CenterZ=0 NormalX=0 NormalY=0 NormalZ=1 AngleXU=0 Radius=1.5 StartAngle=4.71239 EndAngle=7.85398
    g17: ArcOfCircle CenterX=-18.2337 CenterY=39 CenterZ=0 NormalX=0 NormalY=0 NormalZ=1 AngleXU=0 Radius=1.5 StartAngle=4.71485 EndAngle=7.85398
    g18: ArcOfCircle CenterX=-16.2837 CenterY=27.25 CenterZ=0 NormalX=0 NormalY=0 NormalZ=1 AngleXU=0 Radius=1.5 StartAngle=4.71485 EndAngle=7.85398
    g19: ArcOfCircle CenterX=-18.2337 CenterY=33 CenterZ=0 NormalX=0 NormalY=0 NormalZ=1 AngleXU=0 Radius=1.5 StartAngle=4.71485 EndAngle=7.85398
    g20: ArcOfCircle CenterX=-11.49 CenterY=21.5 CenterZ=0 NormalX=0 NormalY=0 NormalZ=1 AngleXU=0 Radius=1.5 StartAngle=4.71239 EndAngle=7.85398
    g21: ArcOfCircle CenterX=-1.5 CenterY=4.25 CenterZ=0 NormalX=0 NormalY=0 NormalZ=1 AngleXU=0 Radius=1.5 StartAngle=4.71239 EndAngle=7.85398
    g22: ArcOfCircle CenterX=-1.5 CenterY=10 CenterZ=0 NormalX=0 NormalY=0 NormalZ=1 AngleXU=0 Radius=1.5 StartAngle=4.71239 EndAngle=7.85398
    g23: ArcOfCircle CenterX=-1.5 CenterY=15.75 CenterZ=0 NormalX=0 NormalY=0 NormalZ=1 AngleXU=0 Radius=1.5 StartAngle=4.71239 EndAngle=7.85398
    g24: LineSegment StartX=-49.19 StartY=69.25 StartZ=0 EndX=-1.5 EndY=69.25 EndZ=0
    g25: LineSegment StartX=-49.19 StartY=66.25 StartZ=0 EndX=-1.5 EndY=66.25 EndZ=0
    g26: LineSegment StartX=-49.19 StartY=63.5 StartZ=0 EndX=-1.5 EndY=63.5 EndZ=0
    g27: LineSegment StartX=-49.19 StartY=60.5 StartZ=0 EndX=-1.5 EndY=60.5 EndZ=0
    g28: LineSegment StartX=-49.19 StartY=57.75 StartZ=0 EndX=-1.5 EndY=57.75 EndZ=0
    g29: LineSegment StartX=-49.19 StartY=54.75 StartZ=0 EndX=-1.5 EndY=54.75 EndZ=0
    g30: LineSegment StartX=-49.19 StartY=52 StartZ=0 EndX=-11.49 EndY=52 EndZ=0
    g31: LineSegment StartX=-49.19 StartY=49 StartZ=0 EndX=-11.49 EndY=49 EndZ=0
    g32: LineSegment StartX=-49.19 StartY=46.25 StartZ=0 EndX=-16.28 EndY=46.25 EndZ=0
    g33: LineSegment StartX=-49.19 StartY=43.25 StartZ=0 EndX=-16.28 EndY=43.25 EndZ=0
    g34: LineSegment StartX=-49.19 StartY=40.5 StartZ=0 EndX=-18.2337 EndY=40.5 EndZ=0
    g35: LineSegment StartX=-49.19 StartY=37.5 StartZ=0 EndX=-18.23 EndY=37.5 EndZ=0
    g36: LineSegment StartX=-49.19 StartY=34.5 StartZ=0 EndX=-18.2337 EndY=34.5 EndZ=0
    g37: LineSegment StartX=-49.19 StartY=31.5 StartZ=0 EndX=-18.23 EndY=31.5 EndZ=0
    g38: LineSegment StartX=-49.19 StartY=28.75 StartZ=0 EndX=-16.2837 EndY=28.75 EndZ=0
    g39: LineSegment StartX=-49.19 StartY=25.75 StartZ=0 EndX=-16.28 EndY=25.75 EndZ=0
    g40: LineSegment StartX=-49.19 StartY=23 StartZ=0 EndX=-11.49 EndY=23 EndZ=0
    g41: LineSegment StartX=-49.19 StartY=20 StartZ=0 EndX=-11.49 EndY=20 EndZ=0
    g42: LineSegment StartX=-49.19 StartY=17.25 StartZ=0 EndX=-1.5 EndY=17.25 EndZ=0
    g43: LineSegment StartX=-49.19 StartY=14.25 StartZ=0 EndX=-1.5 EndY=14.25 EndZ=0
    g44: LineSegment StartX=-49.19 StartY=11.5 StartZ=0 EndX=-1.5 EndY=11.5 EndZ=0
    g45: LineSegment StartX=-49.19 StartY=8.5 StartZ=0 EndX=-1.5 EndY=8.5 EndZ=0
    g46: LineSegment StartX=-49.19 StartY=5.75 StartZ=0 EndX=-1.5 EndY=5.75 EndZ=0
    g47: LineSegment StartX=-49.19 StartY=2.75 StartZ=0 EndX=-1.5 EndY=2.75 EndZ=0
  constraints (120):
    c: Vertical(g0)
    c: Distance(g0) = 3
    c: Block(g0)
    c: Vertical(g1)
    c: Distance(g1) = 3
    c: Vertical(g2)
    c: Equal(g0,g2) = 3
    c: Block(g2)
    c: Vertical(g3)
    c: Equal(g1,g3) = 3
    c: Vertical(g4)
    c: Equal(g0,g4) = 3
    c: Block(g4)
    c: Vertical(g5)
    c: Equal(g1,g5) = 3
    c: Vertical(g6)
    c: Equal(g0,g6) = 3
    c: Block(g6)
    c: Vertical(g7)
    c: Equal(g1,g7) = 3
    c: Vertical(g8)
    c: Equal(g0,g8) = 3
    c: Block(g8)
    c: Vertical(g9)
    c: Equal(g1,g9) = 3
    c: Vertical(g10)
    c: Equal(g0,g10) = 3
    c: Block(g10)
    c: Vertical(g11)
    c: Equal(g1,g11) = 3
    c: Block(g12)
    c: Block(g13)
    c: Block(g14)
    c: Block(g15)
    c: Block(g16)
    c: Block(g17)
    c: Block(g18)
    c: Block(g19)
    c: Block(g20)
    c: Block(g21)
    c: Block(g22)
    c: Block(g23)
    c: Block(g11)
    c: Block(g9)
    c: Block(g7)
    c: Block(g5)
    c: Block(g3)
    c: Block(g1)
    c: Coincident(g24,g0)
    c: Coincident(g24,g12)
    c: Horizontal(g24)
    c: Coincident(g25,g0)
    c: Coincident(g25,g12)
    c: Horizontal(g25)
    c: Coincident(g26,g1)
    c: Coincident(g26,g13)
    c: Horizontal(g26)
    c: Coincident(g27,g1)
    c: Coincident(g27,g13)
    c: Horizontal(g27)
    c: Coincident(g28,g2)
    c: Coincident(g28,g14)
    c: Horizontal(g28)
    c: Coincident(g29,g2)
    c: Coincident(g29,g14)
    c: Horizontal(g29)
    c: Coincident(g30,g3)
    c: Coincident(g30,g15)
    c: Horizontal(g30)
    c: Coincident(g31,g3)
    c: Coincident(g31,g15)
    c: Horizontal(g31)
    c: Coincident(g32,g4)
    c: Coincident(g32,g16)
    c: Horizontal(g32)
    c: Coincident(g33,g4)
    c: Coincident(g33,g16)
    c: Horizontal(g33)
    c: Coincident(g34,g5)
    c: Coincident(g34,g17)
    c: Horizontal(g34)
    c: Coincident(g35,g5)
    c: Coincident(g35,g17)
    c: Horizontal(g35)
    c: Coincident(g36,g6)
    c: Coincident(g36,g19)
    c: Horizontal(g36)
    c: Coincident(g37,g6)
    c: Coincident(g37,g19)
    c: Horizontal(g37)
    c: Coincident(g38,g7)
    c: Coincident(g38,g18)
    c: Horizontal(g38)
    c: Coincident(g39,g7)
    c: Coincident(g39,g18)
    c: Horizontal(g39)
    c: Coincident(g40,g8)
    c: Coincident(g40,g20)
    c: Horizontal(g40)
    c: Coincident(g41,g8)
    c: Coincident(g41,g20)
    c: Horizontal(g41)
    c: Coincident(g42,g9)
    c: Coincident(g42,g23)
    c: Horizontal(g42)
    c: Coincident(g43,g9)
    c: Coincident(g43,g23)
    c: Horizontal(g43)
    c: Coincident(g44,g10)
    c: Coincident(g44,g22)
    c: Horizontal(g44)
    c: Coincident(g45,g10)
    c: Coincident(g45,g22)
    c: Horizontal(g45)
    c: Coincident(g46,g11)
    c: Coincident(g46,g21)
    c: Horizontal(g46)
    c: Coincident(g47,g11)
    c: Coincident(g47,g21)
    c: Horizontal(g47)
FEATURE [Part::Extrusion] Extrude065
  Base = -> Sketch074
  Dir = (1,0,0)
  DirMode = 2
  FaceMakerClass = Part::FaceMakerBullseye
  LengthFwd = 23
  LengthRev = 0
  Placement = pos=(-19,0,0) rot=(0,0,1;0rad)
  Solid = true
  Symmetric = false
FEATURE [Part::Fillet] Fillet056  label="removeToCreateVentalationHoles003"
  Base = -> Extrude065
  Edges = <same value as first occurrence — deduplicated (x6 in doc)>
  Placement = pos=(7,0.02,0) rot=(0,0,1;0rad)
FEATURE [Part::Revolution] Revolve158  label="removeToCreateScrewAndThreadedInsertHole065"
  Angle = 360
  Axis = (0,1,0)
  Base = (0,0,0)
  FaceMakerClass = Part::FaceMakerBullseye
  Placement = pos=(12.5,0,62) rot=(0,0,1;0rad)
  Solid = false
  Source = -> Face146
  Symmetric = false
FEATURE [Part::Revolution] Revolve159  label="removeToCreateScrewAndThreadedInsertHole066"
  Angle = 360
  Axis = (0,1,0)
  Base = (0,0,0)
  FaceMakerClass = Part::FaceMakerBullseye
  Placement = pos=(89.5,0,68.5) rot=(0,0,1;0rad)
  Solid = false
  Source = -> Face143
  Symmetric = false
FEATURE [Part::Revolution] Revolve160  label="removeToCreateScrewAndThreadedInsertHole067"
  Angle = 360
  Axis = (0,1,0)
  Base = (0,0,0)
  FaceMakerClass = Part::FaceMakerBullseye
  Placement = pos=(89.5,0,3.5) rot=(0,0,1;0rad)
  Solid = false
  Source = -> Face142
  Symmetric = false
FEATURE [Part::Revolution] Revolve161  label="removeToCreateScrewAndThreadedInsertHole068"
  Angle = 360
  Axis = (0,1,0)
  Base = (0,0,0)
  FaceMakerClass = Part::FaceMakerBullseye
  Placement = pos=(109.5,4.7,3.5) rot=(0,0,1;0rad)
  Solid = false
  Source = -> Face145
  Symmetric = false
FEATURE [Part::Revolution] Revolve162  label="removeToCreateScrewAndThreadedInsertHole069"
  Angle = 360
  Axis = (0,1,0)
  Base = (0,0,0)
  FaceMakerClass = Part::FaceMakerBullseye
  Placement = pos=(109.5,4.7,68.5) rot=(0,0,1;0rad)
  Solid = false
  Source = -> Face144
  Symmetric = false
FEATURE [Part::MultiFuse] Fusion141  label="removeToCreateScrewAndThreadedInsertHole064"
  Shapes = -> [Revolve162,Revolve161,Revolve160,Revolve159,Revolve158,Revolve157]
FEATURE [Part::Cylinder] Cylinder062
  Angle = 360
  AttacherType = Attacher::AttachEngine3D
  Height = 20
  Placement = pos=(0,0,36.15) rot=(0,0,1;0rad)
  Radius = 14
FEATURE [Part::Cylinder] Cylinder063
  Angle = 360
  AttacherType = Attacher::AttachEngine3D
  Height = 10
  Placement = pos=(0,0,36.15) rot=(0,0,1;0rad)
  Radius = 4
FEATURE [Part::MultiFuse] Fusion139  label="removeToCreteHoleForPlugHousing052"
  Placement = pos=(70,19,36) rot=(0,1,0;1.5708rad)
  Shapes = -> [Cylinder062,Cylinder063]
FEATURE [Part::Cut] Cut060  label="bottom017"
  Base = -> Extrude064
  Tool = -> Fusion139
FEATURE [Part::Cut] Cut061  label="bottom019"
  Base = -> Cut060
  Tool = -> Fusion141
FEATURE [Part::MultiFuse] Fusion140  label="bottom018"
  Shapes = -> [Cut061,Cut058]
FEATURE [Part::Cut] Cut059  label="bottom020"
  Base = -> Fusion140
  Tool = -> Fillet056
FEATURE [Part::Box] Box036  label="Cube021"
  AttacherType = Attacher::AttachEngine3D
  Height = 80
  Length = 26
  Placement = pos=(0,-1,-5) rot=(0,0,1;0rad)
  Width = 11
FEATURE [Part::Cut] Cut062  label="removeFromBottom002"
  Base = -> Cut057
  Tool = -> Box036
FEATURE [Part::Cut] Cut063
  Base = -> Cut059
  Tool = -> Cut062
FEATURE [Part::Cut] Cut064  label="pcbStands"
  Base = -> Fusion095
  Tool = -> Fusion127
FEATURE [Sketcher::SketchObject] Sketch075  label="topSketch022"
  FullyConstrained = true
  sketch-geometry (6):
    g0: LineSegment StartX=19 StartY=38 StartZ=0 EndX=117 EndY=38 EndZ=0
    g1: ArcOfCircle CenterX=19 CenterY=19 CenterZ=0 NormalX=0 NormalY=0 NormalZ=1 AngleXU=0 Radius=19 StartAngle=1.5708 EndAngle=3.14159
    g2: LineSegment StartX=117 StartY=38 StartZ=0 EndX=117 EndY=19 EndZ=0
    g3: LineSegment StartX=98 StartY=1.0161e-12 StartZ=0 EndX=5.22862e-06 EndY=1.0161e-12 EndZ=0
    g4: LineSegment StartX=5.22862e-06 StartY=19 StartZ=0 EndX=5.22862e-06 EndY=1.0161e-12 EndZ=0
    g5: ArcOfCircle CenterX=98 CenterY=19 CenterZ=0 NormalX=0 NormalY=0 NormalZ=1 AngleXU=0 Radius=19 StartAngle=4.71239 EndAngle=6.28319
  constraints (16):
    c: Horizontal(g0)
    c: Distance(g0) = 98
    c: Coincident(g1,g0)
    c: Block(g1)
    c: Coincident(g2,g0)
    c: Vertical(g2)
    c: Distance(g2) = 19
    c: Horizontal(g3)
    c: Coincident(g4,g1)
    c: Vertical(g4)
    c: Coincident(g3,g4)
    c: Block(g3)
    c: Coincident(g5,g2)
    c: Coincident(g5,g3)
    c: Block(g0)
    c: Block(g5)
FEATURE [Part::Extrusion] Extrude067  label="sideB003"
  Base = -> Sketch075
  Dir = (0,0,1)
  DirMode = 2
  FaceMakerClass = Part::FaceMakerBullseye
  LengthFwd = 3
  LengthRev = 0
  Placement = pos=(0,0,71.7) rot=(0,0,1;0rad)
  Solid = true
  Symmetric = false
FEATURE [Sketcher::SketchObject] Sketch076  label="topSketch023"
  FullyConstrained = true
  sketch-geometry (6):
    g0: LineSegment StartX=19 StartY=38 StartZ=0 EndX=117 EndY=38 EndZ=0
    g1: ArcOfCircle CenterX=19 CenterY=19 CenterZ=0 NormalX=0 NormalY=0 NormalZ=1 AngleXU=0 Radius=19 StartAngle=1.5708 EndAngle=3.14159
    g2: LineSegment StartX=117 StartY=38 StartZ=0 EndX=117 EndY=19 EndZ=0
    g3: LineSegment StartX=98 StartY=1.0161e-12 StartZ=0 EndX=5.22862e-06 EndY=1.0161e-12 EndZ=0
    g4: LineSegment StartX=5.22862e-06 StartY=19 StartZ=0 EndX=5.22862e-06 EndY=1.0161e-12 EndZ=0
    g5: ArcOfCircle CenterX=98 CenterY=19 CenterZ=0 NormalX=0 NormalY=0 NormalZ=1 AngleXU=0 Radius=19 StartAngle=4.71239 EndAngle=6.28319
  constraints (16):
    c: Horizontal(g0)
    c: Distance(g0) = 98
    c: Coincident(g1,g0)
    c: Block(g1)
    c: Coincident(g2,g0)
    c: Vertical(g2)
    c: Distance(g2) = 19
    c: Horizontal(g3)
    c: Coincident(g4,g1)
    c: Vertical(g4)
    c: Coincident(g3,g4)
    c: Block(g3)
    c: Coincident(g5,g2)
    c: Coincident(g5,g3)
    c: Block(g0)
    c: Block(g5)
FEATURE [Part::Extrusion] Extrude066  label="sideA003"
  Base = -> Sketch076
  Dir = (0,0,1)
  DirMode = 2
  FaceMakerClass = Part::FaceMakerBullseye
  LengthFwd = 3
  LengthRev = 0
  Placement = pos=(0,0,-2.7) rot=(0,0,1;0rad)
  Solid = true
  Symmetric = false
FEATURE [Part::MultiFuse] Fusion142  label="removeFromBottom003"
  Placement = pos=(2,0,0) rot=(0,0,1;0rad)
  Shapes = -> [Extrude066,Extrude067]
FEATURE [Part::Cut] Cut065  label="screwRetainers002"
  Base = -> Fusion096
  Tool = -> Fusion142
FEATURE [Sketcher::SketchObject] Sketch077
  FullyConstrained = true
  Placement = pos=(117,19,0) rot=(0.57735,0.57735,0.57735;2.0944rad)
  sketch-geometry (8):
    g0: LineSegment StartX=-49.19 StartY=63.5 StartZ=0 EndX=-49.19 EndY=60.5 EndZ=0
    g1: LineSegment StartX=-49.19 StartY=11.5 StartZ=0 EndX=-49.19 EndY=8.5 EndZ=0
    g2: ArcOfCircle CenterX=-1.5 CenterY=62 CenterZ=0 NormalX=0 NormalY=0 NormalZ=1 AngleXU=0 Radius=1.5 StartAngle=4.71239 EndAngle=7.85398
    g3: ArcOfCircle CenterX=-1.5 CenterY=10 CenterZ=0 NormalX=0 NormalY=0 NormalZ=1 AngleXU=0 Radius=1.5 StartAngle=4.71239 EndAngle=7.85398
    g4: LineSegment StartX=-49.19 StartY=63.5 StartZ=0 EndX=-1.5 EndY=63.5 EndZ=0
    g5: LineSegment StartX=-49.19 StartY=60.5 StartZ=0 EndX=-1.5 EndY=60.5 EndZ=0
    g6: LineSegment StartX=-49.19 StartY=11.5 StartZ=0 EndX=-1.5 EndY=11.5 EndZ=0
    g7: LineSegment StartX=-49.19 StartY=8.5 StartZ=0 EndX=-1.5 EndY=8.5 EndZ=0
  constraints (19):
    c: Vertical(g0)
    c: Distance(g0) = 3
    c: Vertical(g1)
    c: Block(g1)
    c: Block(g2)
    c: Block(g3)
    c: Block(g0)
    c: Coincident(g4,g0)
    c: Coincident(g4,g2)
    c: Horizontal(g4)
    c: Coincident(g5,g0)
    c: Coincident(g5,g2)
    c: Horizontal(g5)
    c: Coincident(g6,g1)
    c: Coincident(g6,g3)
    c: Horizontal(g6)
    c: Coincident(g7,g1)
    c: Coincident(g7,g3)
    c: Horizontal(g7)
FEATURE [Part::Extrusion] Extrude068
  Base = -> Sketch077
  Dir = (1,0,0)
  DirMode = 2
  FaceMakerClass = Part::FaceMakerBullseye
  LengthFwd = 10
  LengthRev = 0
  Solid = true
  Symmetric = false
FEATURE [Part::Fillet] Fillet057  label="removeFromtMoreFrontCaseScrewRetainers002"
  Base = -> Extrude068
  Edges = 4 edges r=1.49: [Edge6,Edge11,Edge18,Edge23]
  Placement = pos=(-12,0,0) rot=(0,0,1;0rad)
FEATURE [Sketcher::SketchObject] Sketch078
  FullyConstrained = true
  Placement = pos=(117,19,0) rot=(0.57735,0.57735,0.57735;2.0944rad)
  sketch-geometry (8):
    g0: LineSegment StartX=-49.19 StartY=69.25 StartZ=0 EndX=-49.19 EndY=66.25 EndZ=0
    g1: LineSegment StartX=-49.19 StartY=5.75 StartZ=0 EndX=-49.19 EndY=2.75 EndZ=0
    g2: ArcOfCircle CenterX=-1.5 CenterY=67.75 CenterZ=0 NormalX=0 NormalY=0 NormalZ=1 AngleXU=0 Radius=1.5 StartAngle=4.71239 EndAngle=7.85398
    g3: ArcOfCircle CenterX=-1.5 CenterY=4.25 CenterZ=0 NormalX=0 NormalY=0 NormalZ=1 AngleXU=0 Radius=1.5 StartAngle=4.71239 EndAngle=7.85398
    g4: LineSegment StartX=-49.19 StartY=69.25 StartZ=0 EndX=-1.5 EndY=69.25 EndZ=0
    g5: LineSegment StartX=-49.19 StartY=66.25 StartZ=0 EndX=-1.5 EndY=66.25 EndZ=0
    g6: LineSegment StartX=-49.19 StartY=5.75 StartZ=0 EndX=-1.5 EndY=5.75 EndZ=0
    g7: LineSegment StartX=-49.19 StartY=2.75 StartZ=0 EndX=-1.5 EndY=2.75 EndZ=0
  constraints (19):
    c: Vertical(g0)
    c: Distance(g0) = 3
    c: Block(g0)
    c: Vertical(g1)
    c: Block(g2)
    c: Block(g3)
    c: Block(g1)
    c: Coincident(g4,g0)
    c: Coincident(g4,g2)
    c: Horizontal(g4)
    c: Coincident(g5,g0)
    c: Coincident(g5,g2)
    c: Horizontal(g5)
    c: Coincident(g6,g1)
    c: Coincident(g6,g3)
    c: Horizontal(g6)
    c: Coincident(g7,g1)
    c: Coincident(g7,g3)
    c: Horizontal(g7)
FEATURE [Part::Extrusion] Extrude069
  Base = -> Sketch078
  Dir = (1,0,0)
  DirMode = 2
  FaceMakerClass = Part::FaceMakerBullseye
  LengthFwd = 10
  LengthRev = 0
  Solid = true
  Symmetric = false
FEATURE [Part::Fillet] Fillet058  label="removeFromtMoreFrontCaseScrewRetainers003"
  Base = -> Extrude069
  Edges = 4 edges r=1.49: [Edge6,Edge11,Edge18,Edge23]
  Placement = pos=(-4,0,0) rot=(0,0,1;0rad)
FEATURE [Part::Cut] Cut066
  Base = -> Cut065
  Tool = -> Fillet058
FEATURE [Part::Cut] Cut067  label="screwPillars"
  Base = -> Cut066
  Tool = -> Fillet057
FEATURE [Part::MultiFuse] Fusion143  label="bottom021"
  Shapes = -> [Cut031,Cut063]
FEATURE [Part::Cylinder] Cylinder
  Angle = 360
  AttacherType = Attacher::AttachEngine3D
  Height = 10
  Placement = pos=(20.65,12,4.68) rot=(1,0,0;1.5708rad)
  Radius = 2
FEATURE [Part::Cylinder] Cylinder064
  Angle = 360
  AttacherType = Attacher::AttachEngine3D
  Height = 10
  Placement = pos=(20.65,12,67.38) rot=(1,0,0;1.5708rad)
  Radius = 2
FEATURE [Part::Cylinder] Cylinder065
  Angle = 360
  AttacherType = Attacher::AttachEngine3D
  Height = 10
  Placement = pos=(77.15,12,67.38) rot=(1,0,0;1.5708rad)
  Radius = 2
FEATURE [Part::Cylinder] Cylinder066
  Angle = 360
  AttacherType = Attacher::AttachEngine3D
  Height = 10
  Placement = pos=(77.15,12,4.68) rot=(1,0,0;1.5708rad)
  Radius = 2
FEATURE [Part::MultiFuse] Fusion144  label="removeFromThreadedInsertHousing"
  Shapes = -> [Cylinder065,Cylinder064,Cylinder,Cylinder066]
FEATURE [Part::Cut] Cut068  label="pcbStands001"
  Base = -> Cut064
  Tool = -> Fusion144
FEATURE [Part::MultiFuse] Fusion145
  Shapes = -> [Cut068,Fusion143]
FEATURE [Part::MultiFuse] Fusion146
  Shapes = -> [Fusion145]
FEATURE [Part::MultiFuse] Fusion147  label="bottom022"
  Shapes = -> [Cut067,Fusion146]
FEATURE [Part::MultiFuse] Fusion148  label="casePillars005"
  Shapes = -> [Cut047,Fusion092]
FEATURE [Part::MultiFuse] Fusion149  label="bottom023"
  Shapes = -> [Fusion124,Fusion113,Fusion147]
FEATURE [Part::MultiFuse] Fusion150  label="topBits"
  Shapes = -> [Cut025,Fusion148,Cut030,Fillet034]
FEATURE [Part::Feature] Face149 .. Face152  x4 (patterned run collapsed; names and placements below)
  shape: bbox 3.2 x 1.5 x 2e-07 mm, 1 faces, 0 solids (baked)
FEATURE [Part::Feature] Face153
  shape: bbox 3.6 x 3.2 x 2e-07 mm, 1 faces, 0 solids (baked)
FEATURE [Part::Feature] Face154
  shape: bbox 3.6 x 3.2 x 2e-07 mm, 1 faces, 0 solids (baked)
FEATURE [Sketcher::SketchObject] Sketch079  label="topSketch024"
  FullyConstrained = true
  sketch-geometry (6):
    g0: LineSegment StartX=19 StartY=38 StartZ=0 EndX=117 EndY=38 EndZ=0
    g1: ArcOfCircle CenterX=19 CenterY=19 CenterZ=0 NormalX=0 NormalY=0 NormalZ=1 AngleXU=0 Radius=19 StartAngle=1.5708 EndAngle=3.14159
    g2: LineSegment StartX=117 StartY=38 StartZ=0 EndX=117 EndY=19 EndZ=0
    g3: LineSegment StartX=98 StartY=1.0161e-12 StartZ=0 EndX=5.22862e-06 EndY=1.0161e-12 EndZ=0
    g4: LineSegment StartX=5.22862e-06 StartY=19 StartZ=0 EndX=5.22862e-06 EndY=1.0161e-12 EndZ=0
    g5: ArcOfCircle CenterX=98 CenterY=19 CenterZ=0 NormalX=0 NormalY=0 NormalZ=1 AngleXU=0 Radius=19 StartAngle=4.71239 EndAngle=6.28319
  constraints (16):
    c: Horizontal(g0)
    c: Distance(g0) = 98
    c: Coincident(g1,g0)
    c: Block(g1)
    c: Coincident(g2,g0)
    c: Vertical(g2)
    c: Distance(g2) = 19
    c: Horizontal(g3)
    c: Coincident(g4,g1)
    c: Vertical(g4)
    c: Coincident(g3,g4)
    c: Block(g3)
    c: Coincident(g5,g2)
    c: Coincident(g5,g3)
    c: Block(g0)
    c: Block(g5)
FEATURE [Sketcher::SketchObject] Sketch080  label="topSketch025"
  FullyConstrained = true
  sketch-geometry (6):
    g0: LineSegment StartX=19 StartY=38 StartZ=0 EndX=117 EndY=38 EndZ=0
    g1: ArcOfCircle CenterX=19 CenterY=19 CenterZ=0 NormalX=0 NormalY=0 NormalZ=1 AngleXU=0 Radius=19 StartAngle=1.5708 EndAngle=3.14159
    g2: LineSegment StartX=117 StartY=38 StartZ=0 EndX=117 EndY=19 EndZ=0
    g3: LineSegment StartX=98 StartY=1.0161e-12 StartZ=0 EndX=5.22862e-06 EndY=1.0161e-12 EndZ=0
    g4: LineSegment StartX=5.22862e-06 StartY=19 StartZ=0 EndX=5.22862e-06 EndY=1.0161e-12 EndZ=0
    g5: ArcOfCircle CenterX=98 CenterY=19 CenterZ=0 NormalX=0 NormalY=0 NormalZ=1 AngleXU=0 Radius=19 StartAngle=4.71239 EndAngle=6.28319
  constraints (16):
    c: Horizontal(g0)
    c: Distance(g0) = 98
    c: Coincident(g1,g0)
    c: Block(g1)
    c: Coincident(g2,g0)
    c: Vertical(g2)
    c: Distance(g2) = 19
    c: Horizontal(g3)
    c: Coincident(g4,g1)
    c: Vertical(g4)
    c: Coincident(g3,g4)
    c: Block(g3)
    c: Coincident(g5,g2)
    c: Coincident(g5,g3)
    c: Block(g0)
    c: Block(g5)
FEATURE [Part::Extrusion] Extrude070  label="sideA004"
  Base = -> Sketch080
  Dir = (0,0,1)
  DirMode = 2
  FaceMakerClass = Part::FaceMakerBullseye
  LengthFwd = 3
  LengthRev = 0
  Placement = pos=(0,0,-2.7) rot=(0,0,1;0rad)
  Solid = true
  Symmetric = false
FEATURE [Sketcher::SketchObject] Sketch081
  FullyConstrained = true
  Placement = pos=(117,19,0) rot=(0.57735,0.57735,0.57735;2.0944rad)
  sketch-geometry (8):
    g0: LineSegment StartX=-49.19 StartY=63.5 StartZ=0 EndX=-49.19 EndY=60.5 EndZ=0
    g1: LineSegment StartX=-49.19 StartY=11.5 StartZ=0 EndX=-49.19 EndY=8.5 EndZ=0
    g2: ArcOfCircle CenterX=-1.5 CenterY=62 CenterZ=0 NormalX=0 NormalY=0 NormalZ=1 AngleXU=0 Radius=1.5 StartAngle=4.71239 EndAngle=7.85398
    g3: ArcOfCircle CenterX=-1.5 CenterY=10 CenterZ=0 NormalX=0 NormalY=0 NormalZ=1 AngleXU=0 Radius=1.5 StartAngle=4.71239 EndAngle=7.85398
    g4: LineSegment StartX=-49.19 StartY=63.5 StartZ=0 EndX=-1.5 EndY=63.5 EndZ=0
    g5: LineSegment StartX=-49.19 StartY=60.5 StartZ=0 EndX=-1.5 EndY=60.5 EndZ=0
    g6: LineSegment StartX=-49.19 StartY=11.5 StartZ=0 EndX=-1.5 EndY=11.5 EndZ=0
    g7: LineSegment StartX=-49.19 StartY=8.5 StartZ=0 EndX=-1.5 EndY=8.5 EndZ=0
  constraints (19):
    c: Vertical(g0)
    c: Distance(g0) = 3
    c: Vertical(g1)
    c: Block(g1)
    c: Block(g2)
    c: Block(g3)
    c: Block(g0)
    c: Coincident(g4,g0)
    c: Coincident(g4,g2)
    c: Horizontal(g4)
    c: Coincident(g5,g0)
    c: Coincident(g5,g2)
    c: Horizontal(g5)
    c: Coincident(g6,g1)
    c: Coincident(g6,g3)
    c: Horizontal(g6)
    c: Coincident(g7,g1)
    c: Coincident(g7,g3)
    c: Horizontal(g7)
FEATURE [Part::Extrusion] Extrude071  label="sideB004"
  Base = -> Sketch079
  Dir = (0,0,1)
  DirMode = 2
  FaceMakerClass = Part::FaceMakerBullseye
  LengthFwd = 3
  LengthRev = 0
  Placement = pos=(0,0,71.7) rot=(0,0,1;0rad)
  Solid = true
  Symmetric = false
FEATURE [Part::MultiFuse] Fusion152  label="removeFromBottom004"
  Placement = pos=(2,0,0) rot=(0,0,1;0rad)
  Shapes = -> [Extrude070,Extrude071]
FEATURE [Part::Extrusion] Extrude072
  Base = -> Sketch081
  Dir = (1,0,0)
  DirMode = 2
  FaceMakerClass = Part::FaceMakerBullseye
  LengthFwd = 10
  LengthRev = 0
  Solid = true
  Symmetric = false
FEATURE [Part::Fillet] Fillet059  label="removeFromtMoreFrontCaseScrewRetainers004"
  Base = -> Extrude072
  Edges = 4 edges r=1.49: [Edge6,Edge11,Edge18,Edge23]
  Placement = pos=(-12,0,0) rot=(0,0,1;0rad)
FEATURE [Sketcher::SketchObject] Sketch082
  FullyConstrained = true
  Placement = pos=(117,19,0) rot=(0.57735,0.57735,0.57735;2.0944rad)
  sketch-geometry (8):
    g0: LineSegment StartX=-49.19 StartY=69.25 StartZ=0 EndX=-49.19 EndY=66.25 EndZ=0
    g1: LineSegment StartX=-49.19 StartY=5.75 StartZ=0 EndX=-49.19 EndY=2.75 EndZ=0
    g2: ArcOfCircle CenterX=-1.5 CenterY=67.75 CenterZ=0 NormalX=0 NormalY=0 NormalZ=1 AngleXU=0 Radius=1.5 StartAngle=4.71239 EndAngle=7.85398
    g3: ArcOfCircle CenterX=-1.5 CenterY=4.25 CenterZ=0 NormalX=0 NormalY=0 NormalZ=1 AngleXU=0 Radius=1.5 StartAngle=4.71239 EndAngle=7.85398
    g4: LineSegment StartX=-49.19 StartY=69.25 StartZ=0 EndX=-1.5 EndY=69.25 EndZ=0
    g5: LineSegment StartX=-49.19 StartY=66.25 StartZ=0 EndX=-1.5 EndY=66.25 EndZ=0
    g6: LineSegment StartX=-49.19 StartY=5.75 StartZ=0 EndX=-1.5 EndY=5.75 EndZ=0
    g7: LineSegment StartX=-49.19 StartY=2.75 StartZ=0 EndX=-1.5 EndY=2.75 EndZ=0
  constraints (19):
    c: Vertical(g0)
    c: Distance(g0) = 3
    c: Block(g0)
    c: Vertical(g1)
    c: Block(g2)
    c: Block(g3)
    c: Block(g1)
    c: Coincident(g4,g0)
    c: Coincident(g4,g2)
    c: Horizontal(g4)
    c: Coincident(g5,g0)
    c: Coincident(g5,g2)
    c: Horizontal(g5)
    c: Coincident(g6,g1)
    c: Coincident(g6,g3)
    c: Horizontal(g6)
    c: Coincident(g7,g1)
    c: Coincident(g7,g3)
    c: Horizontal(g7)
FEATURE [Part::Extrusion] Extrude073
  Base = -> Sketch082
  Dir = (1,0,0)
  DirMode = 2
  FaceMakerClass = Part::FaceMakerBullseye
  LengthFwd = 10
  LengthRev = 0
  Solid = true
  Symmetric = false
FEATURE [Part::Fillet] Fillet060  label="removeFromtMoreFrontCaseScrewRetainers005"
  Base = -> Extrude073
  Edges = 4 edges r=1.49: [Edge6,Edge11,Edge18,Edge23]
  Placement = pos=(-4,0,0) rot=(0,0,1;0rad)
FEATURE [Part::Revolution] Revolve163  label="backCaseScrewRetainer004"
  Angle = 360
  Axis = (0,1,0)
  Base = (0,0,0)
  FaceMakerClass = Part::FaceMakerBullseye
  Placement = pos=(12.5,3,62) rot=(0,0,1;0rad)
  Solid = false
  Source = -> Face149
  Symmetric = false
FEATURE [Part::Revolution] Revolve164  label="frontCaseScrewRetainer006"
  Angle = 360
  Axis = (0,1,0)
  Base = (0,0,0)
  FaceMakerClass = Part::FaceMakerBullseye
  Placement = pos=(89.5,3,68.5) rot=(0,0,1;0rad)
  Solid = false
  Source = -> Face151
  Symmetric = false
FEATURE [Part::Revolution] Revolve165  label="frontCaseScrewRetainer007"
  Angle = 360
  Axis = (0,1,0)
  Base = (0,0,0)
  FaceMakerClass = Part::FaceMakerBullseye
  Placement = pos=(89.5,3,3.5) rot=(0,0,1;0rad)
  Solid = false
  Source = -> Face152
  Symmetric = false
FEATURE [Part::Revolution] Revolve166  label="backCaseScrewRetainer005"
  Angle = 360
  Axis = (0,1,0)
  Base = (0,0,0)
  FaceMakerClass = Part::FaceMakerBullseye
  Placement = pos=(12.5,3,10) rot=(0,0,1;0rad)
  Solid = false
  Source = -> Face150
  Symmetric = false
FEATURE [Part::Revolution] Revolve167  label="moreFrontCaseScrewRetainer006"
  Angle = 360
  Axis = (0,1,0)
  Base = (0,0,0)
  FaceMakerClass = Part::FaceMakerBullseye
  Placement = pos=(109.5,4.5,68.5) rot=(0,0,1;0rad)
  Solid = false
  Source = -> Face153
  Symmetric = false
FEATURE [Part::Revolution] Revolve168  label="moreFrontCaseScrewRetainer007"
  Angle = 360
  Axis = (0,1,0)
  Base = (0,0,0)
  FaceMakerClass = Part::FaceMakerBullseye
  Placement = pos=(109.5,4.5,3.5) rot=(0,0,1;0rad)
  Solid = false
  Source = -> Face154
  Symmetric = false
FEATURE [Part::MultiFuse] Fusion151  label="screwRetainers003"
  Shapes = -> [Revolve168,Revolve167,Revolve166,Revolve165,Revolve164,Revolve163]
FEATURE [Part::Cut] Cut069  label="screwRetainers004"
  Base = -> Fusion151
  Tool = -> Fusion152
FEATURE [Part::Cut] Cut070
  Base = -> Cut069
  Tool = -> Fillet060
FEATURE [Part::Cut] Cut071  label="screwPillars001"
  Base = -> Cut070
  Tool = -> Fillet059
FEATURE [Part::MultiFuse] Fusion153  label="bottom024"
  Shapes = -> [Fusion149,Cut071]
FEATURE [Part::Cylinder] Cylinder067
  Angle = 360
  AttacherType = Attacher::AttachEngine3D
  Height = 10
  Placement = pos=(20.65,12,4.68) rot=(1,0,0;1.5708rad)
  Radius = 2
FEATURE [Part::Cylinder] Cylinder068
  Angle = 360
  AttacherType = Attacher::AttachEngine3D
  Height = 10
  Placement = pos=(20.65,12,67.38) rot=(1,0,0;1.5708rad)
  Radius = 2
FEATURE [Part::Cylinder] Cylinder069
  Angle = 360
  AttacherType = Attacher::AttachEngine3D
  Height = 10
  Placement = pos=(77.15,12,67.38) rot=(1,0,0;1.5708rad)
  Radius = 2
FEATURE [Part::Cylinder] Cylinder070
  Angle = 360
  AttacherType = Attacher::AttachEngine3D
  Height = 10
  Placement = pos=(77.15,12,4.68) rot=(1,0,0;1.5708rad)
  Radius = 2
FEATURE [Part::MultiFuse] Fusion154  label="removeFromThreadedInsertHousing001"
  Shapes = -> [Cylinder069,Cylinder068,Cylinder067,Cylinder070]
FEATURE [Part::Cut] Cut072  label="bottom025"
  Base = -> Fusion153
  Tool = -> Fusion154
FEATURE [Image::ImagePlane] ImagePlane
  XSize = 339
  YSize = 72
FEATURE [Sketcher::SketchObject] Sketch083
  FullyConstrained = true
  MapMode = 5
  Support = -> [XY_Plane]
  sketch-geometry (338):
    g0: LineSegment StartX=-151.619 StartY=28.8932 StartZ=0 EndX=-140.819 EndY=28.8932 EndZ=0
    g1: LineSegment StartX=-151.619 StartY=24.0313 StartZ=0 EndX=-151.619 EndY=28.8932 EndZ=0
    g2: LineSegment StartX=-140.819 StartY=17.7713 StartZ=0 EndX=-151.619 EndY=17.7713 EndZ=0
    g3: LineSegment StartX=-151.619 StartY=17.7713 StartZ=0 EndX=-151.619 EndY=22.6313 EndZ=0
    g4: LineSegment StartX=-151.619 StartY=22.6313 StartZ=0 EndX=-145.128 EndY=22.6313 EndZ=0
    g5: LineSegment StartX=-145.128 StartY=24.0313 StartZ=0 EndX=-140.819 EndY=28.8932 EndZ=0
    g6: LineSegment StartX=-145.128 StartY=22.6313 StartZ=0 EndX=-140.819 EndY=17.7713 EndZ=0
    g7: ArcOfCircle CenterX=-155.157 CenterY=23.3323 CenterZ=0 NormalX=0 NormalY=0 NormalZ=1 AngleXU=0 Radius=6.92354 StartAngle=1.03434 EndAngle=5.24885
    g8: ArcOfCircle CenterX=-155.157 CenterY=23.3323 CenterZ=0 NormalX=0 NormalY=0 NormalZ=1 AngleXU=0 Radius=12.6269 StartAngle=1.28675 EndAngle=4.99643
    g9: LineSegment StartX=-151.619 StartY=35.4532 StartZ=0 EndX=-151.619 EndY=29.2832 EndZ=0
    g10: LineSegment StartX=-151.619 StartY=17.3813 StartZ=0 EndX=-151.619 EndY=11.2113 EndZ=0
    g11-g21: Circle x11 (B-spline internal-alignment scaffolding for g22; pole/knot coordinates omitted)
    g22: BSplineCurve PolesCount=11 KnotsCount=9 Degree=3 IsPeriodic=0
    g23-g31: GeomPoint x9 (B-spline internal-alignment scaffolding for g22; pole/knot coordinates omitted)
    g32-g49: Circle x18 (B-spline internal-alignment scaffolding for g50; pole/knot coordinates omitted)
    g50: BSplineCurve PolesCount=18 KnotsCount=16 Degree=3 IsPeriodic=0
    g51-g66: GeomPoint x16 (B-spline internal-alignment scaffolding for g50; pole/knot coordinates omitted)
    g67: LineSegment StartX=-117.124 StartY=30.093 StartZ=0 EndX=-117.603 EndY=26.5272 EndZ=0
    g68: LineSegment StartX=-117.603 StartY=17.8472 StartZ=0 EndX=-117.124 EndY=14.2659 EndZ=0
    g69: Ellipse CenterX=-109.671 CenterY=20.025 CenterZ=0 NormalX=0 NormalY=0 NormalZ=1 MajorRadius=3.34798 MinorRadius=2.71052 AngleXU=-1.56793
    g70: GeomPoint X=-109.666 Y=18.0598 Z=0
    g71: GeomPoint X=-109.677 Y=21.9902 Z=0
    g72: Ellipse CenterX=-109.671 CenterY=20.0123 CenterZ=0 NormalX=0 NormalY=0 NormalZ=1 MajorRadius=6.93002 MinorRadius=6.36273 AngleXU=-3.13976
    g73: GeomPoint X=-112.417 Y=20.0073 Z=0
    g74: GeomPoint X=-106.925 Y=20.0173 Z=0
    g75: Ellipse CenterX=-51.7682 CenterY=20.1463 CenterZ=0 NormalX=0 NormalY=0 NormalZ=1 MajorRadius=3.19279 MinorRadius=2.71052 AngleXU=-1.52774
    g76: GeomPoint X=-51.6955 Y=18.4606 Z=0
    g77: GeomPoint X=-51.8408 Y=21.832 Z=0
    g78: GeomPoint X=-54.5142 Y=20.1413 Z=0
    g79: GeomPoint X=-49.0221 Y=20.1513 Z=0
    g80: Ellipse CenterX=-51.7682 CenterY=20.1463 CenterZ=0 NormalX=0 NormalY=0 NormalZ=1 MajorRadius=6.93002 MinorRadius=6.36273 AngleXU=-3.13976
    g81: Ellipse CenterX=-22.8436 CenterY=20.1783 CenterZ=0 NormalX=0 NormalY=0 NormalZ=1 MajorRadius=3.31512 MinorRadius=2.71052 AngleXU=-1.60214
    g82: GeomPoint X=-22.9034 Y=18.2706 Z=0
    g83: GeomPoint X=-22.7838 Y=22.0861 Z=0
    g84: GeomPoint X=-25.5897 Y=20.1733 Z=0
    g85: GeomPoint X=-20.0976 Y=20.1833 Z=0
    g86: Ellipse CenterX=-22.8436 CenterY=20.1783 CenterZ=0 NormalX=0 NormalY=0 NormalZ=1 MajorRadius=6.93002 MinorRadius=6.36273 AngleXU=-3.13976
    g87: LineSegment StartX=-101.889 StartY=14.1107 StartZ=0 EndX=-97.7455 EndY=14.1107 EndZ=0
    g88: LineSegment StartX=-93.8155 StartY=14.1107 StartZ=0 EndX=-89.6755 EndY=14.1107 EndZ=0
    g89: LineSegment StartX=-85.7455 StartY=14.1107 StartZ=0 EndX=-81.6055 EndY=14.1107 EndZ=0
    g90: LineSegment StartX=-101.889 StartY=14.1107 StartZ=0 EndX=-101.889 EndY=25.9907 EndZ=0
    g91: LineSegment StartX=-101.889 StartY=25.9907 StartZ=0 EndX=-97.8594 EndY=25.9907 EndZ=0
    g92: LineSegment StartX=-97.8594 StartY=25.9907 StartZ=0 EndX=-97.8594 EndY=24.0907 EndZ=0
    g93: LineSegment StartX=-97.7455 StartY=14.1107 StartZ=0 EndX=-97.7455 EndY=19.9107 EndZ=0
    g94: LineSegment StartX=-89.6755 StartY=14.1107 StartZ=0 EndX=-89.6755 EndY=19.9107 EndZ=0
    g95: LineSegment StartX=-93.8155 StartY=14.1107 StartZ=0 EndX=-93.8155 EndY=21.0107 EndZ=0
    g96-g106: Circle x11 (B-spline internal-alignment scaffolding for g107; pole/knot coordinates omitted)
    g107: BSplineCurve PolesCount=11 KnotsCount=9 Degree=3 IsPeriodic=0
    g108-g116: GeomPoint x9 (B-spline internal-alignment scaffolding for g107; pole/knot coordinates omitted)
    g117: BSplineCurve PolesCount=11 KnotsCount=9 Degree=3 IsPeriodic=0
    g118-g125: Circle x8 (B-spline internal-alignment scaffolding for g126; pole/knot coordinates omitted)
    g126: BSplineCurve PolesCount=8 KnotsCount=6 Degree=3 IsPeriodic=0
    g127-g132: GeomPoint x6 (B-spline internal-alignment scaffolding for g126; pole/knot coordinates omitted)
    g133: BSplineCurve PolesCount=8 KnotsCount=6 Degree=3 IsPeriodic=0
    g134: LineSegment StartX=-85.7455 StartY=21.0107 StartZ=0 EndX=-85.7455 EndY=14.1107 EndZ=0
    g135: LineSegment StartX=-80.0879 StartY=14.1107 StartZ=0 EndX=-75.944 EndY=14.1107 EndZ=0
    g136: LineSegment StartX=-72.014 StartY=14.1107 StartZ=0 EndX=-67.874 EndY=14.1107 EndZ=0
    g137: LineSegment StartX=-63.944 StartY=14.1107 StartZ=0 EndX=-59.804 EndY=14.1107 EndZ=0
    g138: LineSegment StartX=-80.0879 StartY=14.1107 StartZ=0 EndX=-80.0879 EndY=25.9907 EndZ=0
    g139: LineSegment StartX=-80.0879 StartY=25.9907 StartZ=0 EndX=-76.0579 EndY=25.9907 EndZ=0
    g140: LineSegment StartX=-76.0579 StartY=25.9907 StartZ=0 EndX=-76.0579 EndY=24.0907 EndZ=0
    g141: LineSegment StartX=-75.944 StartY=14.1107 StartZ=0 EndX=-75.944 EndY=19.9107 EndZ=0
    g142: LineSegment StartX=-67.874 StartY=14.1107 StartZ=0 EndX=-67.874 EndY=19.9107 EndZ=0
    g143: LineSegment StartX=-72.014 StartY=14.1107 StartZ=0 EndX=-72.014 EndY=21.0107 EndZ=0
    g144-g148: Circle x5 (B-spline internal-alignment scaffolding for g149; pole/knot coordinates omitted)
    g149: BSplineCurve PolesCount=11 KnotsCount=9 Degree=3 IsPeriodic=0
    g150-g158: GeomPoint x9 (B-spline internal-alignment scaffolding for g149; pole/knot coordinates omitted)
    g159: BSplineCurve PolesCount=11 KnotsCount=9 Degree=3 IsPeriodic=0
    g160-g167: Circle x8 (B-spline internal-alignment scaffolding for g168; pole/knot coordinates omitted)
    g168: BSplineCurve PolesCount=8 KnotsCount=6 Degree=3 IsPeriodic=0
    g169-g174: GeomPoint x6 (B-spline internal-alignment scaffolding for g168; pole/knot coordinates omitted)
    g175: BSplineCurve PolesCount=8 KnotsCount=6 Degree=3 IsPeriodic=0
    g176: LineSegment StartX=-63.944 StartY=21.0107 StartZ=0 EndX=-63.944 EndY=14.1107 EndZ=0
    g177: LineSegment StartX=-59.804 StartY=14.1107 StartZ=0 EndX=-59.804 EndY=21.5868 EndZ=0
    g178: BSplineCurve PolesCount=4 KnotsCount=2 Degree=3 IsPeriodic=0
    g179: GeomPoint X=-59.804 Y=21.5868 Z=0
    g180: GeomPoint X=-60.2379 Y=24.0907 Z=0
    g181: LineSegment StartX=-81.6055 StartY=14.1107 StartZ=0 EndX=-81.6055 EndY=21.5868 EndZ=0
    g182: LineSegment StartX=-151.619 StartY=24.0313 StartZ=0 EndX=-145.128 EndY=24.0313 EndZ=0
    g183: Circle CenterX=-82.0394 CenterY=24.0907 CenterZ=0 NormalX=0 NormalY=0 NormalZ=1 AngleXU=0 Radius=1
    g184: Circle CenterX=-81.7131 CenterY=23.2736 CenterZ=0 NormalX=0 NormalY=0 NormalZ=1 AngleXU=0 Radius=1
    g185: Circle CenterX=-81.6055 CenterY=21.5868 CenterZ=0 NormalX=0 NormalY=0 NormalZ=1 AngleXU=0 Radius=1
    g186: BSplineCurve PolesCount=3 KnotsCount=2 Degree=2 IsPeriodic=0
    g187: GeomPoint X=-82.0394 Y=24.0907 Z=0
    g188: GeomPoint X=-81.6055 Y=21.5868 Z=0
    g189: Ellipse CenterX=-37.3522 CenterY=19.9515 CenterZ=0 NormalX=0 NormalY=0 NormalZ=1 MajorRadius=2.99755 MinorRadius=2.49 AngleXU=1.5708
    g190: GeomPoint X=-37.3522 Y=21.6203 Z=0
    g191: GeomPoint X=-37.3522 Y=18.2826 Z=0
    g192: ArcOfEllipse CenterX=-38.7647 CenterY=20.06 CenterZ=0 NormalX=0 NormalY=0 NormalZ=1 MajorRadius=6.30025 MinorRadius=5.3849 AngleXU=1.57276 StartAngle=5.50632 EndAngle=10.3035
    g193: GeomPoint X=-38.7711 Y=23.3304 Z=0
    g194: GeomPoint X=-38.7583 Y=16.7895 Z=0
    g195: LineSegment StartX=-34.6109 StartY=14.1107 StartZ=0 EndX=-30.8984 EndY=14.1107 EndZ=0
    g196: LineSegment StartX=-30.8984 StartY=14.1107 StartZ=0 EndX=-30.8984 EndY=31.1784 EndZ=0
    g197: LineSegment StartX=-30.8984 StartY=31.1784 StartZ=0 EndX=-34.9984 EndY=31.1784 EndZ=0
    g198: LineSegment StartX=-34.9984 StartY=24.5602 StartZ=0 EndX=-34.9984 EndY=31.1784 EndZ=0
    g199: LineSegment StartX=-34.6109 StartY=16.0476 StartZ=0 EndX=-34.6109 EndY=14.1107 EndZ=0
    g200: LineSegment StartX=-14.8781 StartY=14.1107 StartZ=0 EndX=-10.5106 EndY=14.1107 EndZ=0
    g201: LineSegment StartX=-14.8781 StartY=14.1107 StartZ=0 EndX=-14.8781 EndY=25.8504 EndZ=0
    g202: LineSegment StartX=-14.8781 StartY=25.8504 StartZ=0 EndX=-10.8534 EndY=25.8504 EndZ=0
    g203: LineSegment StartX=-10.8534 StartY=25.8504 StartZ=0 EndX=-10.8534 EndY=24.0923 EndZ=0
    g204: LineSegment StartX=-10.5106 StartY=14.1107 StartZ=0 EndX=-10.5106 EndY=19.7752 EndZ=0
    g205: LineSegment StartX=-5.96397 StartY=25.9304 StartZ=0 EndX=-5.96397 EndY=22.574 EndZ=0
    g206-g214: Circle x9 (B-spline internal-alignment scaffolding for g215; pole/knot coordinates omitted)
    g215: BSplineCurve PolesCount=9 KnotsCount=7 Degree=3 IsPeriodic=0
    g216-g222: GeomPoint x7 (B-spline internal-alignment scaffolding for g215; pole/knot coordinates omitted)
    g223-g232: Circle x10 (B-spline internal-alignment scaffolding for g233; pole/knot coordinates omitted)
    g233: BSplineCurve PolesCount=10 KnotsCount=8 Degree=3 IsPeriodic=0
    g234-g241: GeomPoint x8 (B-spline internal-alignment scaffolding for g233; pole/knot coordinates omitted)
    g242: LineSegment StartX=-1.58923 StartY=21.0696 StartZ=0 EndX=2.62034 EndY=21.0696 EndZ=0
    g243: LineSegment StartX=-1.55856 StartY=18.7342 StartZ=0 EndX=6.45946 EndY=18.7342 EndZ=0
    g244: LineSegment StartX=5.29231 StartY=17.386 StartZ=0 EndX=5.29231 EndY=14.3674 EndZ=0
    g245-g269: Circle x25 (B-spline internal-alignment scaffolding for g270; pole/knot coordinates omitted)
    g270: BSplineCurve PolesCount=25 KnotsCount=23 Degree=3 IsPeriodic=0
    g271-g293: GeomPoint x23 (B-spline internal-alignment scaffolding for g270; pole/knot coordinates omitted)
    g294-g304: Circle x11 (B-spline internal-alignment scaffolding for g305; pole/knot coordinates omitted)
    g305: BSplineCurve PolesCount=11 KnotsCount=9 Degree=3 IsPeriodic=0
    g306-g314: GeomPoint x9 (B-spline internal-alignment scaffolding for g305; pole/knot coordinates omitted)
    g315-g326: Circle x12 (B-spline internal-alignment scaffolding for g327; pole/knot coordinates omitted)
    g327: BSplineCurve PolesCount=12 KnotsCount=10 Degree=3 IsPeriodic=0
    g328-g337: GeomPoint x10 (B-spline internal-alignment scaffolding for g327; pole/knot coordinates omitted)
  constraints (252):
    c: Coincident(g1,g0)
    c: Horizontal(g0)
    c: Vertical(g1)
    c: Coincident(g2,g3)
    c: Coincident(g3,g4)
    c: Horizontal(g4)
    c: Horizontal(g2)
    c: Vertical(g3)
    c: Block(g1)
    c: Distance(g3) = 4.86
    c: Block(g4)
    c: Distance(g0) = 10.8
    c: Distance(g2) = 10.8
    c: Coincident(g5,g0)
    c: Coincident(g6,g4)
    c: Coincident(g6,g2)
    c: Block(g8)
    c: Block(g7)
    c: Coincident(g9,g8)
    c: Coincident(g9,g7)
    c: Vertical(g9)
    c: Coincident(g10,g7)
    c: Coincident(g10,g8)
    c: Vertical(g10)
    c: Weight(g11) = 1
    c: Equal(g11, g12-g21) x10
    c: InternalAlignment(g11-g21 -> g22) x11
    c: InternalAlignment(g23-g31 -> g22) x9
    c: Block(g22)
    c: Weight(g32) = 1
    c: Equal(g32, g33-g49) x17
    c: InternalAlignment(g32-g49 -> g50) x18
    c: InternalAlignment(g51-g66 -> g50) x16
    c: Block(g50)
    c: Coincident(g67,g50)
    c: Coincident(g67,g22)
    c: Coincident(g68,g22)
    c: Coincident(g68,g50)
    c: InternalAlignment(g70,g69)
    c: InternalAlignment(g71,g69)
    c: Block(g69)
    c: InternalAlignment(g73,g72)
    c: InternalAlignment(g74,g72)
    c: Block(g72)
    c: InternalAlignment(g76,g75)
    c: InternalAlignment(g77,g75)
    c: InternalAlignment(g78,g80)
    c: InternalAlignment(g79,g80)
    c: Block(g80)
    c: Coincident(g75,g80)
    c: Block(g75)
    c: InternalAlignment(g82,g81)
    c: InternalAlignment(g83,g81)
    c: InternalAlignment(g84,g86)
    c: InternalAlignment(g85,g86)
    c: Block(g86)
    c: Coincident(g81,g86)
    c: Block(g81)
    c: Horizontal(g87)
    c: Block(g87)
    c: Horizontal(g88)
    c: Distance(g88) = 4.14
    c: Horizontal(g89)
    c: Equal(g88,g89) = 4.14
    c: Block(g89)
    c: Block(g88)
    c: Coincident(g90,g87)
    c: Vertical(g90)
    c: Distance(g90) = 11.88
    c: Coincident(g91,g90)
    c: Horizontal(g91)
    c: Coincident(g92,g91)
    c: Vertical(g92)
    c: Distance(g91) = 4.03
    c: Distance(g92) = 1.9
    c: Coincident(g93,g87)
    c: Vertical(g93)
    c: Vertical(g94)
    c: Coincident(g94,g88)
    c: Distance(g93) = 5.8
    c: Distance(g94) = 5.8
    c: Vertical(g95)
    c: Coincident(g95,g88)
    c: Distance(g95) = 6.9
    c: Coincident(g107,g92)
    c: Weight(g96) = 1
    c: Equal(g96, g97-g106) x10
    c: InternalAlignment(g96-g106 -> g107) x11
    c: InternalAlignment(g108-g116 -> g107) x9
    c: Block(g107)
    c: Block(g117)
    c: Coincident(g126,g93)
    c: Weight(g118) = 1
    c: Equal(g118, g119-g125) x7
    c: Coincident(g126,g95)
    c: InternalAlignment(g118-g125 -> g126) x8
    c: InternalAlignment(g127-g132 -> g126) x6
    c: Coincident(g133,g94)
    c: Block(g126)
    c: Block(g133)
    c: Coincident(g134,g133)
    c: Coincident(g134,g89)
    c: Vertical(g134)
    c: Horizontal(g135)
    c: Block(g135)
    c: Horizontal(g136)
    c: Equal(g88,g136) = 4.14
    c: Horizontal(g137)
    c: Equal(g136,g137) = 4.14
    c: Block(g137)
    c: Block(g136)
    c: Coincident(g138,g135)
    c: Vertical(g138)
    c: Equal(g90,g138) = 11.88
    c: Coincident(g139,g138)
    c: Horizontal(g139)
    c: Coincident(g140,g139)
    c: Vertical(g140)
    c: Equal(g91,g139) = 4.03
    c: Equal(g92,g140) = 1.9
    c: Coincident(g141,g135)
    c: Vertical(g141)
    c: Vertical(g142)
    c: Coincident(g142,g136)
    c: Equal(g93,g141) = 5.8
    c: Equal(g94,g142) = 5.8
    c: Vertical(g143)
    c: Coincident(g143,g136)
    c: Equal(g95,g143) = 6.9
    c: Coincident(g149,g140)
    c: Equal(g96,g144) = 1
    c: Equal(g144, g145-g148) x4
    c: InternalAlignment(g144-g148 -> g149) x5
    c: InternalAlignment(g150-g158 -> g149) x9
    c: Block(g149)
    c: Block(g159)
    c: Coincident(g168,g141)
    c: Equal(g118,g160) = 1
    c: Equal(g160, g161-g167) x7
    c: Coincident(g168,g143)
    c: InternalAlignment(g160-g167 -> g168) x8
    c: InternalAlignment(g169-g174 -> g168) x6
    c: Coincident(g175,g142)
    c: Block(g168)
    c: Block(g175)
    c: Coincident(g176,g175)
    c: Coincident(g176,g137)
    c: Vertical(g176)
    c: Coincident(g177,g137)
    c: Vertical(g177)
    c: Coincident(g178,g177)
    c: Coincident(g178,g159)
    c: InternalAlignment(g179,g178)
    c: InternalAlignment(g180,g178)
    c: Block(g178)
    c: Vertical(g181)
    c: Coincident(g181,g89)
    c: Block(g5)
    c: Coincident(g182,g1)
    c: Coincident(g182,g5)
    c: Horizontal(g182)
    c: Coincident(g186,g117)
    c: Weight(g183) = 1
    c: Equal(g183,g184)
    c: Equal(g183,g185)
    c: Coincident(g186,g181)
    c: InternalAlignment(g183,g186)
    c: InternalAlignment(g184,g186)
    c: InternalAlignment(g185,g186)
    c: InternalAlignment(g187,g186)
    c: InternalAlignment(g188,g186)
    c: Block(g186)
    c: InternalAlignment(g190,g189)
    c: InternalAlignment(g191,g189)
    c: Block(g189)
    c: InternalAlignment(g193,g192)
    c: InternalAlignment(g194,g192)
    c: Block(g192)
    c: Horizontal(g195)
    c: Block(g195)
    c: Coincident(g196,g195)
    c: Vertical(g196)
    c: Block(g196)
    c: Distance(g195) = 3.71244
    c: Coincident(g197,g196)
    c: Horizontal(g197)
    c: Distance(g197) = 4.1
    c: Coincident(g198,g192)
    c: Coincident(g198,g197)
    c: Vertical(g198)
    c: Block(g198)
    c: Coincident(g199,g192)
    c: Coincident(g199,g195)
    c: Vertical(g199)
    c: Block(g199)
    c: Horizontal(g200)
    c: Block(g200)
    c: Coincident(g201,g200)
    c: Vertical(g201)
    c: Block(g201)
    c: Coincident(g202,g201)
    c: Horizontal(g202)
    c: Block(g202)
    c: Coincident(g203,g202)
    c: Vertical(g203)
    c: Block(g203)
    c: Coincident(g204,g200)
    c: Vertical(g204)
    c: Block(g204)
    c: Coincident(g215,g203)
    c: Weight(g206) = 1
    c: Equal(g206, g207-g214) x8
    c: Coincident(g215,g205)
    c: InternalAlignment(g206-g214 -> g215) x9
    c: InternalAlignment(g216-g222 -> g215) x7
    c: Coincident(g233,g204)
    c: Weight(g223) = 1
    c: Equal(g223, g224-g232) x9
    c: Coincident(g233,g205)
    c: InternalAlignment(g223-g232 -> g233) x10
    c: InternalAlignment(g234-g241 -> g233) x8
    c: Vertical(g205)
    c: Block(g205)
    c: Block(g215)
    c: Block(g233)
    c: Horizontal(g242)
    c: Horizontal(g243)
    c: Block(g242)
    c: Block(g243)
    c: Vertical(g244)
    c: Block(g244)
    c: Coincident(g270,g243)
    c: Weight(g245) = 1
    c: Equal(g245, g246-g269) x24
    c: Coincident(g270,g244)
    c: InternalAlignment(g245-g269 -> g270) x25
    c: InternalAlignment(g271-g293 -> g270) x23
    c: Coincident(g305,g242)
    c: Weight(g294) = 1
    c: Equal(g294, g295-g304) x10
    c: Coincident(g305,g242)
    c: InternalAlignment(g294-g304 -> g305) x11
    c: InternalAlignment(g306-g314 -> g305) x9
    c: Block(g305)
    c: Coincident(g327,g243)
    c: Weight(g315) = 1
    c: Equal(g315, g316-g326) x11
    c: Coincident(g327,g244)
    c: InternalAlignment(g315-g326 -> g327) x12
    c: InternalAlignment(g328-g337 -> g327) x10
    c: Block(g327)
    c: Block(g270)
FEATURE [PartDesign::Body] Body  label="CommodoreLogoAndText"
  Group = -> [Sketch083]
  Origin = -> Origin
FEATURE [Part::Extrusion] Extrude074  label="CommodoreLogoAndText001"
  Base = -> Sketch083
  Dir = (0,0,1)
  DirMode = 2
  FaceMakerClass = Part::FaceMakerBullseye
  LengthFwd = 10
  LengthRev = 0
  Solid = true
  Symmetric = false
FEATURE [Part::FeaturePython] Clone  label="CommodoreLogoAndTextScale"  # Draft clone (typed FeaturePython)
  AttacherType = Attacher::AttachEngine3D
  Fuse = false
  Objects = -> [Extrude074]
  Placement = pos=(111,5.37,-11.6) rot=(0,0,1;0rad)
  Scale = (0.62,0.62,1)
FEATURE [Part::Mirroring] Part__Mirroring  label="CommodoreLogoAndTextScale (Mirror #1)"
  Base = (0,0,0)
  Normal = (1,0,0)
  Placement = pos=(123.576,0,0) rot=(0,0,1;0rad)
  Source = -> Clone
FEATURE [Sketcher::SketchObject] Sketch084
  FullyConstrained = true
  MapMode = 5
  Support = -> [XY_Plane001]
  sketch-geometry (338):
    g0: LineSegment StartX=-151.619 StartY=28.8932 StartZ=0 EndX=-140.819 EndY=28.8932 EndZ=0
    g1: LineSegment StartX=-151.619 StartY=24.0313 StartZ=0 EndX=-151.619 EndY=28.8932 EndZ=0
    g2: LineSegment StartX=-140.819 StartY=17.7713 StartZ=0 EndX=-151.619 EndY=17.7713 EndZ=0
    g3: LineSegment StartX=-151.619 StartY=17.7713 StartZ=0 EndX=-151.619 EndY=22.6313 EndZ=0
    g4: LineSegment StartX=-151.619 StartY=22.6313 StartZ=0 EndX=-145.128 EndY=22.6313 EndZ=0
    g5: LineSegment StartX=-145.128 StartY=24.0313 StartZ=0 EndX=-140.819 EndY=28.8932 EndZ=0
    g6: LineSegment StartX=-145.128 StartY=22.6313 StartZ=0 EndX=-140.819 EndY=17.7713 EndZ=0
    g7: ArcOfCircle CenterX=-155.157 CenterY=23.3323 CenterZ=0 NormalX=0 NormalY=0 NormalZ=1 AngleXU=0 Radius=6.92354 StartAngle=1.03434 EndAngle=5.24885
    g8: ArcOfCircle CenterX=-155.157 CenterY=23.3323 CenterZ=0 NormalX=0 NormalY=0 NormalZ=1 AngleXU=0 Radius=12.6269 StartAngle=1.28675 EndAngle=4.99643
    g9: LineSegment StartX=-151.619 StartY=35.4532 StartZ=0 EndX=-151.619 EndY=29.2832 EndZ=0
    g10: LineSegment StartX=-151.619 StartY=17.3813 StartZ=0 EndX=-151.619 EndY=11.2113 EndZ=0
    g11-g21: Circle x11 (B-spline internal-alignment scaffolding for g22; pole/knot coordinates omitted)
    g22: BSplineCurve PolesCount=11 KnotsCount=9 Degree=3 IsPeriodic=0
    g23-g31: GeomPoint x9 (B-spline internal-alignment scaffolding for g22; pole/knot coordinates omitted)
    g32-g49: Circle x18 (B-spline internal-alignment scaffolding for g50; pole/knot coordinates omitted)
    g50: BSplineCurve PolesCount=18 KnotsCount=16 Degree=3 IsPeriodic=0
    g51-g66: GeomPoint x16 (B-spline internal-alignment scaffolding for g50; pole/knot coordinates omitted)
    g67: LineSegment StartX=-117.124 StartY=30.093 StartZ=0 EndX=-117.603 EndY=26.5272 EndZ=0
    g68: LineSegment StartX=-117.603 StartY=17.8472 StartZ=0 EndX=-117.124 EndY=14.2659 EndZ=0
    g69: Ellipse CenterX=-109.671 CenterY=20.025 CenterZ=0 NormalX=0 NormalY=0 NormalZ=1 MajorRadius=3.34798 MinorRadius=2.71052 AngleXU=-1.56793
    g70: GeomPoint X=-109.666 Y=18.0598 Z=0
    g71: GeomPoint X=-109.677 Y=21.9902 Z=0
    g72: Ellipse CenterX=-109.671 CenterY=20.0123 CenterZ=0 NormalX=0 NormalY=0 NormalZ=1 MajorRadius=6.93002 MinorRadius=6.36273 AngleXU=-3.13976
    g73: GeomPoint X=-112.417 Y=20.0073 Z=0
    g74: GeomPoint X=-106.925 Y=20.0173 Z=0
    g75: Ellipse CenterX=-51.7682 CenterY=20.1463 CenterZ=0 NormalX=0 NormalY=0 NormalZ=1 MajorRadius=3.19279 MinorRadius=2.71052 AngleXU=-1.52774
    g76: GeomPoint X=-51.6955 Y=18.4606 Z=0
    g77: GeomPoint X=-51.8408 Y=21.832 Z=0
    g78: GeomPoint X=-54.5142 Y=20.1413 Z=0
    g79: GeomPoint X=-49.0221 Y=20.1513 Z=0
    g80: Ellipse CenterX=-51.7682 CenterY=20.1463 CenterZ=0 NormalX=0 NormalY=0 NormalZ=1 MajorRadius=6.93002 MinorRadius=6.36273 AngleXU=-3.13976
    g81: Ellipse CenterX=-22.8436 CenterY=20.1783 CenterZ=0 NormalX=0 NormalY=0 NormalZ=1 MajorRadius=3.31512 MinorRadius=2.71052 AngleXU=-1.60214
    g82: GeomPoint X=-22.9034 Y=18.2706 Z=0
    g83: GeomPoint X=-22.7838 Y=22.0861 Z=0
    g84: GeomPoint X=-25.5897 Y=20.1733 Z=0
    g85: GeomPoint X=-20.0976 Y=20.1833 Z=0
    g86: Ellipse CenterX=-22.8436 CenterY=20.1783 CenterZ=0 NormalX=0 NormalY=0 NormalZ=1 MajorRadius=6.93002 MinorRadius=6.36273 AngleXU=-3.13976
    g87: LineSegment StartX=-101.889 StartY=14.1107 StartZ=0 EndX=-97.7455 EndY=14.1107 EndZ=0
    g88: LineSegment StartX=-93.8155 StartY=14.1107 StartZ=0 EndX=-89.6755 EndY=14.1107 EndZ=0
    g89: LineSegment StartX=-85.7455 StartY=14.1107 StartZ=0 EndX=-81.6055 EndY=14.1107 EndZ=0
    g90: LineSegment StartX=-101.889 StartY=14.1107 StartZ=0 EndX=-101.889 EndY=25.9907 EndZ=0
    g91: LineSegment StartX=-101.889 StartY=25.9907 StartZ=0 EndX=-97.8594 EndY=25.9907 EndZ=0
    g92: LineSegment StartX=-97.8594 StartY=25.9907 StartZ=0 EndX=-97.8594 EndY=24.0907 EndZ=0
    g93: LineSegment StartX=-97.7455 StartY=14.1107 StartZ=0 EndX=-97.7455 EndY=19.9107 EndZ=0
    g94: LineSegment StartX=-89.6755 StartY=14.1107 StartZ=0 EndX=-89.6755 EndY=19.9107 EndZ=0
    g95: LineSegment StartX=-93.8155 StartY=14.1107 StartZ=0 EndX=-93.8155 EndY=21.0107 EndZ=0
    g96-g106: Circle x11 (B-spline internal-alignment scaffolding for g107; pole/knot coordinates omitted)
    g107: BSplineCurve PolesCount=11 KnotsCount=9 Degree=3 IsPeriodic=0
    g108-g116: GeomPoint x9 (B-spline internal-alignment scaffolding for g107; pole/knot coordinates omitted)
    g117: BSplineCurve PolesCount=11 KnotsCount=9 Degree=3 IsPeriodic=0
    g118-g125: Circle x8 (B-spline internal-alignment scaffolding for g126; pole/knot coordinates omitted)
    g126: BSplineCurve PolesCount=8 KnotsCount=6 Degree=3 IsPeriodic=0
    g127-g132: GeomPoint x6 (B-spline internal-alignment scaffolding for g126; pole/knot coordinates omitted)
    g133: BSplineCurve PolesCount=8 KnotsCount=6 Degree=3 IsPeriodic=0
    g134: LineSegment StartX=-85.7455 StartY=21.0107 StartZ=0 EndX=-85.7455 EndY=14.1107 EndZ=0
    g135: LineSegment StartX=-80.0879 StartY=14.1107 StartZ=0 EndX=-75.944 EndY=14.1107 EndZ=0
    g136: LineSegment StartX=-72.014 StartY=14.1107 StartZ=0 EndX=-67.874 EndY=14.1107 EndZ=0
    g137: LineSegment StartX=-63.944 StartY=14.1107 StartZ=0 EndX=-59.804 EndY=14.1107 EndZ=0
    g138: LineSegment StartX=-80.0879 StartY=14.1107 StartZ=0 EndX=-80.0879 EndY=25.9907 EndZ=0
    g139: LineSegment StartX=-80.0879 StartY=25.9907 StartZ=0 EndX=-76.0579 EndY=25.9907 EndZ=0
    g140: LineSegment StartX=-76.0579 StartY=25.9907 StartZ=0 EndX=-76.0579 EndY=24.0907 EndZ=0
    g141: LineSegment StartX=-75.944 StartY=14.1107 StartZ=0 EndX=-75.944 EndY=19.9107 EndZ=0
    g142: LineSegment StartX=-67.874 StartY=14.1107 StartZ=0 EndX=-67.874 EndY=19.9107 EndZ=0
    g143: LineSegment StartX=-72.014 StartY=14.1107 StartZ=0 EndX=-72.014 EndY=21.0107 EndZ=0
    g144-g148: Circle x5 (B-spline internal-alignment scaffolding for g149; pole/knot coordinates omitted)
    g149: BSplineCurve PolesCount=11 KnotsCount=9 Degree=3 IsPeriodic=0
    g150-g158: GeomPoint x9 (B-spline internal-alignment scaffolding for g149; pole/knot coordinates omitted)
    g159: BSplineCurve PolesCount=11 KnotsCount=9 Degree=3 IsPeriodic=0
    g160-g167: Circle x8 (B-spline internal-alignment scaffolding for g168; pole/knot coordinates omitted)
    g168: BSplineCurve PolesCount=8 KnotsCount=6 Degree=3 IsPeriodic=0
    g169-g174: GeomPoint x6 (B-spline internal-alignment scaffolding for g168; pole/knot coordinates omitted)
    g175: BSplineCurve PolesCount=8 KnotsCount=6 Degree=3 IsPeriodic=0
    g176: LineSegment StartX=-63.944 StartY=21.0107 StartZ=0 EndX=-63.944 EndY=14.1107 EndZ=0
    g177: LineSegment StartX=-59.804 StartY=14.1107 StartZ=0 EndX=-59.804 EndY=21.5868 EndZ=0
    g178: BSplineCurve PolesCount=4 KnotsCount=2 Degree=3 IsPeriodic=0
    g179: GeomPoint X=-59.804 Y=21.5868 Z=0
    g180: GeomPoint X=-60.2379 Y=24.0907 Z=0
    g181: LineSegment StartX=-81.6055 StartY=14.1107 StartZ=0 EndX=-81.6055 EndY=21.5868 EndZ=0
    g182: LineSegment StartX=-151.619 StartY=24.0313 StartZ=0 EndX=-145.128 EndY=24.0313 EndZ=0
    g183: Circle CenterX=-82.0394 CenterY=24.0907 CenterZ=0 NormalX=0 NormalY=0 NormalZ=1 AngleXU=0 Radius=1
    g184: Circle CenterX=-81.7131 CenterY=23.2736 CenterZ=0 NormalX=0 NormalY=0 NormalZ=1 AngleXU=0 Radius=1
    g185: Circle CenterX=-81.6055 CenterY=21.5868 CenterZ=0 NormalX=0 NormalY=0 NormalZ=1 AngleXU=0 Radius=1
    g186: BSplineCurve PolesCount=3 KnotsCount=2 Degree=2 IsPeriodic=0
    g187: GeomPoint X=-82.0394 Y=24.0907 Z=0
    g188: GeomPoint X=-81.6055 Y=21.5868 Z=0
    g189: Ellipse CenterX=-37.3522 CenterY=19.9515 CenterZ=0 NormalX=0 NormalY=0 NormalZ=1 MajorRadius=2.99755 MinorRadius=2.49 AngleXU=1.5708
    g190: GeomPoint X=-37.3522 Y=21.6203 Z=0
    g191: GeomPoint X=-37.3522 Y=18.2826 Z=0
    g192: ArcOfEllipse CenterX=-38.7647 CenterY=20.06 CenterZ=0 NormalX=0 NormalY=0 NormalZ=1 MajorRadius=6.30025 MinorRadius=5.3849 AngleXU=1.57276 StartAngle=5.50632 EndAngle=10.3035
    g193: GeomPoint X=-38.7711 Y=23.3304 Z=0
    g194: GeomPoint X=-38.7583 Y=16.7895 Z=0
    g195: LineSegment StartX=-34.6109 StartY=14.1107 StartZ=0 EndX=-30.8984 EndY=14.1107 EndZ=0
    g196: LineSegment StartX=-30.8984 StartY=14.1107 StartZ=0 EndX=-30.8984 EndY=31.1784 EndZ=0
    g197: LineSegment StartX=-30.8984 StartY=31.1784 StartZ=0 EndX=-34.9984 EndY=31.1784 EndZ=0
    g198: LineSegment StartX=-34.9984 StartY=24.5602 StartZ=0 EndX=-34.9984 EndY=31.1784 EndZ=0
    g199: LineSegment StartX=-34.6109 StartY=16.0476 StartZ=0 EndX=-34.6109 EndY=14.1107 EndZ=0
    g200: LineSegment StartX=-14.8781 StartY=14.1107 StartZ=0 EndX=-10.5106 EndY=14.1107 EndZ=0
    g201: LineSegment StartX=-14.8781 StartY=14.1107 StartZ=0 EndX=-14.8781 EndY=25.8504 EndZ=0
    g202: LineSegment StartX=-14.8781 StartY=25.8504 StartZ=0 EndX=-10.8534 EndY=25.8504 EndZ=0
    g203: LineSegment StartX=-10.8534 StartY=25.8504 StartZ=0 EndX=-10.8534 EndY=24.0923 EndZ=0
    g204: LineSegment StartX=-10.5106 StartY=14.1107 StartZ=0 EndX=-10.5106 EndY=19.7752 EndZ=0
    g205: LineSegment StartX=-5.96397 StartY=25.9304 StartZ=0 EndX=-5.96397 EndY=22.574 EndZ=0
    g206-g214: Circle x9 (B-spline internal-alignment scaffolding for g215; pole/knot coordinates omitted)
    g215: BSplineCurve PolesCount=9 KnotsCount=7 Degree=3 IsPeriodic=0
    g216-g222: GeomPoint x7 (B-spline internal-alignment scaffolding for g215; pole/knot coordinates omitted)
    g223-g232: Circle x10 (B-spline internal-alignment scaffolding for g233; pole/knot coordinates omitted)
    g233: BSplineCurve PolesCount=10 KnotsCount=8 Degree=3 IsPeriodic=0
    g234-g241: GeomPoint x8 (B-spline internal-alignment scaffolding for g233; pole/knot coordinates omitted)
    g242: LineSegment StartX=-1.58923 StartY=21.0696 StartZ=0 EndX=2.62034 EndY=21.0696 EndZ=0
    g243: LineSegment StartX=-1.55856 StartY=18.7342 StartZ=0 EndX=6.45946 EndY=18.7342 EndZ=0
    g244: LineSegment StartX=5.29231 StartY=17.386 StartZ=0 EndX=5.29231 EndY=14.3674 EndZ=0
    g245-g269: Circle x25 (B-spline internal-alignment scaffolding for g270; pole/knot coordinates omitted)
    g270: BSplineCurve PolesCount=25 KnotsCount=23 Degree=3 IsPeriodic=0
    g271-g293: GeomPoint x23 (B-spline internal-alignment scaffolding for g270; pole/knot coordinates omitted)
    g294-g304: Circle x11 (B-spline internal-alignment scaffolding for g305; pole/knot coordinates omitted)
    g305: BSplineCurve PolesCount=11 KnotsCount=9 Degree=3 IsPeriodic=0
    g306-g314: GeomPoint x9 (B-spline internal-alignment scaffolding for g305; pole/knot coordinates omitted)
    g315-g326: Circle x12 (B-spline internal-alignment scaffolding for g327; pole/knot coordinates omitted)
    g327: BSplineCurve PolesCount=12 KnotsCount=10 Degree=3 IsPeriodic=0
    g328-g337: GeomPoint x10 (B-spline internal-alignment scaffolding for g327; pole/knot coordinates omitted)
  constraints (252):
    c: Coincident(g1,g0)
    c: Horizontal(g0)
    c: Vertical(g1)
    c: Coincident(g2,g3)
    c: Coincident(g3,g4)
    c: Horizontal(g4)
    c: Horizontal(g2)
    c: Vertical(g3)
    c: Block(g1)
    c: Distance(g3) = 4.86
    c: Block(g4)
    c: Distance(g0) = 10.8
    c: Distance(g2) = 10.8
    c: Coincident(g5,g0)
    c: Coincident(g6,g4)
    c: Coincident(g6,g2)
    c: Block(g8)
    c: Block(g7)
    c: Coincident(g9,g8)
    c: Coincident(g9,g7)
    c: Vertical(g9)
    c: Coincident(g10,g7)
    c: Coincident(g10,g8)
    c: Vertical(g10)
    c: Weight(g11) = 1
    c: Equal(g11, g12-g21) x10
    c: InternalAlignment(g11-g21 -> g22) x11
    c: InternalAlignment(g23-g31 -> g22) x9
    c: Block(g22)
    c: Weight(g32) = 1
    c: Equal(g32, g33-g49) x17
    c: InternalAlignment(g32-g49 -> g50) x18
    c: InternalAlignment(g51-g66 -> g50) x16
    c: Block(g50)
    c: Coincident(g67,g50)
    c: Coincident(g67,g22)
    c: Coincident(g68,g22)
    c: Coincident(g68,g50)
    c: InternalAlignment(g70,g69)
    c: InternalAlignment(g71,g69)
    c: Block(g69)
    c: InternalAlignment(g73,g72)
    c: InternalAlignment(g74,g72)
    c: Block(g72)
    c: InternalAlignment(g76,g75)
    c: InternalAlignment(g77,g75)
    c: InternalAlignment(g78,g80)
    c: InternalAlignment(g79,g80)
    c: Block(g80)
    c: Coincident(g75,g80)
    c: Block(g75)
    c: InternalAlignment(g82,g81)
    c: InternalAlignment(g83,g81)
    c: InternalAlignment(g84,g86)
    c: InternalAlignment(g85,g86)
    c: Block(g86)
    c: Coincident(g81,g86)
    c: Block(g81)
    c: Horizontal(g87)
    c: Block(g87)
    c: Horizontal(g88)
    c: Distance(g88) = 4.14
    c: Horizontal(g89)
    c: Equal(g88,g89) = 4.14
    c: Block(g89)
    c: Block(g88)
    c: Coincident(g90,g87)
    c: Vertical(g90)
    c: Distance(g90) = 11.88
    c: Coincident(g91,g90)
    c: Horizontal(g91)
    c: Coincident(g92,g91)
    c: Vertical(g92)
    c: Distance(g91) = 4.03
    c: Distance(g92) = 1.9
    c: Coincident(g93,g87)
    c: Vertical(g93)
    c: Vertical(g94)
    c: Coincident(g94,g88)
    c: Distance(g93) = 5.8
    c: Distance(g94) = 5.8
    c: Vertical(g95)
    c: Coincident(g95,g88)
    c: Distance(g95) = 6.9
    c: Coincident(g107,g92)
    c: Weight(g96) = 1
    c: Equal(g96, g97-g106) x10
    c: InternalAlignment(g96-g106 -> g107) x11
    c: InternalAlignment(g108-g116 -> g107) x9
    c: Block(g107)
    c: Block(g117)
    c: Coincident(g126,g93)
    c: Weight(g118) = 1
    c: Equal(g118, g119-g125) x7
    c: Coincident(g126,g95)
    c: InternalAlignment(g118-g125 -> g126) x8
    c: InternalAlignment(g127-g132 -> g126) x6
    c: Coincident(g133,g94)
    c: Block(g126)
    c: Block(g133)
    c: Coincident(g134,g133)
    c: Coincident(g134,g89)
    c: Vertical(g134)
    c: Horizontal(g135)
    c: Block(g135)
    c: Horizontal(g136)
    c: Equal(g88,g136) = 4.14
    c: Horizontal(g137)
    c: Equal(g136,g137) = 4.14
    c: Block(g137)
    c: Block(g136)
    c: Coincident(g138,g135)
    c: Vertical(g138)
    c: Equal(g90,g138) = 11.88
    c: Coincident(g139,g138)
    c: Horizontal(g139)
    c: Coincident(g140,g139)
    c: Vertical(g140)
    c: Equal(g91,g139) = 4.03
    c: Equal(g92,g140) = 1.9
    c: Coincident(g141,g135)
    c: Vertical(g141)
    c: Vertical(g142)
    c: Coincident(g142,g136)
    c: Equal(g93,g141) = 5.8
    c: Equal(g94,g142) = 5.8
    c: Vertical(g143)
    c: Coincident(g143,g136)
    c: Equal(g95,g143) = 6.9
    c: Coincident(g149,g140)
    c: Equal(g96,g144) = 1
    c: Equal(g144, g145-g148) x4
    c: InternalAlignment(g144-g148 -> g149) x5
    c: InternalAlignment(g150-g158 -> g149) x9
    c: Block(g149)
    c: Block(g159)
    c: Coincident(g168,g141)
    c: Equal(g118,g160) = 1
    c: Equal(g160, g161-g167) x7
    c: Coincident(g168,g143)
    c: InternalAlignment(g160-g167 -> g168) x8
    c: InternalAlignment(g169-g174 -> g168) x6
    c: Coincident(g175,g142)
    c: Block(g168)
    c: Block(g175)
    c: Coincident(g176,g175)
    c: Coincident(g176,g137)
    c: Vertical(g176)
    c: Coincident(g177,g137)
    c: Vertical(g177)
    c: Coincident(g178,g177)
    c: Coincident(g178,g159)
    c: InternalAlignment(g179,g178)
    c: InternalAlignment(g180,g178)
    c: Block(g178)
    c: Vertical(g181)
    c: Coincident(g181,g89)
    c: Block(g5)
    c: Coincident(g182,g1)
    c: Coincident(g182,g5)
    c: Horizontal(g182)
    c: Coincident(g186,g117)
    c: Weight(g183) = 1
    c: Equal(g183,g184)
    c: Equal(g183,g185)
    c: Coincident(g186,g181)
    c: InternalAlignment(g183,g186)
    c: InternalAlignment(g184,g186)
    c: InternalAlignment(g185,g186)
    c: InternalAlignment(g187,g186)
    c: InternalAlignment(g188,g186)
    c: Block(g186)
    c: InternalAlignment(g190,g189)
    c: InternalAlignment(g191,g189)
    c: Block(g189)
    c: InternalAlignment(g193,g192)
    c: InternalAlignment(g194,g192)
    c: Block(g192)
    c: Horizontal(g195)
    c: Block(g195)
    c: Coincident(g196,g195)
    c: Vertical(g196)
    c: Block(g196)
    c: Distance(g195) = 3.71244
    c: Coincident(g197,g196)
    c: Horizontal(g197)
    c: Distance(g197) = 4.1
    c: Coincident(g198,g192)
    c: Coincident(g198,g197)
    c: Vertical(g198)
    c: Block(g198)
    c: Coincident(g199,g192)
    c: Coincident(g199,g195)
    c: Vertical(g199)
    c: Block(g199)
    c: Horizontal(g200)
    c: Block(g200)
    c: Coincident(g201,g200)
    c: Vertical(g201)
    c: Block(g201)
    c: Coincident(g202,g201)
    c: Horizontal(g202)
    c: Block(g202)
    c: Coincident(g203,g202)
    c: Vertical(g203)
    c: Block(g203)
    c: Coincident(g204,g200)
    c: Vertical(g204)
    c: Block(g204)
    c: Coincident(g215,g203)
    c: Weight(g206) = 1
    c: Equal(g206, g207-g214) x8
    c: Coincident(g215,g205)
    c: InternalAlignment(g206-g214 -> g215) x9
    c: InternalAlignment(g216-g222 -> g215) x7
    c: Coincident(g233,g204)
    c: Weight(g223) = 1
    c: Equal(g223, g224-g232) x9
    c: Coincident(g233,g205)
    c: InternalAlignment(g223-g232 -> g233) x10
    c: InternalAlignment(g234-g241 -> g233) x8
    c: Vertical(g205)
    c: Block(g205)
    c: Block(g215)
    c: Block(g233)
    c: Horizontal(g242)
    c: Horizontal(g243)
    c: Block(g242)
    c: Block(g243)
    c: Vertical(g244)
    c: Block(g244)
    c: Coincident(g270,g243)
    c: Weight(g245) = 1
    c: Equal(g245, g246-g269) x24
    c: Coincident(g270,g244)
    c: InternalAlignment(g245-g269 -> g270) x25
    c: InternalAlignment(g271-g293 -> g270) x23
    c: Coincident(g305,g242)
    c: Weight(g294) = 1
    c: Equal(g294, g295-g304) x10
    c: Coincident(g305,g242)
    c: InternalAlignment(g294-g304 -> g305) x11
    c: InternalAlignment(g306-g314 -> g305) x9
    c: Block(g305)
    c: Coincident(g327,g243)
    c: Weight(g315) = 1
    c: Equal(g315, g316-g326) x11
    c: Coincident(g327,g244)
    c: InternalAlignment(g315-g326 -> g327) x12
    c: InternalAlignment(g328-g337 -> g327) x10
    c: Block(g327)
    c: Block(g270)
FEATURE [Part::Extrusion] Extrude075  label="CommodoreLogoAndText002"
  Base = -> Sketch084
  Dir = (0,0,1)
  DirMode = 2
  FaceMakerClass = Part::FaceMakerBullseye
  LengthFwd = 10
  LengthRev = 0
  Solid = true
  Symmetric = false
FEATURE [Part::FeaturePython] Clone001  label="CommodoreLogoAndTextScale001"  # Draft clone (typed FeaturePython)
  AttacherType = Attacher::AttachEngine3D
  Fuse = false
  Objects = -> [Extrude075]
  Placement = pos=(112.566,5.37,73.6) rot=(0,0,1;0rad)
  Scale = (0.62,0.62,1)
FEATURE [Part::Cut] Cut073  label="sideA005"
  Base = -> Extrude002
  Tool = -> Part__Mirroring
FEATURE [Part::Cut] Cut074  label="sideB005"
  Base = -> Extrude028
  Tool = -> Clone001
